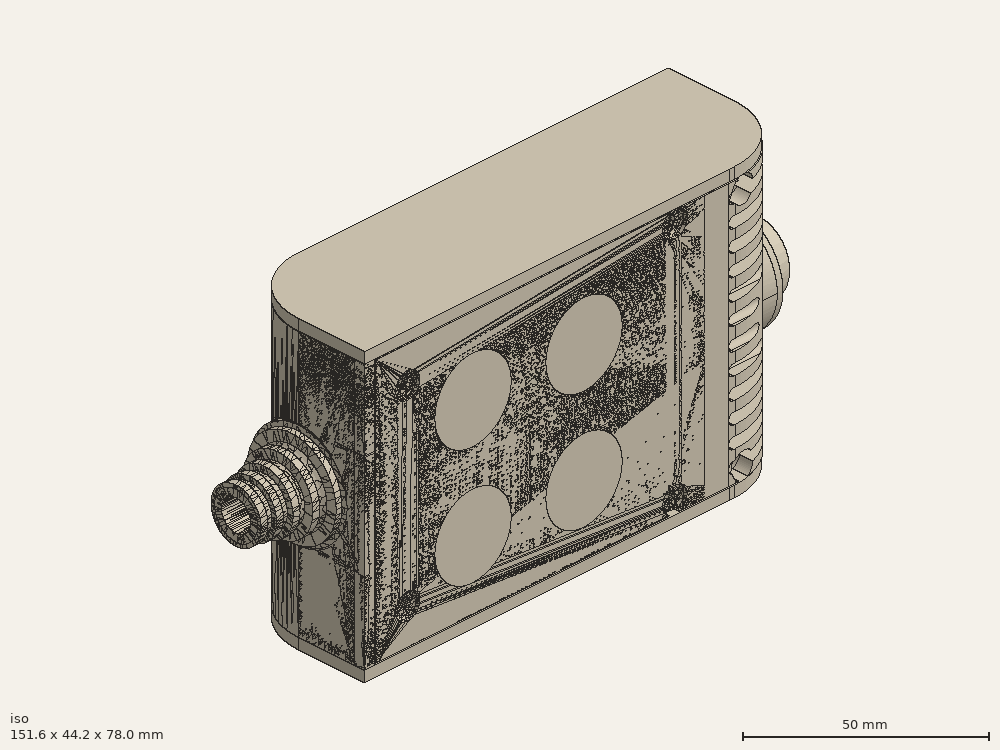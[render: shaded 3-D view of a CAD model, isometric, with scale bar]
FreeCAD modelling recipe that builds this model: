
FCSTD DOCUMENT  (FreeCAD 0.19R0.19.2)
Label: enclosure_200FCStd
License: All rights reserved
LicenseURL: http://en.wikipedia.org/wiki/All_rights_reserved
objects: Part::Revolution×152, Part::MultiFuse×146, Part::Feature×146, Sketcher::SketchObject×84, Part::Cut×70, Part::Cylinder×70, Part::Extrusion×67, Part::Fillet×58, Part::Box×36, App::MeasureDistance×4, PartDesign::Body×2, Image::ImagePlane×1
note: 831 computed .brp shape members not serialized (recipe doc carries the construction recipe); baked Part::Feature solids carry a one-line shape summary decoded from their .brp

FEATURE [Sketcher::SketchObject] Sketch  label="topSketch"
  FullyConstrained = true
  sketch-geometry (20):
    g0: LineSegment StartX=5.21097e-06 StartY=3 StartZ=0 EndX=5.21097e-06 EndY=19 EndZ=0
    g1: ArcOfCircle CenterX=19 CenterY=19 CenterZ=0 NormalX=0 NormalY=0 NormalZ=1 AngleXU=0 Radius=19 StartAngle=1.5708 EndAngle=3.14159
    g2: ArcOfCircle CenterX=19 CenterY=19 CenterZ=0 NormalX=0 NormalY=0 NormalZ=1 AngleXU=0 Radius=16 StartAngle=1.5708 EndAngle=3.14159
    g3: LineSegment StartX=114 StartY=35 StartZ=0 EndX=19 EndY=35 EndZ=0
    g4: LineSegment StartX=5.21097e-06 StartY=3 StartZ=0 EndX=5.21097e-06 EndY=0 EndZ=0
    g5: LineSegment StartX=3 StartY=0 StartZ=0 EndX=5.21097e-06 EndY=0 EndZ=0
    g6: LineSegment StartX=3 StartY=19 StartZ=0 EndX=3 EndY=0 EndZ=0
    g7: LineSegment StartX=19 StartY=38 StartZ=0 EndX=124 EndY=38 EndZ=0
    g8: Circle CenterX=119 CenterY=35 CenterZ=0 NormalX=0 NormalY=0 NormalZ=1 AngleXU=0 Radius=1
    g9: Circle CenterX=121 CenterY=35 CenterZ=0 NormalX=0 NormalY=0 NormalZ=1 AngleXU=0 Radius=1
    g10: Circle CenterX=121 CenterY=33 CenterZ=0 NormalX=0 NormalY=0 NormalZ=1 AngleXU=0 Radius=1
    g11: BSplineCurve PolesCount=3 KnotsCount=2 Degree=2 IsPeriodic=0
    g12: GeomPoint X=119 Y=35 Z=0
    g13: GeomPoint X=121 Y=33 Z=0
    g14: LineSegment StartX=119 StartY=35 StartZ=0 EndX=114 EndY=35 EndZ=0
    g15: ArcOfCircle CenterX=105 CenterY=19 CenterZ=0 NormalX=0 NormalY=0 NormalZ=1 AngleXU=0 Radius=19 StartAngle=5.7297 EndAngle=6.28319
    g16: ArcOfCircle CenterX=105 CenterY=19 CenterZ=0 NormalX=0 NormalY=0 NormalZ=1 AngleXU=0 Radius=16 StartAngle=5.60905 EndAngle=6.28319
    g17: LineSegment StartX=121 StartY=33 StartZ=0 EndX=121 EndY=19 EndZ=0
    g18: LineSegment StartX=124 StartY=38 StartZ=0 EndX=124 EndY=19 EndZ=0
    g19: LineSegment StartX=117.5 StartY=9.01251 StartZ=0 EndX=121.163 EndY=9.0125 EndZ=0
  constraints (46):
    c: Vertical(g0)
    c: Block(g0)
    c: Coincident(g1,g0)
    c: Block(g1)
    c: Coincident(g2,g1)
    c: Block(g2)
    c: Coincident(g3,g2)
    c: Horizontal(g3)
    c: Tangent(g3,g2)
    c: Coincident(g4,g0)
    c: Distance(g4) = 3
    c: Vertical(g4)
    c: Coincident(g5,g4)
    c: Horizontal(g5)
    c: Coincident(g6,g2)
    c: Coincident(g6,g5)
    c: Vertical(g6)
    c: Horizontal(g7)
    c: Distance(g7) = 105
    c: Coincident(g7,g1)
    c: Block(g3)
    c: Weight(g8) = 1
    c: Equal(g8,g9)
    c: Equal(g8,g10)
    c: InternalAlignment(g8,g11)
    c: InternalAlignment(g9,g11)
    c: InternalAlignment(g10,g11)
    c: InternalAlignment(g12,g11)
    c: InternalAlignment(g13,g11)
    c: Block(g11)
    c: Coincident(g14,g11)
    c: Coincident(g14,g3)
    c: Horizontal(g14)
    c: Block(g15)
    c: Coincident(g16,g15)
    c: Block(g16)
    c: Coincident(g17,g11)
    c: Coincident(g17,g16)
    c: Vertical(g17)
    c: Distance(g17) = 14
    c: Coincident(g18,g7)
    c: Coincident(g18,g15)
    c: Vertical(g18)
    c: Distance(g18) = 19
    c: Coincident(g19,g16)
    c: Coincident(g19,g15)
FEATURE [Sketcher::SketchObject] Sketch001  label="bottomSketch"
  FullyConstrained = true
  sketch-geometry (32):
    g0: LineSegment StartX=3.3 StartY=-6.03275e-07 StartZ=0 EndX=98 EndY=-6.03275e-07 EndZ=0
    g1: ArcOfCircle CenterX=98 CenterY=19 CenterZ=0 NormalX=0 NormalY=0 NormalZ=1 AngleXU=0 Radius=19 StartAngle=4.71239 EndAngle=5.71103
    g2: LineSegment StartX=6.3 StartY=8 StartZ=0 EndX=3.3 EndY=8 EndZ=0
    g3: LineSegment StartX=3.3 StartY=8 StartZ=0 EndX=3.3 EndY=-6.03275e-07 EndZ=0
    g4: ArcOfCircle CenterX=8.3 CenterY=5 CenterZ=0 NormalX=0 NormalY=0 NormalZ=1 AngleXU=0 Radius=2 StartAngle=3.14159 EndAngle=4.71239
    g5: LineSegment StartX=6.3 StartY=8 StartZ=0 EndX=6.3 EndY=5 EndZ=0
    g6: ArcOfCircle CenterX=98 CenterY=19 CenterZ=0 NormalX=0 NormalY=0 NormalZ=1 AngleXU=0 Radius=12.7 StartAngle=4.71239 EndAngle=6.28319
    g7: LineSegment StartX=94.7 StartY=3 StartZ=0 EndX=8.3 EndY=3 EndZ=0
    g8-g12: Circle x5 (B-spline internal-alignment scaffolding for g13; pole/knot coordinates omitted)
    g13: BSplineCurve PolesCount=5 KnotsCount=3 Degree=3 IsPeriodic=0
    g14: GeomPoint X=98 Y=6.3 Z=0
    g15: GeomPoint X=96.3938 Y=4.71946 Z=0
    g16: GeomPoint X=94.7 Y=3 Z=0
    g17-g23: Circle x7 (B-spline internal-alignment scaffolding for g24; pole/knot coordinates omitted)
    g24: BSplineCurve PolesCount=7 KnotsCount=5 Degree=3 IsPeriodic=0
    g25-g29: GeomPoint x5 (B-spline internal-alignment scaffolding for g24; pole/knot coordinates omitted)
    g30: ArcOfCircle CenterX=98 CenterY=19 CenterZ=0 NormalX=0 NormalY=0 NormalZ=1 AngleXU=0 Radius=15.7 StartAngle=5.81226 EndAngle=6.28319
    g31: LineSegment StartX=110.7 StartY=19 StartZ=0 EndX=113.7 EndY=19 EndZ=0
  constraints (41):
    c: Horizontal(g0)
    c: Coincident(g1,g0)
    c: Block(g1)
    c: Horizontal(g2)
    c: Distance(g2) = 3
    c: Coincident(g3,g2)
    c: Vertical(g3)
    c: Coincident(g3,g0)
    c: Block(g4)
    c: Block(g2)
    c: Coincident(g5,g2)
    c: Coincident(g5,g4)
    c: Vertical(g5)
    c: Coincident(g6,g1)
    c: Block(g6)
    c: Coincident(g7,g4)
    c: Horizontal(g7)
    c: Block(g0)
    c: Block(g7)
    c: Block(g3)
    c: Coincident(g13,g6)
    c: Weight(g8) = 1
    c: Equal(g8, g9-g12) x4
    c: Coincident(g13,g7)
    c: InternalAlignment(g8-g12 -> g13) x5
    c: InternalAlignment(g14,g13)
    c: InternalAlignment(g15,g13)
    c: InternalAlignment(g16,g13)
    c: Block(g13)
    c: Weight(g17) = 1
    c: Equal(g17, g18-g23) x6
    c: Coincident(g24,g1)
    c: InternalAlignment(g17-g23 -> g24) x7
    c: InternalAlignment(g25-g29 -> g24) x5
    c: Block(g24)
    c: Coincident(g30,g24)
    c: Coincident(g31,g6)
    c: Coincident(g31,g30)
    c: Horizontal(g31)
    c: Block(g31)
    c: Block(g30)
FEATURE [Part::Extrusion] Extrude  label="top"
  Base = -> Sketch
  Dir = (0,0,1)
  DirMode = 2
  FaceMakerClass = Part::FaceMakerBullseye
  LengthFwd = 72
  LengthRev = 0
  Solid = true
  Symmetric = false
FEATURE [Part::Extrusion] Extrude001  label="bottom"
  Base = -> Sketch001
  Dir = (0,0,1)
  DirMode = 2
  FaceMakerClass = Part::FaceMakerBullseye
  LengthFwd = 71.4
  LengthRev = 0
  Placement = pos=(0,0,0.3) rot=(0,0,1;0rad)
  Solid = true
  Symmetric = false
FEATURE [Sketcher::SketchObject] Sketch002  label="topSketch001"
  FullyConstrained = true
  sketch-geometry (8):
    g0: ArcOfCircle CenterX=19 CenterY=19.0975 CenterZ=0 NormalX=0 NormalY=0 NormalZ=1 AngleXU=0 Radius=18.9025 StartAngle=1.5708 EndAngle=3.14674
    g1: LineSegment StartX=0.0977805 StartY=19.0003 StartZ=0 EndX=0.0977805 EndY=0.000251602 EndZ=0
    g2: LineSegment StartX=19 StartY=38 StartZ=0 EndX=124 EndY=38 EndZ=0
    g3: LineSegment StartX=0.0977805 StartY=0.000251602 StartZ=0 EndX=105.098 EndY=0.000251602 EndZ=0
    g4: LineSegment StartX=124 StartY=38 StartZ=0 EndX=125.616 EndY=38 EndZ=0
    g5: LineSegment StartX=105.098 StartY=0.000251602 StartZ=0 EndX=106.713 EndY=0.000251602 EndZ=0
    g6: ArcOfCircle CenterX=106.616 CenterY=19 CenterZ=0 NormalX=0 NormalY=0 NormalZ=1 AngleXU=0 Radius=19 StartAngle=4.71754 EndAngle=6.28319
    g7: LineSegment StartX=125.616 StartY=38 StartZ=0 EndX=125.616 EndY=19 EndZ=0
  constraints (21):
    c: Block(g0)
    c: Coincident(g1,g0)
    c: Vertical(g1)
    c: Horizontal(g2)
    c: Distance(g2) = 105
    c: Coincident(g2,g0)
    c: Distance(g1) = 19
    c: Coincident(g3,g1)
    c: Horizontal(g3)
    c: Distance(g3) = 105
    c: Coincident(g4,g2)
    c: Horizontal(g4)
    c: Distance(g4) = 1.61553
    c: Horizontal(g5)
    c: Equal(g4,g5) = 1.61553
    c: Coincident(g5,g3)
    c: Block(g6)
    c: Coincident(g6,g5)
    c: Coincident(g7,g4)
    c: Coincident(g7,g6)
    c: Vertical(g7)
FEATURE [Part::Extrusion] Extrude002  label="sideA"
  Base = -> Sketch002
  Dir = (0,0,1)
  DirMode = 2
  FaceMakerClass = Part::FaceMakerBullseye
  LengthFwd = 3
  LengthRev = 0
  Placement = pos=(0,0,-3) rot=(0,0,1;0rad)
  Solid = true
  Symmetric = false
FEATURE [Sketcher::SketchObject] Sketch003  label="topSketch002"
  FullyConstrained = true
  sketch-geometry (6):
    g0: LineSegment StartX=19 StartY=38 StartZ=0 EndX=117 EndY=38 EndZ=0
    g1: ArcOfCircle CenterX=19 CenterY=19 CenterZ=0 NormalX=0 NormalY=0 NormalZ=1 AngleXU=0 Radius=19 StartAngle=1.5708 EndAngle=3.14159
    g2: LineSegment StartX=117 StartY=38 StartZ=0 EndX=117 EndY=19 EndZ=0
    g3: LineSegment StartX=98 StartY=1.0161e-12 StartZ=0 EndX=5.22862e-06 EndY=1.0161e-12 EndZ=0
    g4: LineSegment StartX=5.22862e-06 StartY=19 StartZ=0 EndX=5.22862e-06 EndY=1.0161e-12 EndZ=0
    g5: ArcOfCircle CenterX=98 CenterY=19 CenterZ=0 NormalX=0 NormalY=0 NormalZ=1 AngleXU=0 Radius=19 StartAngle=4.71239 EndAngle=6.28319
  constraints (16):
    c: Horizontal(g0)
    c: Distance(g0) = 98
    c: Coincident(g1,g0)
    c: Block(g1)
    c: Coincident(g2,g0)
    c: Vertical(g2)
    c: Distance(g2) = 19
    c: Horizontal(g3)
    c: Coincident(g4,g1)
    c: Vertical(g4)
    c: Coincident(g3,g4)
    c: Block(g3)
    c: Coincident(g5,g2)
    c: Coincident(g5,g3)
    c: Block(g0)
    c: Block(g5)
FEATURE [Sketcher::SketchObject] Sketch004
  FullyConstrained = true
  MapMode = 3
  Placement = pos=(0,0,0) rot=(1,0,0;1.5708rad)
  Support = -> [Extrude]
  sketch-geometry (8):
    g0: Circle CenterX=80.351 CenterY=-67.6202 CenterZ=0 NormalX=0 NormalY=0 NormalZ=1 AngleXU=0 Radius=2
    g1: Circle CenterX=80.351 CenterY=-67.6202 CenterZ=0 NormalX=0 NormalY=0 NormalZ=1 AngleXU=0 Radius=3
    g2: Circle CenterX=80.351 CenterY=-4.92017 CenterZ=0 NormalX=0 NormalY=0 NormalZ=1 AngleXU=0 Radius=2
    g3: Circle CenterX=80.351 CenterY=-4.92017 CenterZ=0 NormalX=0 NormalY=0 NormalZ=1 AngleXU=0 Radius=3
    g4: Circle CenterX=23.851 CenterY=-4.92017 CenterZ=0 NormalX=0 NormalY=0 NormalZ=1 AngleXU=0 Radius=2
    g5: Circle CenterX=23.851 CenterY=-4.92017 CenterZ=0 NormalX=0 NormalY=0 NormalZ=1 AngleXU=0 Radius=3
    g6: Circle CenterX=23.851 CenterY=-67.6202 CenterZ=0 NormalX=0 NormalY=0 NormalZ=1 AngleXU=0 Radius=2
    g7: Circle CenterX=23.851 CenterY=-67.6202 CenterZ=0 NormalX=0 NormalY=0 NormalZ=1 AngleXU=0 Radius=3
  constraints (8):
    c: Block(g3)
    c: Block(g2)
    c: Block(g1)
    c: Block(g0)
    c: Block(g6)
    c: Block(g7)
    c: Block(g4)
    c: Block(g5)
FEATURE [Part::Extrusion] Extrude004
  Base = -> Sketch004
  Dir = (0,-1,2e-16)
  DirMode = 2
  FaceMakerClass = Part::FaceMakerBullseye
  LengthFwd = 6
  LengthRev = 0
  Placement = pos=(0,9,0) rot=(0,0,1;0rad)
  Solid = true
  Symmetric = false
FEATURE [Sketcher::SketchObject] Sketch005
  FullyConstrained = true
  MapMode = 3
  Placement = pos=(0,0,0) rot=(1,0,0;1.5708rad)
  Support = -> [Extrude]
  sketch-geometry (8):
    g0: Circle CenterX=80.351 CenterY=-67.6202 CenterZ=0 NormalX=0 NormalY=0 NormalZ=1 AngleXU=0 Radius=3
    g1: Circle CenterX=80.351 CenterY=-4.92017 CenterZ=0 NormalX=0 NormalY=0 NormalZ=1 AngleXU=0 Radius=3
    g2: Circle CenterX=23.851 CenterY=-4.92017 CenterZ=0 NormalX=0 NormalY=0 NormalZ=1 AngleXU=0 Radius=3
    g3: Circle CenterX=23.851 CenterY=-67.6202 CenterZ=0 NormalX=0 NormalY=0 NormalZ=1 AngleXU=0 Radius=3
    g4: Circle CenterX=23.851 CenterY=-67.6202 CenterZ=0 NormalX=0 NormalY=0 NormalZ=1 AngleXU=0 Radius=5
    g5: Circle CenterX=80.351 CenterY=-67.6202 CenterZ=0 NormalX=0 NormalY=0 NormalZ=1 AngleXU=0 Radius=5
    g6: Circle CenterX=23.851 CenterY=-4.92017 CenterZ=0 NormalX=0 NormalY=0 NormalZ=1 AngleXU=0 Radius=5
    g7: Circle CenterX=80.351 CenterY=-4.92017 CenterZ=0 NormalX=0 NormalY=0 NormalZ=1 AngleXU=0 Radius=5
  constraints (8):
    c: Block(g1)
    c: Block(g0)
    c: Block(g3)
    c: Block(g2)
    c: Block(g5)
    c: Block(g4)
    c: Block(g6)
    c: Block(g7)
FEATURE [Part::Extrusion] Extrude005
  Base = -> Sketch005
  Dir = (0,-1,2e-16)
  DirMode = 2
  FaceMakerClass = Part::FaceMakerBullseye
  LengthFwd = 2
  LengthRev = 0
  Solid = true
  Symmetric = false
FEATURE [Sketcher::SketchObject] Sketch006
  FullyConstrained = true
  MapMode = 3
  Placement = pos=(0,0,0) rot=(1,0,0;1.5708rad)
  sketch-geometry (8):
    g0: Circle CenterX=80.351 CenterY=-67.6202 CenterZ=0 NormalX=0 NormalY=0 NormalZ=1 AngleXU=0 Radius=3
    g1: Circle CenterX=80.351 CenterY=-4.92017 CenterZ=0 NormalX=0 NormalY=0 NormalZ=1 AngleXU=0 Radius=3
    g2: Circle CenterX=23.851 CenterY=-4.92017 CenterZ=0 NormalX=0 NormalY=0 NormalZ=1 AngleXU=0 Radius=3
    g3: Circle CenterX=23.851 CenterY=-67.6202 CenterZ=0 NormalX=0 NormalY=0 NormalZ=1 AngleXU=0 Radius=3
    g4: Circle CenterX=23.851 CenterY=-67.6202 CenterZ=0 NormalX=0 NormalY=0 NormalZ=1 AngleXU=0 Radius=5
    g5: Circle CenterX=80.351 CenterY=-67.6202 CenterZ=0 NormalX=0 NormalY=0 NormalZ=1 AngleXU=0 Radius=5
    g6: Circle CenterX=23.851 CenterY=-4.92017 CenterZ=0 NormalX=0 NormalY=0 NormalZ=1 AngleXU=0 Radius=5
    g7: Circle CenterX=80.351 CenterY=-4.92017 CenterZ=0 NormalX=0 NormalY=0 NormalZ=1 AngleXU=0 Radius=5
  constraints (8):
    c: Block(g1)
    c: Block(g0)
    c: Block(g3)
    c: Block(g2)
    c: Block(g5)
    c: Block(g4)
    c: Block(g6)
    c: Block(g7)
FEATURE [Part::Extrusion] Extrude007
  Base = -> Sketch006
  Dir = (0,-1,2e-16)
  DirMode = 2
  FaceMakerClass = Part::FaceMakerBullseye
  LengthFwd = 2
  LengthRev = 0
  Solid = true
  Symmetric = false
FEATURE [Part::Fillet] Fillet
  Base = -> Extrude007
  Edges = 4 edges r=1.99: [Edge6,Edge12,Edge18,Edge24]
FEATURE [Part::Cut] Cut
  Base = -> Extrude005
  Placement = pos=(0,5,0) rot=(0,0,1;0rad)
  Tool = -> Fillet
FEATURE [Part::MultiFuse] Fusion  label="pCBScrews"
  Placement = pos=(-2.5,0,72.3) rot=(0,0,1;0rad)
  Shapes = -> [Extrude004,Cut]
FEATURE [App::MeasureDistance] Distance  label="Distance: 0.69 mm"
  Distance = 0.685967
  P1 = (24.0138,2.9647,0.3)
  P2 = (23.8901,3,-0.373787)
FEATURE [App::MeasureDistance] Distance001  label="Distance: 0.53 mm"
  Distance = 0.533607
  P1 = (80.2939,3,72.2334)
  P2 = (80.281,2.99661,71.7)
FEATURE [Part::Fillet] Fillet001
  Base = -> Extrude001
  Edges = 1 edges r=2.4: [Edge17]
FEATURE [Part::Fillet] Fillet002  label="bottom001"
  Base = -> Fillet001
  Edges = 1 edges r=2.4: [Edge36]
FEATURE [Part::Fillet] Fillet003  label="top001"
  Base = -> Extrude
  Edges = 1 edges r=2: [Edge1]
FEATURE [Sketcher::SketchObject] Sketch007
  FullyConstrained = true
  sketch-geometry (16):
    g0: LineSegment StartX=4 StartY=0 StartZ=0 EndX=4 EndY=2.4 EndZ=0
    g1: LineSegment StartX=4 StartY=2.4 StartZ=0 EndX=7 EndY=2.4 EndZ=0
    g2: LineSegment StartX=4 StartY=0 StartZ=0 EndX=5.7 EndY=0 EndZ=0
    g3: LineSegment StartX=5.7 StartY=0 StartZ=0 EndX=5.7 EndY=-5.6 EndZ=0
    g4-g8: Circle x5 (B-spline internal-alignment scaffolding for g9; pole/knot coordinates omitted)
    g9: BSplineCurve PolesCount=5 KnotsCount=3 Degree=3 IsPeriodic=0
    g10: GeomPoint X=7 Y=2.4 Z=0
    g11: GeomPoint X=10.4582 Y=-1.55472 Z=0
    g12: GeomPoint X=14 Y=-5.6 Z=0
    g13: LineSegment StartX=14 StartY=-5.6 StartZ=0 EndX=14 EndY=-14.1 EndZ=0
    g14: LineSegment StartX=14 StartY=-14.1 StartZ=0 EndX=6.5 EndY=-14.1 EndZ=0
    g15: LineSegment StartX=5.7 StartY=-5.6 StartZ=0 EndX=6.5 EndY=-14.1 EndZ=0
  constraints (28):
    c: Distance(g0) = 2.4
    c: Vertical(g0)
    c: Block(g0)
    c: Coincident(g1,g0)
    c: Horizontal(g1)
    c: Distance(g1) = 3
    c: Coincident(g2,g0)
    c: Horizontal(g2)
    c: Distance(g2) = 1.7
    c: Coincident(g3,g2)
    c: Vertical(g3)
    c: Distance(g3) = 5.6
    c: Coincident(g9,g1)
    c: Weight(g4) = 1
    c: Equal(g4, g5-g8) x4
    c: InternalAlignment(g4-g8 -> g9) x5
    c: InternalAlignment(g10,g9)
    c: InternalAlignment(g11,g9)
    c: InternalAlignment(g12,g9)
    c: Block(g9)
    c: Coincident(g13,g9)
    c: Vertical(g13)
    c: Distance(g13) = 8.5
    c: Coincident(g14,g13)
    c: Horizontal(g14)
    c: Distance(g14) = 7.5
    c: Coincident(g15,g3)
    c: Coincident(g15,g14)
FEATURE [Part::Feature] Face
  shape: bbox 10 x 16.5 x 2e-07 mm, 1 faces, 0 solids (baked)
FEATURE [Part::Revolution] Revolve  label="plugHousing"
  Angle = 360
  Axis = (0,1,0)
  Base = (0,0,0)
  FaceMakerClass = Part::FaceMakerBullseye
  Placement = pos=(0,0,36.15) rot=(0,0,1;0rad)
  Solid = false
  Source = -> Face
  Symmetric = false
FEATURE [Part::Feature] Face001
  shape: bbox 10 x 16.5 x 2e-07 mm, 1 faces, 0 solids (baked)
FEATURE [Part::Revolution] Revolve001  label="plugHousing001"
  Angle = 360
  Axis = (0,1,0)
  Base = (0,0,0)
  FaceMakerClass = Part::FaceMakerBullseye
  Placement = pos=(0,0,36.15) rot=(0,0,1;0rad)
  Solid = false
  Source = -> Face001
  Symmetric = false
FEATURE [Part::MultiFuse] Fusion001  label="plugHousing002"
  Placement = pos=(0,0,0) rot=(0,0,1;1.5708rad)
  Shapes = -> [Revolve001,Revolve]
FEATURE [Part::Feature] Face002
  shape: bbox 10 x 16.5 x 2e-07 mm, 1 faces, 0 solids (baked)
FEATURE [Part::Revolution] Revolve003  label="plugHousing005"
  Angle = 360
  Axis = (0,1,0)
  Base = (0,0,0)
  FaceMakerClass = Part::FaceMakerBullseye
  Placement = pos=(0,0,36.15) rot=(0,0,1;0rad)
  Solid = false
  Source = -> Face002
  Symmetric = false
FEATURE [Part::Feature] Face003
  shape: bbox 10 x 16.5 x 2e-07 mm, 1 faces, 0 solids (baked)
FEATURE [Part::Revolution] Revolve002  label="plugHousing003"
  Angle = 360
  Axis = (0,1,0)
  Base = (0,0,0)
  FaceMakerClass = Part::FaceMakerBullseye
  Placement = pos=(0,0,36.15) rot=(0,0,1;0rad)
  Solid = false
  Source = -> Face003
  Symmetric = false
FEATURE [Part::MultiFuse] Fusion002  label="plugHousing004"
  Placement = pos=(0,0,0) rot=(0,0,1;1.5708rad)
  Shapes = -> [Revolve002,Revolve003]
FEATURE [Part::MultiFuse] Fusion003  label="plugHousing006"
  Placement = pos=(0,19,0) rot=(0,0,1;3.14159rad)
  Shapes = -> [Fusion002,Fusion001]
FEATURE [Part::Feature] Face004
  shape: bbox 10 x 16.5 x 2e-07 mm, 1 faces, 0 solids (baked)
FEATURE [Part::Revolution] Revolve006  label="plugHousing010"
  Angle = 360
  Axis = (0,1,0)
  Base = (0,0,0)
  FaceMakerClass = Part::FaceMakerBullseye
  Placement = pos=(0,0,36.15) rot=(0,0,1;0rad)
  Solid = false
  Source = -> Face004
  Symmetric = false
FEATURE [Part::Feature] Face005
  shape: bbox 10 x 16.5 x 2e-07 mm, 1 faces, 0 solids (baked)
FEATURE [Part::Revolution] Revolve007  label="plugHousing011"
  Angle = 360
  Axis = (0,1,0)
  Base = (0,0,0)
  FaceMakerClass = Part::FaceMakerBullseye
  Placement = pos=(0,0,36.15) rot=(0,0,1;0rad)
  Solid = false
  Source = -> Face005
  Symmetric = false
FEATURE [Part::Feature] Face006
  shape: bbox 10 x 16.5 x 2e-07 mm, 1 faces, 0 solids (baked)
FEATURE [Part::Revolution] Revolve004  label="plugHousing007"
  Angle = 360
  Axis = (0,1,0)
  Base = (0,0,0)
  FaceMakerClass = Part::FaceMakerBullseye
  Placement = pos=(0,0,36.15) rot=(0,0,1;0rad)
  Solid = false
  Source = -> Face006
  Symmetric = false
FEATURE [Part::MultiFuse] Fusion004  label="plugHousing009"
  Placement = pos=(0,0,0) rot=(0,0,1;1.5708rad)
  Shapes = -> [Revolve004,Revolve007]
FEATURE [Part::Feature] Face007
  shape: bbox 10 x 16.5 x 2e-07 mm, 1 faces, 0 solids (baked)
FEATURE [Part::Revolution] Revolve005  label="plugHousing008"
  Angle = 360
  Axis = (0,1,0)
  Base = (0,0,0)
  FaceMakerClass = Part::FaceMakerBullseye
  Placement = pos=(0,0,36.15) rot=(0,0,1;0rad)
  Solid = false
  Source = -> Face007
  Symmetric = false
FEATURE [Part::MultiFuse] Fusion005  label="plugHousing012"
  Placement = pos=(0,0,0) rot=(0,0,1;1.5708rad)
  Shapes = -> [Revolve006,Revolve005]
FEATURE [Part::MultiFuse] Fusion006  label="plugHousing013"
  Placement = pos=(0,19,0) rot=(0,0,1;3.14159rad)
  Shapes = -> [Fusion005,Fusion004]
FEATURE [Part::MultiFuse] Fusion007  label="plugHousing014"
  Placement = pos=(122.621,0,-0.15) rot=(0,0,1;0rad)
  Shapes = -> [Fusion003,Fusion006]
FEATURE [Part::Cylinder] Cylinder002
  Angle = 360
  AttacherType = Attacher::AttachEngine3D
  Height = 20
  Placement = pos=(0,0,36.15) rot=(0,0,1;0rad)
  Radius = 4
FEATURE [Part::Cylinder] Cylinder003
  Angle = 360
  AttacherType = Attacher::AttachEngine3D
  Height = 10
  Placement = pos=(0,0,36.15) rot=(0,0,1;0rad)
  Radius = 4
FEATURE [Part::MultiFuse] Fusion009  label="removeToCreateHoleForPlugHousing"
  Placement = pos=(70,19,36.15) rot=(0,1,0;1.5708rad)
  Shapes = -> [Cylinder002,Cylinder003]
FEATURE [Part::Cylinder] Cylinder004
  Angle = 360
  AttacherType = Attacher::AttachEngine3D
  Height = 20
  Placement = pos=(0,0,36.15) rot=(0,0,1;0rad)
  Radius = 4
FEATURE [Part::Cylinder] Cylinder005
  Angle = 360
  AttacherType = Attacher::AttachEngine3D
  Height = 10
  Placement = pos=(0,0,36.15) rot=(0,0,1;0rad)
  Radius = 4
FEATURE [Part::MultiFuse] Fusion010  label="removeToCreateHoleForPlugHousing001"
  Placement = pos=(70,19,36.15) rot=(0,1,0;1.5708rad)
  Shapes = -> [Cylinder004,Cylinder005]
FEATURE [Part::Cut] Cut001
  Base = -> Fillet003
  Tool = -> Fusion010
FEATURE [Part::Cut] Cut002  label="Bottom"
  Base = -> Fillet002
  Tool = -> Fusion009
FEATURE [Part::Feature] Face008
  shape: bbox 10 x 16.5 x 2e-07 mm, 1 faces, 0 solids (baked)
FEATURE [Part::Revolution] Revolve011  label="plugHousing021"
  Angle = 360
  Axis = (0,1,0)
  Base = (0,0,0)
  FaceMakerClass = Part::FaceMakerBullseye
  Placement = pos=(0,0,36.15) rot=(0,0,1;0rad)
  Solid = false
  Source = -> Face008
  Symmetric = false
FEATURE [Part::Feature] Face009
  shape: bbox 10 x 16.5 x 2e-07 mm, 1 faces, 0 solids (baked)
FEATURE [Part::Revolution] Revolve012  label="plugHousing022"
  Angle = 360
  Axis = (0,1,0)
  Base = (0,0,0)
  FaceMakerClass = Part::FaceMakerBullseye
  Placement = pos=(0,0,36.15) rot=(0,0,1;0rad)
  Solid = false
  Source = -> Face009
  Symmetric = false
FEATURE [Part::Feature] Face010 .. Face013  x4 (patterned run collapsed; names and placements below)
  shape: bbox 10 x 16.5 x 2e-07 mm, 1 faces, 0 solids (baked)
FEATURE [Part::Revolution] Revolve015  label="plugHousing027"
  Angle = 360
  Axis = (0,1,0)
  Base = (0,0,0)
  FaceMakerClass = Part::FaceMakerBullseye
  Placement = pos=(0,0,36.15) rot=(0,0,1;0rad)
  Solid = false
  Source = -> Face013
  Symmetric = false
FEATURE [Part::Feature] Face014
  shape: bbox 10 x 16.5 x 2e-07 mm, 1 faces, 0 solids (baked)
FEATURE [Part::Feature] Face015
  shape: bbox 10 x 16.5 x 2e-07 mm, 1 faces, 0 solids (baked)
FEATURE [Part::Feature] Face016
  shape: bbox 10 x 16.5 x 2e-07 mm, 1 faces, 0 solids (baked)
FEATURE [Part::Revolution] Revolve019  label="plugHousing033"
  Angle = 360
  Axis = (0,1,0)
  Base = (0,0,0)
  FaceMakerClass = Part::FaceMakerBullseye
  Placement = pos=(0,0,36.15) rot=(0,0,1;0rad)
  Solid = false
  Source = -> Face016
  Symmetric = false
FEATURE [Part::Feature] Face017
  shape: bbox 10 x 16.5 x 2e-07 mm, 1 faces, 0 solids (baked)
FEATURE [Part::Revolution] Revolve020  label="plugHousing034"
  Angle = 360
  Axis = (0,1,0)
  Base = (0,0,0)
  FaceMakerClass = Part::FaceMakerBullseye
  Placement = pos=(0,0,36.15) rot=(0,0,1;0rad)
  Solid = false
  Source = -> Face017
  Symmetric = false
FEATURE [Part::Feature] Face018
  shape: bbox 10 x 16.5 x 2e-07 mm, 1 faces, 0 solids (baked)
FEATURE [Part::Revolution] Revolve016  label="plugHousing030"
  Angle = 360
  Axis = (0,1,0)
  Base = (0,0,0)
  FaceMakerClass = Part::FaceMakerBullseye
  Placement = pos=(0,0,36.15) rot=(0,0,1;0rad)
  Solid = false
  Source = -> Face018
  Symmetric = false
FEATURE [Part::MultiFuse] Fusion020  label="plugHousing038"
  Placement = pos=(0,0,0) rot=(0,0,1;1.5708rad)
  Shapes = -> [Revolve016,Revolve020]
FEATURE [Part::Feature] Face019
  shape: bbox 10 x 16.5 x 2e-07 mm, 1 faces, 0 solids (baked)
FEATURE [Part::Feature] Face020
  shape: bbox 10 x 16.5 x 2e-07 mm, 1 faces, 0 solids (baked)
FEATURE [Part::Revolution] Revolve017  label="plugHousing031"
  Angle = 360
  Axis = (0,1,0)
  Base = (0,0,0)
  FaceMakerClass = Part::FaceMakerBullseye
  Placement = pos=(0,0,36.15) rot=(0,0,1;0rad)
  Solid = false
  Source = -> Face020
  Symmetric = false
FEATURE [Part::MultiFuse] Fusion021  label="plugHousing039"
  Placement = pos=(0,0,0) rot=(0,0,1;1.5708rad)
  Shapes = -> [Revolve019,Revolve017]
FEATURE [Part::MultiFuse] Fusion023  label="plugHousing041"
  Placement = pos=(0,19,0) rot=(0,0,1;3.14159rad)
  Shapes = -> [Fusion021,Fusion020]
FEATURE [Part::Revolution] Revolve022  label="plugHousing043"
  Angle = 360
  Axis = (0,1,0)
  Base = (0,0,0)
  FaceMakerClass = Part::FaceMakerBullseye
  Placement = pos=(0,0,36.15) rot=(0,0,1;0rad)
  Solid = false
  Source = -> Face019
  Symmetric = false
FEATURE [Part::Feature] Face021
  shape: bbox 10 x 16.5 x 2e-07 mm, 1 faces, 0 solids (baked)
FEATURE [Part::Revolution] Revolve023  label="plugHousing044"
  Angle = 360
  Axis = (0,1,0)
  Base = (0,0,0)
  FaceMakerClass = Part::FaceMakerBullseye
  Placement = pos=(0,0,36.15) rot=(0,0,1;0rad)
  Solid = false
  Source = -> Face021
  Symmetric = false
FEATURE [Part::Feature] Face022
  shape: bbox 10 x 16.5 x 2e-07 mm, 1 faces, 0 solids (baked)
FEATURE [Part::Revolution] Revolve018  label="plugHousing032"
  Angle = 360
  Axis = (0,1,0)
  Base = (0,0,0)
  FaceMakerClass = Part::FaceMakerBullseye
  Placement = pos=(0,0,36.15) rot=(0,0,1;0rad)
  Solid = false
  Source = -> Face022
  Symmetric = false
FEATURE [Part::MultiFuse] Fusion022  label="plugHousing040"
  Placement = pos=(0,0,0) rot=(0,0,1;1.5708rad)
  Shapes = -> [Revolve018,Revolve023]
FEATURE [Part::Feature] Face023
  shape: bbox 10 x 16.5 x 2e-07 mm, 1 faces, 0 solids (baked)
FEATURE [Part::Revolution] Revolve021  label="plugHousing035"
  Angle = 360
  Axis = (0,1,0)
  Base = (0,0,0)
  FaceMakerClass = Part::FaceMakerBullseye
  Placement = pos=(0,0,36.15) rot=(0,0,1;0rad)
  Solid = false
  Source = -> Face023
  Symmetric = false
FEATURE [Part::MultiFuse] Fusion018  label="plugHousing036"
  Placement = pos=(0,0,0) rot=(0,0,1;1.5708rad)
  Shapes = -> [Revolve022,Revolve021]
FEATURE [Part::MultiFuse] Fusion019  label="plugHousing037"
  Placement = pos=(0,19,0) rot=(0,0,1;3.14159rad)
  Shapes = -> [Fusion018,Fusion022]
FEATURE [Part::MultiFuse] Fusion024  label="plugHousing042"
  Placement = pos=(122.621,0,-0.15) rot=(0,0,1;0rad)
  Shapes = -> [Fusion023,Fusion019]
FEATURE [Part::Cylinder] Cylinder006
  Angle = 360
  AttacherType = Attacher::AttachEngine3D
  Height = 20
  Placement = pos=(0,0,36.15) rot=(0,0,1;0rad)
  Radius = 14.3
FEATURE [Part::Cylinder] Cylinder007
  Angle = 360
  AttacherType = Attacher::AttachEngine3D
  Height = 10
  Placement = pos=(0,0,36.15) rot=(0,0,1;0rad)
  Radius = 4
FEATURE [Part::MultiFuse] Fusion026  label="removeToCreteHoleForPlugHousing"
  Placement = pos=(70,19,36) rot=(0,1,0;1.5708rad)
  Shapes = -> [Cylinder006,Cylinder007]
FEATURE [Part::Box] Box001  label="Cube001"
  AttacherType = Attacher::AttachEngine3D
  Height = 28
  Length = 3
  Placement = pos=(110.7,19,22) rot=(0,0,1;0rad)
  Width = 15.7
FEATURE [Part::Cut] Cut003  label="top002"
  Base = -> Cut001
  Tool = -> Fusion007
FEATURE [Part::Revolution] Revolve008  label="plugHousing015"
  Angle = 360
  Axis = (0,1,0)
  Base = (0,0,0)
  FaceMakerClass = Part::FaceMakerBullseye
  Placement = pos=(0,0,36.15) rot=(0,0,1;0rad)
  Solid = false
  Source = -> Face010
  Symmetric = false
FEATURE [Part::MultiFuse] Fusion013  label="plugHousing020"
  Placement = pos=(0,0,0) rot=(0,0,1;1.5708rad)
  Shapes = -> [Revolve008,Revolve012]
FEATURE [Part::Cut] Cut004  label="top003"
  Base = -> Cut003
  Placement = pos=(1,0,0) rot=(0,0,1;0rad)
  Tool = -> Fusion026
FEATURE [Part::Cylinder] Cylinder008
  Angle = 360
  AttacherType = Attacher::AttachEngine3D
  Height = 20
  Placement = pos=(0,0,36.15) rot=(0,0,1;0rad)
  Radius = 10.3
FEATURE [Part::Cylinder] Cylinder009
  Angle = 360
  AttacherType = Attacher::AttachEngine3D
  Height = 10
  Placement = pos=(0,0,36.15) rot=(0,0,1;0rad)
  Radius = 4
FEATURE [Part::MultiFuse] Fusion027  label="removeToCreteHoleForPlugHousing001"
  Placement = pos=(70,19,36) rot=(0,1,0;1.5708rad)
  Shapes = -> [Cylinder008,Cylinder009]
FEATURE [Part::Cut] Cut005  label="plugHousingTab"
  Base = -> Box001
  Tool = -> Fusion027
FEATURE [Part::MultiFuse] Fusion028  label="plugHousing045"
  Shapes = -> [Fusion024,Cut005]
FEATURE [Part::Box] Box002  label="Cube002"
  AttacherType = Attacher::AttachEngine3D
  Height = 28.8
  Length = 3
  Placement = pos=(107.3,28,21.6) rot=(0,0,1;0rad)
  Width = 7
FEATURE [Part::Box] Box003  label="Cube003"
  AttacherType = Attacher::AttachEngine3D
  Height = 3
  Length = 6.4
  Placement = pos=(107.3,28,18.6) rot=(0,0,1;0rad)
  Width = 7
FEATURE [Part::Box] Box004  label="Cube004"
  AttacherType = Attacher::AttachEngine3D
  Height = 3
  Length = 6.4
  Placement = pos=(107.3,28,50.4) rot=(0,0,1;0rad)
  Width = 7
FEATURE [Part::MultiFuse] Fusion029  label="plugHousingBracketHolder"
  Shapes = -> [Box004,Box002,Box003]
FEATURE [Part::Cylinder] Cylinder010
  Angle = 360
  AttacherType = Attacher::AttachEngine3D
  Height = 20
  Placement = pos=(0,0,36.15) rot=(0,0,1;0rad)
  Radius = 14.3
FEATURE [Part::Cylinder] Cylinder011
  Angle = 360
  AttacherType = Attacher::AttachEngine3D
  Height = 10
  Placement = pos=(0,0,36.15) rot=(0,0,1;0rad)
  Radius = 4
FEATURE [Part::MultiFuse] Fusion030  label="removeToCreteHoleForPlugHousing002"
  Placement = pos=(70,19,36) rot=(0,1,0;1.5708rad)
  Shapes = -> [Cylinder010,Cylinder011]
FEATURE [Part::Cut] Cut006  label="plugHousingBracketHolder001"
  Base = -> Fusion029
  Tool = -> Fusion030
FEATURE [Part::Cylinder] Cylinder012
  Angle = 360
  AttacherType = Attacher::AttachEngine3D
  Height = 20
  Placement = pos=(0,0,36.15) rot=(0,0,1;0rad)
  Radius = 7
FEATURE [Part::Cylinder] Cylinder013
  Angle = 360
  AttacherType = Attacher::AttachEngine3D
  Height = 10
  Placement = pos=(0,0,36.15) rot=(0,0,1;0rad)
  Radius = 4
FEATURE [Part::MultiFuse] Fusion032  label="removeToCreteHoleForPlugHousing003"
  Placement = pos=(70,19,36) rot=(0,1,0;1.5708rad)
  Shapes = -> [Cylinder012,Cylinder013]
FEATURE [Part::Cut] Cut007  label="bottom002"
  Base = -> Cut002
  Tool = -> Fusion032
FEATURE [Sketcher::SketchObject] Sketch008
  FullyConstrained = true
  sketch-geometry (54):
    g0: LineSegment StartX=-4.2 StartY=0 StartZ=0 EndX=-6.2 EndY=0 EndZ=0
    g1: LineSegment StartX=-14 StartY=-18 StartZ=0 EndX=-14 EndY=-26.5 EndZ=0
    g2: LineSegment StartX=-4.2 StartY=0 StartZ=0 EndX=-4.2 EndY=-13.4877 EndZ=0
    g3: Circle CenterX=-4.2 CenterY=-13.4877 CenterZ=0 NormalX=0 NormalY=0 NormalZ=1 AngleXU=0 Radius=1
    g4: Circle CenterX=-4.2 CenterY=-26.5 CenterZ=0 NormalX=0 NormalY=0 NormalZ=1 AngleXU=0 Radius=1
    g5: Circle CenterX=-8.2 CenterY=-26.5 CenterZ=0 NormalX=0 NormalY=0 NormalZ=1 AngleXU=0 Radius=1
    g6: BSplineCurve PolesCount=3 KnotsCount=2 Degree=2 IsPeriodic=0
    g7: GeomPoint X=-4.2 Y=-13.4877 Z=0
    g8: GeomPoint X=-8.2 Y=-26.5 Z=0
    g9: LineSegment StartX=-14 StartY=-26.5 StartZ=0 EndX=-8.2 EndY=-26.5 EndZ=0
    g10: LineSegment StartX=-10.15 StartY=-12 StartZ=0 EndX=-10.15 EndY=-14 EndZ=0
    g11: LineSegment StartX=-12.8401 StartY=-16 StartZ=0 EndX=-10.1571 EndY=-16 EndZ=0
    g12: LineSegment StartX=-10.15 StartY=-14 StartZ=0 EndX=-8.70761 EndY=-14 EndZ=0
    g13: LineSegment StartX=-12.8401 StartY=-16 StartZ=0 EndX=-12.8401 EndY=-17.6958 EndZ=0
    g14: LineSegment StartX=-10.15 StartY=-12 StartZ=0 EndX=-7.79258 EndY=-12 EndZ=0
    g15: Circle CenterX=-6.2215 CenterY=-2 CenterZ=0 NormalX=0 NormalY=0 NormalZ=1 AngleXU=0 Radius=1
    g16: Circle CenterX=-6.22762 CenterY=-2.58724 CenterZ=0 NormalX=0 NormalY=0 NormalZ=1 AngleXU=0 Radius=1
    g17: Circle CenterX=-6.32538 CenterY=-4 CenterZ=0 NormalX=0 NormalY=0 NormalZ=1 AngleXU=0 Radius=1
    g18: BSplineCurve PolesCount=3 KnotsCount=2 Degree=2 IsPeriodic=0
    g19: GeomPoint X=-6.2215 Y=-2 Z=0
    g20: GeomPoint X=-6.32538 Y=-4 Z=0
    g21: Circle CenterX=-6.48644 CenterY=-5.99526 CenterZ=0 NormalX=0 NormalY=0 NormalZ=1 AngleXU=0 Radius=1
    g22: Circle CenterX=-6.58486 CenterY=-6.99526 CenterZ=0 NormalX=0 NormalY=0 NormalZ=1 AngleXU=0 Radius=1
    g23: Circle CenterX=-6.77343 CenterY=-8 CenterZ=0 NormalX=0 NormalY=0 NormalZ=1 AngleXU=0 Radius=1
    g24: BSplineCurve PolesCount=3 KnotsCount=2 Degree=2 IsPeriodic=0
    g25: GeomPoint X=-6.48644 Y=-5.99526 Z=0
    g26: GeomPoint X=-6.77343 Y=-8 Z=0
    g27: Circle CenterX=-7.19003 CenterY=-10 CenterZ=0 NormalX=0 NormalY=0 NormalZ=1 AngleXU=0 Radius=1
    g28: Circle CenterX=-7.44407 CenterY=-11.0915 CenterZ=0 NormalX=0 NormalY=0 NormalZ=1 AngleXU=0 Radius=1
    g29: Circle CenterX=-7.79258 CenterY=-12 CenterZ=0 NormalX=0 NormalY=0 NormalZ=1 AngleXU=0 Radius=1
    g30: BSplineCurve PolesCount=3 KnotsCount=2 Degree=2 IsPeriodic=0
    g31: GeomPoint X=-7.19003 Y=-10 Z=0
    g32: GeomPoint X=-7.79258 Y=-12 Z=0
    g33: Circle CenterX=-8.70761 CenterY=-14 CenterZ=0 NormalX=0 NormalY=0 NormalZ=1 AngleXU=0 Radius=1
    g34: Circle CenterX=-9.33087 CenterY=-15.1837 CenterZ=0 NormalX=0 NormalY=0 NormalZ=1 AngleXU=0 Radius=1
    g35: Circle CenterX=-10.1571 CenterY=-16 CenterZ=0 NormalX=0 NormalY=0 NormalZ=1 AngleXU=0 Radius=1
    g36: BSplineCurve PolesCount=3 KnotsCount=2 Degree=2 IsPeriodic=0
    g37: GeomPoint X=-8.70761 Y=-14 Z=0
    g38: GeomPoint X=-10.1571 Y=-16 Z=0
    g39: Circle CenterX=-12.8401 CenterY=-17.6958 CenterZ=0 NormalX=0 NormalY=0 NormalZ=1 AngleXU=0 Radius=1
    g40: Circle CenterX=-13.3521 CenterY=-17.9027 CenterZ=0 NormalX=0 NormalY=0 NormalZ=1 AngleXU=0 Radius=1
    g41: Circle CenterX=-14 CenterY=-18 CenterZ=0 NormalX=0 NormalY=0 NormalZ=1 AngleXU=0 Radius=1
    g42: BSplineCurve PolesCount=3 KnotsCount=2 Degree=2 IsPeriodic=0
    g43: GeomPoint X=-12.8401 Y=-17.6958 Z=0
    g44: GeomPoint X=-14 Y=-18 Z=0
    g45: LineSegment StartX=-6.2 StartY=0 StartZ=0 EndX=-7.2 EndY=0 EndZ=0
    g46: LineSegment StartX=-7.2 StartY=0 StartZ=0 EndX=-7.2 EndY=-2 EndZ=0
    g47: LineSegment StartX=-7.2 StartY=-2 StartZ=0 EndX=-6.2215 EndY=-2 EndZ=0
    g48: LineSegment StartX=-6.32538 StartY=-4 StartZ=0 EndX=-7.65538 EndY=-4 EndZ=0
    g49: LineSegment StartX=-7.65538 StartY=-4 StartZ=0 EndX=-7.65538 EndY=-5.99526 EndZ=0
    g50: LineSegment StartX=-7.65538 StartY=-5.99526 StartZ=0 EndX=-6.48644 EndY=-5.99526 EndZ=0
    g51: LineSegment StartX=-6.77343 StartY=-8 StartZ=0 EndX=-8.43343 EndY=-8 EndZ=0
    g52: LineSegment StartX=-8.43343 StartY=-8 StartZ=0 EndX=-8.43343 EndY=-10 EndZ=0
    g53: LineSegment StartX=-8.43343 StartY=-10 StartZ=0 EndX=-7.19003 EndY=-10 EndZ=0
  constraints (112):
    c: Horizontal(g0)
    c: Distance(g0) = 2
    c: Block(g0)
    c: Vertical(g1)
    c: Coincident(g2,g0)
    c: Vertical(g2)
    c: Block(g2)
    c: Coincident(g6,g2)
    c: Weight(g3) = 1
    c: Equal(g3,g4)
    c: Equal(g3,g5)
    c: InternalAlignment(g3,g6)
    c: InternalAlignment(g4,g6)
    c: InternalAlignment(g5,g6)
    c: InternalAlignment(g7,g6)
    c: InternalAlignment(g8,g6)
    c: Block(g6)
    c: Coincident(g9,g1)
    c: Coincident(g9,g6)
    c: Horizontal(g9)
    c: Vertical(g10)
    c: Block(g10)
    c: Horizontal(g11)
    c: Block(g11)
    c: Coincident(g12,g10)
    c: Horizontal(g12)
    c: Block(g12)
    c: Coincident(g13,g11)
    c: Vertical(g13)
    c: Block(g13)
    c: Coincident(g14,g10)
    c: Horizontal(g14)
    c: Block(g14)
    c: Block(g9)
    c: Block(g1)
    c: Weight(g15) = 1
    c: Equal(g15,g16)
    c: Equal(g15,g17)
    c: InternalAlignment(g15,g18)
    c: InternalAlignment(g16,g18)
    c: InternalAlignment(g17,g18)
    c: InternalAlignment(g19,g18)
    c: InternalAlignment(g20,g18)
    c: Weight(g21) = 1
    c: Equal(g21,g22)
    c: Equal(g21,g23)
    c: InternalAlignment(g21,g24)
    c: InternalAlignment(g22,g24)
    c: InternalAlignment(g23,g24)
    c: InternalAlignment(g25,g24)
    c: InternalAlignment(g26,g24)
    c: Weight(g27) = 1
    c: Equal(g27,g28)
    c: Equal(g27,g29)
    c: Coincident(g30,g14)
    c: InternalAlignment(g27,g30)
    c: InternalAlignment(g28,g30)
    c: InternalAlignment(g29,g30)
    c: InternalAlignment(g31,g30)
    c: InternalAlignment(g32,g30)
    c: Coincident(g36,g12)
    c: Weight(g33) = 1
    c: Equal(g33,g34)
    c: Equal(g33,g35)
    c: Coincident(g36,g11)
    c: InternalAlignment(g33,g36)
    c: InternalAlignment(g34,g36)
    c: InternalAlignment(g35,g36)
    c: InternalAlignment(g37,g36)
    c: InternalAlignment(g38,g36)
    c: Coincident(g42,g13)
    c: Weight(g39) = 1
    c: Equal(g39,g40)
    c: Equal(g39,g41)
    c: Coincident(g42,g1)
    c: InternalAlignment(g39,g42)
    c: InternalAlignment(g40,g42)
    c: InternalAlignment(g41,g42)
    c: InternalAlignment(g43,g42)
    c: InternalAlignment(g44,g42)
    c: Block(g18)
    c: Block(g24)
    c: Block(g30)
    c: Block(g36)
    c: Block(g42)
    c: Horizontal(g45)
    c: Coincident(g45,g0)
    c: Vertical(g46)
    c: Coincident(g46,g45)
    c: Coincident(g47,g46)
    c: Coincident(g47,g18)
    c: Horizontal(g47)
    c: Block(g46)
    c: Coincident(g48,g18)
    c: Horizontal(g48)
    c: Distance(g48) = 1.33
    c: Vertical(g49)
    c: Coincident(g49,g48)
    c: Coincident(g50,g49)
    c: Coincident(g50,g24)
    c: Horizontal(g50)
    c: Tangent(g50,g22)
    c: Horizontal(g51)
    c: Coincident(g51,g24)
    c: Block(g51)
    c: Vertical(g52)
    c: Block(g52)
    c: Coincident(g52,g51)
    c: Coincident(g53,g52)
    c: Coincident(g53,g30)
    c: Horizontal(g53)
    c: Distance(g1) = 8.5
FEATURE [Part::Feature] Face024
  shape: bbox 9.8 x 26.5 x 2e-07 mm, 1 faces, 0 solids (baked)
FEATURE [Part::Revolution] Revolve024
  Angle = 360
  Axis = (0,1,0)
  Base = (0,0,0)
  FaceMakerClass = Part::FaceMakerBullseye
  Placement = pos=(0,0,0) rot=(0,0,1;1.5708rad)
  Solid = false
  Source = -> Face024
  Symmetric = false
FEATURE [Part::Feature] Face025
  shape: bbox 9.8 x 26.5 x 2e-07 mm, 1 faces, 0 solids (baked)
FEATURE [Part::Revolution] Revolve025
  Angle = 360
  Axis = (0,1,0)
  Base = (0,0,0)
  FaceMakerClass = Part::FaceMakerBullseye
  Placement = pos=(0,0,0) rot=(0,0,1;1.5708rad)
  Solid = false
  Source = -> Face025
  Symmetric = false
FEATURE [Part::MultiFuse] Fusion033
  Placement = pos=(-18,19,36) rot=(0,0,1;0rad)
  Shapes = -> [Revolve025,Revolve024]
FEATURE [Part::Cylinder] Cylinder014
  Angle = 360
  AttacherType = Attacher::AttachEngine3D
  Height = 20
  Placement = pos=(0,0,36.15) rot=(0,0,1;0rad)
  Radius = 14.3
FEATURE [Part::Cylinder] Cylinder015
  Angle = 360
  AttacherType = Attacher::AttachEngine3D
  Height = 10
  Placement = pos=(0,0,36.15) rot=(0,0,1;0rad)
  Radius = 4
FEATURE [Part::MultiFuse] Fusion034  label="removeToCreteHoleForPlugHousing004"
  Placement = pos=(-42,19,36) rot=(0,1,0;1.5708rad)
  Shapes = -> [Cylinder014,Cylinder015]
FEATURE [Part::Cut] Cut008  label="top004"
  Base = -> Cut004
  Placement = pos=(-1,0,0) rot=(0,0,1;0rad)
  Tool = -> Fusion034
FEATURE [Part::Box] Box005  label="Cube005"
  AttacherType = Attacher::AttachEngine3D
  Height = 28
  Length = 3
  Placement = pos=(110.7,19,22) rot=(0,0,1;0rad)
  Width = 15.7
FEATURE [Part::Cylinder] Cylinder016
  Angle = 360
  AttacherType = Attacher::AttachEngine3D
  Height = 10
  Placement = pos=(0,0,36.15) rot=(0,0,1;0rad)
  Radius = 4
FEATURE [Part::Cylinder] Cylinder017
  Angle = 360
  AttacherType = Attacher::AttachEngine3D
  Height = 20
  Placement = pos=(0,0,36.15) rot=(0,0,1;0rad)
  Radius = 10.3
FEATURE [Part::MultiFuse] Fusion035  label="removeToCreteHoleForPlugHousing005"
  Placement = pos=(70,19,36) rot=(0,1,0;1.5708rad)
  Shapes = -> [Cylinder017,Cylinder016]
FEATURE [Part::Cut] Cut009  label="plugHousingTab001"
  Base = -> Box005
  Placement = pos=(-107.4,-14,0) rot=(0,0,1;0rad)
  Tool = -> Fusion035
FEATURE [Part::Box] Box006  label="Cube006"
  AttacherType = Attacher::AttachEngine3D
  Height = 28
  Length = 3
  Placement = pos=(110.7,19,22) rot=(0,0,1;0rad)
  Width = 15.7
FEATURE [Part::Cylinder] Cylinder018
  Angle = 360
  AttacherType = Attacher::AttachEngine3D
  Height = 10
  Placement = pos=(0,0,36.15) rot=(0,0,1;0rad)
  Radius = 4
FEATURE [Part::Cylinder] Cylinder019
  Angle = 360
  AttacherType = Attacher::AttachEngine3D
  Height = 20
  Placement = pos=(0,0,36.15) rot=(0,0,1;0rad)
  Radius = 10.3
FEATURE [Part::MultiFuse] Fusion036  label="removeToCreteHoleForPlugHousing006"
  Placement = pos=(70,19,36) rot=(0,1,0;1.5708rad)
  Shapes = -> [Cylinder019,Cylinder018]
FEATURE [Part::Cut] Cut010  label="plugHousingTab002"
  Base = -> Box006
  Placement = pos=(-107.4,-14,0) rot=(0,0,1;0rad)
  Tool = -> Fusion036
FEATURE [Part::MultiFuse] Fusion037
  Placement = pos=(9.6,23,0) rot=(0,0,1;3.14159rad)
  Shapes = -> [Cut009,Cut010]
FEATURE [Part::Box] Box  label="Cube"
  AttacherType = Attacher::AttachEngine3D
  Height = 10
  Length = 3
  Placement = pos=(3.3,4,12) rot=(0,0,1;0rad)
  Width = 10
FEATURE [Part::Fillet] Fillet004
  Base = -> Fusion028
  Edges = 1 edges r=2: [Edge25]
FEATURE [Part::Fillet] Fillet005  label="plugHousing046"
  Base = -> Fillet004
  Edges = 1 edges r=2: [Edge8]
FEATURE [Part::Fillet] Fillet006
  Base = -> Box
  Edges = 1 edges r=2: [Edge11]
FEATURE [Part::Box] Box007  label="Cube007"
  AttacherType = Attacher::AttachEngine3D
  Height = 10
  Length = 3
  Placement = pos=(3.3,4,50) rot=(0,0,1;0rad)
  Width = 10
FEATURE [Part::Fillet] Fillet007
  Base = -> Box007
  Edges = 1 edges r=2: [Edge12]
FEATURE [Part::Box] Box008  label="Cube008"
  AttacherType = Attacher::AttachEngine3D
  Height = 28
  Length = 4
  Placement = pos=(5,0,22) rot=(0,0,1;0rad)
  Width = 10
FEATURE [Part::Fillet] Fillet008
  Base = -> Box008
  Edges = 1 edges r=1: [Edge7]
FEATURE [Part::Fillet] Fillet009
  Base = -> Fillet008
  Edges = 1 edges r=2: [Edge5]
FEATURE [Part::Fillet] Fillet010
  Base = -> Fillet009
  Edges = 1 edges r=2: [Edge2]
FEATURE [Sketcher::SketchObject] Sketch009  label="topSketch003"
  FullyConstrained = true
  sketch-geometry (4):
    g0: LineSegment StartX=16.8446 StartY=31.512 StartZ=0 EndX=16.3251 EndY=34.4666 EndZ=0
    g1: ArcOfCircle CenterX=19 CenterY=19.2524 CenterZ=0 NormalX=0 NormalY=0 NormalZ=1 AngleXU=0 Radius=15.4476 StartAngle=1.74483 EndAngle=2.72717
    g2: ArcOfCircle CenterX=19 CenterY=19.2524 CenterZ=0 NormalX=0 NormalY=0 NormalZ=1 AngleXU=0 Radius=12.4476 StartAngle=1.74483 EndAngle=2.73189
    g3: LineSegment StartX=4.86004 StartY=25.4725 StartZ=0 EndX=7.58253 EndY=24.2107 EndZ=0
  constraints (7):
    c: Block(g0)
    c: Coincident(g1,g0)
    c: Coincident(g2,g0)
    c: Coincident(g3,g1)
    c: Coincident(g3,g2)
    c: Block(g1)
    c: Block(g2)
FEATURE [Part::Extrusion] Extrude008
  Base = -> Sketch009
  Dir = (0,0,1)
  DirMode = 2
  FaceMakerClass = Part::FaceMakerBullseye
  LengthFwd = 10
  LengthRev = 0
  Placement = pos=(0,0,31) rot=(0,0,1;0rad)
  Solid = true
  Symmetric = false
FEATURE [Part::Cylinder] Cylinder020
  Angle = 360
  AttacherType = Attacher::AttachEngine3D
  Height = 20
  Placement = pos=(0,0,36.15) rot=(0,0,1;0rad)
  Radius = 8.2
FEATURE [Part::Cylinder] Cylinder021
  Angle = 360
  AttacherType = Attacher::AttachEngine3D
  Height = 10
  Placement = pos=(0,0,36.15) rot=(0,0,1;0rad)
  Radius = 4
FEATURE [Part::MultiFuse] Fusion038  label="removeToCreteHoleForPlugHousing007"
  Placement = pos=(-42,19,36) rot=(0,1,0;1.5708rad)
  Shapes = -> [Cylinder020,Cylinder021]
FEATURE [Part::Cut] Cut011
  Base = -> Extrude008
  Tool = -> Fusion038
FEATURE [Part::Fillet] Fillet011
  Base = -> Cut011
  Edges = 1 edges r=2: [Edge1]
FEATURE [Part::Fillet] Fillet012
  Base = -> Fillet011
  Edges = 1 edges r=2.5: [Edge1]
FEATURE [Part::Fillet] Fillet013
  Base = -> Fillet012
  Edges = 1 edges r=2.5: [Edge2]
FEATURE [Part::Box] Box010  label="Cube010"
  AttacherType = Attacher::AttachEngine3D
  Height = 16
  Length = 8
  Placement = pos=(12.7,31.52,28) rot=(0,0,1;0rad)
  Width = 4
FEATURE [Sketcher::SketchObject] Sketch010  label="topSketch004"
  FullyConstrained = true
  sketch-geometry (4):
    g0: LineSegment StartX=16.8446 StartY=31.512 StartZ=0 EndX=16.3251 EndY=34.4666 EndZ=0
    g1: ArcOfCircle CenterX=19 CenterY=19.2524 CenterZ=0 NormalX=0 NormalY=0 NormalZ=1 AngleXU=0 Radius=15.4476 StartAngle=1.74483 EndAngle=2.72717
    g2: ArcOfCircle CenterX=19 CenterY=19.2524 CenterZ=0 NormalX=0 NormalY=0 NormalZ=1 AngleXU=0 Radius=12.4476 StartAngle=1.74483 EndAngle=2.73189
    g3: LineSegment StartX=4.86004 StartY=25.4725 StartZ=0 EndX=7.58253 EndY=24.2107 EndZ=0
  constraints (7):
    c: Block(g0)
    c: Coincident(g1,g0)
    c: Coincident(g2,g0)
    c: Coincident(g3,g1)
    c: Coincident(g3,g2)
    c: Block(g1)
    c: Block(g2)
FEATURE [Part::Cylinder] Cylinder022
  Angle = 360
  AttacherType = Attacher::AttachEngine3D
  Height = 10
  Placement = pos=(0,0,36.15) rot=(0,0,1;0rad)
  Radius = 4
FEATURE [Sketcher::SketchObject] Sketch011  label="topSketch005"
  FullyConstrained = true
  sketch-geometry (4):
    g0: LineSegment StartX=16.8446 StartY=31.512 StartZ=0 EndX=16.3251 EndY=34.4666 EndZ=0
    g1: ArcOfCircle CenterX=19 CenterY=19.2524 CenterZ=0 NormalX=0 NormalY=0 NormalZ=1 AngleXU=0 Radius=15.4476 StartAngle=1.74483 EndAngle=2.72717
    g2: ArcOfCircle CenterX=19 CenterY=19.2524 CenterZ=0 NormalX=0 NormalY=0 NormalZ=1 AngleXU=0 Radius=12.4476 StartAngle=1.74483 EndAngle=2.73189
    g3: LineSegment StartX=4.86004 StartY=25.4725 StartZ=0 EndX=7.58253 EndY=24.2107 EndZ=0
  constraints (7):
    c: Block(g0)
    c: Coincident(g1,g0)
    c: Coincident(g2,g0)
    c: Coincident(g3,g1)
    c: Coincident(g3,g2)
    c: Block(g1)
    c: Block(g2)
FEATURE [Part::Extrusion] Extrude010
  Base = -> Sketch011
  Dir = (0,0,1)
  DirMode = 2
  FaceMakerClass = Part::FaceMakerBullseye
  LengthFwd = 10.6
  LengthRev = 0
  Placement = pos=(0,0,31) rot=(0,0,1;0rad)
  Solid = true
  Symmetric = false
FEATURE [Part::Cylinder] Cylinder023
  Angle = 360
  AttacherType = Attacher::AttachEngine3D
  Height = 20
  Placement = pos=(0,0,36.15) rot=(0,0,1;0rad)
  Radius = 8.2
FEATURE [Part::MultiFuse] Fusion039  label="removeToCreteHoleForPlugHousing008"
  Placement = pos=(-42,19,36) rot=(0,1,0;1.5708rad)
  Shapes = -> [Cylinder023,Cylinder022]
FEATURE [Part::Cut] Cut012
  Base = -> Extrude010
  Placement = pos=(0,0,-0.3) rot=(0,0,1;0rad)
  Tool = -> Fusion039
FEATURE [Part::Cut] Cut013
  Base = -> Box010
  Tool = -> Cut012
FEATURE [Part::Fillet] Fillet014
  Base = -> Cut013
  Edges = 1 edges r=0.7: [Edge13]
FEATURE [Part::Fillet] Fillet015
  Base = -> Fillet014
  Edges = 1 edges r=0.7: [Edge13]
FEATURE [Part::Fillet] Fillet016
  Base = -> Fillet015
  Edges = 1 edges r=0.7: [Edge16]
FEATURE [Part::Fillet] Fillet017
  Base = -> Fillet016
  Edges = 1 edges r=0.7: [Edge11]
FEATURE [Part::Fillet] Fillet018
  Base = -> Fillet017
  Edges = 1 edges r=0.7: [Edge10]
FEATURE [Part::Fillet] Fillet019
  Base = -> Fillet018
  Edges = 1 edges r=1.2: [Edge5]
FEATURE [Part::Fillet] Fillet020
  Base = -> Fillet019
  Edges = 1 edges r=1.2: [Edge12]
FEATURE [Part::Fillet] Fillet021
  Base = -> Fillet020
  Edges = 1 edges r=2: [Edge1]
  Placement = pos=(0.3,0,0) rot=(0,0,1;0rad)
FEATURE [Part::MultiFuse] Fusion040  label="top005"
  Shapes = -> [Cut008,Fillet021]
FEATURE [Part::MultiFuse] Fusion041  label="wireHolder"
  Shapes = -> [Fusion033,Fillet013]
FEATURE [Part::MultiFuse] Fusion042
  Shapes = -> [Fillet007,Fusion041]
FEATURE [Part::MultiFuse] Fusion043  label="wireHolder001"
  Shapes = -> [Fusion042,Fillet010]
FEATURE [Part::MultiFuse] Fusion044  label="wireHolder002"
  Shapes = -> [Fillet006,Fusion037,Fusion043]
FEATURE [Part::Feature] Face026
  shape: bbox 11 x 6 x 2e-07 mm, 1 faces, 0 solids (baked)
FEATURE [Part::Revolution] Revolve026
  Angle = 360
  Axis = (0,1,0)
  Base = (0,0,0)
  FaceMakerClass = Part::FaceMakerBullseye
  Placement = pos=(30.3,-1,19.7) rot=(0,0,1;0rad)
  Solid = false
  Source = -> Face026
  Symmetric = false
FEATURE [Sketcher::SketchObject] Sketch013  label="topSketch006"
  FullyConstrained = true
  sketch-geometry (13):
    g0: LineSegment StartX=117 StartY=19 StartZ=0 EndX=117 EndY=38 EndZ=0
    g1: ArcOfCircle CenterX=98 CenterY=19 CenterZ=0 NormalX=0 NormalY=0 NormalZ=1 AngleXU=0 Radius=19 StartAngle=5.7297 EndAngle=6.28319
    g2: LineSegment StartX=0 StartY=3 StartZ=0 EndX=0 EndY=19 EndZ=0
    g3: LineSegment StartX=19 StartY=38 StartZ=0 EndX=117 EndY=38 EndZ=0
    g4: ArcOfCircle CenterX=19 CenterY=19 CenterZ=0 NormalX=0 NormalY=0 NormalZ=1 AngleXU=0 Radius=19 StartAngle=1.5708 EndAngle=3.14159
    g5: ArcOfCircle CenterX=19 CenterY=19 CenterZ=0 NormalX=0 NormalY=0 NormalZ=1 AngleXU=0 Radius=16 StartAngle=1.5708 EndAngle=3.14159
    g6: ArcOfCircle CenterX=98 CenterY=19 CenterZ=0 NormalX=0 NormalY=0 NormalZ=1 AngleXU=0 Radius=16 StartAngle=5.60905 EndAngle=6.28319
    g7: LineSegment StartX=114 StartY=19 StartZ=0 EndX=114 EndY=35 EndZ=0
    g8: LineSegment StartX=110.5 StartY=9.01251 StartZ=0 EndX=114.163 EndY=9.01251 EndZ=0
    g9: LineSegment StartX=114 StartY=35 StartZ=0 EndX=19 EndY=35 EndZ=0
    g10: LineSegment StartX=0 StartY=3 StartZ=0 EndX=0 EndY=0 EndZ=0
    g11: LineSegment StartX=3 StartY=0 StartZ=0 EndX=0 EndY=0 EndZ=0
    g12: LineSegment StartX=3 StartY=19 StartZ=0 EndX=3 EndY=0 EndZ=0
  constraints (33):
    c: Vertical(g0)
    c: Distance(g0) = 19
    c: Block(g0)
    c: Coincident(g1,g0)
    c: Block(g1)
    c: Vertical(g2)
    c: Block(g2)
    c: Coincident(g3,g0)
    c: Horizontal(g3)
    c: Distance(g3) = 98
    c: Coincident(g4,g3)
    c: Coincident(g4,g2)
    c: Block(g4)
    c: Coincident(g5,g4)
    c: Coincident(g6,g1)
    c: Block(g6)
    c: Block(g5)
    c: Coincident(g7,g6)
    c: Vertical(g7)
    c: Coincident(g8,g6)
    c: Coincident(g8,g1)
    c: Coincident(g9,g7)
    c: Coincident(g9,g5)
    c: Horizontal(g9)
    c: Tangent(g9,g5)
    c: Coincident(g10,g2)
    c: Distance(g10) = 3
    c: Vertical(g10)
    c: Coincident(g11,g10)
    c: Horizontal(g11)
    c: Coincident(g12,g5)
    c: Coincident(g12,g11)
    c: Vertical(g12)
FEATURE [Part::Extrusion] Extrude011  label="top006"
  Base = -> Sketch013
  Dir = (0,0,1)
  DirMode = 2
  FaceMakerClass = Part::FaceMakerBullseye
  LengthFwd = 72
  LengthRev = 0
  Solid = true
  Symmetric = false
FEATURE [Sketcher::SketchObject] Sketch014
  FullyConstrained = true
  MapMode = 3
  Placement = pos=(0,0,0) rot=(1,0,0;1.5708rad)
  Support = -> [Extrude011]
  sketch-geometry (8):
    g0: Circle CenterX=80.351 CenterY=-67.6202 CenterZ=0 NormalX=0 NormalY=0 NormalZ=1 AngleXU=0 Radius=2
    g1: Circle CenterX=80.351 CenterY=-67.6202 CenterZ=0 NormalX=0 NormalY=0 NormalZ=1 AngleXU=0 Radius=3
    g2: Circle CenterX=80.351 CenterY=-4.92017 CenterZ=0 NormalX=0 NormalY=0 NormalZ=1 AngleXU=0 Radius=2
    g3: Circle CenterX=80.351 CenterY=-4.92017 CenterZ=0 NormalX=0 NormalY=0 NormalZ=1 AngleXU=0 Radius=3
    g4: Circle CenterX=23.851 CenterY=-4.92017 CenterZ=0 NormalX=0 NormalY=0 NormalZ=1 AngleXU=0 Radius=2
    g5: Circle CenterX=23.851 CenterY=-4.92017 CenterZ=0 NormalX=0 NormalY=0 NormalZ=1 AngleXU=0 Radius=3
    g6: Circle CenterX=23.851 CenterY=-67.6202 CenterZ=0 NormalX=0 NormalY=0 NormalZ=1 AngleXU=0 Radius=2
    g7: Circle CenterX=23.851 CenterY=-67.6202 CenterZ=0 NormalX=0 NormalY=0 NormalZ=1 AngleXU=0 Radius=3
  constraints (8):
    c: Block(g3)
    c: Block(g2)
    c: Block(g1)
    c: Block(g0)
    c: Block(g6)
    c: Block(g7)
    c: Block(g4)
    c: Block(g5)
FEATURE [Part::Feature] Face027
  shape: bbox 11 x 6 x 2e-07 mm, 1 faces, 0 solids (baked)
FEATURE [Part::Revolution] Revolve027
  Angle = 360
  Axis = (0,1,0)
  Base = (0,0,0)
  FaceMakerClass = Part::FaceMakerBullseye
  Placement = pos=(30.3,-1,51.7) rot=(0,0,1;0rad)
  Solid = false
  Source = -> Face027
  Symmetric = false
FEATURE [Part::Feature] Face028
  shape: bbox 11 x 6 x 2e-07 mm, 1 faces, 0 solids (baked)
FEATURE [Part::Revolution] Revolve028
  Angle = 360
  Axis = (0,1,0)
  Base = (0,0,0)
  FaceMakerClass = Part::FaceMakerBullseye
  Placement = pos=(62.3,-1,19.7) rot=(0,0,1;0rad)
  Solid = false
  Source = -> Face028
  Symmetric = false
FEATURE [Part::Feature] Face029
  shape: bbox 11 x 6 x 2e-07 mm, 1 faces, 0 solids (baked)
FEATURE [Part::Revolution] Revolve029
  Angle = 360
  Axis = (0,1,0)
  Base = (0,0,0)
  FaceMakerClass = Part::FaceMakerBullseye
  Placement = pos=(62.3,-1,51.7) rot=(0,0,1;0rad)
  Solid = false
  Source = -> Face029
  Symmetric = false
FEATURE [Part::Feature] Wire
  shape: bbox 11 x 5.2 x 2e-07 mm, 0 faces, 0 solids (baked)
FEATURE [Part::Revolution] Revolve030
  Angle = 360
  Axis = (0,1,0)
  Base = (0,0,0)
  FaceMakerClass = Part::FaceMakerBullseye
  Placement = pos=(30.3,38,19.7) rot=(0,0,1;0rad)
  Solid = true
  Source = -> Wire
  Symmetric = false
FEATURE [Part::Feature] Wire001
  shape: bbox 11 x 5.2 x 2e-07 mm, 0 faces, 0 solids (baked)
FEATURE [Part::Revolution] Revolve031
  Angle = 360
  Axis = (0,1,0)
  Base = (0,0,0)
  FaceMakerClass = Part::FaceMakerBullseye
  Placement = pos=(30.3,38,51.7) rot=(0,0,1;0rad)
  Solid = true
  Source = -> Wire001
  Symmetric = false
FEATURE [Part::Feature] Wire002
  shape: bbox 11 x 5.2 x 2e-07 mm, 0 faces, 0 solids (baked)
FEATURE [Part::Revolution] Revolve032
  Angle = 360
  Axis = (0,1,0)
  Base = (0,0,0)
  FaceMakerClass = Part::FaceMakerBullseye
  Placement = pos=(62.3,38,51.7) rot=(0,0,1;0rad)
  Solid = true
  Source = -> Wire002
  Symmetric = false
FEATURE [Part::Feature] Wire003
  shape: bbox 11 x 5.2 x 2e-07 mm, 0 faces, 0 solids (baked)
FEATURE [Part::Revolution] Revolve033
  Angle = 360
  Axis = (0,1,0)
  Base = (0,0,0)
  FaceMakerClass = Part::FaceMakerBullseye
  Placement = pos=(62.3,38,19.7) rot=(0,0,1;0rad)
  Solid = true
  Source = -> Wire003
  Symmetric = false
FEATURE [Part::MultiFuse] Fusion045  label="altRandScrewHousing"
  Shapes = -> [Revolve029,Revolve027,Revolve028,Revolve026]
FEATURE [Part::MultiFuse] Fusion046  label="fanScrewHousing"
  Shapes = -> [Revolve033,Revolve032,Revolve031,Revolve030]
FEATURE [Sketcher::SketchObject] Sketch015
  FullyConstrained = true
  sketch-geometry (17):
    g0: Circle CenterX=-3.5 CenterY=23.5 CenterZ=0 NormalX=0 NormalY=0 NormalZ=1 AngleXU=0 Radius=1
    g1: Circle CenterX=-1 CenterY=15.25 CenterZ=0 NormalX=0 NormalY=0 NormalZ=1 AngleXU=0 Radius=1
    g2: Circle CenterX=-3.5 CenterY=7 CenterZ=0 NormalX=0 NormalY=0 NormalZ=1 AngleXU=0 Radius=1
    g3: BSplineCurve PolesCount=3 KnotsCount=2 Degree=2 IsPeriodic=0
    g4: GeomPoint X=-3.5 Y=23.5 Z=0
    g5: GeomPoint X=-3.5 Y=7 Z=0
    g6: Circle CenterX=-4.8 CenterY=30.5 CenterZ=0 NormalX=0 NormalY=0 NormalZ=1 AngleXU=0 Radius=1
    g7: Circle CenterX=-3.5 CenterY=30.5 CenterZ=0 NormalX=0 NormalY=0 NormalZ=1 AngleXU=0 Radius=1
    g8: Circle CenterX=-3.5 CenterY=29.2 CenterZ=0 NormalX=0 NormalY=0 NormalZ=1 AngleXU=0 Radius=1
    g9: BSplineCurve PolesCount=3 KnotsCount=2 Degree=2 IsPeriodic=0
    g10: GeomPoint X=-4.8 Y=30.5 Z=0
    g11: GeomPoint X=-3.5 Y=29.2 Z=0
    g12: LineSegment StartX=-3.5 StartY=29.2 StartZ=0 EndX=-3.5 EndY=23.5 EndZ=0
    g13: LineSegment StartX=-4.8 StartY=30.5 StartZ=0 EndX=0 EndY=30.5 EndZ=0
    g14: LineSegment StartX=-3.5 StartY=0.3 StartZ=0 EndX=0 EndY=0.3 EndZ=0
    g15: LineSegment StartX=-3.5 StartY=0.3 StartZ=0 EndX=-3.5 EndY=7 EndZ=0
    g16: LineSegment StartX=0 StartY=0.3 StartZ=0 EndX=0 EndY=30.5 EndZ=0
  constraints (33):
    c: Weight(g0) = 1
    c: Equal(g0,g1)
    c: Equal(g0,g2)
    c: InternalAlignment(g0,g3)
    c: InternalAlignment(g1,g3)
    c: InternalAlignment(g2,g3)
    c: InternalAlignment(g4,g3)
    c: InternalAlignment(g5,g3)
    c: Block(g3)
    c: Weight(g6) = 1
    c: Equal(g6,g7)
    c: Equal(g6,g8)
    c: InternalAlignment(g6,g9)
    c: InternalAlignment(g7,g9)
    c: InternalAlignment(g8,g9)
    c: InternalAlignment(g10,g9)
    c: InternalAlignment(g11,g9)
    c: Block(g9)
    c: Coincident(g12,g9)
    c: Coincident(g12,g3)
    c: Vertical(g12)
    c: Coincident(g13,g9)
    c: Horizontal(g13)
    c: Distance(g13) = 4.8
    c: Horizontal(g14)
    c: Block(g14)
    c: Coincident(g15,g14)
    c: Coincident(g15,g3)
    c: Vertical(g15)
    c: Coincident(g16,g14)
    c: Coincident(g16,g13)
    c: Vertical(g16)
    c: Tangent(g16,g1)
FEATURE [Sketcher::SketchObject] Sketch016
  FullyConstrained = true
  sketch-geometry (16):
    g0: Circle CenterX=-3.5 CenterY=23.5 CenterZ=0 NormalX=0 NormalY=0 NormalZ=1 AngleXU=0 Radius=1
    g1: Circle CenterX=-1 CenterY=15.25 CenterZ=0 NormalX=0 NormalY=0 NormalZ=1 AngleXU=0 Radius=1
    g2: Circle CenterX=-3.5 CenterY=7 CenterZ=0 NormalX=0 NormalY=0 NormalZ=1 AngleXU=0 Radius=1
    g3: BSplineCurve PolesCount=3 KnotsCount=2 Degree=2 IsPeriodic=0
    g4: GeomPoint X=-3.5 Y=23.5 Z=0
    g5: GeomPoint X=-3.5 Y=7 Z=0
    g6: LineSegment StartX=-3.5 StartY=28.2 StartZ=0 EndX=-3.5 EndY=23.5 EndZ=0
    g7: LineSegment StartX=0 StartY=29.5 StartZ=0 EndX=0 EndY=30 EndZ=0
    g8: LineSegment StartX=-3.5 StartY=28.2 StartZ=0 EndX=-3.5 EndY=30 EndZ=0
    g9: LineSegment StartX=0 StartY=30 StartZ=0 EndX=0 EndY=30.5 EndZ=0
    g10: LineSegment StartX=0 StartY=30.5 StartZ=0 EndX=-3.5 EndY=30.5 EndZ=0
    g11: LineSegment StartX=-3.5 StartY=30.5 StartZ=0 EndX=-3.5 EndY=30 EndZ=0
    g12: LineSegment StartX=0 StartY=29.5 StartZ=0 EndX=0 EndY=5 EndZ=0
    g13: LineSegment StartX=-3.5 StartY=0.3 StartZ=0 EndX=-3.5 EndY=7 EndZ=0
    g14: LineSegment StartX=-3.5 StartY=0.3 StartZ=0 EndX=0 EndY=0.3 EndZ=0
    g15: LineSegment StartX=0 StartY=5 StartZ=0 EndX=0 EndY=0.3 EndZ=0
  constraints (39):
    c: Weight(g0) = 1
    c: Equal(g0,g1)
    c: Equal(g0,g2)
    c: InternalAlignment(g0,g3)
    c: InternalAlignment(g1,g3)
    c: InternalAlignment(g2,g3)
    c: InternalAlignment(g4,g3)
    c: InternalAlignment(g5,g3)
    c: Block(g3)
    c: Coincident(g6,g3)
    c: Vertical(g6)
    c: Vertical(g7)
    c: Distance(g7) = 0.5
    c: Coincident(g8,g6)
    c: Vertical(g8)
    c: Block(g6)
    c: Block(g7)
    c: Vertical(g9)
    c: Equal(g7,g9) = 0.5
    c: Block(g9)
    c: Coincident(g9,g7)
    c: Horizontal(g10)
    c: Coincident(g10,g9)
    c: Coincident(g11,g10)
    c: Coincident(g11,g8)
    c: Vertical(g11)
    c: Block(g11)
    c: Coincident(g12,g7)
    c: Vertical(g12)
    c: Coincident(g13,g3)
    c: Vertical(g13)
    c: Distance(g13) = 6.7
    c: Coincident(g14,g13)
    c: Horizontal(g14)
    c: Block(g14)
    c: Coincident(g15,g12)
    c: Coincident(g15,g14)
    c: Vertical(g15)
    c: Block(g15)
FEATURE [Sketcher::SketchObject] Sketch017
  FullyConstrained = true
  sketch-geometry (11):
    g0: LineSegment StartX=-3.5 StartY=1e-16 StartZ=0 EndX=-1.6 EndY=1e-16 EndZ=0
    g1: LineSegment StartX=-1.6 StartY=1e-16 StartZ=0 EndX=-1.6 EndY=1.5 EndZ=0
    g2: LineSegment StartX=-3.5 StartY=1.5 StartZ=0 EndX=-1.6 EndY=1.5 EndZ=0
    g3: LineSegment StartX=-3.5 StartY=1e-16 StartZ=0 EndX=-4.8 EndY=1e-16 EndZ=0
    g4: Circle CenterX=-3.5 CenterY=1.3 CenterZ=0 NormalX=0 NormalY=0 NormalZ=1 AngleXU=0 Radius=1
    g5: Circle CenterX=-3.5 CenterY=1e-16 CenterZ=0 NormalX=0 NormalY=0 NormalZ=1 AngleXU=0 Radius=1
    g6: Circle CenterX=-4.8 CenterY=1e-16 CenterZ=0 NormalX=0 NormalY=0 NormalZ=1 AngleXU=0 Radius=1
    g7: BSplineCurve PolesCount=3 KnotsCount=2 Degree=2 IsPeriodic=0
    g8: GeomPoint X=-3.5 Y=1.3 Z=0
    g9: GeomPoint X=-4.8 Y=1e-16 Z=0
    g10: LineSegment StartX=-3.5 StartY=1.3 StartZ=0 EndX=-3.5 EndY=1.5 EndZ=0
  constraints (24):
    c: Horizontal(g0)
    c: Distance(g0) = 1.9
    c: Block(g0)
    c: Coincident(g1,g0)
    c: Vertical(g1)
    c: Coincident(g2,g1)
    c: Horizontal(g2)
    c: Coincident(g3,g0)
    c: Horizontal(g3)
    c: Distance(g3) = 1.3
    c: Weight(g4) = 1
    c: Equal(g4,g5)
    c: Coincident(g5,g0)
    c: Equal(g4,g6)
    c: Coincident(g7,g3)
    c: InternalAlignment(g4,g7)
    c: InternalAlignment(g5,g7)
    c: InternalAlignment(g6,g7)
    c: InternalAlignment(g8,g7)
    c: InternalAlignment(g9,g7)
    c: Coincident(g10,g7)
    c: Coincident(g10,g2)
    c: Vertical(g10)
    c: Block(g10)
FEATURE [Part::Feature] Face035
  shape: bbox 3.2 x 1.5 x 2e-07 mm, 1 faces, 0 solids (baked)
FEATURE [Part::Revolution] Revolve039  label="backCaseScrewRetainer"
  Angle = 360
  Axis = (0,1,0)
  Base = (0,0,0)
  FaceMakerClass = Part::FaceMakerBullseye
  Placement = pos=(12.5,3,62) rot=(0,0,1;0rad)
  Solid = false
  Source = -> Face035
  Symmetric = false
FEATURE [Part::Feature] Face036
  shape: bbox 3.2 x 1.5 x 2e-07 mm, 1 faces, 0 solids (baked)
FEATURE [Part::Feature] Face039
  shape: bbox 4.8 x 30.2 x 2e-07 mm, 1 faces, 0 solids (baked)
FEATURE [Part::Revolution] Revolve043  label="frontCaseScrewPost002"
  Angle = 360
  Axis = (0,1,0)
  Base = (0,0,0)
  FaceMakerClass = Part::FaceMakerBullseye
  Placement = pos=(89.5,4.5,3.5) rot=(0,0,1;0rad)
  Solid = false
  Source = -> Face039
  Symmetric = false
FEATURE [Part::Feature] Face042
  shape: bbox 4.8 x 30.2 x 2e-07 mm, 1 faces, 0 solids (baked)
FEATURE [Part::Revolution] Revolve046  label="frontCaseScrewPost003"
  Angle = 360
  Axis = (0,1,0)
  Base = (0,0,0)
  FaceMakerClass = Part::FaceMakerBullseye
  Placement = pos=(89.5,4.5,68.5) rot=(0,0,1;0rad)
  Solid = false
  Source = -> Face042
  Symmetric = false
FEATURE [Part::Feature] Face043
  shape: bbox 3.2 x 1.5 x 2e-07 mm, 1 faces, 0 solids (baked)
FEATURE [Part::Revolution] Revolve047  label="frontCaseScrewRetainer002"
  Angle = 360
  Axis = (0,1,0)
  Base = (0,0,0)
  FaceMakerClass = Part::FaceMakerBullseye
  Placement = pos=(89.5,3,68.5) rot=(0,0,1;0rad)
  Solid = false
  Source = -> Face043
  Symmetric = false
FEATURE [Part::Feature] Face044
  shape: bbox 3.2 x 1.5 x 2e-07 mm, 1 faces, 0 solids (baked)
FEATURE [Part::Revolution] Revolve048  label="frontCaseScrewRetainer003"
  Angle = 360
  Axis = (0,1,0)
  Base = (0,0,0)
  FaceMakerClass = Part::FaceMakerBullseye
  Placement = pos=(89.5,3,3.5) rot=(0,0,1;0rad)
  Solid = false
  Source = -> Face044
  Symmetric = false
FEATURE [App::MeasureDistance] Distance002  label="Distance: 1.67 mm"
  Distance = 1.66921
  P1 = (99.2361,4.7524,71.7)
  P2 = (99.2347,6.42161,71.7)
FEATURE [Sketcher::SketchObject] Sketch018
  FullyConstrained = true
  sketch-geometry (7):
    g0: LineSegment StartX=0 StartY=0 StartZ=0 EndX=0 EndY=6 EndZ=0
    g1: Circle CenterX=0 CenterY=0 CenterZ=0 NormalX=0 NormalY=0 NormalZ=1 AngleXU=0 Radius=1
    g2: Circle CenterX=8 CenterY=6 CenterZ=0 NormalX=0 NormalY=0 NormalZ=1 AngleXU=0 Radius=1
    g3: BSplineCurve PolesCount=3 KnotsCount=2 Degree=2 IsPeriodic=0
    g4: GeomPoint X=0 Y=0 Z=0
    g5: GeomPoint X=8 Y=6 Z=0
    g6: LineSegment StartX=0 StartY=6 StartZ=0 EndX=8 EndY=6 EndZ=0
  constraints (14):
    c: Coincident(g0,g-1)
    c: Distance(g0) = 6
    c: Vertical(g0)
    c: Coincident(g3,g0)
    c: Weight(g1) = 1
    c: Equal(g1,g2)
    c: InternalAlignment(g1,g3)
    c: InternalAlignment(g2,g3)
    c: InternalAlignment(g4,g3)
    c: InternalAlignment(g5,g3)
    c: Block(g3)
    c: Coincident(g6,g0)
    c: Coincident(g6,g3)
    c: Horizontal(g6)
FEATURE [Part::Extrusion] Extrude012  label="caseScrewPillarBracket"
  Base = -> Sketch018
  Dir = (0,0,1)
  DirMode = 2
  FaceMakerClass = Part::FaceMakerBullseye
  LengthFwd = 2.4
  LengthRev = 0
  Placement = pos=(15.76,29,8.8) rot=(0,1,0;0rad)
  Solid = true
  Symmetric = false
FEATURE [Sketcher::SketchObject] Sketch019
  FullyConstrained = true
  sketch-geometry (7):
    g0: LineSegment StartX=0 StartY=0 StartZ=0 EndX=0 EndY=6 EndZ=0
    g1: Circle CenterX=0 CenterY=0 CenterZ=0 NormalX=0 NormalY=0 NormalZ=1 AngleXU=0 Radius=1
    g2: Circle CenterX=8 CenterY=6 CenterZ=0 NormalX=0 NormalY=0 NormalZ=1 AngleXU=0 Radius=1
    g3: BSplineCurve PolesCount=3 KnotsCount=2 Degree=2 IsPeriodic=0
    g4: GeomPoint X=0 Y=0 Z=0
    g5: GeomPoint X=8 Y=6 Z=0
    g6: LineSegment StartX=0 StartY=6 StartZ=0 EndX=8 EndY=6 EndZ=0
  constraints (14):
    c: Coincident(g0,g-1)
    c: Distance(g0) = 6
    c: Vertical(g0)
    c: Coincident(g3,g0)
    c: Weight(g1) = 1
    c: Equal(g1,g2)
    c: InternalAlignment(g1,g3)
    c: InternalAlignment(g2,g3)
    c: InternalAlignment(g4,g3)
    c: InternalAlignment(g5,g3)
    c: Block(g3)
    c: Coincident(g6,g0)
    c: Coincident(g6,g3)
    c: Horizontal(g6)
FEATURE [Part::Extrusion] Extrude013  label="caseScrewPillarBracket001"
  Base = -> Sketch019
  Dir = (0,0,1)
  DirMode = 2
  FaceMakerClass = Part::FaceMakerBullseye
  LengthFwd = 2.4
  LengthRev = 0
  Placement = pos=(15.76,29,60.8) rot=(0,0,1;0rad)
  Solid = true
  Symmetric = false
FEATURE [Sketcher::SketchObject] Sketch020
  FullyConstrained = true
  sketch-geometry (7):
    g0: LineSegment StartX=0 StartY=0 StartZ=0 EndX=0 EndY=6 EndZ=0
    g1: Circle CenterX=0 CenterY=0 CenterZ=0 NormalX=0 NormalY=0 NormalZ=1 AngleXU=0 Radius=1
    g2: Circle CenterX=8 CenterY=6 CenterZ=0 NormalX=0 NormalY=0 NormalZ=1 AngleXU=0 Radius=1
    g3: BSplineCurve PolesCount=3 KnotsCount=2 Degree=2 IsPeriodic=0
    g4: GeomPoint X=0 Y=0 Z=0
    g5: GeomPoint X=8 Y=6 Z=0
    g6: LineSegment StartX=0 StartY=6 StartZ=0 EndX=8 EndY=6 EndZ=0
  constraints (14):
    c: Coincident(g0,g-1)
    c: Distance(g0) = 6
    c: Vertical(g0)
    c: Coincident(g3,g0)
    c: Weight(g1) = 1
    c: Equal(g1,g2)
    c: InternalAlignment(g1,g3)
    c: InternalAlignment(g2,g3)
    c: InternalAlignment(g4,g3)
    c: InternalAlignment(g5,g3)
    c: Block(g3)
    c: Coincident(g6,g0)
    c: Coincident(g6,g3)
    c: Horizontal(g6)
FEATURE [Part::Extrusion] Extrude014  label="caseScrewPillarBracket002"
  Base = -> Sketch020
  Dir = (0,0,1)
  DirMode = 2
  FaceMakerClass = Part::FaceMakerBullseye
  LengthFwd = 2.4
  LengthRev = 0
  Placement = pos=(13.7,29,13.26) rot=(0,-1,0;1.5708rad)
  Solid = true
  Symmetric = false
FEATURE [Sketcher::SketchObject] Sketch021
  FullyConstrained = true
  sketch-geometry (7):
    g0: LineSegment StartX=0 StartY=0 StartZ=0 EndX=0 EndY=6 EndZ=0
    g1: Circle CenterX=0 CenterY=0 CenterZ=0 NormalX=0 NormalY=0 NormalZ=1 AngleXU=0 Radius=1
    g2: Circle CenterX=8 CenterY=6 CenterZ=0 NormalX=0 NormalY=0 NormalZ=1 AngleXU=0 Radius=1
    g3: BSplineCurve PolesCount=3 KnotsCount=2 Degree=2 IsPeriodic=0
    g4: GeomPoint X=0 Y=0 Z=0
    g5: GeomPoint X=8 Y=6 Z=0
    g6: LineSegment StartX=0 StartY=6 StartZ=0 EndX=8 EndY=6 EndZ=0
  constraints (14):
    c: Coincident(g0,g-1)
    c: Distance(g0) = 6
    c: Vertical(g0)
    c: Coincident(g3,g0)
    c: Weight(g1) = 1
    c: Equal(g1,g2)
    c: InternalAlignment(g1,g3)
    c: InternalAlignment(g2,g3)
    c: InternalAlignment(g4,g3)
    c: InternalAlignment(g5,g3)
    c: Block(g3)
    c: Coincident(g6,g0)
    c: Coincident(g6,g3)
    c: Horizontal(g6)
FEATURE [Part::Extrusion] Extrude015  label="caseScrewPillarBracket003"
  Base = -> Sketch021
  Dir = (0,0,1)
  DirMode = 2
  FaceMakerClass = Part::FaceMakerBullseye
  LengthFwd = 2.4
  LengthRev = 0
  Placement = pos=(11.3,29,58.74) rot=(0,1,0;1.5708rad)
  Solid = true
  Symmetric = false
FEATURE [Sketcher::SketchObject] Sketch022
  FullyConstrained = true
  sketch-geometry (7):
    g0: LineSegment StartX=0 StartY=0 StartZ=0 EndX=0 EndY=6 EndZ=0
    g1: Circle CenterX=0 CenterY=0 CenterZ=0 NormalX=0 NormalY=0 NormalZ=1 AngleXU=0 Radius=1
    g2: Circle CenterX=8 CenterY=6 CenterZ=0 NormalX=0 NormalY=0 NormalZ=1 AngleXU=0 Radius=1
    g3: BSplineCurve PolesCount=3 KnotsCount=2 Degree=2 IsPeriodic=0
    g4: GeomPoint X=0 Y=0 Z=0
    g5: GeomPoint X=8 Y=6 Z=0
    g6: LineSegment StartX=0 StartY=6 StartZ=0 EndX=8 EndY=6 EndZ=0
  constraints (14):
    c: Coincident(g0,g-1)
    c: Distance(g0) = 6
    c: Vertical(g0)
    c: Coincident(g3,g0)
    c: Weight(g1) = 1
    c: Equal(g1,g2)
    c: InternalAlignment(g1,g3)
    c: InternalAlignment(g2,g3)
    c: InternalAlignment(g4,g3)
    c: InternalAlignment(g5,g3)
    c: Block(g3)
    c: Coincident(g6,g0)
    c: Coincident(g6,g3)
    c: Horizontal(g6)
FEATURE [Part::Extrusion] Extrude016  label="caseScrewPillarBracket004"
  Base = -> Sketch022
  Dir = (0,0,1)
  DirMode = 2
  FaceMakerClass = Part::FaceMakerBullseye
  LengthFwd = 2.4
  LengthRev = 0
  Placement = pos=(88.3,29,65.23) rot=(0,1,0;1.5708rad)
  Solid = true
  Symmetric = false
FEATURE [Sketcher::SketchObject] Sketch023
  FullyConstrained = true
  sketch-geometry (7):
    g0: LineSegment StartX=0 StartY=0 StartZ=0 EndX=0 EndY=6 EndZ=0
    g1: Circle CenterX=0 CenterY=0 CenterZ=0 NormalX=0 NormalY=0 NormalZ=1 AngleXU=0 Radius=1
    g2: Circle CenterX=8 CenterY=6 CenterZ=0 NormalX=0 NormalY=0 NormalZ=1 AngleXU=0 Radius=1
    g3: BSplineCurve PolesCount=3 KnotsCount=2 Degree=2 IsPeriodic=0
    g4: GeomPoint X=0 Y=0 Z=0
    g5: GeomPoint X=8 Y=6 Z=0
    g6: LineSegment StartX=0 StartY=6 StartZ=0 EndX=8 EndY=6 EndZ=0
  constraints (14):
    c: Coincident(g0,g-1)
    c: Distance(g0) = 6
    c: Vertical(g0)
    c: Coincident(g3,g0)
    c: Weight(g1) = 1
    c: Equal(g1,g2)
    c: InternalAlignment(g1,g3)
    c: InternalAlignment(g2,g3)
    c: InternalAlignment(g4,g3)
    c: InternalAlignment(g5,g3)
    c: Block(g3)
    c: Coincident(g6,g0)
    c: Coincident(g6,g3)
    c: Horizontal(g6)
FEATURE [Part::Extrusion] Extrude017  label="caseScrewPillarBracket005"
  Base = -> Sketch023
  Dir = (0,0,1)
  DirMode = 2
  FaceMakerClass = Part::FaceMakerBullseye
  LengthFwd = 2.4
  LengthRev = 0
  Placement = pos=(90.7,29,6.77) rot=(0,-1,0;1.5708rad)
  Solid = true
  Symmetric = false
FEATURE [Sketcher::SketchObject] Sketch024
  FullyConstrained = true
  sketch-geometry (7):
    g0: LineSegment StartX=0 StartY=0 StartZ=0 EndX=0 EndY=6 EndZ=0
    g1: Circle CenterX=0 CenterY=0 CenterZ=0 NormalX=0 NormalY=0 NormalZ=1 AngleXU=0 Radius=1
    g2: Circle CenterX=8 CenterY=6 CenterZ=0 NormalX=0 NormalY=0 NormalZ=1 AngleXU=0 Radius=1
    g3: BSplineCurve PolesCount=3 KnotsCount=2 Degree=2 IsPeriodic=0
    g4: GeomPoint X=0 Y=0 Z=0
    g5: GeomPoint X=8 Y=6 Z=0
    g6: LineSegment StartX=0 StartY=6 StartZ=0 EndX=8 EndY=6 EndZ=0
  constraints (14):
    c: Coincident(g0,g-1)
    c: Distance(g0) = 6
    c: Vertical(g0)
    c: Coincident(g3,g0)
    c: Weight(g1) = 1
    c: Equal(g1,g2)
    c: InternalAlignment(g1,g3)
    c: InternalAlignment(g2,g3)
    c: InternalAlignment(g4,g3)
    c: InternalAlignment(g5,g3)
    c: Block(g3)
    c: Coincident(g6,g0)
    c: Coincident(g6,g3)
    c: Horizontal(g6)
FEATURE [Part::Extrusion] Extrude018  label="caseScrewPillarBracket006"
  Base = -> Sketch024
  Dir = (0,0,1)
  DirMode = 2
  FaceMakerClass = Part::FaceMakerBullseye
  LengthFwd = 2.4
  LengthRev = 0
  Placement = pos=(103.7,29,6.77) rot=(0,-1,0;1.5708rad)
  Solid = true
  Symmetric = false
FEATURE [Sketcher::SketchObject] Sketch025
  FullyConstrained = true
  sketch-geometry (7):
    g0: LineSegment StartX=0 StartY=0 StartZ=0 EndX=0 EndY=6 EndZ=0
    g1: Circle CenterX=0 CenterY=0 CenterZ=0 NormalX=0 NormalY=0 NormalZ=1 AngleXU=0 Radius=1
    g2: Circle CenterX=8 CenterY=6 CenterZ=0 NormalX=0 NormalY=0 NormalZ=1 AngleXU=0 Radius=1
    g3: BSplineCurve PolesCount=3 KnotsCount=2 Degree=2 IsPeriodic=0
    g4: GeomPoint X=0 Y=0 Z=0
    g5: GeomPoint X=8 Y=6 Z=0
    g6: LineSegment StartX=0 StartY=6 StartZ=0 EndX=8 EndY=6 EndZ=0
  constraints (14):
    c: Coincident(g0,g-1)
    c: Distance(g0) = 6
    c: Vertical(g0)
    c: Coincident(g3,g0)
    c: Weight(g1) = 1
    c: Equal(g1,g2)
    c: InternalAlignment(g1,g3)
    c: InternalAlignment(g2,g3)
    c: InternalAlignment(g4,g3)
    c: InternalAlignment(g5,g3)
    c: Block(g3)
    c: Coincident(g6,g0)
    c: Coincident(g6,g3)
    c: Horizontal(g6)
FEATURE [Part::Extrusion] Extrude019  label="caseScrewPillarBracket007"
  Base = -> Sketch025
  Dir = (0,0,1)
  DirMode = 2
  FaceMakerClass = Part::FaceMakerBullseye
  LengthFwd = 2.4
  LengthRev = 0
  Placement = pos=(101.3,29,65.23) rot=(0,1,0;1.5708rad)
  Solid = true
  Symmetric = false
FEATURE [Part::Box] Box011  label="frontCaseScrewPillarBracket"
  AttacherType = Attacher::AttachEngine3D
  Height = 2.4
  Length = 16
  Placement = pos=(87,28,2.3) rot=(0,0,1;0rad)
  Width = 7
FEATURE [Part::Box] Box012  label="frontCaseScrewPillarBracket001"
  AttacherType = Attacher::AttachEngine3D
  Height = 2.4
  Length = 16
  Placement = pos=(87,28,67.3) rot=(0,0,1;0rad)
  Width = 7
FEATURE [Sketcher::SketchObject] Sketch026
  FullyConstrained = true
  sketch-geometry (17):
    g0: Circle CenterX=-3.5 CenterY=23.5 CenterZ=0 NormalX=0 NormalY=0 NormalZ=1 AngleXU=0 Radius=1
    g1: Circle CenterX=-1 CenterY=15.25 CenterZ=0 NormalX=0 NormalY=0 NormalZ=1 AngleXU=0 Radius=1
    g2: Circle CenterX=-3.5 CenterY=7 CenterZ=0 NormalX=0 NormalY=0 NormalZ=1 AngleXU=0 Radius=1
    g3: BSplineCurve PolesCount=3 KnotsCount=2 Degree=2 IsPeriodic=0
    g4: GeomPoint X=-3.5 Y=23.5 Z=0
    g5: GeomPoint X=-3.5 Y=7 Z=0
    g6: Circle CenterX=-4.8 CenterY=30.5 CenterZ=0 NormalX=0 NormalY=0 NormalZ=1 AngleXU=0 Radius=1
    g7: Circle CenterX=-3.5 CenterY=30.5 CenterZ=0 NormalX=0 NormalY=0 NormalZ=1 AngleXU=0 Radius=1
    g8: Circle CenterX=-3.5 CenterY=29.2 CenterZ=0 NormalX=0 NormalY=0 NormalZ=1 AngleXU=0 Radius=1
    g9: BSplineCurve PolesCount=3 KnotsCount=2 Degree=2 IsPeriodic=0
    g10: GeomPoint X=-4.8 Y=30.5 Z=0
    g11: GeomPoint X=-3.5 Y=29.2 Z=0
    g12: LineSegment StartX=-3.5 StartY=29.2 StartZ=0 EndX=-3.5 EndY=23.5 EndZ=0
    g13: LineSegment StartX=-4.8 StartY=30.5 StartZ=0 EndX=0 EndY=30.5 EndZ=0
    g14: LineSegment StartX=-3.5 StartY=5 StartZ=0 EndX=-3.5 EndY=7 EndZ=0
    g15: LineSegment StartX=0 StartY=5 StartZ=0 EndX=0 EndY=30.5 EndZ=0
    g16: LineSegment StartX=-3.5 StartY=5 StartZ=0 EndX=0 EndY=5 EndZ=0
  constraints (33):
    c: Weight(g0) = 1
    c: Equal(g0,g1)
    c: Equal(g0,g2)
    c: InternalAlignment(g0,g3)
    c: InternalAlignment(g1,g3)
    c: InternalAlignment(g2,g3)
    c: InternalAlignment(g4,g3)
    c: InternalAlignment(g5,g3)
    c: Block(g3)
    c: Weight(g6) = 1
    c: Equal(g6,g7)
    c: Equal(g6,g8)
    c: InternalAlignment(g6,g9)
    c: InternalAlignment(g7,g9)
    c: InternalAlignment(g8,g9)
    c: InternalAlignment(g10,g9)
    c: InternalAlignment(g11,g9)
    c: Block(g9)
    c: Coincident(g12,g9)
    c: Coincident(g12,g3)
    c: Vertical(g12)
    c: Coincident(g13,g9)
    c: Horizontal(g13)
    c: Distance(g13) = 4.8
    c: Coincident(g14,g3)
    c: Vertical(g14)
    c: Coincident(g15,g13)
    c: Vertical(g15)
    c: Tangent(g15,g1)
    c: Distance(g14) = 2
    c: Coincident(g16,g14)
    c: Horizontal(g16)
    c: Coincident(g15,g16)
FEATURE [Part::Feature] Face050
  shape: bbox 4.8 x 25.5 x 2e-07 mm, 1 faces, 0 solids (baked)
FEATURE [Part::Revolution] Revolve054  label="moreFrontCaseScrewPost001"
  Angle = 360
  Axis = (0,1,0)
  Base = (0,0,0)
  FaceMakerClass = Part::FaceMakerBullseye
  Placement = pos=(102.5,4.5,3.5) rot=(0,0,1;0rad)
  Solid = false
  Source = -> Face050
  Symmetric = false
FEATURE [Part::Feature] Face051
  shape: bbox 4.8 x 25.5 x 2e-07 mm, 1 faces, 0 solids (baked)
FEATURE [Part::Revolution] Revolve055  label="moreFrontCaseScrewPost002"
  Angle = 360
  Axis = (0,1,0)
  Base = (0,0,0)
  FaceMakerClass = Part::FaceMakerBullseye
  Placement = pos=(102.5,4.5,68.5) rot=(0,0,1;0rad)
  Solid = false
  Source = -> Face051
  Symmetric = false
FEATURE [Sketcher::SketchObject] Sketch027
  FullyConstrained = true
  sketch-geometry (10):
    g0: LineSegment StartX=-1.6 StartY=4.7 StartZ=0 EndX=-1.6 EndY=1.7 EndZ=0
    g1: LineSegment StartX=-3.5 StartY=4.7 StartZ=0 EndX=-1.6 EndY=4.7 EndZ=0
    g2: LineSegment StartX=-1.6 StartY=1.7 StartZ=0 EndX=-1.6 EndY=1.5 EndZ=0
    g3: LineSegment StartX=-1.6 StartY=1.5 StartZ=0 EndX=-5.2 EndY=1.5 EndZ=0
    g4: Circle CenterX=-3.5 CenterY=4.7 CenterZ=0 NormalX=0 NormalY=0 NormalZ=1 AngleXU=0 Radius=1
    g5: Circle CenterX=-3.59627 CenterY=2.99743 CenterZ=0 NormalX=0 NormalY=0 NormalZ=1 AngleXU=0 Radius=1
    g6: Circle CenterX=-5.2 CenterY=1.5 CenterZ=0 NormalX=0 NormalY=0 NormalZ=1 AngleXU=0 Radius=1
    g7: BSplineCurve PolesCount=3 KnotsCount=2 Degree=2 IsPeriodic=0
    g8: GeomPoint X=-3.5 Y=4.7 Z=0
    g9: GeomPoint X=-5.2 Y=1.5 Z=0
  constraints (23):
    c: Vertical(g0)
    c: Distance(g0) = 3
    c: Coincident(g1,g0)
    c: Horizontal(g1)
    c: Block(g0)
    c: Block(g1)
    c: Coincident(g2,g0)
    c: Vertical(g2)
    c: Distance(g2) = 0.2
    c: Coincident(g3,g2)
    c: Horizontal(g3)
    c: Block(g3)
    c: Coincident(g7,g1)
    c: Weight(g4) = 1
    c: Equal(g4,g5)
    c: Equal(g4,g6)
    c: Coincident(g7,g3)
    c: InternalAlignment(g4,g7)
    c: InternalAlignment(g5,g7)
    c: InternalAlignment(g6,g7)
    c: InternalAlignment(g8,g7)
    c: InternalAlignment(g9,g7)
    c: Block(g7)
FEATURE [Sketcher::SketchObject] Sketch028
  FullyConstrained = true
  sketch-geometry (18):
    g0: LineSegment StartX=0 StartY=3e-16 StartZ=0 EndX=0 EndY=1.7 EndZ=0
    g1: LineSegment StartX=-3.5 StartY=0 StartZ=0 EndX=-3.5 EndY=0.9 EndZ=0
    g2: Circle CenterX=-2.7 CenterY=1.7 CenterZ=0 NormalX=0 NormalY=0 NormalZ=1 AngleXU=0 Radius=1
    g3: Circle CenterX=-3.5 CenterY=1.7 CenterZ=0 NormalX=0 NormalY=0 NormalZ=1 AngleXU=0 Radius=1
    g4: Circle CenterX=-3.5 CenterY=0.9 CenterZ=0 NormalX=0 NormalY=0 NormalZ=1 AngleXU=0 Radius=1
    g5: BSplineCurve PolesCount=3 KnotsCount=2 Degree=2 IsPeriodic=0
    g6: GeomPoint X=-2.7 Y=1.7 Z=0
    g7: GeomPoint X=-3.5 Y=0.9 Z=0
    g8: LineSegment StartX=-3.5 StartY=0 StartZ=0 EndX=-3.5 EndY=-7 EndZ=0
    g9: LineSegment StartX=0 StartY=3e-16 StartZ=0 EndX=0 EndY=-7 EndZ=0
    g10: LineSegment StartX=-3.5 StartY=-7 StartZ=0 EndX=0 EndY=-7 EndZ=0
    g11: LineSegment StartX=-2.7 StartY=1.7 StartZ=0 EndX=-1.6 EndY=1.7 EndZ=0
    g12: LineSegment StartX=0 StartY=1.7 StartZ=0 EndX=0 EndY=4.5 EndZ=0
    g13: LineSegment StartX=0 StartY=4.5 StartZ=0 EndX=0 EndY=10.8 EndZ=0
    g14: LineSegment StartX=0 StartY=10.8 StartZ=0 EndX=-2 EndY=10.8 EndZ=0
    g15: LineSegment StartX=-1.6 StartY=4.7 StartZ=0 EndX=-1.6 EndY=1.7 EndZ=0
    g16: LineSegment StartX=-1.6 StartY=4.7 StartZ=0 EndX=-2 EndY=4.7 EndZ=0
    g17: LineSegment StartX=-2 StartY=4.7 StartZ=0 EndX=-2 EndY=10.8 EndZ=0
  constraints (44):
    c: Vertical(g0)
    c: Vertical(g1)
    c: Distance(g1) = 0.9
    c: Block(g0)
    c: Distance(g0) = 1.7
    c: Weight(g2) = 1
    c: Equal(g2,g3)
    c: Equal(g2,g4)
    c: Coincident(g5,g1)
    c: InternalAlignment(g2,g5)
    c: InternalAlignment(g3,g5)
    c: InternalAlignment(g4,g5)
    c: InternalAlignment(g6,g5)
    c: InternalAlignment(g7,g5)
    c: Block(g5)
    c: Coincident(g8,g1)
    c: Vertical(g8)
    c: Distance(g8) = 7
    c: Vertical(g9)
    c: Equal(g8,g9) = 7
    c: Coincident(g9,g0)
    c: Coincident(g10,g8)
    c: Coincident(g10,g9)
    c: Horizontal(g10)
    c: Coincident(g11,g5)
    c: Horizontal(g11)
    c: Coincident(g12,g0)
    c: Vertical(g12)
    c: Distance(g12) = 2.8
    c: Coincident(g13,g12)
    c: Vertical(g13)
    c: Distance(g13) = 6.3
    c: Coincident(g14,g13)
    c: Horizontal(g14)
    c: Distance(g14) = 2
    c: Vertical(g15)
    c: Distance(g15) = 3
    c: Block(g11)
    c: Coincident(g15,g11)
    c: Coincident(g16,g15)
    c: Horizontal(g16)
    c: Coincident(g17,g16)
    c: Coincident(g17,g14)
    c: Vertical(g17)
FEATURE [Part::Revolution] Revolve040  label="backCaseScrewRetainer001"
  Angle = 360
  Axis = (0,1,0)
  Base = (0,0,0)
  FaceMakerClass = Part::FaceMakerBullseye
  Placement = pos=(12.5,3,10) rot=(0,0,1;0rad)
  Solid = false
  Source = -> Face036
  Symmetric = false
FEATURE [Part::Feature] Face055
  shape: bbox 3.5 x 30.2 x 2e-07 mm, 1 faces, 0 solids (baked)
FEATURE [Part::Revolution] Revolve059  label="backCaseScrewPost"
  Angle = 360
  Axis = (0,1,0)
  Base = (0,0,0)
  FaceMakerClass = Part::FaceMakerBullseye
  Placement = pos=(12.5,4.5,10) rot=(0,0,1;0rad)
  Solid = false
  Source = -> Face055
  Symmetric = false
FEATURE [Part::Feature] Face056
  shape: bbox 3.5 x 30.2 x 2e-07 mm, 1 faces, 0 solids (baked)
FEATURE [Part::Revolution] Revolve060  label="backCaseScrewPost001"
  Angle = 360
  Axis = (0,1,0)
  Base = (0,0,0)
  FaceMakerClass = Part::FaceMakerBullseye
  Placement = pos=(12.5,4.5,62) rot=(0,0,1;0rad)
  Solid = false
  Source = -> Face056
  Symmetric = false
FEATURE [Part::Feature] Face057
  shape: bbox 3.5 x 17.8 x 2e-07 mm, 1 faces, 0 solids (baked)
FEATURE [Part::Revolution] Revolve061  label="removeToCreateScrewAndThreadedInsertHole"
  Angle = 360
  Axis = (0,1,0)
  Base = (0,0,0)
  FaceMakerClass = Part::FaceMakerBullseye
  Placement = pos=(12.5,0,10) rot=(0,0,1;0rad)
  Solid = false
  Source = -> Face057
  Symmetric = false
FEATURE [Part::Feature] Face058
  shape: bbox 3.5 x 17.8 x 2e-07 mm, 1 faces, 0 solids (baked)
FEATURE [Part::Revolution] Revolve062  label="removeToCreateScrewAndThreadedInsertHole001"
  Angle = 360
  Axis = (0,1,0)
  Base = (0,0,0)
  FaceMakerClass = Part::FaceMakerBullseye
  Placement = pos=(12.5,0,62) rot=(0,0,1;0rad)
  Solid = false
  Source = -> Face058
  Symmetric = false
FEATURE [Part::Feature] Face059
  shape: bbox 3.5 x 17.8 x 2e-07 mm, 1 faces, 0 solids (baked)
FEATURE [Part::Revolution] Revolve063  label="removeToCreateScrewAndThreadedInsertHole002"
  Angle = 360
  Axis = (0,1,0)
  Base = (0,0,0)
  FaceMakerClass = Part::FaceMakerBullseye
  Placement = pos=(89.5,0,68.5) rot=(0,0,1;0rad)
  Solid = false
  Source = -> Face059
  Symmetric = false
FEATURE [Part::Feature] Face060
  shape: bbox 3.5 x 17.8 x 2e-07 mm, 1 faces, 0 solids (baked)
FEATURE [Part::Revolution] Revolve064  label="removeToCreateScrewAndThreadedInsertHole003"
  Angle = 360
  Axis = (0,1,0)
  Base = (0,0,0)
  FaceMakerClass = Part::FaceMakerBullseye
  Placement = pos=(89.5,0,3.5) rot=(0,0,1;0rad)
  Solid = false
  Source = -> Face060
  Symmetric = false
FEATURE [Part::Feature] Face061
  shape: bbox 3.5 x 17.8 x 2e-07 mm, 1 faces, 0 solids (baked)
FEATURE [Part::Revolution] Revolve065  label="removeToCreateScrewAndThreadedInsertHole004"
  Angle = 360
  Axis = (0,1,0)
  Base = (0,0,0)
  FaceMakerClass = Part::FaceMakerBullseye
  Placement = pos=(102.5,4.7,3.5) rot=(0,0,1;0rad)
  Solid = false
  Source = -> Face061
  Symmetric = false
FEATURE [Part::Feature] Face062
  shape: bbox 3.5 x 17.8 x 2e-07 mm, 1 faces, 0 solids (baked)
FEATURE [Part::Revolution] Revolve066  label="removeToCreateScrewAndThreadedInsertHole005"
  Angle = 360
  Axis = (0,1,0)
  Base = (0,0,0)
  FaceMakerClass = Part::FaceMakerBullseye
  Placement = pos=(102.5,4.7,68.5) rot=(0,0,1;0rad)
  Solid = false
  Source = -> Face062
  Symmetric = false
FEATURE [Part::MultiFuse] Fusion047  label="makeHoles"
  Shapes = -> [Revolve066,Revolve065,Revolve064,Revolve063,Revolve062,Revolve061]
FEATURE [Part::Feature] Face063
  shape: bbox 3.6 x 3.2 x 2e-07 mm, 1 faces, 0 solids (baked)
FEATURE [Part::Revolution] Revolve067  label="moreFrontCaseScrewRetainer002"
  Angle = 360
  Axis = (0,1,0)
  Base = (0,0,0)
  FaceMakerClass = Part::FaceMakerBullseye
  Placement = pos=(102.5,4.5,68.5) rot=(0,0,1;0rad)
  Solid = false
  Source = -> Face063
  Symmetric = false
FEATURE [Part::Feature] Face064
  shape: bbox 3.6 x 3.2 x 2e-07 mm, 1 faces, 0 solids (baked)
FEATURE [Part::Revolution] Revolve068  label="moreFrontCaseScrewRetainer003"
  Angle = 360
  Axis = (0,1,0)
  Base = (0,0,0)
  FaceMakerClass = Part::FaceMakerBullseye
  Placement = pos=(102.5,4.5,3.5) rot=(0,0,1;0rad)
  Solid = false
  Source = -> Face064
  Symmetric = false
FEATURE [Part::Feature] Face065
  shape: bbox 3.5 x 17.8 x 2e-07 mm, 1 faces, 0 solids (baked)
FEATURE [Part::Revolution] Revolve069  label="removeToCreateScrewAndThreadedInsertHole006"
  Angle = 360
  Axis = (0,1,0)
  Base = (0,0,0)
  FaceMakerClass = Part::FaceMakerBullseye
  Placement = pos=(12.5,0,10) rot=(0,0,1;0rad)
  Solid = false
  Source = -> Face065
  Symmetric = false
FEATURE [Part::Feature] Face066
  shape: bbox 3.5 x 17.8 x 2e-07 mm, 1 faces, 0 solids (baked)
FEATURE [Part::Revolution] Revolve070  label="removeToCreateScrewAndThreadedInsertHole007"
  Angle = 360
  Axis = (0,1,0)
  Base = (0,0,0)
  FaceMakerClass = Part::FaceMakerBullseye
  Placement = pos=(12.5,0,62) rot=(0,0,1;0rad)
  Solid = false
  Source = -> Face066
  Symmetric = false
FEATURE [Part::Feature] Face067
  shape: bbox 3.5 x 17.8 x 2e-07 mm, 1 faces, 0 solids (baked)
FEATURE [Part::Revolution] Revolve071  label="removeToCreateScrewAndThreadedInsertHole008"
  Angle = 360
  Axis = (0,1,0)
  Base = (0,0,0)
  FaceMakerClass = Part::FaceMakerBullseye
  Placement = pos=(89.5,0,68.5) rot=(0,0,1;0rad)
  Solid = false
  Source = -> Face067
  Symmetric = false
FEATURE [Part::Feature] Face068
  shape: bbox 3.5 x 17.8 x 2e-07 mm, 1 faces, 0 solids (baked)
FEATURE [Part::Revolution] Revolve072  label="removeToCreateScrewAndThreadedInsertHole009"
  Angle = 360
  Axis = (0,1,0)
  Base = (0,0,0)
  FaceMakerClass = Part::FaceMakerBullseye
  Placement = pos=(89.5,0,3.5) rot=(0,0,1;0rad)
  Solid = false
  Source = -> Face068
  Symmetric = false
FEATURE [Part::Feature] Face069
  shape: bbox 3.5 x 17.8 x 2e-07 mm, 1 faces, 0 solids (baked)
FEATURE [Part::Feature] Face070
  shape: bbox 3.5 x 17.8 x 2e-07 mm, 1 faces, 0 solids (baked)
FEATURE [Part::Revolution] Revolve073  label="removeToCreateScrewAndThreadedInsertHole010"
  Angle = 360
  Axis = (0,1,0)
  Base = (0,0,0)
  FaceMakerClass = Part::FaceMakerBullseye
  Placement = pos=(102.5,4.7,3.5) rot=(0,0,1;0rad)
  Solid = false
  Source = -> Face069
  Symmetric = false
FEATURE [Part::Revolution] Revolve074  label="removeToCreateScrewAndThreadedInsertHole011"
  Angle = 360
  Axis = (0,1,0)
  Base = (0,0,0)
  FaceMakerClass = Part::FaceMakerBullseye
  Placement = pos=(102.5,4.7,68.5) rot=(0,0,1;0rad)
  Solid = false
  Source = -> Face070
  Symmetric = false
FEATURE [Part::MultiFuse] Fusion048  label="makeHoles001"
  Shapes = -> [Revolve074,Revolve073,Revolve072,Revolve071,Revolve070,Revolve069]
FEATURE [Part::MultiFuse] Fusion049  label="caseScrewRetainers"
  Shapes = -> [Revolve067,Revolve068,Revolve048,Revolve047,Revolve039,Revolve040]
FEATURE [Part::Cut] Cut015  label="caseScrewRetainers001"
  Base = -> Fusion049
  Tool = -> Fusion048
FEATURE [Part::MultiFuse] Fusion050  label="casePillars"
  Shapes = -> [Revolve055,Revolve054,Revolve043,Revolve046,Revolve059,Revolve060]
FEATURE [Part::Feature] Face071 .. Face076  x6 (patterned run collapsed; names and placements below)
  shape: bbox 3.5 x 17.8 x 2e-07 mm, 1 faces, 0 solids (baked)
FEATURE [Part::Revolution] Revolve075  label="removeToCreateScrewAndThreadedInsertHole012"
  Angle = 360
  Axis = (0,1,0)
  Base = (0,0,0)
  FaceMakerClass = Part::FaceMakerBullseye
  Placement = pos=(12.5,0,10) rot=(0,0,1;0rad)
  Solid = false
  Source = -> Face071
  Symmetric = false
FEATURE [Part::Revolution] Revolve076  label="removeToCreateScrewAndThreadedInsertHole013"
  Angle = 360
  Axis = (0,1,0)
  Base = (0,0,0)
  FaceMakerClass = Part::FaceMakerBullseye
  Placement = pos=(12.5,0,62) rot=(0,0,1;0rad)
  Solid = false
  Source = -> Face072
  Symmetric = false
FEATURE [Part::Revolution] Revolve077  label="removeToCreateScrewAndThreadedInsertHole014"
  Angle = 360
  Axis = (0,1,0)
  Base = (0,0,0)
  FaceMakerClass = Part::FaceMakerBullseye
  Placement = pos=(89.5,0,68.5) rot=(0,0,1;0rad)
  Solid = false
  Source = -> Face073
  Symmetric = false
FEATURE [Part::Revolution] Revolve078  label="removeToCreateScrewAndThreadedInsertHole015"
  Angle = 360
  Axis = (0,1,0)
  Base = (0,0,0)
  FaceMakerClass = Part::FaceMakerBullseye
  Placement = pos=(89.5,0,3.5) rot=(0,0,1;0rad)
  Solid = false
  Source = -> Face074
  Symmetric = false
FEATURE [Part::Revolution] Revolve079  label="removeToCreateScrewAndThreadedInsertHole016"
  Angle = 360
  Axis = (0,1,0)
  Base = (0,0,0)
  FaceMakerClass = Part::FaceMakerBullseye
  Placement = pos=(102.5,4.7,3.5) rot=(0,0,1;0rad)
  Solid = false
  Source = -> Face075
  Symmetric = false
FEATURE [Part::Revolution] Revolve080  label="removeToCreateScrewAndThreadedInsertHole017"
  Angle = 360
  Axis = (0,1,0)
  Base = (0,0,0)
  FaceMakerClass = Part::FaceMakerBullseye
  Placement = pos=(102.5,4.7,68.5) rot=(0,0,1;0rad)
  Solid = false
  Source = -> Face076
  Symmetric = false
FEATURE [Part::MultiFuse] Fusion051  label="makeHoles002"
  Shapes = -> [Revolve080,Revolve079,Revolve078,Revolve077,Revolve076,Revolve075]
FEATURE [Part::Cut] Cut016  label="caesPillars"
  Base = -> Fusion050
  Tool = -> Fusion051
FEATURE [Part::Revolution] Revolve009  label="plugHousing016"
  Angle = 360
  Axis = (0,1,0)
  Base = (0,0,0)
  FaceMakerClass = Part::FaceMakerBullseye
  Placement = pos=(0,0,36.15) rot=(0,0,1;0rad)
  Solid = false
  Source = -> Face012
  Symmetric = false
FEATURE [Part::MultiFuse] Fusion014  label="plugHousing023"
  Placement = pos=(0,0,0) rot=(0,0,1;1.5708rad)
  Shapes = -> [Revolve011,Revolve009]
FEATURE [Part::Revolution] Revolve010  label="plugHousing017"
  Angle = 360
  Axis = (0,1,0)
  Base = (0,0,0)
  FaceMakerClass = Part::FaceMakerBullseye
  Placement = pos=(0,0,36.15) rot=(0,0,1;0rad)
  Solid = false
  Source = -> Face014
  Symmetric = false
FEATURE [Part::MultiFuse] Fusion015  label="plugHousing024"
  Placement = pos=(0,0,0) rot=(0,0,1;1.5708rad)
  Shapes = -> [Revolve010,Revolve015]
FEATURE [Part::Revolution] Revolve014  label="plugHousing026"
  Angle = 360
  Axis = (0,1,0)
  Base = (0,0,0)
  FaceMakerClass = Part::FaceMakerBullseye
  Placement = pos=(0,0,36.15) rot=(0,0,1;0rad)
  Solid = false
  Source = -> Face011
  Symmetric = false
FEATURE [Part::Revolution] Revolve013  label="plugHousing025"
  Angle = 360
  Axis = (0,1,0)
  Base = (0,0,0)
  FaceMakerClass = Part::FaceMakerBullseye
  Placement = pos=(0,0,36.15) rot=(0,0,1;0rad)
  Solid = false
  Source = -> Face015
  Symmetric = false
FEATURE [Part::MultiFuse] Fusion016  label="plugHousing028"
  Placement = pos=(0,19,0) rot=(0,0,1;3.14159rad)
  Shapes = -> [Fusion014,Fusion013]
FEATURE [Part::MultiFuse] Fusion011  label="plugHousing018"
  Placement = pos=(0,0,0) rot=(0,0,1;1.5708rad)
  Shapes = -> [Revolve014,Revolve013]
FEATURE [Part::MultiFuse] Fusion012  label="plugHousing019"
  Placement = pos=(0,19,0) rot=(0,0,1;3.14159rad)
  Shapes = -> [Fusion011,Fusion015]
FEATURE [Part::MultiFuse] Fusion017  label="plugHousing029"
  Placement = pos=(122.621,0,-0.15) rot=(0,0,1;0rad)
  Shapes = -> [Fusion016,Fusion012]
FEATURE [Part::MultiFuse] Fusion052  label="casePillarRetainers"
  Shapes = -> [Extrude012,Extrude013,Extrude014,Extrude015,Extrude016,Extrude017,Extrude018,Extrude019,Box011,Box012]
FEATURE [Part::Feature] Face077
  shape: bbox 3.5 x 17.8 x 2e-07 mm, 1 faces, 0 solids (baked)
FEATURE [Part::Revolution] Revolve081  label="removeToCreateScrewAndThreadedInsertHole018"
  Angle = 360
  Axis = (0,1,0)
  Base = (0,0,0)
  FaceMakerClass = Part::FaceMakerBullseye
  Placement = pos=(62.3,30.3,19.7) rot=(0,0,1;0rad)
  Solid = false
  Source = -> Face077
  Symmetric = false
FEATURE [Part::Feature] Face078
  shape: bbox 3.5 x 17.8 x 2e-07 mm, 1 faces, 0 solids (baked)
FEATURE [Part::Revolution] Revolve082  label="removeToCreateScrewAndThreadedInsertHole019"
  Angle = 360
  Axis = (0,1,0)
  Base = (0,0,0)
  FaceMakerClass = Part::FaceMakerBullseye
  Placement = pos=(62.3,30.3,51.7) rot=(0,0,1;0rad)
  Solid = false
  Source = -> Face078
  Symmetric = false
FEATURE [Part::Feature] Face079
  shape: bbox 3.5 x 17.8 x 2e-07 mm, 1 faces, 0 solids (baked)
FEATURE [Part::Revolution] Revolve083  label="removeToCreateScrewAndThreadedInsertHole020"
  Angle = 360
  Axis = (0,1,0)
  Base = (0,0,0)
  FaceMakerClass = Part::FaceMakerBullseye
  Placement = pos=(30.3,30.3,19.7) rot=(0,0,1;0rad)
  Solid = false
  Source = -> Face079
  Symmetric = false
FEATURE [Part::Feature] Face080
  shape: bbox 3.5 x 17.8 x 2e-07 mm, 1 faces, 0 solids (baked)
FEATURE [Part::Revolution] Revolve084  label="removeToCreateScrewAndThreadedInsertHole021"
  Angle = 360
  Axis = (0,1,0)
  Base = (0,0,0)
  FaceMakerClass = Part::FaceMakerBullseye
  Placement = pos=(30.3,30.3,51.7) rot=(0,0,1;0rad)
  Solid = false
  Source = -> Face080
  Symmetric = false
FEATURE [Part::MultiFuse] Fusion053  label="createThreadedInsertHolesForFan"
  Shapes = -> [Revolve081,Revolve082,Revolve083,Revolve084]
FEATURE [Part::Cut] Cut017  label="fanScrewHousing001"
  Base = -> Fusion046
  Tool = -> Fusion053
FEATURE [Part::Feature] Face081
  shape: bbox 3.5 x 17.8 x 2e-07 mm, 1 faces, 0 solids (baked)
FEATURE [Part::Revolution] Revolve085  label="removeToCreateScrewAndThreadedInsertHole022"
  Angle = 360
  Axis = (0,1,0)
  Base = (0,0,0)
  FaceMakerClass = Part::FaceMakerBullseye
  Placement = pos=(62.3,30.3,19.7) rot=(0,0,1;0rad)
  Solid = false
  Source = -> Face081
  Symmetric = false
FEATURE [Part::Feature] Face082
  shape: bbox 3.5 x 17.8 x 2e-07 mm, 1 faces, 0 solids (baked)
FEATURE [Part::Revolution] Revolve086  label="removeToCreateScrewAndThreadedInsertHole023"
  Angle = 360
  Axis = (0,1,0)
  Base = (0,0,0)
  FaceMakerClass = Part::FaceMakerBullseye
  Placement = pos=(62.3,30.3,51.7) rot=(0,0,1;0rad)
  Solid = false
  Source = -> Face082
  Symmetric = false
FEATURE [Part::Feature] Face083
  shape: bbox 3.5 x 17.8 x 2e-07 mm, 1 faces, 0 solids (baked)
FEATURE [Part::Revolution] Revolve087  label="removeToCreateScrewAndThreadedInsertHole024"
  Angle = 360
  Axis = (0,1,0)
  Base = (0,0,0)
  FaceMakerClass = Part::FaceMakerBullseye
  Placement = pos=(30.3,30.3,19.7) rot=(0,0,1;0rad)
  Solid = false
  Source = -> Face083
  Symmetric = false
FEATURE [Part::Feature] Face084
  shape: bbox 3.5 x 17.8 x 2e-07 mm, 1 faces, 0 solids (baked)
FEATURE [Part::Revolution] Revolve088  label="removeToCreateScrewAndThreadedInsertHole025"
  Angle = 360
  Axis = (0,1,0)
  Base = (0,0,0)
  FaceMakerClass = Part::FaceMakerBullseye
  Placement = pos=(30.3,30.3,51.7) rot=(0,0,1;0rad)
  Solid = false
  Source = -> Face084
  Symmetric = false
FEATURE [Part::MultiFuse] Fusion054  label="createThreadedInsertHolesForFan001"
  Shapes = -> [Revolve085,Revolve086,Revolve087,Revolve088]
FEATURE [Part::Cut] Cut018  label="top007"
  Base = -> Fusion040
  Tool = -> Fusion054
FEATURE [Sketcher::SketchObject] Sketch029
  FullyConstrained = false
  Placement = pos=(0,0,0) rot=(1,0,0;1.5708rad)
  sketch-geometry (24):
    g0: ArcOfCircle CenterX=-4 CenterY=-10.5 CenterZ=0 NormalX=0 NormalY=0 NormalZ=1 AngleXU=0 Radius=1.5 StartAngle=6e-16 EndAngle=3.14159
    g1: ArcOfCircle CenterX=-34.2 CenterY=-10.5 CenterZ=0 NormalX=0 NormalY=0 NormalZ=1 AngleXU=0 Radius=1.5 StartAngle=0 EndAngle=3.14159
    g2: ArcOfCircle CenterX=-34.2 CenterY=-27.7 CenterZ=0 NormalX=0 NormalY=0 NormalZ=1 AngleXU=0 Radius=1.5 StartAngle=3.14159 EndAngle=6.28319
    g3: ArcOfCircle CenterX=-4 CenterY=-27.7 CenterZ=0 NormalX=0 NormalY=0 NormalZ=1 AngleXU=0 Radius=1.5 StartAngle=3.1416 EndAngle=6.28319
    g4: ArcOfCircle CenterX=-10 CenterY=-4.3 CenterZ=0 NormalX=0 NormalY=0 NormalZ=1 AngleXU=0 Radius=1.5 StartAngle=2e-16 EndAngle=3.14159
    g5: ArcOfCircle CenterX=-16.1 CenterY=-1.8 CenterZ=0 NormalX=0 NormalY=0 NormalZ=1 AngleXU=0 Radius=1.5 StartAngle=5e-16 EndAngle=3.14159
    g6: ArcOfCircle CenterX=-22.1 CenterY=-1.8 CenterZ=0 NormalX=0 NormalY=0 NormalZ=1 AngleXU=0 Radius=1.5 StartAngle=5e-16 EndAngle=3.14159
    g7: ArcOfCircle CenterX=-28.2 CenterY=-4.3 CenterZ=0 NormalX=0 NormalY=0 NormalZ=1 AngleXU=0 Radius=1.5 StartAngle=2e-16 EndAngle=3.14159
    g8: ArcOfCircle CenterX=-10 CenterY=-33.9 CenterZ=0 NormalX=0 NormalY=0 NormalZ=1 AngleXU=0 Radius=1.5 StartAngle=3.14159 EndAngle=6.28319
    g9: ArcOfCircle CenterX=-16.1 CenterY=-36.4 CenterZ=0 NormalX=0 NormalY=0 NormalZ=1 AngleXU=0 Radius=1.5 StartAngle=3.14159 EndAngle=6.28319
    g10: ArcOfCircle CenterX=-22.1 CenterY=-36.4 CenterZ=0 NormalX=0 NormalY=0 NormalZ=1 AngleXU=0 Radius=1.5 StartAngle=3.14159 EndAngle=6.28319
    g11: ArcOfCircle CenterX=-28.2 CenterY=-33.9 CenterZ=0 NormalX=0 NormalY=0 NormalZ=1 AngleXU=0 Radius=1.5 StartAngle=3.14159 EndAngle=6.28319
    g12: LineSegment StartX=-35.7 StartY=-10.5 StartZ=0 EndX=-35.7 EndY=-27.7 EndZ=0
    g13: LineSegment StartX=-32.7 StartY=-10.5 StartZ=0 EndX=-32.7 EndY=-27.7 EndZ=0
    g14: LineSegment StartX=-29.7 StartY=-33.9 StartZ=0 EndX=-29.7 EndY=-4.3 EndZ=0
    g15: LineSegment StartX=-26.7 StartY=-33.9 StartZ=0 EndX=-26.7 EndY=-4.3 EndZ=0
    g16: LineSegment StartX=-2.5 StartY=-10.5 StartZ=0 EndX=-2.5 EndY=-27.7 EndZ=0
    g17: LineSegment StartX=-8.5 StartY=-4.3 StartZ=0 EndX=-8.5 EndY=-33.9 EndZ=0
    g18: LineSegment StartX=-5.5 StartY=-10.5 StartZ=0 EndX=-5.5 EndY=-27.7 EndZ=0
    g19: LineSegment StartX=-11.5 StartY=-4.3 StartZ=0 EndX=-11.5 EndY=-33.9 EndZ=0
    g20: LineSegment StartX=-14.6 StartY=-1.8 StartZ=0 EndX=-14.6 EndY=-36.4 EndZ=0
    g21: LineSegment StartX=-17.6 StartY=-1.8 StartZ=0 EndX=-17.6 EndY=-36.4 EndZ=0
    g22: LineSegment StartX=-20.6 StartY=-36.4 StartZ=0 EndX=-20.6 EndY=-1.8 EndZ=0
    g23: LineSegment StartX=-23.6 StartY=-1.8 StartZ=0 EndX=-23.6 EndY=-36.4 EndZ=0
  constraints (48):
    c: Block(g0)
    c: Block(g1)
    c: Block(g2)
    c: Block(g3)
    c: Block(g4)
    c: Block(g5)
    c: Block(g6)
    c: Block(g7)
    c: Block(g8)
    c: Block(g9)
    c: Block(g10)
    c: Block(g11)
    c: Coincident(g12,g1)
    c: Coincident(g12,g2)
    c: Vertical(g12)
    c: Coincident(g13,g1)
    c: Coincident(g13,g2)
    c: Vertical(g13)
    c: Coincident(g14,g11)
    c: Coincident(g14,g7)
    c: Vertical(g14)
    c: Coincident(g15,g11)
    c: Coincident(g15,g7)
    c: Vertical(g15)
    c: Coincident(g16,g0)
    c: Coincident(g16,g3)
    c: Vertical(g16)
    c: Coincident(g17,g4)
    c: Coincident(g17,g8)
    c: Vertical(g17)
    c: Coincident(g18,g0)
    c: Coincident(g18,g3)
    c: Vertical(g18)
    c: Coincident(g19,g4)
    c: Coincident(g19,g8)
    c: Vertical(g19)
    c: Coincident(g20,g5)
    c: Coincident(g20,g9)
    c: Vertical(g20)
    c: Coincident(g21,g5)
    c: Coincident(g21,g9)
    c: Vertical(g21)
    c: Coincident(g22,g10)
    c: Coincident(g22,g6)
    c: Vertical(g22)
    c: Coincident(g23,g6)
    c: Coincident(g23,g10)
    c: Vertical(g23)
FEATURE [Part::Extrusion] Extrude020  label="removeToCreateFanGrillHoles"
  Base = -> Sketch029
  Dir = (0,-1,6e-16)
  DirMode = 2
  FaceMakerClass = Part::FaceMakerBullseye
  LengthFwd = 10
  LengthRev = 0
  Placement = pos=(65.4,44,54.82) rot=(0,0,1;0rad)
  Solid = true
  Symmetric = false
FEATURE [Part::MultiFuse] Fusion055  label="top008"
  Shapes = -> [Cut017,Cut018]
FEATURE [Part::Cut] Cut019  label="top009"
  Base = -> Fusion055
  Tool = -> Extrude020
FEATURE [App::MeasureDistance] Distance003  label="Distance: 71.95 mm"
  Distance = 71.9513
  P1 = (117,38,72)
  P2 = (117,38,0.0487319)
FEATURE [Sketcher::SketchObject] Sketch030
  FullyConstrained = true
  Placement = pos=(117,19,0) rot=(0.57735,0.57735,0.57735;2.0944rad)
  sketch-geometry (48):
    g0: LineSegment StartX=-49.19 StartY=69.25 StartZ=0 EndX=-49.19 EndY=66.25 EndZ=0
    g1: LineSegment StartX=-49.19 StartY=63.5 StartZ=0 EndX=-49.19 EndY=60.5 EndZ=0
    g2: LineSegment StartX=-49.19 StartY=57.75 StartZ=0 EndX=-49.19 EndY=54.75 EndZ=0
    g3: LineSegment StartX=-49.19 StartY=52 StartZ=0 EndX=-49.19 EndY=49 EndZ=0
    g4: LineSegment StartX=-49.19 StartY=46.25 StartZ=0 EndX=-49.19 EndY=43.25 EndZ=0
    g5: LineSegment StartX=-49.19 StartY=40.5 StartZ=0 EndX=-49.19 EndY=37.5 EndZ=0
    g6: LineSegment StartX=-49.19 StartY=34.5 StartZ=0 EndX=-49.19 EndY=31.5 EndZ=0
    g7: LineSegment StartX=-49.19 StartY=28.75 StartZ=0 EndX=-49.19 EndY=25.75 EndZ=0
    g8: LineSegment StartX=-49.19 StartY=23 StartZ=0 EndX=-49.19 EndY=20 EndZ=0
    g9: LineSegment StartX=-49.19 StartY=17.25 StartZ=0 EndX=-49.19 EndY=14.25 EndZ=0
    g10: LineSegment StartX=-49.19 StartY=11.5 StartZ=0 EndX=-49.19 EndY=8.5 EndZ=0
    g11: LineSegment StartX=-49.19 StartY=5.75 StartZ=0 EndX=-49.19 EndY=2.75 EndZ=0
    g12: ArcOfCircle CenterX=-1.5 CenterY=67.75 CenterZ=0 NormalX=0 NormalY=0 NormalZ=1 AngleXU=0 Radius=1.5 StartAngle=4.71239 EndAngle=7.85398
    g13: ArcOfCircle CenterX=-1.5 CenterY=62 CenterZ=0 NormalX=0 NormalY=0 NormalZ=1 AngleXU=0 Radius=1.5 StartAngle=4.71239 EndAngle=7.85398
    g14: ArcOfCircle CenterX=-1.5 CenterY=56.25 CenterZ=0 NormalX=0 NormalY=0 NormalZ=1 AngleXU=0 Radius=1.5 StartAngle=4.71239 EndAngle=7.85398
    g15: ArcOfCircle CenterX=-11.49 CenterY=50.5 CenterZ=0 NormalX=0 NormalY=0 NormalZ=1 AngleXU=0 Radius=1.5 StartAngle=4.71239 EndAngle=7.85398
    g16: ArcOfCircle CenterX=-16.28 CenterY=44.75 CenterZ=0 NormalX=0 NormalY=0 NormalZ=1 AngleXU=0 Radius=1.5 StartAngle=4.71239 EndAngle=7.85398
    g17: ArcOfCircle CenterX=-18.2337 CenterY=39 CenterZ=0 NormalX=0 NormalY=0 NormalZ=1 AngleXU=0 Radius=1.5 StartAngle=4.71485 EndAngle=7.85398
    g18: ArcOfCircle CenterX=-16.2837 CenterY=27.25 CenterZ=0 NormalX=0 NormalY=0 NormalZ=1 AngleXU=0 Radius=1.5 StartAngle=4.71485 EndAngle=7.85398
    g19: ArcOfCircle CenterX=-18.2337 CenterY=33 CenterZ=0 NormalX=0 NormalY=0 NormalZ=1 AngleXU=0 Radius=1.5 StartAngle=4.71485 EndAngle=7.85398
    g20: ArcOfCircle CenterX=-11.49 CenterY=21.5 CenterZ=0 NormalX=0 NormalY=0 NormalZ=1 AngleXU=0 Radius=1.5 StartAngle=4.71239 EndAngle=7.85398
    g21: ArcOfCircle CenterX=-1.5 CenterY=4.25 CenterZ=0 NormalX=0 NormalY=0 NormalZ=1 AngleXU=0 Radius=1.5 StartAngle=4.71239 EndAngle=7.85398
    g22: ArcOfCircle CenterX=-1.5 CenterY=10 CenterZ=0 NormalX=0 NormalY=0 NormalZ=1 AngleXU=0 Radius=1.5 StartAngle=4.71239 EndAngle=7.85398
    g23: ArcOfCircle CenterX=-1.5 CenterY=15.75 CenterZ=0 NormalX=0 NormalY=0 NormalZ=1 AngleXU=0 Radius=1.5 StartAngle=4.71239 EndAngle=7.85398
    g24: LineSegment StartX=-49.19 StartY=69.25 StartZ=0 EndX=-1.5 EndY=69.25 EndZ=0
    g25: LineSegment StartX=-49.19 StartY=66.25 StartZ=0 EndX=-1.5 EndY=66.25 EndZ=0
    g26: LineSegment StartX=-49.19 StartY=63.5 StartZ=0 EndX=-1.5 EndY=63.5 EndZ=0
    g27: LineSegment StartX=-49.19 StartY=60.5 StartZ=0 EndX=-1.5 EndY=60.5 EndZ=0
    g28: LineSegment StartX=-49.19 StartY=57.75 StartZ=0 EndX=-1.5 EndY=57.75 EndZ=0
    g29: LineSegment StartX=-49.19 StartY=54.75 StartZ=0 EndX=-1.5 EndY=54.75 EndZ=0
    g30: LineSegment StartX=-49.19 StartY=52 StartZ=0 EndX=-11.49 EndY=52 EndZ=0
    g31: LineSegment StartX=-49.19 StartY=49 StartZ=0 EndX=-11.49 EndY=49 EndZ=0
    g32: LineSegment StartX=-49.19 StartY=46.25 StartZ=0 EndX=-16.28 EndY=46.25 EndZ=0
    g33: LineSegment StartX=-49.19 StartY=43.25 StartZ=0 EndX=-16.28 EndY=43.25 EndZ=0
    g34: LineSegment StartX=-49.19 StartY=40.5 StartZ=0 EndX=-18.2337 EndY=40.5 EndZ=0
    g35: LineSegment StartX=-49.19 StartY=37.5 StartZ=0 EndX=-18.23 EndY=37.5 EndZ=0
    g36: LineSegment StartX=-49.19 StartY=34.5 StartZ=0 EndX=-18.2337 EndY=34.5 EndZ=0
    g37: LineSegment StartX=-49.19 StartY=31.5 StartZ=0 EndX=-18.23 EndY=31.5 EndZ=0
    g38: LineSegment StartX=-49.19 StartY=28.75 StartZ=0 EndX=-16.2837 EndY=28.75 EndZ=0
    g39: LineSegment StartX=-49.19 StartY=25.75 StartZ=0 EndX=-16.28 EndY=25.75 EndZ=0
    g40: LineSegment StartX=-49.19 StartY=23 StartZ=0 EndX=-11.49 EndY=23 EndZ=0
    g41: LineSegment StartX=-49.19 StartY=20 StartZ=0 EndX=-11.49 EndY=20 EndZ=0
    g42: LineSegment StartX=-49.19 StartY=17.25 StartZ=0 EndX=-1.5 EndY=17.25 EndZ=0
    g43: LineSegment StartX=-49.19 StartY=14.25 StartZ=0 EndX=-1.5 EndY=14.25 EndZ=0
    g44: LineSegment StartX=-49.19 StartY=11.5 StartZ=0 EndX=-1.5 EndY=11.5 EndZ=0
    g45: LineSegment StartX=-49.19 StartY=8.5 StartZ=0 EndX=-1.5 EndY=8.5 EndZ=0
    g46: LineSegment StartX=-49.19 StartY=5.75 StartZ=0 EndX=-1.5 EndY=5.75 EndZ=0
    g47: LineSegment StartX=-49.19 StartY=2.75 StartZ=0 EndX=-1.5 EndY=2.75 EndZ=0
  constraints (120):
    c: Vertical(g0)
    c: Distance(g0) = 3
    c: Block(g0)
    c: Vertical(g1)
    c: Distance(g1) = 3
    c: Vertical(g2)
    c: Equal(g0,g2) = 3
    c: Block(g2)
    c: Vertical(g3)
    c: Equal(g1,g3) = 3
    c: Vertical(g4)
    c: Equal(g0,g4) = 3
    c: Block(g4)
    c: Vertical(g5)
    c: Equal(g1,g5) = 3
    c: Vertical(g6)
    c: Equal(g0,g6) = 3
    c: Block(g6)
    c: Vertical(g7)
    c: Equal(g1,g7) = 3
    c: Vertical(g8)
    c: Equal(g0,g8) = 3
    c: Block(g8)
    c: Vertical(g9)
    c: Equal(g1,g9) = 3
    c: Vertical(g10)
    c: Equal(g0,g10) = 3
    c: Block(g10)
    c: Vertical(g11)
    c: Equal(g1,g11) = 3
    c: Block(g12)
    c: Block(g13)
    c: Block(g14)
    c: Block(g15)
    c: Block(g16)
    c: Block(g17)
    c: Block(g18)
    c: Block(g19)
    c: Block(g20)
    c: Block(g21)
    c: Block(g22)
    c: Block(g23)
    c: Block(g11)
    c: Block(g9)
    c: Block(g7)
    c: Block(g5)
    c: Block(g3)
    c: Block(g1)
    c: Coincident(g24,g0)
    c: Coincident(g24,g12)
    c: Horizontal(g24)
    c: Coincident(g25,g0)
    c: Coincident(g25,g12)
    c: Horizontal(g25)
    c: Coincident(g26,g1)
    c: Coincident(g26,g13)
    c: Horizontal(g26)
    c: Coincident(g27,g1)
    c: Coincident(g27,g13)
    c: Horizontal(g27)
    c: Coincident(g28,g2)
    c: Coincident(g28,g14)
    c: Horizontal(g28)
    c: Coincident(g29,g2)
    c: Coincident(g29,g14)
    c: Horizontal(g29)
    c: Coincident(g30,g3)
    c: Coincident(g30,g15)
    c: Horizontal(g30)
    c: Coincident(g31,g3)
    c: Coincident(g31,g15)
    c: Horizontal(g31)
    c: Coincident(g32,g4)
    c: Coincident(g32,g16)
    c: Horizontal(g32)
    c: Coincident(g33,g4)
    c: Coincident(g33,g16)
    c: Horizontal(g33)
    c: Coincident(g34,g5)
    c: Coincident(g34,g17)
    c: Horizontal(g34)
    c: Coincident(g35,g5)
    c: Coincident(g35,g17)
    c: Horizontal(g35)
    c: Coincident(g36,g6)
    c: Coincident(g36,g19)
    c: Horizontal(g36)
    c: Coincident(g37,g6)
    c: Coincident(g37,g19)
    c: Horizontal(g37)
    c: Coincident(g38,g7)
    c: Coincident(g38,g18)
    c: Horizontal(g38)
    c: Coincident(g39,g7)
    c: Coincident(g39,g18)
    c: Horizontal(g39)
    c: Coincident(g40,g8)
    c: Coincident(g40,g20)
    c: Horizontal(g40)
    c: Coincident(g41,g8)
    c: Coincident(g41,g20)
    c: Horizontal(g41)
    c: Coincident(g42,g9)
    c: Coincident(g42,g23)
    c: Horizontal(g42)
    c: Coincident(g43,g9)
    c: Coincident(g43,g23)
    c: Horizontal(g43)
    c: Coincident(g44,g10)
    c: Coincident(g44,g22)
    c: Horizontal(g44)
    c: Coincident(g45,g10)
    c: Coincident(g45,g22)
    c: Horizontal(g45)
    c: Coincident(g46,g11)
    c: Coincident(g46,g21)
    c: Horizontal(g46)
    c: Coincident(g47,g11)
    c: Coincident(g47,g21)
    c: Horizontal(g47)
FEATURE [Sketcher::SketchObject] Sketch031
  FullyConstrained = true
  Placement = pos=(117,19,0) rot=(0.57735,0.57735,0.57735;2.0944rad)
  sketch-geometry (24):
    g0: ArcOfCircle CenterX=-49.19 CenterY=67.75 CenterZ=0 NormalX=0 NormalY=0 NormalZ=1 AngleXU=0 Radius=1.5 StartAngle=1.5708 EndAngle=4.71239
    g1: ArcOfCircle CenterX=-49.19 CenterY=62 CenterZ=0 NormalX=0 NormalY=0 NormalZ=1 AngleXU=0 Radius=1.5 StartAngle=1.5708 EndAngle=4.71239
    g2: ArcOfCircle CenterX=-49.19 CenterY=56.25 CenterZ=0 NormalX=0 NormalY=0 NormalZ=1 AngleXU=0 Radius=1.5 StartAngle=1.5708 EndAngle=4.71239
    g3: ArcOfCircle CenterX=-49.19 CenterY=50.5 CenterZ=0 NormalX=0 NormalY=0 NormalZ=1 AngleXU=0 Radius=1.5 StartAngle=1.5708 EndAngle=4.71239
    g4: ArcOfCircle CenterX=-49.19 CenterY=44.75 CenterZ=0 NormalX=0 NormalY=0 NormalZ=1 AngleXU=0 Radius=1.5 StartAngle=1.5708 EndAngle=4.71239
    g5: ArcOfCircle CenterX=-49.19 CenterY=39 CenterZ=0 NormalX=0 NormalY=0 NormalZ=1 AngleXU=0 Radius=1.5 StartAngle=1.5708 EndAngle=4.71239
    g6: ArcOfCircle CenterX=-49.19 CenterY=33 CenterZ=0 NormalX=0 NormalY=0 NormalZ=1 AngleXU=0 Radius=1.5 StartAngle=1.5708 EndAngle=4.71239
    g7: ArcOfCircle CenterX=-49.19 CenterY=27.25 CenterZ=0 NormalX=0 NormalY=0 NormalZ=1 AngleXU=0 Radius=1.5 StartAngle=1.5708 EndAngle=4.71239
    g8: ArcOfCircle CenterX=-49.19 CenterY=21.5 CenterZ=0 NormalX=0 NormalY=0 NormalZ=1 AngleXU=0 Radius=1.5 StartAngle=1.5708 EndAngle=4.71239
    g9: ArcOfCircle CenterX=-49.19 CenterY=15.75 CenterZ=0 NormalX=0 NormalY=0 NormalZ=1 AngleXU=0 Radius=1.5 StartAngle=1.5708 EndAngle=4.71239
    g10: ArcOfCircle CenterX=-49.19 CenterY=10 CenterZ=0 NormalX=0 NormalY=0 NormalZ=1 AngleXU=0 Radius=1.5 StartAngle=1.5708 EndAngle=4.71239
    g11: ArcOfCircle CenterX=-49.19 CenterY=4.25 CenterZ=0 NormalX=0 NormalY=0 NormalZ=1 AngleXU=0 Radius=1.5 StartAngle=1.5708 EndAngle=4.71239
    g12: LineSegment StartX=-49.19 StartY=69.25 StartZ=0 EndX=-49.19 EndY=66.25 EndZ=0
    g13: LineSegment StartX=-49.19 StartY=63.5 StartZ=0 EndX=-49.19 EndY=60.5 EndZ=0
    g14: LineSegment StartX=-49.19 StartY=57.75 StartZ=0 EndX=-49.19 EndY=54.75 EndZ=0
    g15: LineSegment StartX=-49.19 StartY=52 StartZ=0 EndX=-49.19 EndY=49 EndZ=0
    g16: LineSegment StartX=-49.19 StartY=46.25 StartZ=0 EndX=-49.19 EndY=43.25 EndZ=0
    g17: LineSegment StartX=-49.19 StartY=40.5 StartZ=0 EndX=-49.19 EndY=37.5 EndZ=0
    g18: LineSegment StartX=-49.19 StartY=34.5 StartZ=0 EndX=-49.19 EndY=31.5 EndZ=0
    g19: LineSegment StartX=-49.19 StartY=28.75 StartZ=0 EndX=-49.19 EndY=25.75 EndZ=0
    g20: LineSegment StartX=-49.19 StartY=23 StartZ=0 EndX=-49.19 EndY=20 EndZ=0
    g21: LineSegment StartX=-49.19 StartY=17.25 StartZ=0 EndX=-49.19 EndY=14.25 EndZ=0
    g22: LineSegment StartX=-49.19 StartY=11.5 StartZ=0 EndX=-49.19 EndY=8.5 EndZ=0
    g23: LineSegment StartX=-49.19 StartY=5.75 StartZ=0 EndX=-49.19 EndY=2.75 EndZ=0
  constraints (48):
    c: Block(g0)
    c: Block(g1)
    c: Block(g2)
    c: Block(g3)
    c: Block(g4)
    c: Block(g5)
    c: Block(g6)
    c: Block(g7)
    c: Block(g8)
    c: Block(g9)
    c: Block(g10)
    c: Block(g11)
    c: Coincident(g12,g0)
    c: Coincident(g12,g0)
    c: Vertical(g12)
    c: Vertical(g13)
    c: Coincident(g13,g1)
    c: Vertical(g14)
    c: Coincident(g14,g2)
    c: Vertical(g15)
    c: Coincident(g15,g3)
    c: Vertical(g16)
    c: Coincident(g16,g4)
    c: Vertical(g17)
    c: Coincident(g17,g5)
    c: Vertical(g18)
    c: Coincident(g18,g6)
    c: Vertical(g19)
    c: Coincident(g19,g7)
    c: Vertical(g20)
    c: Coincident(g20,g8)
    c: Vertical(g21)
    c: Coincident(g21,g9)
    c: Vertical(g22)
    c: Coincident(g22,g10)
    c: Vertical(g23)
    c: Coincident(g23,g11)
    c: Block(g23)
    c: Block(g22)
    c: Block(g21)
    c: Block(g20)
    c: Block(g13)
    c: Block(g14)
    c: Block(g15)
    c: Block(g16)
    c: Block(g17)
    c: Block(g18)
    c: Block(g19)
FEATURE [Part::Extrusion] Extrude022
  Base = -> Sketch030
  Dir = (1,-2e-16,2e-16)
  DirMode = 2
  FaceMakerClass = Part::FaceMakerBullseye
  LengthFwd = 19
  LengthRev = 0
  Placement = pos=(-19,0,0) rot=(0,0,1;0rad)
  Solid = true
  Symmetric = false
FEATURE [Part::Fillet] Fillet022
  Base = -> Extrude022
  Edges = 24 edges r=1.49: [Edge6,Edge11,Edge18,Edge23,Edge30,Edge35,Edge42,Edge47,Edge54,Edge59,Edge66,Edge71,Edge78,Edge83,Edge90,Edge95,Edge102,Edge107,Edge114,Edge119,Edge126,Edge131,Edge138,Edge143]
FEATURE [Part::Cut] Cut020  label="top010"
  Base = -> Cut019
  Tool = -> Fillet022
FEATURE [Sketcher::SketchObject] Sketch032
  FullyConstrained = true
  Placement = pos=(117,19,0) rot=(0.57735,0.57735,0.57735;2.0944rad)
  sketch-geometry (48):
    g0: LineSegment StartX=-49.19 StartY=69.25 StartZ=0 EndX=-49.19 EndY=66.25 EndZ=0
    g1: LineSegment StartX=-49.19 StartY=63.5 StartZ=0 EndX=-49.19 EndY=60.5 EndZ=0
    g2: LineSegment StartX=-49.19 StartY=57.75 StartZ=0 EndX=-49.19 EndY=54.75 EndZ=0
    g3: LineSegment StartX=-49.19 StartY=52 StartZ=0 EndX=-49.19 EndY=49 EndZ=0
    g4: LineSegment StartX=-49.19 StartY=46.25 StartZ=0 EndX=-49.19 EndY=43.25 EndZ=0
    g5: LineSegment StartX=-49.19 StartY=40.5 StartZ=0 EndX=-49.19 EndY=37.5 EndZ=0
    g6: LineSegment StartX=-49.19 StartY=34.5 StartZ=0 EndX=-49.19 EndY=31.5 EndZ=0
    g7: LineSegment StartX=-49.19 StartY=28.75 StartZ=0 EndX=-49.19 EndY=25.75 EndZ=0
    g8: LineSegment StartX=-49.19 StartY=23 StartZ=0 EndX=-49.19 EndY=20 EndZ=0
    g9: LineSegment StartX=-49.19 StartY=17.25 StartZ=0 EndX=-49.19 EndY=14.25 EndZ=0
    g10: LineSegment StartX=-49.19 StartY=11.5 StartZ=0 EndX=-49.19 EndY=8.5 EndZ=0
    g11: LineSegment StartX=-49.19 StartY=5.75 StartZ=0 EndX=-49.19 EndY=2.75 EndZ=0
    g12: ArcOfCircle CenterX=-1.5 CenterY=67.75 CenterZ=0 NormalX=0 NormalY=0 NormalZ=1 AngleXU=0 Radius=1.5 StartAngle=4.71239 EndAngle=7.85398
    g13: ArcOfCircle CenterX=-1.5 CenterY=62 CenterZ=0 NormalX=0 NormalY=0 NormalZ=1 AngleXU=0 Radius=1.5 StartAngle=4.71239 EndAngle=7.85398
    g14: ArcOfCircle CenterX=-1.5 CenterY=56.25 CenterZ=0 NormalX=0 NormalY=0 NormalZ=1 AngleXU=0 Radius=1.5 StartAngle=4.71239 EndAngle=7.85398
    g15: ArcOfCircle CenterX=-11.49 CenterY=50.5 CenterZ=0 NormalX=0 NormalY=0 NormalZ=1 AngleXU=0 Radius=1.5 StartAngle=4.71239 EndAngle=7.85398
    g16: ArcOfCircle CenterX=-16.28 CenterY=44.75 CenterZ=0 NormalX=0 NormalY=0 NormalZ=1 AngleXU=0 Radius=1.5 StartAngle=4.71239 EndAngle=7.85398
    g17: ArcOfCircle CenterX=-18.2337 CenterY=39 CenterZ=0 NormalX=0 NormalY=0 NormalZ=1 AngleXU=0 Radius=1.5 StartAngle=4.71485 EndAngle=7.85398
    g18: ArcOfCircle CenterX=-16.2837 CenterY=27.25 CenterZ=0 NormalX=0 NormalY=0 NormalZ=1 AngleXU=0 Radius=1.5 StartAngle=4.71485 EndAngle=7.85398
    g19: ArcOfCircle CenterX=-18.2337 CenterY=33 CenterZ=0 NormalX=0 NormalY=0 NormalZ=1 AngleXU=0 Radius=1.5 StartAngle=4.71485 EndAngle=7.85398
    g20: ArcOfCircle CenterX=-11.49 CenterY=21.5 CenterZ=0 NormalX=0 NormalY=0 NormalZ=1 AngleXU=0 Radius=1.5 StartAngle=4.71239 EndAngle=7.85398
    g21: ArcOfCircle CenterX=-1.5 CenterY=4.25 CenterZ=0 NormalX=0 NormalY=0 NormalZ=1 AngleXU=0 Radius=1.5 StartAngle=4.71239 EndAngle=7.85398
    g22: ArcOfCircle CenterX=-1.5 CenterY=10 CenterZ=0 NormalX=0 NormalY=0 NormalZ=1 AngleXU=0 Radius=1.5 StartAngle=4.71239 EndAngle=7.85398
    g23: ArcOfCircle CenterX=-1.5 CenterY=15.75 CenterZ=0 NormalX=0 NormalY=0 NormalZ=1 AngleXU=0 Radius=1.5 StartAngle=4.71239 EndAngle=7.85398
    g24: LineSegment StartX=-49.19 StartY=69.25 StartZ=0 EndX=-1.5 EndY=69.25 EndZ=0
    g25: LineSegment StartX=-49.19 StartY=66.25 StartZ=0 EndX=-1.5 EndY=66.25 EndZ=0
    g26: LineSegment StartX=-49.19 StartY=63.5 StartZ=0 EndX=-1.5 EndY=63.5 EndZ=0
    g27: LineSegment StartX=-49.19 StartY=60.5 StartZ=0 EndX=-1.5 EndY=60.5 EndZ=0
    g28: LineSegment StartX=-49.19 StartY=57.75 StartZ=0 EndX=-1.5 EndY=57.75 EndZ=0
    g29: LineSegment StartX=-49.19 StartY=54.75 StartZ=0 EndX=-1.5 EndY=54.75 EndZ=0
    g30: LineSegment StartX=-49.19 StartY=52 StartZ=0 EndX=-11.49 EndY=52 EndZ=0
    g31: LineSegment StartX=-49.19 StartY=49 StartZ=0 EndX=-11.49 EndY=49 EndZ=0
    g32: LineSegment StartX=-49.19 StartY=46.25 StartZ=0 EndX=-16.28 EndY=46.25 EndZ=0
    g33: LineSegment StartX=-49.19 StartY=43.25 StartZ=0 EndX=-16.28 EndY=43.25 EndZ=0
    g34: LineSegment StartX=-49.19 StartY=40.5 StartZ=0 EndX=-18.2337 EndY=40.5 EndZ=0
    g35: LineSegment StartX=-49.19 StartY=37.5 StartZ=0 EndX=-18.23 EndY=37.5 EndZ=0
    g36: LineSegment StartX=-49.19 StartY=34.5 StartZ=0 EndX=-18.2337 EndY=34.5 EndZ=0
    g37: LineSegment StartX=-49.19 StartY=31.5 StartZ=0 EndX=-18.23 EndY=31.5 EndZ=0
    g38: LineSegment StartX=-49.19 StartY=28.75 StartZ=0 EndX=-16.2837 EndY=28.75 EndZ=0
    g39: LineSegment StartX=-49.19 StartY=25.75 StartZ=0 EndX=-16.28 EndY=25.75 EndZ=0
    g40: LineSegment StartX=-49.19 StartY=23 StartZ=0 EndX=-11.49 EndY=23 EndZ=0
    g41: LineSegment StartX=-49.19 StartY=20 StartZ=0 EndX=-11.49 EndY=20 EndZ=0
    g42: LineSegment StartX=-49.19 StartY=17.25 StartZ=0 EndX=-1.5 EndY=17.25 EndZ=0
    g43: LineSegment StartX=-49.19 StartY=14.25 StartZ=0 EndX=-1.5 EndY=14.25 EndZ=0
    g44: LineSegment StartX=-49.19 StartY=11.5 StartZ=0 EndX=-1.5 EndY=11.5 EndZ=0
    g45: LineSegment StartX=-49.19 StartY=8.5 StartZ=0 EndX=-1.5 EndY=8.5 EndZ=0
    g46: LineSegment StartX=-49.19 StartY=5.75 StartZ=0 EndX=-1.5 EndY=5.75 EndZ=0
    g47: LineSegment StartX=-49.19 StartY=2.75 StartZ=0 EndX=-1.5 EndY=2.75 EndZ=0
  constraints (120):
    c: Vertical(g0)
    c: Distance(g0) = 3
    c: Block(g0)
    c: Vertical(g1)
    c: Distance(g1) = 3
    c: Vertical(g2)
    c: Equal(g0,g2) = 3
    c: Block(g2)
    c: Vertical(g3)
    c: Equal(g1,g3) = 3
    c: Vertical(g4)
    c: Equal(g0,g4) = 3
    c: Block(g4)
    c: Vertical(g5)
    c: Equal(g1,g5) = 3
    c: Vertical(g6)
    c: Equal(g0,g6) = 3
    c: Block(g6)
    c: Vertical(g7)
    c: Equal(g1,g7) = 3
    c: Vertical(g8)
    c: Equal(g0,g8) = 3
    c: Block(g8)
    c: Vertical(g9)
    c: Equal(g1,g9) = 3
    c: Vertical(g10)
    c: Equal(g0,g10) = 3
    c: Block(g10)
    c: Vertical(g11)
    c: Equal(g1,g11) = 3
    c: Block(g12)
    c: Block(g13)
    c: Block(g14)
    c: Block(g15)
    c: Block(g16)
    c: Block(g17)
    c: Block(g18)
    c: Block(g19)
    c: Block(g20)
    c: Block(g21)
    c: Block(g22)
    c: Block(g23)
    c: Block(g11)
    c: Block(g9)
    c: Block(g7)
    c: Block(g5)
    c: Block(g3)
    c: Block(g1)
    c: Coincident(g24,g0)
    c: Coincident(g24,g12)
    c: Horizontal(g24)
    c: Coincident(g25,g0)
    c: Coincident(g25,g12)
    c: Horizontal(g25)
    c: Coincident(g26,g1)
    c: Coincident(g26,g13)
    c: Horizontal(g26)
    c: Coincident(g27,g1)
    c: Coincident(g27,g13)
    c: Horizontal(g27)
    c: Coincident(g28,g2)
    c: Coincident(g28,g14)
    c: Horizontal(g28)
    c: Coincident(g29,g2)
    c: Coincident(g29,g14)
    c: Horizontal(g29)
    c: Coincident(g30,g3)
    c: Coincident(g30,g15)
    c: Horizontal(g30)
    c: Coincident(g31,g3)
    c: Coincident(g31,g15)
    c: Horizontal(g31)
    c: Coincident(g32,g4)
    c: Coincident(g32,g16)
    c: Horizontal(g32)
    c: Coincident(g33,g4)
    c: Coincident(g33,g16)
    c: Horizontal(g33)
    c: Coincident(g34,g5)
    c: Coincident(g34,g17)
    c: Horizontal(g34)
    c: Coincident(g35,g5)
    c: Coincident(g35,g17)
    c: Horizontal(g35)
    c: Coincident(g36,g6)
    c: Coincident(g36,g19)
    c: Horizontal(g36)
    c: Coincident(g37,g6)
    c: Coincident(g37,g19)
    c: Horizontal(g37)
    c: Coincident(g38,g7)
    c: Coincident(g38,g18)
    c: Horizontal(g38)
    c: Coincident(g39,g7)
    c: Coincident(g39,g18)
    c: Horizontal(g39)
    c: Coincident(g40,g8)
    c: Coincident(g40,g20)
    c: Horizontal(g40)
    c: Coincident(g41,g8)
    c: Coincident(g41,g20)
    c: Horizontal(g41)
    c: Coincident(g42,g9)
    c: Coincident(g42,g23)
    c: Horizontal(g42)
    c: Coincident(g43,g9)
    c: Coincident(g43,g23)
    c: Horizontal(g43)
    c: Coincident(g44,g10)
    c: Coincident(g44,g22)
    c: Horizontal(g44)
    c: Coincident(g45,g10)
    c: Coincident(g45,g22)
    c: Horizontal(g45)
    c: Coincident(g46,g11)
    c: Coincident(g46,g21)
    c: Horizontal(g46)
    c: Coincident(g47,g11)
    c: Coincident(g47,g21)
    c: Horizontal(g47)
FEATURE [Part::Extrusion] Extrude023
  Base = -> Sketch032
  Dir = (1,-2e-16,2e-16)
  DirMode = 2
  FaceMakerClass = Part::FaceMakerBullseye
  LengthFwd = 19
  LengthRev = 0
  Placement = pos=(-19,0,0) rot=(0,0,1;0rad)
  Solid = true
  Symmetric = false
FEATURE [Part::Fillet] Fillet023
  Base = -> Extrude023
  Edges = <same value as first occurrence — deduplicated (x6 in doc)>
  Placement = pos=(0,0.05,0) rot=(0,0,1;0rad)
FEATURE [Part::Cut] Cut014  label="bottom003"
  Base = -> Cut007
  Tool = -> Fusion047
FEATURE [Part::Cut] Cut021  label="bottom004"
  Base = -> Cut014
  Tool = -> Fillet023
FEATURE [Sketcher::SketchObject] Sketch033
  FullyConstrained = true
  Placement = pos=(117,19,0) rot=(0.57735,0.57735,0.57735;2.0944rad)
  sketch-geometry (8):
    g0: LineSegment StartX=-49.19 StartY=69.25 StartZ=0 EndX=-49.19 EndY=66.25 EndZ=0
    g1: LineSegment StartX=-49.19 StartY=5.75 StartZ=0 EndX=-49.19 EndY=2.75 EndZ=0
    g2: ArcOfCircle CenterX=-1.5 CenterY=67.75 CenterZ=0 NormalX=0 NormalY=0 NormalZ=1 AngleXU=0 Radius=1.5 StartAngle=4.71239 EndAngle=7.85398
    g3: ArcOfCircle CenterX=-1.5 CenterY=4.25 CenterZ=0 NormalX=0 NormalY=0 NormalZ=1 AngleXU=0 Radius=1.5 StartAngle=4.71239 EndAngle=7.85398
    g4: LineSegment StartX=-49.19 StartY=69.25 StartZ=0 EndX=-1.5 EndY=69.25 EndZ=0
    g5: LineSegment StartX=-49.19 StartY=66.25 StartZ=0 EndX=-1.5 EndY=66.25 EndZ=0
    g6: LineSegment StartX=-49.19 StartY=5.75 StartZ=0 EndX=-1.5 EndY=5.75 EndZ=0
    g7: LineSegment StartX=-49.19 StartY=2.75 StartZ=0 EndX=-1.5 EndY=2.75 EndZ=0
  constraints (19):
    c: Vertical(g0)
    c: Distance(g0) = 3
    c: Block(g0)
    c: Vertical(g1)
    c: Block(g2)
    c: Block(g3)
    c: Block(g1)
    c: Coincident(g4,g0)
    c: Coincident(g4,g2)
    c: Horizontal(g4)
    c: Coincident(g5,g0)
    c: Coincident(g5,g2)
    c: Horizontal(g5)
    c: Coincident(g6,g1)
    c: Coincident(g6,g3)
    c: Horizontal(g6)
    c: Coincident(g7,g1)
    c: Coincident(g7,g3)
    c: Horizontal(g7)
FEATURE [Sketcher::SketchObject] Sketch034
  FullyConstrained = true
  Placement = pos=(117,19,0) rot=(0.57735,0.57735,0.57735;2.0944rad)
  sketch-geometry (8):
    g0: LineSegment StartX=-49.19 StartY=63.5 StartZ=0 EndX=-49.19 EndY=60.5 EndZ=0
    g1: LineSegment StartX=-49.19 StartY=11.5 StartZ=0 EndX=-49.19 EndY=8.5 EndZ=0
    g2: ArcOfCircle CenterX=-1.5 CenterY=62 CenterZ=0 NormalX=0 NormalY=0 NormalZ=1 AngleXU=0 Radius=1.5 StartAngle=4.71239 EndAngle=7.85398
    g3: ArcOfCircle CenterX=-1.5 CenterY=10 CenterZ=0 NormalX=0 NormalY=0 NormalZ=1 AngleXU=0 Radius=1.5 StartAngle=4.71239 EndAngle=7.85398
    g4: LineSegment StartX=-49.19 StartY=63.5 StartZ=0 EndX=-1.5 EndY=63.5 EndZ=0
    g5: LineSegment StartX=-49.19 StartY=60.5 StartZ=0 EndX=-1.5 EndY=60.5 EndZ=0
    g6: LineSegment StartX=-49.19 StartY=11.5 StartZ=0 EndX=-1.5 EndY=11.5 EndZ=0
    g7: LineSegment StartX=-49.19 StartY=8.5 StartZ=0 EndX=-1.5 EndY=8.5 EndZ=0
  constraints (19):
    c: Vertical(g0)
    c: Distance(g0) = 3
    c: Vertical(g1)
    c: Block(g1)
    c: Block(g2)
    c: Block(g3)
    c: Block(g0)
    c: Coincident(g4,g0)
    c: Coincident(g4,g2)
    c: Horizontal(g4)
    c: Coincident(g5,g0)
    c: Coincident(g5,g2)
    c: Horizontal(g5)
    c: Coincident(g6,g1)
    c: Coincident(g6,g3)
    c: Horizontal(g6)
    c: Coincident(g7,g1)
    c: Coincident(g7,g3)
    c: Horizontal(g7)
FEATURE [Part::Extrusion] Extrude024
  Base = -> Sketch033
  Dir = (1,0,0)
  DirMode = 2
  FaceMakerClass = Part::FaceMakerBullseye
  LengthFwd = 10
  LengthRev = 0
  Solid = true
  Symmetric = false
FEATURE [Part::Extrusion] Extrude025
  Base = -> Sketch034
  Dir = (1,0,0)
  DirMode = 2
  FaceMakerClass = Part::FaceMakerBullseye
  LengthFwd = 10
  LengthRev = 0
  Solid = true
  Symmetric = false
FEATURE [Part::Fillet] Fillet024  label="removeFromtMoreFrontCaseScrewRetainers"
  Base = -> Extrude024
  Edges = 4 edges r=1.49: [Edge6,Edge11,Edge18,Edge23]
  Placement = pos=(-11,0,0) rot=(0,0,1;0rad)
FEATURE [Part::Fillet] Fillet025  label="removeFromtMoreFrontCaseScrewRetainers001"
  Base = -> Extrude025
  Edges = 4 edges r=1.49: [Edge6,Edge11,Edge18,Edge23]
  Placement = pos=(-19,0,0) rot=(0,0,1;0rad)
FEATURE [Part::Cut] Cut022
  Base = -> Cut015
  Tool = -> Fillet025
FEATURE [Part::Cut] Cut023  label="screwRetainers"
  Base = -> Cut022
  Tool = -> Fillet024
FEATURE [Part::MultiFuse] Fusion056  label="bottom005"
  Shapes = -> [Fusion044,Cut021]
FEATURE [Part::MultiFuse] Fusion057  label="casePillars001"
  Shapes = -> [Cut016,Fusion052]
FEATURE [Part::MultiFuse] Fusion058  label="bottom006"
  Shapes = -> [Fusion056,Cut023]
FEATURE [Part::MultiFuse] Fusion059  label="bottom007"
  Shapes = -> [Fusion058,Fillet005]
FEATURE [Part::MultiFuse] Fusion060  label="bottom008"
  Shapes = -> [Fusion059,Fusion]
FEATURE [Part::MultiFuse] Fusion061  label="top011"
  Shapes = -> [Cut006,Cut020]
FEATURE [Part::MultiFuse] Fusion062  label="top012"
  Shapes = -> [Fusion057,Fusion061]
FEATURE [Sketcher::SketchObject] Sketch035  label="topSketch007"
  FullyConstrained = true
  sketch-geometry (6):
    g0: LineSegment StartX=19 StartY=38 StartZ=0 EndX=117 EndY=38 EndZ=0
    g1: ArcOfCircle CenterX=19 CenterY=19 CenterZ=0 NormalX=0 NormalY=0 NormalZ=1 AngleXU=0 Radius=19 StartAngle=1.5708 EndAngle=3.14159
    g2: LineSegment StartX=117 StartY=38 StartZ=0 EndX=117 EndY=19 EndZ=0
    g3: LineSegment StartX=98 StartY=1.0161e-12 StartZ=0 EndX=5.22862e-06 EndY=1.0161e-12 EndZ=0
    g4: LineSegment StartX=5.22862e-06 StartY=19 StartZ=0 EndX=5.22862e-06 EndY=1.0161e-12 EndZ=0
    g5: ArcOfCircle CenterX=98 CenterY=19 CenterZ=0 NormalX=0 NormalY=0 NormalZ=1 AngleXU=0 Radius=19 StartAngle=4.71239 EndAngle=6.28319
  constraints (16):
    c: Horizontal(g0)
    c: Distance(g0) = 98
    c: Coincident(g1,g0)
    c: Block(g1)
    c: Coincident(g2,g0)
    c: Vertical(g2)
    c: Distance(g2) = 19
    c: Horizontal(g3)
    c: Coincident(g4,g1)
    c: Vertical(g4)
    c: Coincident(g3,g4)
    c: Block(g3)
    c: Coincident(g5,g2)
    c: Coincident(g5,g3)
    c: Block(g0)
    c: Block(g5)
FEATURE [Part::Extrusion] Extrude026  label="sideA001"
  Base = -> Sketch035
  Dir = (0,0,1)
  DirMode = 2
  FaceMakerClass = Part::FaceMakerBullseye
  LengthFwd = 3
  LengthRev = 0
  Placement = pos=(0,0,-2.7) rot=(0,0,1;0rad)
  Solid = true
  Symmetric = false
FEATURE [Sketcher::SketchObject] Sketch036  label="topSketch008"
  FullyConstrained = true
  sketch-geometry (6):
    g0: LineSegment StartX=19 StartY=38 StartZ=0 EndX=117 EndY=38 EndZ=0
    g1: ArcOfCircle CenterX=19 CenterY=19 CenterZ=0 NormalX=0 NormalY=0 NormalZ=1 AngleXU=0 Radius=19 StartAngle=1.5708 EndAngle=3.14159
    g2: LineSegment StartX=117 StartY=38 StartZ=0 EndX=117 EndY=19 EndZ=0
    g3: LineSegment StartX=98 StartY=1.0161e-12 StartZ=0 EndX=5.22862e-06 EndY=1.0161e-12 EndZ=0
    g4: LineSegment StartX=5.22862e-06 StartY=19 StartZ=0 EndX=5.22862e-06 EndY=1.0161e-12 EndZ=0
    g5: ArcOfCircle CenterX=98 CenterY=19 CenterZ=0 NormalX=0 NormalY=0 NormalZ=1 AngleXU=0 Radius=19 StartAngle=4.71239 EndAngle=6.28319
  constraints (16):
    c: Horizontal(g0)
    c: Distance(g0) = 98
    c: Coincident(g1,g0)
    c: Block(g1)
    c: Coincident(g2,g0)
    c: Vertical(g2)
    c: Distance(g2) = 19
    c: Horizontal(g3)
    c: Coincident(g4,g1)
    c: Vertical(g4)
    c: Coincident(g3,g4)
    c: Block(g3)
    c: Coincident(g5,g2)
    c: Coincident(g5,g3)
    c: Block(g0)
    c: Block(g5)
FEATURE [Part::Extrusion] Extrude027  label="sideB001"
  Base = -> Sketch036
  Dir = (0,0,1)
  DirMode = 2
  FaceMakerClass = Part::FaceMakerBullseye
  LengthFwd = 3
  LengthRev = 0
  Placement = pos=(0,0,71.7) rot=(0,0,1;0rad)
  Solid = true
  Symmetric = false
FEATURE [Part::MultiFuse] Fusion064  label="removeFromBottom"
  Shapes = -> [Extrude026,Extrude027]
FEATURE [Part::Cut] Cut024  label="bottom009"
  Base = -> Fusion060
  Tool = -> Fusion064
FEATURE [Sketcher::SketchObject] Sketch037  label="topSketch009"
  FullyConstrained = true
  sketch-geometry (8):
    g0: ArcOfCircle CenterX=19 CenterY=19.1201 CenterZ=0 NormalX=0 NormalY=0 NormalZ=1 AngleXU=0 Radius=18.8799 StartAngle=1.5708 EndAngle=3.14793
    g1: LineSegment StartX=0.120501 StartY=19.0004 StartZ=0 EndX=0.120501 EndY=0.000382114 EndZ=0
    g2: LineSegment StartX=19 StartY=38 StartZ=0 EndX=124 EndY=38 EndZ=0
    g3: LineSegment StartX=0.120501 StartY=0.000382114 StartZ=0 EndX=105.121 EndY=0.000382114 EndZ=0
    g4: LineSegment StartX=124 StartY=38 StartZ=0 EndX=125.616 EndY=38 EndZ=0
    g5: LineSegment StartX=105.121 StartY=0.000382114 StartZ=0 EndX=106.736 EndY=0.000382114 EndZ=0
    g6: ArcOfCircle CenterX=106.616 CenterY=19 CenterZ=0 NormalX=0 NormalY=0 NormalZ=1 AngleXU=0 Radius=19 StartAngle=4.71873 EndAngle=6.28319
    g7: LineSegment StartX=125.616 StartY=38 StartZ=0 EndX=125.616 EndY=19 EndZ=0
  constraints (21):
    c: Block(g0)
    c: Coincident(g1,g0)
    c: Vertical(g1)
    c: Horizontal(g2)
    c: Distance(g2) = 105
    c: Coincident(g2,g0)
    c: Distance(g1) = 19
    c: Coincident(g3,g1)
    c: Horizontal(g3)
    c: Distance(g3) = 105
    c: Coincident(g4,g2)
    c: Horizontal(g4)
    c: Distance(g4) = 1.61553
    c: Horizontal(g5)
    c: Equal(g4,g5) = 1.61553
    c: Coincident(g5,g3)
    c: Block(g6)
    c: Coincident(g6,g5)
    c: Coincident(g7,g4)
    c: Coincident(g7,g6)
    c: Vertical(g7)
FEATURE [Part::Extrusion] Extrude028  label="sideB"
  Base = -> Sketch037
  Dir = (0,0,1)
  DirMode = 2
  FaceMakerClass = Part::FaceMakerBullseye
  LengthFwd = 3
  LengthRev = 0
  Placement = pos=(0,0,72) rot=(0,0,1;0rad)
  Solid = true
  Symmetric = false
FEATURE [Sketcher::SketchObject] Sketch038  label="topSketch010"
  FullyConstrained = true
  sketch-geometry (22):
    g0: LineSegment StartX=5.21097e-06 StartY=3 StartZ=0 EndX=5.21097e-06 EndY=19 EndZ=0
    g1: ArcOfCircle CenterX=19 CenterY=19 CenterZ=0 NormalX=0 NormalY=0 NormalZ=1 AngleXU=0 Radius=19 StartAngle=1.5708 EndAngle=3.14159
    g2: ArcOfCircle CenterX=19 CenterY=19 CenterZ=0 NormalX=0 NormalY=0 NormalZ=1 AngleXU=0 Radius=16 StartAngle=1.5708 EndAngle=3.14159
    g3: LineSegment StartX=114 StartY=35 StartZ=0 EndX=19 EndY=35 EndZ=0
    g4: LineSegment StartX=5.21097e-06 StartY=3 StartZ=0 EndX=5.21097e-06 EndY=0 EndZ=0
    g5: LineSegment StartX=3 StartY=0 StartZ=0 EndX=5.21097e-06 EndY=0 EndZ=0
    g6: LineSegment StartX=3 StartY=19 StartZ=0 EndX=3 EndY=0 EndZ=0
    g7: LineSegment StartX=19 StartY=38 StartZ=0 EndX=124 EndY=38 EndZ=0
    g8: Circle CenterX=119 CenterY=35 CenterZ=0 NormalX=0 NormalY=0 NormalZ=1 AngleXU=0 Radius=1
    g9: Circle CenterX=121 CenterY=35 CenterZ=0 NormalX=0 NormalY=0 NormalZ=1 AngleXU=0 Radius=1
    g10: Circle CenterX=121 CenterY=33 CenterZ=0 NormalX=0 NormalY=0 NormalZ=1 AngleXU=0 Radius=1
    g11: BSplineCurve PolesCount=3 KnotsCount=2 Degree=2 IsPeriodic=0
    g12: GeomPoint X=119 Y=35 Z=0
    g13: GeomPoint X=121 Y=33 Z=0
    g14: LineSegment StartX=119 StartY=35 StartZ=0 EndX=114 EndY=35 EndZ=0
    g15: ArcOfCircle CenterX=105 CenterY=19 CenterZ=0 NormalX=0 NormalY=0 NormalZ=1 AngleXU=0 Radius=16 StartAngle=5.60905 EndAngle=6.28319
    g16: LineSegment StartX=121 StartY=33 StartZ=0 EndX=121 EndY=19 EndZ=0
    g17: LineSegment StartX=117.5 StartY=9.01251 StartZ=0 EndX=121.163 EndY=9.0125 EndZ=0
    g18: ArcOfCircle CenterX=105 CenterY=19 CenterZ=0 NormalX=0 NormalY=0 NormalZ=1 AngleXU=0 Radius=20.6155 StartAngle=5.7297 EndAngle=6.28319
    g19: LineSegment StartX=121.163 StartY=9.0125 StartZ=0 EndX=122.538 EndY=8.16329 EndZ=0
    g20: LineSegment StartX=124 StartY=38 StartZ=0 EndX=125.616 EndY=38 EndZ=0
    g21: LineSegment StartX=125.616 StartY=19 StartZ=0 EndX=125.616 EndY=38 EndZ=0
  constraints (49):
    c: Vertical(g0)
    c: Block(g0)
    c: Coincident(g1,g0)
    c: Block(g1)
    c: Coincident(g2,g1)
    c: Block(g2)
    c: Coincident(g3,g2)
    c: Horizontal(g3)
    c: Tangent(g3,g2)
    c: Coincident(g4,g0)
    c: Distance(g4) = 3
    c: Vertical(g4)
    c: Coincident(g5,g4)
    c: Horizontal(g5)
    c: Coincident(g6,g2)
    c: Coincident(g6,g5)
    c: Vertical(g6)
    c: Horizontal(g7)
    c: Distance(g7) = 105
    c: Coincident(g7,g1)
    c: Block(g3)
    c: Weight(g8) = 1
    c: Equal(g8,g9)
    c: Equal(g8,g10)
    c: InternalAlignment(g8,g11)
    c: InternalAlignment(g9,g11)
    c: InternalAlignment(g10,g11)
    c: InternalAlignment(g12,g11)
    c: InternalAlignment(g13,g11)
    c: Block(g11)
    c: Coincident(g14,g11)
    c: Coincident(g14,g3)
    c: Horizontal(g14)
    c: Block(g15)
    c: Coincident(g16,g11)
    c: Coincident(g16,g15)
    c: Vertical(g16)
    c: Distance(g16) = 14
    c: Coincident(g17,g15)
    c: Block(g18)
    c: Coincident(g19,g18)
    c: Coincident(g20,g7)
    c: Horizontal(g20)
    c: Vertical(g21)
    c: Coincident(g20,g21)
    c: Block(g20)
    c: Block(g21)
    c: Block(g19)
    c: Block(g17)
FEATURE [Part::Extrusion] Extrude029
  Base = -> Sketch038
  Dir = (0,0,1)
  DirMode = 2
  FaceMakerClass = Part::FaceMakerBullseye
  LengthFwd = 72
  LengthRev = 0
  Solid = true
  Symmetric = false
FEATURE [Part::Feature] Face085
  shape: bbox 4.8 x 25.5 x 2e-07 mm, 1 faces, 0 solids (baked)
FEATURE [Part::Revolution] Revolve089  label="moreFrontCaseScrewPost003"
  Angle = 360
  Axis = (0,1,0)
  Base = (0,0,0)
  FaceMakerClass = Part::FaceMakerBullseye
  Placement = pos=(109.5,4.5,3.5) rot=(0,0,1;0rad)
  Solid = false
  Source = -> Face085
  Symmetric = false
FEATURE [Part::Feature] Face086
  shape: bbox 4.8 x 25.5 x 2e-07 mm, 1 faces, 0 solids (baked)
FEATURE [Part::Revolution] Revolve090  label="moreFrontCaseScrewPost004"
  Angle = 360
  Axis = (0,1,0)
  Base = (0,0,0)
  FaceMakerClass = Part::FaceMakerBullseye
  Placement = pos=(109.5,4.5,68.5) rot=(0,0,1;0rad)
  Solid = false
  Source = -> Face086
  Symmetric = false
FEATURE [Part::Fillet] Fillet026  label="top013"
  Base = -> Extrude029
  Edges = 1 edges r=2: [Edge35]
FEATURE [Sketcher::SketchObject] Sketch039
  FullyConstrained = true
  sketch-geometry (7):
    g0: LineSegment StartX=0 StartY=0 StartZ=0 EndX=0 EndY=6 EndZ=0
    g1: Circle CenterX=0 CenterY=0 CenterZ=0 NormalX=0 NormalY=0 NormalZ=1 AngleXU=0 Radius=1
    g2: Circle CenterX=8 CenterY=6 CenterZ=0 NormalX=0 NormalY=0 NormalZ=1 AngleXU=0 Radius=1
    g3: BSplineCurve PolesCount=3 KnotsCount=2 Degree=2 IsPeriodic=0
    g4: GeomPoint X=0 Y=0 Z=0
    g5: GeomPoint X=8 Y=6 Z=0
    g6: LineSegment StartX=0 StartY=6 StartZ=0 EndX=8 EndY=6 EndZ=0
  constraints (14):
    c: Coincident(g0,g-1)
    c: Distance(g0) = 6
    c: Vertical(g0)
    c: Coincident(g3,g0)
    c: Weight(g1) = 1
    c: Equal(g1,g2)
    c: InternalAlignment(g1,g3)
    c: InternalAlignment(g2,g3)
    c: InternalAlignment(g4,g3)
    c: InternalAlignment(g5,g3)
    c: Block(g3)
    c: Coincident(g6,g0)
    c: Coincident(g6,g3)
    c: Horizontal(g6)
FEATURE [Sketcher::SketchObject] Sketch040
  FullyConstrained = true
  sketch-geometry (7):
    g0: LineSegment StartX=0 StartY=0 StartZ=0 EndX=0 EndY=6 EndZ=0
    g1: Circle CenterX=0 CenterY=0 CenterZ=0 NormalX=0 NormalY=0 NormalZ=1 AngleXU=0 Radius=1
    g2: Circle CenterX=8 CenterY=6 CenterZ=0 NormalX=0 NormalY=0 NormalZ=1 AngleXU=0 Radius=1
    g3: BSplineCurve PolesCount=3 KnotsCount=2 Degree=2 IsPeriodic=0
    g4: GeomPoint X=0 Y=0 Z=0
    g5: GeomPoint X=8 Y=6 Z=0
    g6: LineSegment StartX=0 StartY=6 StartZ=0 EndX=8 EndY=6 EndZ=0
  constraints (14):
    c: Coincident(g0,g-1)
    c: Distance(g0) = 6
    c: Vertical(g0)
    c: Coincident(g3,g0)
    c: Weight(g1) = 1
    c: Equal(g1,g2)
    c: InternalAlignment(g1,g3)
    c: InternalAlignment(g2,g3)
    c: InternalAlignment(g4,g3)
    c: InternalAlignment(g5,g3)
    c: Block(g3)
    c: Coincident(g6,g0)
    c: Coincident(g6,g3)
    c: Horizontal(g6)
FEATURE [Sketcher::SketchObject] Sketch041
  FullyConstrained = true
  sketch-geometry (7):
    g0: LineSegment StartX=0 StartY=0 StartZ=0 EndX=0 EndY=6 EndZ=0
    g1: Circle CenterX=0 CenterY=0 CenterZ=0 NormalX=0 NormalY=0 NormalZ=1 AngleXU=0 Radius=1
    g2: Circle CenterX=8 CenterY=6 CenterZ=0 NormalX=0 NormalY=0 NormalZ=1 AngleXU=0 Radius=1
    g3: BSplineCurve PolesCount=3 KnotsCount=2 Degree=2 IsPeriodic=0
    g4: GeomPoint X=0 Y=0 Z=0
    g5: GeomPoint X=8 Y=6 Z=0
    g6: LineSegment StartX=0 StartY=6 StartZ=0 EndX=8 EndY=6 EndZ=0
  constraints (14):
    c: Coincident(g0,g-1)
    c: Distance(g0) = 6
    c: Vertical(g0)
    c: Coincident(g3,g0)
    c: Weight(g1) = 1
    c: Equal(g1,g2)
    c: InternalAlignment(g1,g3)
    c: InternalAlignment(g2,g3)
    c: InternalAlignment(g4,g3)
    c: InternalAlignment(g5,g3)
    c: Block(g3)
    c: Coincident(g6,g0)
    c: Coincident(g6,g3)
    c: Horizontal(g6)
FEATURE [Sketcher::SketchObject] Sketch042
  FullyConstrained = true
  sketch-geometry (7):
    g0: LineSegment StartX=0 StartY=0 StartZ=0 EndX=0 EndY=6 EndZ=0
    g1: Circle CenterX=0 CenterY=0 CenterZ=0 NormalX=0 NormalY=0 NormalZ=1 AngleXU=0 Radius=1
    g2: Circle CenterX=8 CenterY=6 CenterZ=0 NormalX=0 NormalY=0 NormalZ=1 AngleXU=0 Radius=1
    g3: BSplineCurve PolesCount=3 KnotsCount=2 Degree=2 IsPeriodic=0
    g4: GeomPoint X=0 Y=0 Z=0
    g5: GeomPoint X=8 Y=6 Z=0
    g6: LineSegment StartX=0 StartY=6 StartZ=0 EndX=8 EndY=6 EndZ=0
  constraints (14):
    c: Coincident(g0,g-1)
    c: Distance(g0) = 6
    c: Vertical(g0)
    c: Coincident(g3,g0)
    c: Weight(g1) = 1
    c: Equal(g1,g2)
    c: InternalAlignment(g1,g3)
    c: InternalAlignment(g2,g3)
    c: InternalAlignment(g4,g3)
    c: InternalAlignment(g5,g3)
    c: Block(g3)
    c: Coincident(g6,g0)
    c: Coincident(g6,g3)
    c: Horizontal(g6)
FEATURE [Part::Extrusion] Extrude030  label="caseScrewPillarBracket008"
  Base = -> Sketch039
  Dir = (0,0,1)
  DirMode = 2
  FaceMakerClass = Part::FaceMakerBullseye
  LengthFwd = 2.4
  LengthRev = 0
  Placement = pos=(15.76,29,8.8) rot=(0,1,0;0rad)
  Solid = true
  Symmetric = false
FEATURE [Part::Extrusion] Extrude031  label="caseScrewPillarBracket009"
  Base = -> Sketch040
  Dir = (0,0,1)
  DirMode = 2
  FaceMakerClass = Part::FaceMakerBullseye
  LengthFwd = 2.4
  LengthRev = 0
  Placement = pos=(15.76,29,60.8) rot=(0,0,1;0rad)
  Solid = true
  Symmetric = false
FEATURE [Part::Extrusion] Extrude032  label="caseScrewPillarBracket010"
  Base = -> Sketch041
  Dir = (0,0,1)
  DirMode = 2
  FaceMakerClass = Part::FaceMakerBullseye
  LengthFwd = 2.4
  LengthRev = 0
  Placement = pos=(13.7,29,13.26) rot=(0,-1,0;1.5708rad)
  Solid = true
  Symmetric = false
FEATURE [Part::Extrusion] Extrude033  label="caseScrewPillarBracket011"
  Base = -> Sketch042
  Dir = (0,0,1)
  DirMode = 2
  FaceMakerClass = Part::FaceMakerBullseye
  LengthFwd = 2.4
  LengthRev = 0
  Placement = pos=(11.3,29,58.74) rot=(0,1,0;1.5708rad)
  Solid = true
  Symmetric = false
FEATURE [Sketcher::SketchObject] Sketch043
  FullyConstrained = true
  sketch-geometry (7):
    g0: LineSegment StartX=0 StartY=0 StartZ=0 EndX=0 EndY=6 EndZ=0
    g1: Circle CenterX=0 CenterY=0 CenterZ=0 NormalX=0 NormalY=0 NormalZ=1 AngleXU=0 Radius=1
    g2: Circle CenterX=8 CenterY=6 CenterZ=0 NormalX=0 NormalY=0 NormalZ=1 AngleXU=0 Radius=1
    g3: BSplineCurve PolesCount=3 KnotsCount=2 Degree=2 IsPeriodic=0
    g4: GeomPoint X=0 Y=0 Z=0
    g5: GeomPoint X=8 Y=6 Z=0
    g6: LineSegment StartX=0 StartY=6 StartZ=0 EndX=8 EndY=6 EndZ=0
  constraints (14):
    c: Coincident(g0,g-1)
    c: Distance(g0) = 6
    c: Vertical(g0)
    c: Coincident(g3,g0)
    c: Weight(g1) = 1
    c: Equal(g1,g2)
    c: InternalAlignment(g1,g3)
    c: InternalAlignment(g2,g3)
    c: InternalAlignment(g4,g3)
    c: InternalAlignment(g5,g3)
    c: Block(g3)
    c: Coincident(g6,g0)
    c: Coincident(g6,g3)
    c: Horizontal(g6)
FEATURE [Part::Extrusion] Extrude034  label="caseScrewPillarBracket012"
  Base = -> Sketch043
  Dir = (0,0,1)
  DirMode = 2
  FaceMakerClass = Part::FaceMakerBullseye
  LengthFwd = 2.4
  LengthRev = 0
  Placement = pos=(88.3,29,65.23) rot=(0,1,0;1.5708rad)
  Solid = true
  Symmetric = false
FEATURE [Sketcher::SketchObject] Sketch044
  FullyConstrained = true
  sketch-geometry (7):
    g0: LineSegment StartX=0 StartY=0 StartZ=0 EndX=0 EndY=6 EndZ=0
    g1: Circle CenterX=0 CenterY=0 CenterZ=0 NormalX=0 NormalY=0 NormalZ=1 AngleXU=0 Radius=1
    g2: Circle CenterX=8 CenterY=6 CenterZ=0 NormalX=0 NormalY=0 NormalZ=1 AngleXU=0 Radius=1
    g3: BSplineCurve PolesCount=3 KnotsCount=2 Degree=2 IsPeriodic=0
    g4: GeomPoint X=0 Y=0 Z=0
    g5: GeomPoint X=8 Y=6 Z=0
    g6: LineSegment StartX=0 StartY=6 StartZ=0 EndX=8 EndY=6 EndZ=0
  constraints (14):
    c: Coincident(g0,g-1)
    c: Distance(g0) = 6
    c: Vertical(g0)
    c: Coincident(g3,g0)
    c: Weight(g1) = 1
    c: Equal(g1,g2)
    c: InternalAlignment(g1,g3)
    c: InternalAlignment(g2,g3)
    c: InternalAlignment(g4,g3)
    c: InternalAlignment(g5,g3)
    c: Block(g3)
    c: Coincident(g6,g0)
    c: Coincident(g6,g3)
    c: Horizontal(g6)
FEATURE [Part::Extrusion] Extrude035  label="caseScrewPillarBracket013"
  Base = -> Sketch044
  Dir = (0,0,1)
  DirMode = 2
  FaceMakerClass = Part::FaceMakerBullseye
  LengthFwd = 2.4
  LengthRev = 0
  Placement = pos=(90.7,29,6.77) rot=(0,-1,0;1.5708rad)
  Solid = true
  Symmetric = false
FEATURE [Sketcher::SketchObject] Sketch045
  FullyConstrained = true
  sketch-geometry (7):
    g0: LineSegment StartX=0 StartY=0 StartZ=0 EndX=0 EndY=6 EndZ=0
    g1: Circle CenterX=0 CenterY=0 CenterZ=0 NormalX=0 NormalY=0 NormalZ=1 AngleXU=0 Radius=1
    g2: Circle CenterX=8 CenterY=6 CenterZ=0 NormalX=0 NormalY=0 NormalZ=1 AngleXU=0 Radius=1
    g3: BSplineCurve PolesCount=3 KnotsCount=2 Degree=2 IsPeriodic=0
    g4: GeomPoint X=0 Y=0 Z=0
    g5: GeomPoint X=8 Y=6 Z=0
    g6: LineSegment StartX=0 StartY=6 StartZ=0 EndX=8 EndY=6 EndZ=0
  constraints (14):
    c: Coincident(g0,g-1)
    c: Distance(g0) = 6
    c: Vertical(g0)
    c: Coincident(g3,g0)
    c: Weight(g1) = 1
    c: Equal(g1,g2)
    c: InternalAlignment(g1,g3)
    c: InternalAlignment(g2,g3)
    c: InternalAlignment(g4,g3)
    c: InternalAlignment(g5,g3)
    c: Block(g3)
    c: Coincident(g6,g0)
    c: Coincident(g6,g3)
    c: Horizontal(g6)
FEATURE [Sketcher::SketchObject] Sketch046
  FullyConstrained = true
  sketch-geometry (7):
    g0: LineSegment StartX=0 StartY=0 StartZ=0 EndX=0 EndY=6 EndZ=0
    g1: Circle CenterX=0 CenterY=0 CenterZ=0 NormalX=0 NormalY=0 NormalZ=1 AngleXU=0 Radius=1
    g2: Circle CenterX=8 CenterY=6 CenterZ=0 NormalX=0 NormalY=0 NormalZ=1 AngleXU=0 Radius=1
    g3: BSplineCurve PolesCount=3 KnotsCount=2 Degree=2 IsPeriodic=0
    g4: GeomPoint X=0 Y=0 Z=0
    g5: GeomPoint X=8 Y=6 Z=0
    g6: LineSegment StartX=0 StartY=6 StartZ=0 EndX=8 EndY=6 EndZ=0
  constraints (14):
    c: Coincident(g0,g-1)
    c: Distance(g0) = 6
    c: Vertical(g0)
    c: Coincident(g3,g0)
    c: Weight(g1) = 1
    c: Equal(g1,g2)
    c: InternalAlignment(g1,g3)
    c: InternalAlignment(g2,g3)
    c: InternalAlignment(g4,g3)
    c: InternalAlignment(g5,g3)
    c: Block(g3)
    c: Coincident(g6,g0)
    c: Coincident(g6,g3)
    c: Horizontal(g6)
FEATURE [Part::Extrusion] Extrude036  label="caseScrewPillarBracket014"
  Base = -> Sketch045
  Dir = (0,0,1)
  DirMode = 2
  FaceMakerClass = Part::FaceMakerBullseye
  LengthFwd = 2.4
  LengthRev = 0
  Placement = pos=(110.7,29,6.77) rot=(0,-1,0;1.5708rad)
  Solid = true
  Symmetric = false
FEATURE [Part::Extrusion] Extrude037  label="caseScrewPillarBracket015"
  Base = -> Sketch046
  Dir = (0,0,1)
  DirMode = 2
  FaceMakerClass = Part::FaceMakerBullseye
  LengthFwd = 2.4
  LengthRev = 0
  Placement = pos=(108.3,29,65.23) rot=(0,1,0;1.5708rad)
  Solid = true
  Symmetric = false
FEATURE [Part::Box] Box013  label="frontCaseScrewPillarBracket002"
  AttacherType = Attacher::AttachEngine3D
  Height = 2.4
  Length = 22
  Placement = pos=(87,28,2.3) rot=(0,0,1;0rad)
  Width = 7
FEATURE [Part::Box] Box014  label="frontCaseScrewPillarBracket003"
  AttacherType = Attacher::AttachEngine3D
  Height = 2.4
  Length = 22
  Placement = pos=(87,28,67.3) rot=(0,0,1;0rad)
  Width = 7
FEATURE [Part::Feature] Face087
  shape: bbox 4.8 x 30.2 x 2e-07 mm, 1 faces, 0 solids (baked)
FEATURE [Part::Revolution] Revolve091  label="frontCaseScrewPost004"
  Angle = 360
  Axis = (0,1,0)
  Base = (0,0,0)
  FaceMakerClass = Part::FaceMakerBullseye
  Placement = pos=(89.5,4.5,3.5) rot=(0,0,1;0rad)
  Solid = false
  Source = -> Face087
  Symmetric = false
FEATURE [Part::Feature] Face088
  shape: bbox 4.8 x 30.2 x 2e-07 mm, 1 faces, 0 solids (baked)
FEATURE [Part::Revolution] Revolve092  label="frontCaseScrewPost005"
  Angle = 360
  Axis = (0,1,0)
  Base = (0,0,0)
  FaceMakerClass = Part::FaceMakerBullseye
  Placement = pos=(89.5,4.5,68.5) rot=(0,0,1;0rad)
  Solid = false
  Source = -> Face088
  Symmetric = false
FEATURE [Part::Feature] Face089
  shape: bbox 3.5 x 30.2 x 2e-07 mm, 1 faces, 0 solids (baked)
FEATURE [Part::Revolution] Revolve093  label="backCaseScrewPost002"
  Angle = 360
  Axis = (0,1,0)
  Base = (0,0,0)
  FaceMakerClass = Part::FaceMakerBullseye
  Placement = pos=(12.5,4.5,10) rot=(0,0,1;0rad)
  Solid = false
  Source = -> Face089
  Symmetric = false
FEATURE [Part::Feature] Face090
  shape: bbox 3.5 x 30.2 x 2e-07 mm, 1 faces, 0 solids (baked)
FEATURE [Part::Revolution] Revolve094  label="backCaseScrewPost003"
  Angle = 360
  Axis = (0,1,0)
  Base = (0,0,0)
  FaceMakerClass = Part::FaceMakerBullseye
  Placement = pos=(12.5,4.5,62) rot=(0,0,1;0rad)
  Solid = false
  Source = -> Face090
  Symmetric = false
FEATURE [Part::Box] Box015  label="Cube011"
  AttacherType = Attacher::AttachEngine3D
  Height = 28.8
  Length = 3
  Placement = pos=(107.3,28,21.6) rot=(0,0,1;0rad)
  Width = 7
FEATURE [Part::Box] Box016  label="Cube012"
  AttacherType = Attacher::AttachEngine3D
  Height = 3
  Length = 7.4
  Placement = pos=(107.3,28,18.6) rot=(0,0,1;0rad)
  Width = 7
FEATURE [Part::Box] Box017  label="Cube013"
  AttacherType = Attacher::AttachEngine3D
  Height = 3
  Length = 7.4
  Placement = pos=(107.3,28,50.4) rot=(0,0,1;0rad)
  Width = 7
FEATURE [Part::Cylinder] Cylinder024
  Angle = 360
  AttacherType = Attacher::AttachEngine3D
  Height = 20
  Placement = pos=(0,0,36.15) rot=(0,0,1;0rad)
  Radius = 14.3
FEATURE [Part::Cylinder] Cylinder025
  Angle = 360
  AttacherType = Attacher::AttachEngine3D
  Height = 10
  Placement = pos=(0,0,36.15) rot=(0,0,1;0rad)
  Radius = 4
FEATURE [Part::MultiFuse] Fusion066  label="removeToCreteHoleForPlugHousing009"
  Placement = pos=(70,19,36) rot=(0,1,0;1.5708rad)
  Shapes = -> [Cylinder024,Cylinder025]
FEATURE [Part::MultiFuse] Fusion065  label="plugHousingBracketHolder002"
  Shapes = -> [Box017,Box015,Box016]
FEATURE [Part::Cut] Cut025  label="plugHousingBracketHolder003"
  Base = -> Fusion065
  Placement = pos=(7,0,0) rot=(0,0,1;0rad)
  Tool = -> Fusion066
FEATURE [Sketcher::SketchObject] Sketch047
  FullyConstrained = false
  Placement = pos=(0,0,0) rot=(1,0,0;1.5708rad)
  sketch-geometry (24):
    g0: ArcOfCircle CenterX=-4 CenterY=-10.5 CenterZ=0 NormalX=0 NormalY=0 NormalZ=1 AngleXU=0 Radius=1.5 StartAngle=6e-16 EndAngle=3.14159
    g1: ArcOfCircle CenterX=-34.2 CenterY=-10.5 CenterZ=0 NormalX=0 NormalY=0 NormalZ=1 AngleXU=0 Radius=1.5 StartAngle=0 EndAngle=3.14159
    g2: ArcOfCircle CenterX=-34.2 CenterY=-27.7 CenterZ=0 NormalX=0 NormalY=0 NormalZ=1 AngleXU=0 Radius=1.5 StartAngle=3.14159 EndAngle=6.28319
    g3: ArcOfCircle CenterX=-4 CenterY=-27.7 CenterZ=0 NormalX=0 NormalY=0 NormalZ=1 AngleXU=0 Radius=1.5 StartAngle=3.1416 EndAngle=6.28319
    g4: ArcOfCircle CenterX=-10 CenterY=-4.3 CenterZ=0 NormalX=0 NormalY=0 NormalZ=1 AngleXU=0 Radius=1.5 StartAngle=2e-16 EndAngle=3.14159
    g5: ArcOfCircle CenterX=-16.1 CenterY=-1.8 CenterZ=0 NormalX=0 NormalY=0 NormalZ=1 AngleXU=0 Radius=1.5 StartAngle=5e-16 EndAngle=3.14159
    g6: ArcOfCircle CenterX=-22.1 CenterY=-1.8 CenterZ=0 NormalX=0 NormalY=0 NormalZ=1 AngleXU=0 Radius=1.5 StartAngle=5e-16 EndAngle=3.14159
    g7: ArcOfCircle CenterX=-28.2 CenterY=-4.3 CenterZ=0 NormalX=0 NormalY=0 NormalZ=1 AngleXU=0 Radius=1.5 StartAngle=2e-16 EndAngle=3.14159
    g8: ArcOfCircle CenterX=-10 CenterY=-33.9 CenterZ=0 NormalX=0 NormalY=0 NormalZ=1 AngleXU=0 Radius=1.5 StartAngle=3.14159 EndAngle=6.28319
    g9: ArcOfCircle CenterX=-16.1 CenterY=-36.4 CenterZ=0 NormalX=0 NormalY=0 NormalZ=1 AngleXU=0 Radius=1.5 StartAngle=3.14159 EndAngle=6.28319
    g10: ArcOfCircle CenterX=-22.1 CenterY=-36.4 CenterZ=0 NormalX=0 NormalY=0 NormalZ=1 AngleXU=0 Radius=1.5 StartAngle=3.14159 EndAngle=6.28319
    g11: ArcOfCircle CenterX=-28.2 CenterY=-33.9 CenterZ=0 NormalX=0 NormalY=0 NormalZ=1 AngleXU=0 Radius=1.5 StartAngle=3.14159 EndAngle=6.28319
    g12: LineSegment StartX=-35.7 StartY=-10.5 StartZ=0 EndX=-35.7 EndY=-27.7 EndZ=0
    g13: LineSegment StartX=-32.7 StartY=-10.5 StartZ=0 EndX=-32.7 EndY=-27.7 EndZ=0
    g14: LineSegment StartX=-29.7 StartY=-33.9 StartZ=0 EndX=-29.7 EndY=-4.3 EndZ=0
    g15: LineSegment StartX=-26.7 StartY=-33.9 StartZ=0 EndX=-26.7 EndY=-4.3 EndZ=0
    g16: LineSegment StartX=-2.5 StartY=-10.5 StartZ=0 EndX=-2.5 EndY=-27.7 EndZ=0
    g17: LineSegment StartX=-8.5 StartY=-4.3 StartZ=0 EndX=-8.5 EndY=-33.9 EndZ=0
    g18: LineSegment StartX=-5.5 StartY=-10.5 StartZ=0 EndX=-5.5 EndY=-27.7 EndZ=0
    g19: LineSegment StartX=-11.5 StartY=-4.3 StartZ=0 EndX=-11.5 EndY=-33.9 EndZ=0
    g20: LineSegment StartX=-14.6 StartY=-1.8 StartZ=0 EndX=-14.6 EndY=-36.4 EndZ=0
    g21: LineSegment StartX=-17.6 StartY=-1.8 StartZ=0 EndX=-17.6 EndY=-36.4 EndZ=0
    g22: LineSegment StartX=-20.6 StartY=-36.4 StartZ=0 EndX=-20.6 EndY=-1.8 EndZ=0
    g23: LineSegment StartX=-23.6 StartY=-1.8 StartZ=0 EndX=-23.6 EndY=-36.4 EndZ=0
  constraints (48):
    c: Block(g0)
    c: Block(g1)
    c: Block(g2)
    c: Block(g3)
    c: Block(g4)
    c: Block(g5)
    c: Block(g6)
    c: Block(g7)
    c: Block(g8)
    c: Block(g9)
    c: Block(g10)
    c: Block(g11)
    c: Coincident(g12,g1)
    c: Coincident(g12,g2)
    c: Vertical(g12)
    c: Coincident(g13,g1)
    c: Coincident(g13,g2)
    c: Vertical(g13)
    c: Coincident(g14,g11)
    c: Coincident(g14,g7)
    c: Vertical(g14)
    c: Coincident(g15,g11)
    c: Coincident(g15,g7)
    c: Vertical(g15)
    c: Coincident(g16,g0)
    c: Coincident(g16,g3)
    c: Vertical(g16)
    c: Coincident(g17,g4)
    c: Coincident(g17,g8)
    c: Vertical(g17)
    c: Coincident(g18,g0)
    c: Coincident(g18,g3)
    c: Vertical(g18)
    c: Coincident(g19,g4)
    c: Coincident(g19,g8)
    c: Vertical(g19)
    c: Coincident(g20,g5)
    c: Coincident(g20,g9)
    c: Vertical(g20)
    c: Coincident(g21,g5)
    c: Coincident(g21,g9)
    c: Vertical(g21)
    c: Coincident(g22,g10)
    c: Coincident(g22,g6)
    c: Vertical(g22)
    c: Coincident(g23,g6)
    c: Coincident(g23,g10)
    c: Vertical(g23)
FEATURE [Part::Extrusion] Extrude038  label="removeToCreateFanGrillHoles001"
  Base = -> Sketch047
  Dir = (0,-1,6e-16)
  DirMode = 2
  FaceMakerClass = Part::FaceMakerBullseye
  LengthFwd = 10
  LengthRev = 0
  Placement = pos=(65.4,44,54.82) rot=(0,0,1;0rad)
  Solid = true
  Symmetric = false
FEATURE [Part::Feature] Wire004
  shape: bbox 11 x 5.2 x 2e-07 mm, 0 faces, 0 solids (baked)
FEATURE [Part::Revolution] Revolve095
  Angle = 360
  Axis = (0,1,0)
  Base = (0,0,0)
  FaceMakerClass = Part::FaceMakerBullseye
  Placement = pos=(30.3,38,19.7) rot=(0,0,1;0rad)
  Solid = true
  Source = -> Wire004
  Symmetric = false
FEATURE [Part::Feature] Wire005
  shape: bbox 11 x 5.2 x 2e-07 mm, 0 faces, 0 solids (baked)
FEATURE [Part::Revolution] Revolve096
  Angle = 360
  Axis = (0,1,0)
  Base = (0,0,0)
  FaceMakerClass = Part::FaceMakerBullseye
  Placement = pos=(30.3,38,51.7) rot=(0,0,1;0rad)
  Solid = true
  Source = -> Wire005
  Symmetric = false
FEATURE [Part::Feature] Wire006
  shape: bbox 11 x 5.2 x 2e-07 mm, 0 faces, 0 solids (baked)
FEATURE [Part::Revolution] Revolve097
  Angle = 360
  Axis = (0,1,0)
  Base = (0,0,0)
  FaceMakerClass = Part::FaceMakerBullseye
  Placement = pos=(62.3,38,51.7) rot=(0,0,1;0rad)
  Solid = true
  Source = -> Wire006
  Symmetric = false
FEATURE [Part::Feature] Wire007
  shape: bbox 11 x 5.2 x 2e-07 mm, 0 faces, 0 solids (baked)
FEATURE [Part::Revolution] Revolve098
  Angle = 360
  Axis = (0,1,0)
  Base = (0,0,0)
  FaceMakerClass = Part::FaceMakerBullseye
  Placement = pos=(62.3,38,19.7) rot=(0,0,1;0rad)
  Solid = true
  Source = -> Wire007
  Symmetric = false
FEATURE [Part::MultiFuse] Fusion067  label="fanScrewHousing002"
  Shapes = -> [Revolve098,Revolve097,Revolve096,Revolve095]
FEATURE [Part::Feature] Face091 .. Face094  x4 (patterned run collapsed; names and placements below)
  shape: bbox 3.5 x 17.8 x 2e-07 mm, 1 faces, 0 solids (baked)
FEATURE [Part::Revolution] Revolve099  label="removeToCreateScrewAndThreadedInsertHole026"
  Angle = 360
  Axis = (0,1,0)
  Base = (0,0,0)
  FaceMakerClass = Part::FaceMakerBullseye
  Placement = pos=(62.3,30.3,19.7) rot=(0,0,1;0rad)
  Solid = false
  Source = -> Face091
  Symmetric = false
FEATURE [Part::Revolution] Revolve100  label="removeToCreateScrewAndThreadedInsertHole027"
  Angle = 360
  Axis = (0,1,0)
  Base = (0,0,0)
  FaceMakerClass = Part::FaceMakerBullseye
  Placement = pos=(62.3,30.3,51.7) rot=(0,0,1;0rad)
  Solid = false
  Source = -> Face092
  Symmetric = false
FEATURE [Part::Revolution] Revolve101  label="removeToCreateScrewAndThreadedInsertHole028"
  Angle = 360
  Axis = (0,1,0)
  Base = (0,0,0)
  FaceMakerClass = Part::FaceMakerBullseye
  Placement = pos=(30.3,30.3,19.7) rot=(0,0,1;0rad)
  Solid = false
  Source = -> Face093
  Symmetric = false
FEATURE [Part::Revolution] Revolve102  label="removeToCreateScrewAndThreadedInsertHole029"
  Angle = 360
  Axis = (0,1,0)
  Base = (0,0,0)
  FaceMakerClass = Part::FaceMakerBullseye
  Placement = pos=(30.3,30.3,51.7) rot=(0,0,1;0rad)
  Solid = false
  Source = -> Face094
  Symmetric = false
FEATURE [Part::MultiFuse] Fusion068  label="createThreadedInsertHolesForFan002"
  Shapes = -> [Revolve099,Revolve100,Revolve101,Revolve102]
FEATURE [Part::Cut] Cut026  label="fanScrewHousing003"
  Base = -> Fusion067
  Tool = -> Fusion068
FEATURE [Sketcher::SketchObject] Sketch048
  FullyConstrained = false
  Placement = pos=(0,0,0) rot=(1,0,0;1.5708rad)
  sketch-geometry (24):
    g0: ArcOfCircle CenterX=-4 CenterY=-10.5 CenterZ=0 NormalX=0 NormalY=0 NormalZ=1 AngleXU=0 Radius=1.5 StartAngle=6e-16 EndAngle=3.14159
    g1: ArcOfCircle CenterX=-34.2 CenterY=-10.5 CenterZ=0 NormalX=0 NormalY=0 NormalZ=1 AngleXU=0 Radius=1.5 StartAngle=0 EndAngle=3.14159
    g2: ArcOfCircle CenterX=-34.2 CenterY=-27.7 CenterZ=0 NormalX=0 NormalY=0 NormalZ=1 AngleXU=0 Radius=1.5 StartAngle=3.14159 EndAngle=6.28319
    g3: ArcOfCircle CenterX=-4 CenterY=-27.7 CenterZ=0 NormalX=0 NormalY=0 NormalZ=1 AngleXU=0 Radius=1.5 StartAngle=3.1416 EndAngle=6.28319
    g4: ArcOfCircle CenterX=-10 CenterY=-4.3 CenterZ=0 NormalX=0 NormalY=0 NormalZ=1 AngleXU=0 Radius=1.5 StartAngle=2e-16 EndAngle=3.14159
    g5: ArcOfCircle CenterX=-16.1 CenterY=-1.8 CenterZ=0 NormalX=0 NormalY=0 NormalZ=1 AngleXU=0 Radius=1.5 StartAngle=5e-16 EndAngle=3.14159
    g6: ArcOfCircle CenterX=-22.1 CenterY=-1.8 CenterZ=0 NormalX=0 NormalY=0 NormalZ=1 AngleXU=0 Radius=1.5 StartAngle=5e-16 EndAngle=3.14159
    g7: ArcOfCircle CenterX=-28.2 CenterY=-4.3 CenterZ=0 NormalX=0 NormalY=0 NormalZ=1 AngleXU=0 Radius=1.5 StartAngle=2e-16 EndAngle=3.14159
    g8: ArcOfCircle CenterX=-10 CenterY=-33.9 CenterZ=0 NormalX=0 NormalY=0 NormalZ=1 AngleXU=0 Radius=1.5 StartAngle=3.14159 EndAngle=6.28319
    g9: ArcOfCircle CenterX=-16.1 CenterY=-36.4 CenterZ=0 NormalX=0 NormalY=0 NormalZ=1 AngleXU=0 Radius=1.5 StartAngle=3.14159 EndAngle=6.28319
    g10: ArcOfCircle CenterX=-22.1 CenterY=-36.4 CenterZ=0 NormalX=0 NormalY=0 NormalZ=1 AngleXU=0 Radius=1.5 StartAngle=3.14159 EndAngle=6.28319
    g11: ArcOfCircle CenterX=-28.2 CenterY=-33.9 CenterZ=0 NormalX=0 NormalY=0 NormalZ=1 AngleXU=0 Radius=1.5 StartAngle=3.14159 EndAngle=6.28319
    g12: LineSegment StartX=-35.7 StartY=-10.5 StartZ=0 EndX=-35.7 EndY=-27.7 EndZ=0
    g13: LineSegment StartX=-32.7 StartY=-10.5 StartZ=0 EndX=-32.7 EndY=-27.7 EndZ=0
    g14: LineSegment StartX=-29.7 StartY=-33.9 StartZ=0 EndX=-29.7 EndY=-4.3 EndZ=0
    g15: LineSegment StartX=-26.7 StartY=-33.9 StartZ=0 EndX=-26.7 EndY=-4.3 EndZ=0
    g16: LineSegment StartX=-2.5 StartY=-10.5 StartZ=0 EndX=-2.5 EndY=-27.7 EndZ=0
    g17: LineSegment StartX=-8.5 StartY=-4.3 StartZ=0 EndX=-8.5 EndY=-33.9 EndZ=0
    g18: LineSegment StartX=-5.5 StartY=-10.5 StartZ=0 EndX=-5.5 EndY=-27.7 EndZ=0
    g19: LineSegment StartX=-11.5 StartY=-4.3 StartZ=0 EndX=-11.5 EndY=-33.9 EndZ=0
    g20: LineSegment StartX=-14.6 StartY=-1.8 StartZ=0 EndX=-14.6 EndY=-36.4 EndZ=0
    g21: LineSegment StartX=-17.6 StartY=-1.8 StartZ=0 EndX=-17.6 EndY=-36.4 EndZ=0
    g22: LineSegment StartX=-20.6 StartY=-36.4 StartZ=0 EndX=-20.6 EndY=-1.8 EndZ=0
    g23: LineSegment StartX=-23.6 StartY=-1.8 StartZ=0 EndX=-23.6 EndY=-36.4 EndZ=0
  constraints (48):
    c: Block(g0)
    c: Block(g1)
    c: Block(g2)
    c: Block(g3)
    c: Block(g4)
    c: Block(g5)
    c: Block(g6)
    c: Block(g7)
    c: Block(g8)
    c: Block(g9)
    c: Block(g10)
    c: Block(g11)
    c: Coincident(g12,g1)
    c: Coincident(g12,g2)
    c: Vertical(g12)
    c: Coincident(g13,g1)
    c: Coincident(g13,g2)
    c: Vertical(g13)
    c: Coincident(g14,g11)
    c: Coincident(g14,g7)
    c: Vertical(g14)
    c: Coincident(g15,g11)
    c: Coincident(g15,g7)
    c: Vertical(g15)
    c: Coincident(g16,g0)
    c: Coincident(g16,g3)
    c: Vertical(g16)
    c: Coincident(g17,g4)
    c: Coincident(g17,g8)
    c: Vertical(g17)
    c: Coincident(g18,g0)
    c: Coincident(g18,g3)
    c: Vertical(g18)
    c: Coincident(g19,g4)
    c: Coincident(g19,g8)
    c: Vertical(g19)
    c: Coincident(g20,g5)
    c: Coincident(g20,g9)
    c: Vertical(g20)
    c: Coincident(g21,g5)
    c: Coincident(g21,g9)
    c: Vertical(g21)
    c: Coincident(g22,g10)
    c: Coincident(g22,g6)
    c: Vertical(g22)
    c: Coincident(g23,g6)
    c: Coincident(g23,g10)
    c: Vertical(g23)
FEATURE [Part::Extrusion] Extrude039  label="removeToCreateFanGrillHoles002"
  Base = -> Sketch048
  Dir = (0,-1,6e-16)
  DirMode = 2
  FaceMakerClass = Part::FaceMakerBullseye
  LengthFwd = 10
  LengthRev = 0
  Placement = pos=(65.4,44,54.82) rot=(0,0,1;0rad)
  Solid = true
  Symmetric = false
FEATURE [Part::Cut] Cut027  label="fanScrewHousing004"
  Base = -> Cut026
  Tool = -> Extrude038
FEATURE [Part::Cut] Cut028  label="top014"
  Base = -> Fillet026
  Tool = -> Extrude039
FEATURE [Part::Feature] Face095 .. Face098  x4 (patterned run collapsed; names and placements below)
  shape: bbox 3.5 x 17.8 x 2e-07 mm, 1 faces, 0 solids (baked)
FEATURE [Part::Revolution] Revolve103  label="removeToCreateScrewAndThreadedInsertHole030"
  Angle = 360
  Axis = (0,1,0)
  Base = (0,0,0)
  FaceMakerClass = Part::FaceMakerBullseye
  Placement = pos=(62.3,30.3,19.7) rot=(0,0,1;0rad)
  Solid = false
  Source = -> Face095
  Symmetric = false
FEATURE [Part::Revolution] Revolve104  label="removeToCreateScrewAndThreadedInsertHole031"
  Angle = 360
  Axis = (0,1,0)
  Base = (0,0,0)
  FaceMakerClass = Part::FaceMakerBullseye
  Placement = pos=(62.3,30.3,51.7) rot=(0,0,1;0rad)
  Solid = false
  Source = -> Face096
  Symmetric = false
FEATURE [Part::Revolution] Revolve105  label="removeToCreateScrewAndThreadedInsertHole032"
  Angle = 360
  Axis = (0,1,0)
  Base = (0,0,0)
  FaceMakerClass = Part::FaceMakerBullseye
  Placement = pos=(30.3,30.3,19.7) rot=(0,0,1;0rad)
  Solid = false
  Source = -> Face097
  Symmetric = false
FEATURE [Part::Revolution] Revolve106  label="removeToCreateScrewAndThreadedInsertHole033"
  Angle = 360
  Axis = (0,1,0)
  Base = (0,0,0)
  FaceMakerClass = Part::FaceMakerBullseye
  Placement = pos=(30.3,30.3,51.7) rot=(0,0,1;0rad)
  Solid = false
  Source = -> Face098
  Symmetric = false
FEATURE [Part::MultiFuse] Fusion069  label="createThreadedInsertHolesForFan003"
  Shapes = -> [Revolve103,Revolve104,Revolve105,Revolve106]
FEATURE [Part::Cut] Cut029  label="top015"
  Base = -> Cut028
  Tool = -> Fusion054
FEATURE [Part::Cut] Cut030  label="fanScrewHousing005"
  Base = -> Cut027
  Tool = -> Fusion069
FEATURE [Part::Cylinder] Cylinder026  label="removeToCreteHoleForPlugHousing010"
  Angle = 360
  AttacherType = Attacher::AttachEngine3D
  Height = 20
  Placement = pos=(-2,19,36) rot=(0,1,0;1.5708rad)
  Radius = 14.3
FEATURE [Part::Box] Box018  label="removeToCreteHoleForPlugHousing011"
  AttacherType = Attacher::AttachEngine3D
  Height = 28.6
  Length = 10
  Placement = pos=(-2,0,21.7) rot=(0,0,1;0rad)
  Width = 19
FEATURE [Part::Box] Box019  label="wireHolderBottomCaseBit"
  AttacherType = Attacher::AttachEngine3D
  Height = 28
  Length = 3
  Placement = pos=(0,0,22) rot=(0,0,1;0rad)
  Width = 21
FEATURE [Part::Cylinder] Cylinder027  label="removeToCreteHoleForPlugHousing012"
  Angle = 360
  AttacherType = Attacher::AttachEngine3D
  Height = 20
  Placement = pos=(-2,19,36) rot=(0,1,0;1.5708rad)
  Radius = 14.3
FEATURE [Part::Cut] Cut031  label="wireHolderBottomCaseBit001"
  Base = -> Box019
  Tool = -> Cylinder027
FEATURE [Part::MultiFuse] Fusion070  label="removeToCreteHoleForPlugHousing013"
  Shapes = -> [Box018,Cylinder026]
FEATURE [Part::Cut] Cut032  label="top016"
  Base = -> Cut029
  Tool = -> Fusion070
FEATURE [Part::Cylinder] Cylinder028
  Angle = 360
  AttacherType = Attacher::AttachEngine3D
  Height = 20
  Placement = pos=(0,0,36.15) rot=(0,0,1;0rad)
  Radius = 14.3
FEATURE [Part::Cylinder] Cylinder029
  Angle = 360
  AttacherType = Attacher::AttachEngine3D
  Height = 10
  Placement = pos=(0,0,36.15) rot=(0,0,1;0rad)
  Radius = 4
FEATURE [Part::MultiFuse] Fusion071  label="removeToCreteHoleForPlugHousing014"
  Placement = pos=(70,19,36) rot=(0,1,0;1.5708rad)
  Shapes = -> [Cylinder028,Cylinder029]
FEATURE [Sketcher::SketchObject] Sketch049  label="topSketch011"
  FullyConstrained = true
  sketch-geometry (4):
    g0: ArcOfCircle CenterX=105 CenterY=19 CenterZ=0 NormalX=0 NormalY=0 NormalZ=1 AngleXU=0 Radius=20.6155 StartAngle=5.54125 EndAngle=6.28319
    g1: ArcOfCircle CenterX=105 CenterY=19 CenterZ=0 NormalX=0 NormalY=0 NormalZ=1 AngleXU=0 Radius=13 StartAngle=5.54125 EndAngle=6.28319
    g2: LineSegment StartX=118 StartY=19 StartZ=0 EndX=125.616 EndY=19 EndZ=0
    g3: LineSegment StartX=114.583 StartY=10.2157 StartZ=0 EndX=120.197 EndY=5.06982 EndZ=0
  constraints (7):
    c: Block(g0)
    c: Block(g1)
    c: Coincident(g2,g1)
    c: Coincident(g2,g0)
    c: Horizontal(g2)
    c: Coincident(g3,g1)
    c: Coincident(g3,g0)
FEATURE [Part::Box] Box020  label="removeToCreteHoleForPlugHousing015"
  AttacherType = Attacher::AttachEngine3D
  Height = 28.6
  Length = 20
  Placement = pos=(106.15,0,21.7) rot=(0,0,1;0rad)
  Width = 19
FEATURE [Part::MultiFuse] Fusion072  label="removeToCreteHoleForPlugHousing016"
  Shapes = -> [Box020,Fusion071]
FEATURE [Part::Cut] Cut033  label="removeToCreteHoleForPlugHousing017"
  Base = -> Cut032
  Tool = -> Fusion072
FEATURE [Part::Cylinder] Cylinder030
  Angle = 360
  AttacherType = Attacher::AttachEngine3D
  Height = 20
  Placement = pos=(0,0,36.15) rot=(0,0,1;0rad)
  Radius = 14.3
FEATURE [Part::Cylinder] Cylinder031
  Angle = 360
  AttacherType = Attacher::AttachEngine3D
  Height = 10
  Placement = pos=(0,0,36.15) rot=(0,0,1;0rad)
  Radius = 4
FEATURE [Part::Box] Box021  label="removeToCreteHoleForPlugHousing019"
  AttacherType = Attacher::AttachEngine3D
  Height = 28.6
  Length = 20
  Placement = pos=(106.15,0,21.7) rot=(0,0,1;0rad)
  Width = 19
FEATURE [Part::MultiFuse] Fusion074  label="removeToCreteHoleForPlugHousing020"
  Placement = pos=(70,19,36) rot=(0,1,0;1.5708rad)
  Shapes = -> [Cylinder030,Cylinder031]
FEATURE [Part::MultiFuse] Fusion073  label="removeToCreteHoleForPlugHousing018"
  Placement = pos=(0,0,28.3) rot=(0,0,1;0rad)
  Shapes = -> [Box021,Fusion074]
FEATURE [Part::Cylinder] Cylinder032
  Angle = 360
  AttacherType = Attacher::AttachEngine3D
  Height = 20
  Placement = pos=(0,0,36.15) rot=(0,0,1;0rad)
  Radius = 14.3
FEATURE [Part::Cylinder] Cylinder033
  Angle = 360
  AttacherType = Attacher::AttachEngine3D
  Height = 10
  Placement = pos=(0,0,36.15) rot=(0,0,1;0rad)
  Radius = 4
FEATURE [Part::Box] Box022  label="removeToCreteHoleForPlugHousing021"
  AttacherType = Attacher::AttachEngine3D
  Height = 28.6
  Length = 20
  Placement = pos=(106.15,0,21.7) rot=(0,0,1;0rad)
  Width = 19
FEATURE [Part::MultiFuse] Fusion076  label="removeToCreteHoleForPlugHousing023"
  Placement = pos=(70,19,36) rot=(0,1,0;1.5708rad)
  Shapes = -> [Cylinder032,Cylinder033]
FEATURE [Part::MultiFuse] Fusion075  label="removeToCreteHoleForPlugHousing022"
  Placement = pos=(0,0,-28.3) rot=(0,0,1;0rad)
  Shapes = -> [Box022,Fusion076]
FEATURE [Part::MultiFuse] Fusion077  label="removeToCreatePlugHousingBottomBit"
  Shapes = -> [Fusion075,Fusion073]
FEATURE [Part::Cylinder] Cylinder034
  Angle = 360
  AttacherType = Attacher::AttachEngine3D
  Height = 20
  Placement = pos=(0,0,36.15) rot=(0,0,1;0rad)
  Radius = 14
FEATURE [Part::Cylinder] Cylinder035
  Angle = 360
  AttacherType = Attacher::AttachEngine3D
  Height = 10
  Placement = pos=(0,0,36.15) rot=(0,0,1;0rad)
  Radius = 4
FEATURE [Part::MultiFuse] Fusion078  label="removeToCreteHoleForPlugHousing024"
  Placement = pos=(70,19,36) rot=(0,1,0;1.5708rad)
  Shapes = -> [Cylinder034,Cylinder035]
FEATURE [Part::MultiFuse] Fusion079  label="removeToCreatePlugHousingBottomBit001"
  Shapes = -> [Fusion078,Fusion077]
FEATURE [Part::Extrusion] Extrude040  label="bottomPlugHousingBit"
  Base = -> Sketch049
  Dir = (0,0,1)
  DirMode = 2
  FaceMakerClass = Part::FaceMakerBullseye
  LengthFwd = 72
  LengthRev = 0
  Solid = true
  Symmetric = false
FEATURE [Part::Cut] Cut034  label="bottomPlugHousingBit001"
  Base = -> Extrude040
  Placement = pos=(-0.09,0,0) rot=(0,0,1;0rad)
  Tool = -> Fusion079
FEATURE [Part::Box] Box023  label="Cube014"
  AttacherType = Attacher::AttachEngine3D
  Height = 16
  Length = 8
  Placement = pos=(12.7,31.52,28) rot=(0,0,1;0rad)
  Width = 4
FEATURE [Part::Cylinder] Cylinder036
  Angle = 360
  AttacherType = Attacher::AttachEngine3D
  Height = 10
  Placement = pos=(0,0,36.15) rot=(0,0,1;0rad)
  Radius = 4
FEATURE [Part::Cylinder] Cylinder037
  Angle = 360
  AttacherType = Attacher::AttachEngine3D
  Height = 20
  Placement = pos=(0,0,36.15) rot=(0,0,1;0rad)
  Radius = 8.2
FEATURE [Part::MultiFuse] Fusion080  label="removeToCreteHoleForPlugHousing025"
  Placement = pos=(-42,19,36) rot=(0,1,0;1.5708rad)
  Shapes = -> [Cylinder037,Cylinder036]
FEATURE [Sketcher::SketchObject] Sketch050  label="topSketch012"
  FullyConstrained = true
  sketch-geometry (4):
    g0: LineSegment StartX=16.8446 StartY=31.512 StartZ=0 EndX=16.3251 EndY=34.4666 EndZ=0
    g1: ArcOfCircle CenterX=19 CenterY=19.2524 CenterZ=0 NormalX=0 NormalY=0 NormalZ=1 AngleXU=0 Radius=15.4476 StartAngle=1.74483 EndAngle=2.72717
    g2: ArcOfCircle CenterX=19 CenterY=19.2524 CenterZ=0 NormalX=0 NormalY=0 NormalZ=1 AngleXU=0 Radius=12.4476 StartAngle=1.74483 EndAngle=2.73189
    g3: LineSegment StartX=4.86004 StartY=25.4725 StartZ=0 EndX=7.58253 EndY=24.2107 EndZ=0
  constraints (7):
    c: Block(g0)
    c: Coincident(g1,g0)
    c: Coincident(g2,g0)
    c: Coincident(g3,g1)
    c: Coincident(g3,g2)
    c: Block(g1)
    c: Block(g2)
FEATURE [Part::Extrusion] Extrude041
  Base = -> Sketch050
  Dir = (0,0,1)
  DirMode = 2
  FaceMakerClass = Part::FaceMakerBullseye
  LengthFwd = 10.6
  LengthRev = 0
  Placement = pos=(0,0,31) rot=(0,0,1;0rad)
  Solid = true
  Symmetric = false
FEATURE [Part::Cut] Cut035
  Base = -> Extrude041
  Placement = pos=(0,0,-0.3) rot=(0,0,1;0rad)
  Tool = -> Fusion080
FEATURE [Part::Cut] Cut036
  Base = -> Box023
  Tool = -> Cut035
FEATURE [Part::Fillet] Fillet027
  Base = -> Cut036
  Edges = 1 edges r=0.7: [Edge13]
FEATURE [Part::Fillet] Fillet028
  Base = -> Fillet027
  Edges = 1 edges r=0.7: [Edge13]
FEATURE [Part::Fillet] Fillet029
  Base = -> Fillet028
  Edges = 1 edges r=0.7: [Edge16]
FEATURE [Part::Fillet] Fillet030
  Base = -> Fillet029
  Edges = 1 edges r=0.7: [Edge11]
FEATURE [Part::Fillet] Fillet031
  Base = -> Fillet030
  Edges = 1 edges r=0.7: [Edge10]
FEATURE [Part::Fillet] Fillet032
  Base = -> Fillet031
  Edges = 1 edges r=1.2: [Edge5]
FEATURE [Part::Fillet] Fillet033
  Base = -> Fillet032
  Edges = 1 edges r=1.2: [Edge12]
FEATURE [Part::Fillet] Fillet034  label="wireHousingRetainer"
  Base = -> Fillet033
  Edges = 1 edges r=2: [Edge1]
  Placement = pos=(0.3,0,0) rot=(0,0,1;0rad)
FEATURE [Part::Feature] Face099
  shape: bbox 3.5 x 17.8 x 2e-07 mm, 1 faces, 0 solids (baked)
FEATURE [Part::Revolution] Revolve107  label="removeToCreateScrewAndThreadedInsertHole034"
  Angle = 360
  Axis = (0,1,0)
  Base = (0,0,0)
  FaceMakerClass = Part::FaceMakerBullseye
  Placement = pos=(12.5,0,10) rot=(0,0,1;0rad)
  Solid = false
  Source = -> Face099
  Symmetric = false
FEATURE [Part::Feature] Face100
  shape: bbox 3.5 x 17.8 x 2e-07 mm, 1 faces, 0 solids (baked)
FEATURE [Part::Revolution] Revolve108  label="removeToCreateScrewAndThreadedInsertHole035"
  Angle = 360
  Axis = (0,1,0)
  Base = (0,0,0)
  FaceMakerClass = Part::FaceMakerBullseye
  Placement = pos=(12.5,0,62) rot=(0,0,1;0rad)
  Solid = false
  Source = -> Face100
  Symmetric = false
FEATURE [Part::Feature] Face101
  shape: bbox 3.5 x 17.8 x 2e-07 mm, 1 faces, 0 solids (baked)
FEATURE [Part::Revolution] Revolve109  label="removeToCreateScrewAndThreadedInsertHole036"
  Angle = 360
  Axis = (0,1,0)
  Base = (0,0,0)
  FaceMakerClass = Part::FaceMakerBullseye
  Placement = pos=(89.5,0,68.5) rot=(0,0,1;0rad)
  Solid = false
  Source = -> Face101
  Symmetric = false
FEATURE [Part::Feature] Face102
  shape: bbox 3.5 x 17.8 x 2e-07 mm, 1 faces, 0 solids (baked)
FEATURE [Part::Revolution] Revolve110  label="removeToCreateScrewAndThreadedInsertHole037"
  Angle = 360
  Axis = (0,1,0)
  Base = (0,0,0)
  FaceMakerClass = Part::FaceMakerBullseye
  Placement = pos=(89.5,0,3.5) rot=(0,0,1;0rad)
  Solid = false
  Source = -> Face102
  Symmetric = false
FEATURE [Part::Feature] Face103
  shape: bbox 3.5 x 17.8 x 2e-07 mm, 1 faces, 0 solids (baked)
FEATURE [Part::Revolution] Revolve111  label="removeToCreateScrewAndThreadedInsertHole038"
  Angle = 360
  Axis = (0,1,0)
  Base = (0,0,0)
  FaceMakerClass = Part::FaceMakerBullseye
  Placement = pos=(109.5,4.7,3.5) rot=(0,0,1;0rad)
  Solid = false
  Source = -> Face103
  Symmetric = false
FEATURE [Part::Feature] Face104
  shape: bbox 3.5 x 17.8 x 2e-07 mm, 1 faces, 0 solids (baked)
FEATURE [Part::Revolution] Revolve112  label="removeToCreateScrewAndThreadedInsertHole039"
  Angle = 360
  Axis = (0,1,0)
  Base = (0,0,0)
  FaceMakerClass = Part::FaceMakerBullseye
  Placement = pos=(109.5,4.7,68.5) rot=(0,0,1;0rad)
  Solid = false
  Source = -> Face104
  Symmetric = false
FEATURE [Part::MultiFuse] Fusion081  label="removeToCreateScrewAndThreadedInsertHole040"
  Shapes = -> [Revolve107,Revolve108,Revolve109,Revolve110,Revolve111,Revolve112]
FEATURE [Part::MultiFuse] Fusion082  label="casePillars002"
  Shapes = -> [Revolve094,Revolve092,Revolve090,Revolve089,Revolve091,Revolve093]
FEATURE [Part::Cut] Cut037  label="casePillars003"
  Base = -> Fusion082
  Tool = -> Fusion081
FEATURE [Sketcher::SketchObject] Sketch051
  FullyConstrained = true
  Placement = pos=(117,19,0) rot=(0.57735,0.57735,0.57735;2.0944rad)
  sketch-geometry (48):
    g0: LineSegment StartX=-49.19 StartY=69.25 StartZ=0 EndX=-49.19 EndY=66.25 EndZ=0
    g1: LineSegment StartX=-49.19 StartY=63.5 StartZ=0 EndX=-49.19 EndY=60.5 EndZ=0
    g2: LineSegment StartX=-49.19 StartY=57.75 StartZ=0 EndX=-49.19 EndY=54.75 EndZ=0
    g3: LineSegment StartX=-49.19 StartY=52 StartZ=0 EndX=-49.19 EndY=49 EndZ=0
    g4: LineSegment StartX=-49.19 StartY=46.25 StartZ=0 EndX=-49.19 EndY=43.25 EndZ=0
    g5: LineSegment StartX=-49.19 StartY=40.5 StartZ=0 EndX=-49.19 EndY=37.5 EndZ=0
    g6: LineSegment StartX=-49.19 StartY=34.5 StartZ=0 EndX=-49.19 EndY=31.5 EndZ=0
    g7: LineSegment StartX=-49.19 StartY=28.75 StartZ=0 EndX=-49.19 EndY=25.75 EndZ=0
    g8: LineSegment StartX=-49.19 StartY=23 StartZ=0 EndX=-49.19 EndY=20 EndZ=0
    g9: LineSegment StartX=-49.19 StartY=17.25 StartZ=0 EndX=-49.19 EndY=14.25 EndZ=0
    g10: LineSegment StartX=-49.19 StartY=11.5 StartZ=0 EndX=-49.19 EndY=8.5 EndZ=0
    g11: LineSegment StartX=-49.19 StartY=5.75 StartZ=0 EndX=-49.19 EndY=2.75 EndZ=0
    g12: ArcOfCircle CenterX=-1.5 CenterY=67.75 CenterZ=0 NormalX=0 NormalY=0 NormalZ=1 AngleXU=0 Radius=1.5 StartAngle=4.71239 EndAngle=7.85398
    g13: ArcOfCircle CenterX=-1.5 CenterY=62 CenterZ=0 NormalX=0 NormalY=0 NormalZ=1 AngleXU=0 Radius=1.5 StartAngle=4.71239 EndAngle=7.85398
    g14: ArcOfCircle CenterX=-1.5 CenterY=56.25 CenterZ=0 NormalX=0 NormalY=0 NormalZ=1 AngleXU=0 Radius=1.5 StartAngle=4.71239 EndAngle=7.85398
    g15: ArcOfCircle CenterX=-11.49 CenterY=50.5 CenterZ=0 NormalX=0 NormalY=0 NormalZ=1 AngleXU=0 Radius=1.5 StartAngle=4.71239 EndAngle=7.85398
    g16: ArcOfCircle CenterX=-16.28 CenterY=44.75 CenterZ=0 NormalX=0 NormalY=0 NormalZ=1 AngleXU=0 Radius=1.5 StartAngle=4.71239 EndAngle=7.85398
    g17: ArcOfCircle CenterX=-18.2337 CenterY=39 CenterZ=0 NormalX=0 NormalY=0 NormalZ=1 AngleXU=0 Radius=1.5 StartAngle=4.71485 EndAngle=7.85398
    g18: ArcOfCircle CenterX=-16.2837 CenterY=27.25 CenterZ=0 NormalX=0 NormalY=0 NormalZ=1 AngleXU=0 Radius=1.5 StartAngle=4.71485 EndAngle=7.85398
    g19: ArcOfCircle CenterX=-18.2337 CenterY=33 CenterZ=0 NormalX=0 NormalY=0 NormalZ=1 AngleXU=0 Radius=1.5 StartAngle=4.71485 EndAngle=7.85398
    g20: ArcOfCircle CenterX=-11.49 CenterY=21.5 CenterZ=0 NormalX=0 NormalY=0 NormalZ=1 AngleXU=0 Radius=1.5 StartAngle=4.71239 EndAngle=7.85398
    g21: ArcOfCircle CenterX=-1.5 CenterY=4.25 CenterZ=0 NormalX=0 NormalY=0 NormalZ=1 AngleXU=0 Radius=1.5 StartAngle=4.71239 EndAngle=7.85398
    g22: ArcOfCircle CenterX=-1.5 CenterY=10 CenterZ=0 NormalX=0 NormalY=0 NormalZ=1 AngleXU=0 Radius=1.5 StartAngle=4.71239 EndAngle=7.85398
    g23: ArcOfCircle CenterX=-1.5 CenterY=15.75 CenterZ=0 NormalX=0 NormalY=0 NormalZ=1 AngleXU=0 Radius=1.5 StartAngle=4.71239 EndAngle=7.85398
    g24: LineSegment StartX=-49.19 StartY=69.25 StartZ=0 EndX=-1.5 EndY=69.25 EndZ=0
    g25: LineSegment StartX=-49.19 StartY=66.25 StartZ=0 EndX=-1.5 EndY=66.25 EndZ=0
    g26: LineSegment StartX=-49.19 StartY=63.5 StartZ=0 EndX=-1.5 EndY=63.5 EndZ=0
    g27: LineSegment StartX=-49.19 StartY=60.5 StartZ=0 EndX=-1.5 EndY=60.5 EndZ=0
    g28: LineSegment StartX=-49.19 StartY=57.75 StartZ=0 EndX=-1.5 EndY=57.75 EndZ=0
    g29: LineSegment StartX=-49.19 StartY=54.75 StartZ=0 EndX=-1.5 EndY=54.75 EndZ=0
    g30: LineSegment StartX=-49.19 StartY=52 StartZ=0 EndX=-11.49 EndY=52 EndZ=0
    g31: LineSegment StartX=-49.19 StartY=49 StartZ=0 EndX=-11.49 EndY=49 EndZ=0
    g32: LineSegment StartX=-49.19 StartY=46.25 StartZ=0 EndX=-16.28 EndY=46.25 EndZ=0
    g33: LineSegment StartX=-49.19 StartY=43.25 StartZ=0 EndX=-16.28 EndY=43.25 EndZ=0
    g34: LineSegment StartX=-49.19 StartY=40.5 StartZ=0 EndX=-18.2337 EndY=40.5 EndZ=0
    g35: LineSegment StartX=-49.19 StartY=37.5 StartZ=0 EndX=-18.23 EndY=37.5 EndZ=0
    g36: LineSegment StartX=-49.19 StartY=34.5 StartZ=0 EndX=-18.2337 EndY=34.5 EndZ=0
    g37: LineSegment StartX=-49.19 StartY=31.5 StartZ=0 EndX=-18.23 EndY=31.5 EndZ=0
    g38: LineSegment StartX=-49.19 StartY=28.75 StartZ=0 EndX=-16.2837 EndY=28.75 EndZ=0
    g39: LineSegment StartX=-49.19 StartY=25.75 StartZ=0 EndX=-16.28 EndY=25.75 EndZ=0
    g40: LineSegment StartX=-49.19 StartY=23 StartZ=0 EndX=-11.49 EndY=23 EndZ=0
    g41: LineSegment StartX=-49.19 StartY=20 StartZ=0 EndX=-11.49 EndY=20 EndZ=0
    g42: LineSegment StartX=-49.19 StartY=17.25 StartZ=0 EndX=-1.5 EndY=17.25 EndZ=0
    g43: LineSegment StartX=-49.19 StartY=14.25 StartZ=0 EndX=-1.5 EndY=14.25 EndZ=0
    g44: LineSegment StartX=-49.19 StartY=11.5 StartZ=0 EndX=-1.5 EndY=11.5 EndZ=0
    g45: LineSegment StartX=-49.19 StartY=8.5 StartZ=0 EndX=-1.5 EndY=8.5 EndZ=0
    g46: LineSegment StartX=-49.19 StartY=5.75 StartZ=0 EndX=-1.5 EndY=5.75 EndZ=0
    g47: LineSegment StartX=-49.19 StartY=2.75 StartZ=0 EndX=-1.5 EndY=2.75 EndZ=0
  constraints (120):
    c: Vertical(g0)
    c: Distance(g0) = 3
    c: Block(g0)
    c: Vertical(g1)
    c: Distance(g1) = 3
    c: Vertical(g2)
    c: Equal(g0,g2) = 3
    c: Block(g2)
    c: Vertical(g3)
    c: Equal(g1,g3) = 3
    c: Vertical(g4)
    c: Equal(g0,g4) = 3
    c: Block(g4)
    c: Vertical(g5)
    c: Equal(g1,g5) = 3
    c: Vertical(g6)
    c: Equal(g0,g6) = 3
    c: Block(g6)
    c: Vertical(g7)
    c: Equal(g1,g7) = 3
    c: Vertical(g8)
    c: Equal(g0,g8) = 3
    c: Block(g8)
    c: Vertical(g9)
    c: Equal(g1,g9) = 3
    c: Vertical(g10)
    c: Equal(g0,g10) = 3
    c: Block(g10)
    c: Vertical(g11)
    c: Equal(g1,g11) = 3
    c: Block(g12)
    c: Block(g13)
    c: Block(g14)
    c: Block(g15)
    c: Block(g16)
    c: Block(g17)
    c: Block(g18)
    c: Block(g19)
    c: Block(g20)
    c: Block(g21)
    c: Block(g22)
    c: Block(g23)
    c: Block(g11)
    c: Block(g9)
    c: Block(g7)
    c: Block(g5)
    c: Block(g3)
    c: Block(g1)
    c: Coincident(g24,g0)
    c: Coincident(g24,g12)
    c: Horizontal(g24)
    c: Coincident(g25,g0)
    c: Coincident(g25,g12)
    c: Horizontal(g25)
    c: Coincident(g26,g1)
    c: Coincident(g26,g13)
    c: Horizontal(g26)
    c: Coincident(g27,g1)
    c: Coincident(g27,g13)
    c: Horizontal(g27)
    c: Coincident(g28,g2)
    c: Coincident(g28,g14)
    c: Horizontal(g28)
    c: Coincident(g29,g2)
    c: Coincident(g29,g14)
    c: Horizontal(g29)
    c: Coincident(g30,g3)
    c: Coincident(g30,g15)
    c: Horizontal(g30)
    c: Coincident(g31,g3)
    c: Coincident(g31,g15)
    c: Horizontal(g31)
    c: Coincident(g32,g4)
    c: Coincident(g32,g16)
    c: Horizontal(g32)
    c: Coincident(g33,g4)
    c: Coincident(g33,g16)
    c: Horizontal(g33)
    c: Coincident(g34,g5)
    c: Coincident(g34,g17)
    c: Horizontal(g34)
    c: Coincident(g35,g5)
    c: Coincident(g35,g17)
    c: Horizontal(g35)
    c: Coincident(g36,g6)
    c: Coincident(g36,g19)
    c: Horizontal(g36)
    c: Coincident(g37,g6)
    c: Coincident(g37,g19)
    c: Horizontal(g37)
    c: Coincident(g38,g7)
    c: Coincident(g38,g18)
    c: Horizontal(g38)
    c: Coincident(g39,g7)
    c: Coincident(g39,g18)
    c: Horizontal(g39)
    c: Coincident(g40,g8)
    c: Coincident(g40,g20)
    c: Horizontal(g40)
    c: Coincident(g41,g8)
    c: Coincident(g41,g20)
    c: Horizontal(g41)
    c: Coincident(g42,g9)
    c: Coincident(g42,g23)
    c: Horizontal(g42)
    c: Coincident(g43,g9)
    c: Coincident(g43,g23)
    c: Horizontal(g43)
    c: Coincident(g44,g10)
    c: Coincident(g44,g22)
    c: Horizontal(g44)
    c: Coincident(g45,g10)
    c: Coincident(g45,g22)
    c: Horizontal(g45)
    c: Coincident(g46,g11)
    c: Coincident(g46,g21)
    c: Horizontal(g46)
    c: Coincident(g47,g11)
    c: Coincident(g47,g21)
    c: Horizontal(g47)
FEATURE [Part::Extrusion] Extrude042
  Base = -> Sketch051
  Dir = (1,-2e-16,2e-16)
  DirMode = 2
  FaceMakerClass = Part::FaceMakerBullseye
  LengthFwd = 19
  LengthRev = 0
  Placement = pos=(-19,0,0) rot=(0,0,1;0rad)
  Solid = true
  Symmetric = false
FEATURE [Part::Fillet] Fillet035  label="removeToCreateVentalationHoles"
  Base = -> Extrude042
  Edges = <same value as first occurrence — deduplicated (x6 in doc)>
  Placement = pos=(7,0,0) rot=(0,0,1;0rad)
FEATURE [Part::Cut] Cut038  label="top017"
  Base = -> Cut033
  Tool = -> Fillet035
FEATURE [Sketcher::SketchObject] Sketch052  label="bottomSketch001"
  FullyConstrained = true
  sketch-geometry (45):
    g0: LineSegment StartX=6.29999 StartY=8 StartZ=0 EndX=3.29999 EndY=8 EndZ=0
    g1: LineSegment StartX=3.29999 StartY=8 StartZ=0 EndX=3.29999 EndY=-6.03275e-07 EndZ=0
    g2: ArcOfCircle CenterX=8.29999 CenterY=5 CenterZ=0 NormalX=0 NormalY=0 NormalZ=1 AngleXU=0 Radius=2 StartAngle=3.14159 EndAngle=4.71239
    g3: LineSegment StartX=6.29999 StartY=8 StartZ=0 EndX=6.29999 EndY=5 EndZ=0
    g4: ArcOfCircle CenterX=105 CenterY=19 CenterZ=0 NormalX=0 NormalY=0 NormalZ=1 AngleXU=0 Radius=12.7 StartAngle=4.71239 EndAngle=5.94289
    g5-g11: Circle x7 (B-spline internal-alignment scaffolding for g12; pole/knot coordinates omitted)
    g12: BSplineCurve PolesCount=7 KnotsCount=5 Degree=3 IsPeriodic=0
    g13-g17: GeomPoint x5 (B-spline internal-alignment scaffolding for g12; pole/knot coordinates omitted)
    g18: ArcOfCircle CenterX=105 CenterY=19 CenterZ=0 NormalX=0 NormalY=0 NormalZ=1 AngleXU=0 Radius=15.7 StartAngle=5.81226 EndAngle=6.28319
    g19: BSplineCurve PolesCount=5 KnotsCount=3 Degree=3 IsPeriodic=0
    g20: LineSegment StartX=8.29999 StartY=3 StartZ=0 EndX=101.7 EndY=3 EndZ=0
    g21: LineSegment StartX=3.29999 StartY=-6.03275e-07 StartZ=0 EndX=105 EndY=-6.03275e-07 EndZ=0
    g22: LineSegment StartX=120.974 StartY=8.71251 StartZ=0 EndX=122.332 EndY=7.83778 EndZ=0
    g23: LineSegment StartX=105 StartY=-6.03274e-07 StartZ=0 EndX=113 EndY=-6.03274e-07 EndZ=0
    g24: ArcOfCircle CenterX=105 CenterY=19 CenterZ=0 NormalX=0 NormalY=0 NormalZ=1 AngleXU=0 Radius=20.6155 StartAngle=5.11091 EndAngle=5.71103
    g25: ArcOfCircle CenterX=117.7 CenterY=19 CenterZ=0 NormalX=0 NormalY=0 NormalZ=1 AngleXU=0 Radius=3 StartAngle=1.2e-15 EndAngle=2.10468
    g26: Circle CenterX=116.345 CenterY=16.3232 CenterZ=0 NormalX=0 NormalY=0 NormalZ=1 AngleXU=0 Radius=1
    g27: Circle CenterX=117.24 CenterY=15.7584 CenterZ=0 NormalX=0 NormalY=0 NormalZ=1 AngleXU=0 Radius=1
    g28: Circle CenterX=116.972 CenterY=14.7612 CenterZ=0 NormalX=0 NormalY=0 NormalZ=1 AngleXU=0 Radius=1
    g29: BSplineCurve PolesCount=3 KnotsCount=2 Degree=2 IsPeriodic=0
    g30: GeomPoint X=116.345 Y=16.3232 Z=0
    g31: GeomPoint X=116.972 Y=14.7612 Z=0
    g32: Circle CenterX=115.828 CenterY=17.157 CenterZ=0 NormalX=0 NormalY=0 NormalZ=1 AngleXU=0 Radius=1
    g33: Circle CenterX=115.841 CenterY=16.639 CenterZ=0 NormalX=0 NormalY=0 NormalZ=1 AngleXU=0 Radius=1
    g34: Circle CenterX=116.345 CenterY=16.3232 CenterZ=0 NormalX=0 NormalY=0 NormalZ=1 AngleXU=0 Radius=1
    g35: BSplineCurve PolesCount=3 KnotsCount=2 Degree=2 IsPeriodic=0
    g36: GeomPoint X=115.828 Y=17.157 Z=0
    g37: GeomPoint X=116.345 Y=16.3232 Z=0
    g38: LineSegment StartX=115.828 StartY=17.157 StartZ=0 EndX=115.828 EndY=20.8307 EndZ=0
    g39: Circle CenterX=115.828 CenterY=20.8307 CenterZ=0 NormalX=0 NormalY=0 NormalZ=1 AngleXU=0 Radius=1
    g40: Circle CenterX=115.831 CenterY=21.3396 CenterZ=0 NormalX=0 NormalY=0 NormalZ=1 AngleXU=0 Radius=1
    g41: Circle CenterX=116.173 CenterY=21.5825 CenterZ=0 NormalX=0 NormalY=0 NormalZ=1 AngleXU=0 Radius=1
    g42: BSplineCurve PolesCount=3 KnotsCount=2 Degree=2 IsPeriodic=0
    g43: GeomPoint X=115.828 Y=20.8307 Z=0
    g44: GeomPoint X=116.173 Y=21.5825 Z=0
  constraints (70):
    c: Horizontal(g0)
    c: Distance(g0) = 3
    c: Coincident(g1,g0)
    c: Vertical(g1)
    c: Block(g2)
    c: Block(g0)
    c: Coincident(g3,g0)
    c: Coincident(g3,g2)
    c: Vertical(g3)
    c: Block(g1)
    c: Block(g4)
    c: Coincident(g19,g4)
    c: Block(g19)
    c: Equal(g5, g6-g11) x6
    c: InternalAlignment(g5-g11 -> g12) x7
    c: InternalAlignment(g13-g17 -> g12) x5
    c: Block(g12)
    c: Coincident(g18,g12)
    c: Block(g18)
    c: Coincident(g20,g2)
    c: Coincident(g20,g19)
    c: Horizontal(g20)
    c: Distance(g20) = 93.4
    c: Coincident(g21,g1)
    c: Horizontal(g21)
    c: Distance(g21) = 101.7
    c: Horizontal(g23)
    c: Distance(g23) = 8
    c: Coincident(g24,g23)
    c: Block(g23)
    c: Coincident(g22,g24)
    c: Block(g24)
    c: Block(g22)
    c: Distance(g22) = 1.61553
    c: Coincident(g25,g18)
    c: Block(g25)
    c: Weight(g26) = 1
    c: Equal(g26,g27)
    c: Equal(g26,g28)
    c: Coincident(g29,g4)
    c: InternalAlignment(g26,g29)
    c: InternalAlignment(g27,g29)
    c: InternalAlignment(g28,g29)
    c: InternalAlignment(g30,g29)
    c: InternalAlignment(g31,g29)
    c: Block(g29)
    c: Weight(g32) = 1
    c: Equal(g32,g33)
    c: Equal(g32,g34)
    c: Coincident(g35,g29)
    c: InternalAlignment(g32,g35)
    c: InternalAlignment(g33,g35)
    c: InternalAlignment(g34,g35)
    c: InternalAlignment(g36,g35)
    c: InternalAlignment(g37,g35)
    c: Block(g35)
    c: Coincident(g38,g35)
    c: Vertical(g38)
    c: Block(g38)
    c: Coincident(g42,g38)
    c: Weight(g39) = 1
    c: Equal(g39,g40)
    c: Equal(g39,g41)
    c: Coincident(g42,g25)
    c: InternalAlignment(g39,g42)
    c: InternalAlignment(g40,g42)
    c: InternalAlignment(g41,g42)
    c: InternalAlignment(g43,g42)
    c: InternalAlignment(g44,g42)
    c: Block(g42)
FEATURE [Part::Extrusion] Extrude043  label="bottom010"
  Base = -> Sketch052
  Dir = (0,0,1)
  DirMode = 2
  FaceMakerClass = Part::FaceMakerBullseye
  LengthFwd = 71.4
  LengthRev = 0
  Placement = pos=(0,0,0.3) rot=(0,0,1;0rad)
  Solid = true
  Symmetric = false
FEATURE [Sketcher::SketchObject] Sketch053  label="topSketch013"
  FullyConstrained = true
  sketch-geometry (22):
    g0: LineSegment StartX=5.21097e-06 StartY=3 StartZ=0 EndX=5.21097e-06 EndY=19 EndZ=0
    g1: ArcOfCircle CenterX=19 CenterY=19 CenterZ=0 NormalX=0 NormalY=0 NormalZ=1 AngleXU=0 Radius=19 StartAngle=1.5708 EndAngle=3.14159
    g2: ArcOfCircle CenterX=19 CenterY=19 CenterZ=0 NormalX=0 NormalY=0 NormalZ=1 AngleXU=0 Radius=16 StartAngle=1.5708 EndAngle=3.14159
    g3: LineSegment StartX=114 StartY=35 StartZ=0 EndX=19 EndY=35 EndZ=0
    g4: LineSegment StartX=5.21097e-06 StartY=3 StartZ=0 EndX=5.21097e-06 EndY=0 EndZ=0
    g5: LineSegment StartX=3 StartY=0 StartZ=0 EndX=5.21097e-06 EndY=0 EndZ=0
    g6: LineSegment StartX=3 StartY=19 StartZ=0 EndX=3 EndY=0 EndZ=0
    g7: LineSegment StartX=19 StartY=38 StartZ=0 EndX=124 EndY=38 EndZ=0
    g8: Circle CenterX=119 CenterY=35 CenterZ=0 NormalX=0 NormalY=0 NormalZ=1 AngleXU=0 Radius=1
    g9: Circle CenterX=121 CenterY=35 CenterZ=0 NormalX=0 NormalY=0 NormalZ=1 AngleXU=0 Radius=1
    g10: Circle CenterX=121 CenterY=33 CenterZ=0 NormalX=0 NormalY=0 NormalZ=1 AngleXU=0 Radius=1
    g11: BSplineCurve PolesCount=3 KnotsCount=2 Degree=2 IsPeriodic=0
    g12: GeomPoint X=119 Y=35 Z=0
    g13: GeomPoint X=121 Y=33 Z=0
    g14: LineSegment StartX=119 StartY=35 StartZ=0 EndX=114 EndY=35 EndZ=0
    g15: ArcOfCircle CenterX=105 CenterY=19 CenterZ=0 NormalX=0 NormalY=0 NormalZ=1 AngleXU=0 Radius=16 StartAngle=5.60905 EndAngle=6.28319
    g16: LineSegment StartX=121 StartY=33 StartZ=0 EndX=121 EndY=19 EndZ=0
    g17: LineSegment StartX=117.5 StartY=9.01251 StartZ=0 EndX=121.163 EndY=9.0125 EndZ=0
    g18: ArcOfCircle CenterX=105 CenterY=19 CenterZ=0 NormalX=0 NormalY=0 NormalZ=1 AngleXU=0 Radius=20.6155 StartAngle=5.7297 EndAngle=6.28319
    g19: LineSegment StartX=121.163 StartY=9.0125 StartZ=0 EndX=122.538 EndY=8.16329 EndZ=0
    g20: LineSegment StartX=124 StartY=38 StartZ=0 EndX=125.616 EndY=38 EndZ=0
    g21: LineSegment StartX=125.616 StartY=19 StartZ=0 EndX=125.616 EndY=38 EndZ=0
  constraints (50):
    c: Vertical(g0)
    c: Block(g0)
    c: Coincident(g1,g0)
    c: Block(g1)
    c: Coincident(g2,g1)
    c: Block(g2)
    c: Coincident(g3,g2)
    c: Horizontal(g3)
    c: Tangent(g3,g2)
    c: Coincident(g4,g0)
    c: Distance(g4) = 3
    c: Vertical(g4)
    c: Coincident(g5,g4)
    c: Horizontal(g5)
    c: Coincident(g6,g2)
    c: Coincident(g6,g5)
    c: Vertical(g6)
    c: Horizontal(g7)
    c: Distance(g7) = 105
    c: Coincident(g7,g1)
    c: Block(g3)
    c: Weight(g8) = 1
    c: Equal(g8,g9)
    c: Equal(g8,g10)
    c: InternalAlignment(g8,g11)
    c: InternalAlignment(g9,g11)
    c: InternalAlignment(g10,g11)
    c: InternalAlignment(g12,g11)
    c: InternalAlignment(g13,g11)
    c: Block(g11)
    c: Coincident(g14,g11)
    c: Coincident(g14,g3)
    c: Horizontal(g14)
    c: Block(g15)
    c: Coincident(g16,g11)
    c: Coincident(g16,g15)
    c: Vertical(g16)
    c: Distance(g16) = 14
    c: Coincident(g17,g15)
    c: Block(g18)
    c: Coincident(g19,g18)
    c: Coincident(g20,g7)
    c: Horizontal(g20)
    c: Vertical(g21)
    c: Coincident(g20,g21)
    c: Block(g20)
    c: Block(g21)
    c: Block(g19)
    c: Block(g17)
    c: Distance(g20) = 1.61553
FEATURE [Part::Extrusion] Extrude044
  Base = -> Sketch053
  Dir = (0,0,1)
  DirMode = 2
  FaceMakerClass = Part::FaceMakerBullseye
  LengthFwd = 72
  LengthRev = 0
  Solid = true
  Symmetric = false
FEATURE [Part::Fillet] Fillet036  label="top018"
  Base = -> Extrude044
  Edges = 1 edges r=2: [Edge41]
FEATURE [Sketcher::SketchObject] Sketch054
  FullyConstrained = false
  Placement = pos=(0,0,0) rot=(1,0,0;1.5708rad)
  sketch-geometry (24):
    g0: ArcOfCircle CenterX=-4 CenterY=-10.5 CenterZ=0 NormalX=0 NormalY=0 NormalZ=1 AngleXU=0 Radius=1.5 StartAngle=6e-16 EndAngle=3.14159
    g1: ArcOfCircle CenterX=-34.2 CenterY=-10.5 CenterZ=0 NormalX=0 NormalY=0 NormalZ=1 AngleXU=0 Radius=1.5 StartAngle=0 EndAngle=3.14159
    g2: ArcOfCircle CenterX=-34.2 CenterY=-27.7 CenterZ=0 NormalX=0 NormalY=0 NormalZ=1 AngleXU=0 Radius=1.5 StartAngle=3.14159 EndAngle=6.28319
    g3: ArcOfCircle CenterX=-4 CenterY=-27.7 CenterZ=0 NormalX=0 NormalY=0 NormalZ=1 AngleXU=0 Radius=1.5 StartAngle=3.1416 EndAngle=6.28319
    g4: ArcOfCircle CenterX=-10 CenterY=-4.3 CenterZ=0 NormalX=0 NormalY=0 NormalZ=1 AngleXU=0 Radius=1.5 StartAngle=2e-16 EndAngle=3.14159
    g5: ArcOfCircle CenterX=-16.1 CenterY=-1.8 CenterZ=0 NormalX=0 NormalY=0 NormalZ=1 AngleXU=0 Radius=1.5 StartAngle=5e-16 EndAngle=3.14159
    g6: ArcOfCircle CenterX=-22.1 CenterY=-1.8 CenterZ=0 NormalX=0 NormalY=0 NormalZ=1 AngleXU=0 Radius=1.5 StartAngle=5e-16 EndAngle=3.14159
    g7: ArcOfCircle CenterX=-28.2 CenterY=-4.3 CenterZ=0 NormalX=0 NormalY=0 NormalZ=1 AngleXU=0 Radius=1.5 StartAngle=2e-16 EndAngle=3.14159
    g8: ArcOfCircle CenterX=-10 CenterY=-33.9 CenterZ=0 NormalX=0 NormalY=0 NormalZ=1 AngleXU=0 Radius=1.5 StartAngle=3.14159 EndAngle=6.28319
    g9: ArcOfCircle CenterX=-16.1 CenterY=-36.4 CenterZ=0 NormalX=0 NormalY=0 NormalZ=1 AngleXU=0 Radius=1.5 StartAngle=3.14159 EndAngle=6.28319
    g10: ArcOfCircle CenterX=-22.1 CenterY=-36.4 CenterZ=0 NormalX=0 NormalY=0 NormalZ=1 AngleXU=0 Radius=1.5 StartAngle=3.14159 EndAngle=6.28319
    g11: ArcOfCircle CenterX=-28.2 CenterY=-33.9 CenterZ=0 NormalX=0 NormalY=0 NormalZ=1 AngleXU=0 Radius=1.5 StartAngle=3.14159 EndAngle=6.28319
    g12: LineSegment StartX=-35.7 StartY=-10.5 StartZ=0 EndX=-35.7 EndY=-27.7 EndZ=0
    g13: LineSegment StartX=-32.7 StartY=-10.5 StartZ=0 EndX=-32.7 EndY=-27.7 EndZ=0
    g14: LineSegment StartX=-29.7 StartY=-33.9 StartZ=0 EndX=-29.7 EndY=-4.3 EndZ=0
    g15: LineSegment StartX=-26.7 StartY=-33.9 StartZ=0 EndX=-26.7 EndY=-4.3 EndZ=0
    g16: LineSegment StartX=-2.5 StartY=-10.5 StartZ=0 EndX=-2.5 EndY=-27.7 EndZ=0
    g17: LineSegment StartX=-8.5 StartY=-4.3 StartZ=0 EndX=-8.5 EndY=-33.9 EndZ=0
    g18: LineSegment StartX=-5.5 StartY=-10.5 StartZ=0 EndX=-5.5 EndY=-27.7 EndZ=0
    g19: LineSegment StartX=-11.5 StartY=-4.3 StartZ=0 EndX=-11.5 EndY=-33.9 EndZ=0
    g20: LineSegment StartX=-14.6 StartY=-1.8 StartZ=0 EndX=-14.6 EndY=-36.4 EndZ=0
    g21: LineSegment StartX=-17.6 StartY=-1.8 StartZ=0 EndX=-17.6 EndY=-36.4 EndZ=0
    g22: LineSegment StartX=-20.6 StartY=-36.4 StartZ=0 EndX=-20.6 EndY=-1.8 EndZ=0
    g23: LineSegment StartX=-23.6 StartY=-1.8 StartZ=0 EndX=-23.6 EndY=-36.4 EndZ=0
  constraints (48):
    c: Block(g0)
    c: Block(g1)
    c: Block(g2)
    c: Block(g3)
    c: Block(g4)
    c: Block(g5)
    c: Block(g6)
    c: Block(g7)
    c: Block(g8)
    c: Block(g9)
    c: Block(g10)
    c: Block(g11)
    c: Coincident(g12,g1)
    c: Coincident(g12,g2)
    c: Vertical(g12)
    c: Coincident(g13,g1)
    c: Coincident(g13,g2)
    c: Vertical(g13)
    c: Coincident(g14,g11)
    c: Coincident(g14,g7)
    c: Vertical(g14)
    c: Coincident(g15,g11)
    c: Coincident(g15,g7)
    c: Vertical(g15)
    c: Coincident(g16,g0)
    c: Coincident(g16,g3)
    c: Vertical(g16)
    c: Coincident(g17,g4)
    c: Coincident(g17,g8)
    c: Vertical(g17)
    c: Coincident(g18,g0)
    c: Coincident(g18,g3)
    c: Vertical(g18)
    c: Coincident(g19,g4)
    c: Coincident(g19,g8)
    c: Vertical(g19)
    c: Coincident(g20,g5)
    c: Coincident(g20,g9)
    c: Vertical(g20)
    c: Coincident(g21,g5)
    c: Coincident(g21,g9)
    c: Vertical(g21)
    c: Coincident(g22,g10)
    c: Coincident(g22,g6)
    c: Vertical(g22)
    c: Coincident(g23,g6)
    c: Coincident(g23,g10)
    c: Vertical(g23)
FEATURE [Part::Extrusion] Extrude045  label="removeToCreateFanGrillHoles003"
  Base = -> Sketch054
  Dir = (0,-1,6e-16)
  DirMode = 2
  FaceMakerClass = Part::FaceMakerBullseye
  LengthFwd = 10
  LengthRev = 0
  Placement = pos=(65.4,44,54.82) rot=(0,0,1;0rad)
  Solid = true
  Symmetric = false
FEATURE [Part::Feature] Face105 .. Face108  x4 (patterned run collapsed; names and placements below)
  shape: bbox 3.5 x 17.8 x 2e-07 mm, 1 faces, 0 solids (baked)
FEATURE [Part::Revolution] Revolve113  label="removeToCreateScrewAndThreadedInsertHole041"
  Angle = 360
  Axis = (0,1,0)
  Base = (0,0,0)
  FaceMakerClass = Part::FaceMakerBullseye
  Placement = pos=(62.3,30.3,19.7) rot=(0,0,1;0rad)
  Solid = false
  Source = -> Face105
  Symmetric = false
FEATURE [Part::Revolution] Revolve114  label="removeToCreateScrewAndThreadedInsertHole042"
  Angle = 360
  Axis = (0,1,0)
  Base = (0,0,0)
  FaceMakerClass = Part::FaceMakerBullseye
  Placement = pos=(62.3,30.3,51.7) rot=(0,0,1;0rad)
  Solid = false
  Source = -> Face106
  Symmetric = false
FEATURE [Part::Revolution] Revolve115  label="removeToCreateScrewAndThreadedInsertHole043"
  Angle = 360
  Axis = (0,1,0)
  Base = (0,0,0)
  FaceMakerClass = Part::FaceMakerBullseye
  Placement = pos=(30.3,30.3,19.7) rot=(0,0,1;0rad)
  Solid = false
  Source = -> Face107
  Symmetric = false
FEATURE [Part::Revolution] Revolve116  label="removeToCreateScrewAndThreadedInsertHole044"
  Angle = 360
  Axis = (0,1,0)
  Base = (0,0,0)
  FaceMakerClass = Part::FaceMakerBullseye
  Placement = pos=(30.3,30.3,51.7) rot=(0,0,1;0rad)
  Solid = false
  Source = -> Face108
  Symmetric = false
FEATURE [Part::MultiFuse] Fusion083  label="createThreadedInsertHolesForFan004"
  Shapes = -> [Revolve113,Revolve114,Revolve115,Revolve116]
FEATURE [Part::Box] Box024  label="removeToCreteHoleForPlugHousing026"
  AttacherType = Attacher::AttachEngine3D
  Height = 28.6
  Length = 10
  Placement = pos=(-2,0,21.7) rot=(0,0,1;0rad)
  Width = 19
FEATURE [Part::Cylinder] Cylinder038  label="removeToCreteHoleForPlugHousing027"
  Angle = 360
  AttacherType = Attacher::AttachEngine3D
  Height = 20
  Placement = pos=(-2,19,36) rot=(0,1,0;1.5708rad)
  Radius = 14.3
FEATURE [Part::MultiFuse] Fusion084  label="removeToCreteHoleForPlugHousing028"
  Shapes = -> [Box024,Cylinder038]
FEATURE [Part::Cylinder] Cylinder039
  Angle = 360
  AttacherType = Attacher::AttachEngine3D
  Height = 20
  Placement = pos=(0,0,36.15) rot=(0,0,1;0rad)
  Radius = 14.3
FEATURE [Part::Cylinder] Cylinder040
  Angle = 360
  AttacherType = Attacher::AttachEngine3D
  Height = 10
  Placement = pos=(0,0,36.15) rot=(0,0,1;0rad)
  Radius = 4
FEATURE [Part::Box] Box025  label="removeToCreteHoleForPlugHousing030"
  AttacherType = Attacher::AttachEngine3D
  Height = 28.6
  Length = 20
  Placement = pos=(106.15,0,21.7) rot=(0,0,1;0rad)
  Width = 19
FEATURE [Part::MultiFuse] Fusion086  label="removeToCreteHoleForPlugHousing031"
  Placement = pos=(70,19,36) rot=(0,1,0;1.5708rad)
  Shapes = -> [Cylinder039,Cylinder040]
FEATURE [Part::MultiFuse] Fusion085  label="removeToCreteHoleForPlugHousing029"
  Shapes = -> [Box025,Fusion086]
FEATURE [Sketcher::SketchObject] Sketch055
  FullyConstrained = true
  Placement = pos=(117,19,0) rot=(0.57735,0.57735,0.57735;2.0944rad)
  sketch-geometry (48):
    g0: LineSegment StartX=-49.19 StartY=69.25 StartZ=0 EndX=-49.19 EndY=66.25 EndZ=0
    g1: LineSegment StartX=-49.19 StartY=63.5 StartZ=0 EndX=-49.19 EndY=60.5 EndZ=0
    g2: LineSegment StartX=-49.19 StartY=57.75 StartZ=0 EndX=-49.19 EndY=54.75 EndZ=0
    g3: LineSegment StartX=-49.19 StartY=52 StartZ=0 EndX=-49.19 EndY=49 EndZ=0
    g4: LineSegment StartX=-49.19 StartY=46.25 StartZ=0 EndX=-49.19 EndY=43.25 EndZ=0
    g5: LineSegment StartX=-49.19 StartY=40.5 StartZ=0 EndX=-49.19 EndY=37.5 EndZ=0
    g6: LineSegment StartX=-49.19 StartY=34.5 StartZ=0 EndX=-49.19 EndY=31.5 EndZ=0
    g7: LineSegment StartX=-49.19 StartY=28.75 StartZ=0 EndX=-49.19 EndY=25.75 EndZ=0
    g8: LineSegment StartX=-49.19 StartY=23 StartZ=0 EndX=-49.19 EndY=20 EndZ=0
    g9: LineSegment StartX=-49.19 StartY=17.25 StartZ=0 EndX=-49.19 EndY=14.25 EndZ=0
    g10: LineSegment StartX=-49.19 StartY=11.5 StartZ=0 EndX=-49.19 EndY=8.5 EndZ=0
    g11: LineSegment StartX=-49.19 StartY=5.75 StartZ=0 EndX=-49.19 EndY=2.75 EndZ=0
    g12: ArcOfCircle CenterX=-1.5 CenterY=67.75 CenterZ=0 NormalX=0 NormalY=0 NormalZ=1 AngleXU=0 Radius=1.5 StartAngle=4.71239 EndAngle=7.85398
    g13: ArcOfCircle CenterX=-1.5 CenterY=62 CenterZ=0 NormalX=0 NormalY=0 NormalZ=1 AngleXU=0 Radius=1.5 StartAngle=4.71239 EndAngle=7.85398
    g14: ArcOfCircle CenterX=-1.5 CenterY=56.25 CenterZ=0 NormalX=0 NormalY=0 NormalZ=1 AngleXU=0 Radius=1.5 StartAngle=4.71239 EndAngle=7.85398
    g15: ArcOfCircle CenterX=-11.49 CenterY=50.5 CenterZ=0 NormalX=0 NormalY=0 NormalZ=1 AngleXU=0 Radius=1.5 StartAngle=4.71239 EndAngle=7.85398
    g16: ArcOfCircle CenterX=-16.28 CenterY=44.75 CenterZ=0 NormalX=0 NormalY=0 NormalZ=1 AngleXU=0 Radius=1.5 StartAngle=4.71239 EndAngle=7.85398
    g17: ArcOfCircle CenterX=-18.2337 CenterY=39 CenterZ=0 NormalX=0 NormalY=0 NormalZ=1 AngleXU=0 Radius=1.5 StartAngle=4.71485 EndAngle=7.85398
    g18: ArcOfCircle CenterX=-16.2837 CenterY=27.25 CenterZ=0 NormalX=0 NormalY=0 NormalZ=1 AngleXU=0 Radius=1.5 StartAngle=4.71485 EndAngle=7.85398
    g19: ArcOfCircle CenterX=-18.2337 CenterY=33 CenterZ=0 NormalX=0 NormalY=0 NormalZ=1 AngleXU=0 Radius=1.5 StartAngle=4.71485 EndAngle=7.85398
    g20: ArcOfCircle CenterX=-11.49 CenterY=21.5 CenterZ=0 NormalX=0 NormalY=0 NormalZ=1 AngleXU=0 Radius=1.5 StartAngle=4.71239 EndAngle=7.85398
    g21: ArcOfCircle CenterX=-1.5 CenterY=4.25 CenterZ=0 NormalX=0 NormalY=0 NormalZ=1 AngleXU=0 Radius=1.5 StartAngle=4.71239 EndAngle=7.85398
    g22: ArcOfCircle CenterX=-1.5 CenterY=10 CenterZ=0 NormalX=0 NormalY=0 NormalZ=1 AngleXU=0 Radius=1.5 StartAngle=4.71239 EndAngle=7.85398
    g23: ArcOfCircle CenterX=-1.5 CenterY=15.75 CenterZ=0 NormalX=0 NormalY=0 NormalZ=1 AngleXU=0 Radius=1.5 StartAngle=4.71239 EndAngle=7.85398
    g24: LineSegment StartX=-49.19 StartY=69.25 StartZ=0 EndX=-1.5 EndY=69.25 EndZ=0
    g25: LineSegment StartX=-49.19 StartY=66.25 StartZ=0 EndX=-1.5 EndY=66.25 EndZ=0
    g26: LineSegment StartX=-49.19 StartY=63.5 StartZ=0 EndX=-1.5 EndY=63.5 EndZ=0
    g27: LineSegment StartX=-49.19 StartY=60.5 StartZ=0 EndX=-1.5 EndY=60.5 EndZ=0
    g28: LineSegment StartX=-49.19 StartY=57.75 StartZ=0 EndX=-1.5 EndY=57.75 EndZ=0
    g29: LineSegment StartX=-49.19 StartY=54.75 StartZ=0 EndX=-1.5 EndY=54.75 EndZ=0
    g30: LineSegment StartX=-49.19 StartY=52 StartZ=0 EndX=-11.49 EndY=52 EndZ=0
    g31: LineSegment StartX=-49.19 StartY=49 StartZ=0 EndX=-11.49 EndY=49 EndZ=0
    g32: LineSegment StartX=-49.19 StartY=46.25 StartZ=0 EndX=-16.28 EndY=46.25 EndZ=0
    g33: LineSegment StartX=-49.19 StartY=43.25 StartZ=0 EndX=-16.28 EndY=43.25 EndZ=0
    g34: LineSegment StartX=-49.19 StartY=40.5 StartZ=0 EndX=-18.2337 EndY=40.5 EndZ=0
    g35: LineSegment StartX=-49.19 StartY=37.5 StartZ=0 EndX=-18.23 EndY=37.5 EndZ=0
    g36: LineSegment StartX=-49.19 StartY=34.5 StartZ=0 EndX=-18.2337 EndY=34.5 EndZ=0
    g37: LineSegment StartX=-49.19 StartY=31.5 StartZ=0 EndX=-18.23 EndY=31.5 EndZ=0
    g38: LineSegment StartX=-49.19 StartY=28.75 StartZ=0 EndX=-16.2837 EndY=28.75 EndZ=0
    g39: LineSegment StartX=-49.19 StartY=25.75 StartZ=0 EndX=-16.28 EndY=25.75 EndZ=0
    g40: LineSegment StartX=-49.19 StartY=23 StartZ=0 EndX=-11.49 EndY=23 EndZ=0
    g41: LineSegment StartX=-49.19 StartY=20 StartZ=0 EndX=-11.49 EndY=20 EndZ=0
    g42: LineSegment StartX=-49.19 StartY=17.25 StartZ=0 EndX=-1.5 EndY=17.25 EndZ=0
    g43: LineSegment StartX=-49.19 StartY=14.25 StartZ=0 EndX=-1.5 EndY=14.25 EndZ=0
    g44: LineSegment StartX=-49.19 StartY=11.5 StartZ=0 EndX=-1.5 EndY=11.5 EndZ=0
    g45: LineSegment StartX=-49.19 StartY=8.5 StartZ=0 EndX=-1.5 EndY=8.5 EndZ=0
    g46: LineSegment StartX=-49.19 StartY=5.75 StartZ=0 EndX=-1.5 EndY=5.75 EndZ=0
    g47: LineSegment StartX=-49.19 StartY=2.75 StartZ=0 EndX=-1.5 EndY=2.75 EndZ=0
  constraints (120):
    c: Vertical(g0)
    c: Distance(g0) = 3
    c: Block(g0)
    c: Vertical(g1)
    c: Distance(g1) = 3
    c: Vertical(g2)
    c: Equal(g0,g2) = 3
    c: Block(g2)
    c: Vertical(g3)
    c: Equal(g1,g3) = 3
    c: Vertical(g4)
    c: Equal(g0,g4) = 3
    c: Block(g4)
    c: Vertical(g5)
    c: Equal(g1,g5) = 3
    c: Vertical(g6)
    c: Equal(g0,g6) = 3
    c: Block(g6)
    c: Vertical(g7)
    c: Equal(g1,g7) = 3
    c: Vertical(g8)
    c: Equal(g0,g8) = 3
    c: Block(g8)
    c: Vertical(g9)
    c: Equal(g1,g9) = 3
    c: Vertical(g10)
    c: Equal(g0,g10) = 3
    c: Block(g10)
    c: Vertical(g11)
    c: Equal(g1,g11) = 3
    c: Block(g12)
    c: Block(g13)
    c: Block(g14)
    c: Block(g15)
    c: Block(g16)
    c: Block(g17)
    c: Block(g18)
    c: Block(g19)
    c: Block(g20)
    c: Block(g21)
    c: Block(g22)
    c: Block(g23)
    c: Block(g11)
    c: Block(g9)
    c: Block(g7)
    c: Block(g5)
    c: Block(g3)
    c: Block(g1)
    c: Coincident(g24,g0)
    c: Coincident(g24,g12)
    c: Horizontal(g24)
    c: Coincident(g25,g0)
    c: Coincident(g25,g12)
    c: Horizontal(g25)
    c: Coincident(g26,g1)
    c: Coincident(g26,g13)
    c: Horizontal(g26)
    c: Coincident(g27,g1)
    c: Coincident(g27,g13)
    c: Horizontal(g27)
    c: Coincident(g28,g2)
    c: Coincident(g28,g14)
    c: Horizontal(g28)
    c: Coincident(g29,g2)
    c: Coincident(g29,g14)
    c: Horizontal(g29)
    c: Coincident(g30,g3)
    c: Coincident(g30,g15)
    c: Horizontal(g30)
    c: Coincident(g31,g3)
    c: Coincident(g31,g15)
    c: Horizontal(g31)
    c: Coincident(g32,g4)
    c: Coincident(g32,g16)
    c: Horizontal(g32)
    c: Coincident(g33,g4)
    c: Coincident(g33,g16)
    c: Horizontal(g33)
    c: Coincident(g34,g5)
    c: Coincident(g34,g17)
    c: Horizontal(g34)
    c: Coincident(g35,g5)
    c: Coincident(g35,g17)
    c: Horizontal(g35)
    c: Coincident(g36,g6)
    c: Coincident(g36,g19)
    c: Horizontal(g36)
    c: Coincident(g37,g6)
    c: Coincident(g37,g19)
    c: Horizontal(g37)
    c: Coincident(g38,g7)
    c: Coincident(g38,g18)
    c: Horizontal(g38)
    c: Coincident(g39,g7)
    c: Coincident(g39,g18)
    c: Horizontal(g39)
    c: Coincident(g40,g8)
    c: Coincident(g40,g20)
    c: Horizontal(g40)
    c: Coincident(g41,g8)
    c: Coincident(g41,g20)
    c: Horizontal(g41)
    c: Coincident(g42,g9)
    c: Coincident(g42,g23)
    c: Horizontal(g42)
    c: Coincident(g43,g9)
    c: Coincident(g43,g23)
    c: Horizontal(g43)
    c: Coincident(g44,g10)
    c: Coincident(g44,g22)
    c: Horizontal(g44)
    c: Coincident(g45,g10)
    c: Coincident(g45,g22)
    c: Horizontal(g45)
    c: Coincident(g46,g11)
    c: Coincident(g46,g21)
    c: Horizontal(g46)
    c: Coincident(g47,g11)
    c: Coincident(g47,g21)
    c: Horizontal(g47)
FEATURE [Part::Extrusion] Extrude046
  Base = -> Sketch055
  Dir = (1,0,0)
  DirMode = 2
  FaceMakerClass = Part::FaceMakerBullseye
  LengthFwd = 23
  LengthRev = 0
  Placement = pos=(-19,0,0) rot=(0,0,1;0rad)
  Solid = true
  Symmetric = false
FEATURE [Part::Fillet] Fillet038  label="removeToCreateVentalationHoles001"
  Base = -> Extrude046
  Edges = <same value as first occurrence — deduplicated (x6 in doc)>
  Placement = pos=(7,0,0) rot=(0,0,1;0rad)
FEATURE [Sketcher::SketchObject] Sketch056  label="topSketch014"
  FullyConstrained = true
  sketch-geometry (22):
    g0: LineSegment StartX=5.21097e-06 StartY=3 StartZ=0 EndX=5.21097e-06 EndY=19 EndZ=0
    g1: ArcOfCircle CenterX=19 CenterY=19 CenterZ=0 NormalX=0 NormalY=0 NormalZ=1 AngleXU=0 Radius=19 StartAngle=1.5708 EndAngle=3.14159
    g2: ArcOfCircle CenterX=19 CenterY=19 CenterZ=0 NormalX=0 NormalY=0 NormalZ=1 AngleXU=0 Radius=16 StartAngle=1.5708 EndAngle=3.14159
    g3: LineSegment StartX=114 StartY=35 StartZ=0 EndX=19 EndY=35 EndZ=0
    g4: LineSegment StartX=5.21097e-06 StartY=3 StartZ=0 EndX=5.21097e-06 EndY=0 EndZ=0
    g5: LineSegment StartX=3 StartY=0 StartZ=0 EndX=5.21097e-06 EndY=0 EndZ=0
    g6: LineSegment StartX=3 StartY=19 StartZ=0 EndX=3 EndY=0 EndZ=0
    g7: LineSegment StartX=19 StartY=38 StartZ=0 EndX=124 EndY=38 EndZ=0
    g8: Circle CenterX=119 CenterY=35 CenterZ=0 NormalX=0 NormalY=0 NormalZ=1 AngleXU=0 Radius=1
    g9: Circle CenterX=121 CenterY=35 CenterZ=0 NormalX=0 NormalY=0 NormalZ=1 AngleXU=0 Radius=1
    g10: Circle CenterX=121 CenterY=33 CenterZ=0 NormalX=0 NormalY=0 NormalZ=1 AngleXU=0 Radius=1
    g11: BSplineCurve PolesCount=3 KnotsCount=2 Degree=2 IsPeriodic=0
    g12: GeomPoint X=119 Y=35 Z=0
    g13: GeomPoint X=121 Y=33 Z=0
    g14: LineSegment StartX=119 StartY=35 StartZ=0 EndX=114 EndY=35 EndZ=0
    g15: ArcOfCircle CenterX=105 CenterY=19 CenterZ=0 NormalX=0 NormalY=0 NormalZ=1 AngleXU=0 Radius=16 StartAngle=5.60905 EndAngle=6.28319
    g16: LineSegment StartX=121 StartY=33 StartZ=0 EndX=121 EndY=19 EndZ=0
    g17: LineSegment StartX=117.5 StartY=9.01251 StartZ=0 EndX=121.163 EndY=9.0125 EndZ=0
    g18: ArcOfCircle CenterX=105 CenterY=19 CenterZ=0 NormalX=0 NormalY=0 NormalZ=1 AngleXU=0 Radius=20.6155 StartAngle=5.7297 EndAngle=6.28319
    g19: LineSegment StartX=121.163 StartY=9.0125 StartZ=0 EndX=122.538 EndY=8.16329 EndZ=0
    g20: LineSegment StartX=124 StartY=38 StartZ=0 EndX=125.616 EndY=38 EndZ=0
    g21: LineSegment StartX=125.616 StartY=19 StartZ=0 EndX=125.616 EndY=38 EndZ=0
  constraints (49):
    c: Vertical(g0)
    c: Block(g0)
    c: Coincident(g1,g0)
    c: Block(g1)
    c: Coincident(g2,g1)
    c: Block(g2)
    c: Coincident(g3,g2)
    c: Horizontal(g3)
    c: Tangent(g3,g2)
    c: Coincident(g4,g0)
    c: Distance(g4) = 3
    c: Vertical(g4)
    c: Coincident(g5,g4)
    c: Horizontal(g5)
    c: Coincident(g6,g2)
    c: Coincident(g6,g5)
    c: Vertical(g6)
    c: Horizontal(g7)
    c: Distance(g7) = 105
    c: Coincident(g7,g1)
    c: Block(g3)
    c: Weight(g8) = 1
    c: Equal(g8,g9)
    c: Equal(g8,g10)
    c: InternalAlignment(g8,g11)
    c: InternalAlignment(g9,g11)
    c: InternalAlignment(g10,g11)
    c: InternalAlignment(g12,g11)
    c: InternalAlignment(g13,g11)
    c: Block(g11)
    c: Coincident(g14,g11)
    c: Coincident(g14,g3)
    c: Horizontal(g14)
    c: Block(g15)
    c: Coincident(g16,g11)
    c: Coincident(g16,g15)
    c: Vertical(g16)
    c: Distance(g16) = 14
    c: Coincident(g17,g15)
    c: Block(g18)
    c: Coincident(g19,g18)
    c: Coincident(g20,g7)
    c: Horizontal(g20)
    c: Vertical(g21)
    c: Coincident(g20,g21)
    c: Block(g20)
    c: Block(g21)
    c: Block(g19)
    c: Block(g17)
FEATURE [Part::Box] Box026  label="removeToCreteHoleForPlugHousing032"
  AttacherType = Attacher::AttachEngine3D
  Height = 28.6
  Length = 10
  Placement = pos=(-2,0,21.7) rot=(0,0,1;0rad)
  Width = 19
FEATURE [Part::Feature] Face109 .. Face112  x4 (patterned run collapsed; names and placements below)
  shape: bbox 3.5 x 17.8 x 2e-07 mm, 1 faces, 0 solids (baked)
FEATURE [Part::Revolution] Revolve117  label="removeToCreateScrewAndThreadedInsertHole045"
  Angle = 360
  Axis = (0,1,0)
  Base = (0,0,0)
  FaceMakerClass = Part::FaceMakerBullseye
  Placement = pos=(62.3,30.3,19.7) rot=(0,0,1;0rad)
  Solid = false
  Source = -> Face109
  Symmetric = false
FEATURE [Part::Revolution] Revolve118  label="removeToCreateScrewAndThreadedInsertHole046"
  Angle = 360
  Axis = (0,1,0)
  Base = (0,0,0)
  FaceMakerClass = Part::FaceMakerBullseye
  Placement = pos=(62.3,30.3,51.7) rot=(0,0,1;0rad)
  Solid = false
  Source = -> Face110
  Symmetric = false
FEATURE [Part::Revolution] Revolve119  label="removeToCreateScrewAndThreadedInsertHole047"
  Angle = 360
  Axis = (0,1,0)
  Base = (0,0,0)
  FaceMakerClass = Part::FaceMakerBullseye
  Placement = pos=(30.3,30.3,19.7) rot=(0,0,1;0rad)
  Solid = false
  Source = -> Face111
  Symmetric = false
FEATURE [Part::Revolution] Revolve120  label="removeToCreateScrewAndThreadedInsertHole048"
  Angle = 360
  Axis = (0,1,0)
  Base = (0,0,0)
  FaceMakerClass = Part::FaceMakerBullseye
  Placement = pos=(30.3,30.3,51.7) rot=(0,0,1;0rad)
  Solid = false
  Source = -> Face112
  Symmetric = false
FEATURE [Part::MultiFuse] Fusion087  label="createThreadedInsertHolesForFan005"
  Shapes = -> [Revolve117,Revolve118,Revolve119,Revolve120]
FEATURE [Part::Extrusion] Extrude047
  Base = -> Sketch056
  Dir = (0,0,1)
  DirMode = 2
  FaceMakerClass = Part::FaceMakerBullseye
  LengthFwd = 72
  LengthRev = 0
  Solid = true
  Symmetric = false
FEATURE [Part::Fillet] Fillet039  label="top019"
  Base = -> Extrude047
  Edges = 1 edges r=2: [Edge35]
FEATURE [Sketcher::SketchObject] Sketch057
  FullyConstrained = false
  Placement = pos=(0,0,0) rot=(1,0,0;1.5708rad)
  sketch-geometry (24):
    g0: ArcOfCircle CenterX=-4 CenterY=-10.5 CenterZ=0 NormalX=0 NormalY=0 NormalZ=1 AngleXU=0 Radius=1.5 StartAngle=6e-16 EndAngle=3.14159
    g1: ArcOfCircle CenterX=-34.2 CenterY=-10.5 CenterZ=0 NormalX=0 NormalY=0 NormalZ=1 AngleXU=0 Radius=1.5 StartAngle=0 EndAngle=3.14159
    g2: ArcOfCircle CenterX=-34.2 CenterY=-27.7 CenterZ=0 NormalX=0 NormalY=0 NormalZ=1 AngleXU=0 Radius=1.5 StartAngle=3.14159 EndAngle=6.28319
    g3: ArcOfCircle CenterX=-4 CenterY=-27.7 CenterZ=0 NormalX=0 NormalY=0 NormalZ=1 AngleXU=0 Radius=1.5 StartAngle=3.1416 EndAngle=6.28319
    g4: ArcOfCircle CenterX=-10 CenterY=-4.3 CenterZ=0 NormalX=0 NormalY=0 NormalZ=1 AngleXU=0 Radius=1.5 StartAngle=2e-16 EndAngle=3.14159
    g5: ArcOfCircle CenterX=-16.1 CenterY=-1.8 CenterZ=0 NormalX=0 NormalY=0 NormalZ=1 AngleXU=0 Radius=1.5 StartAngle=5e-16 EndAngle=3.14159
    g6: ArcOfCircle CenterX=-22.1 CenterY=-1.8 CenterZ=0 NormalX=0 NormalY=0 NormalZ=1 AngleXU=0 Radius=1.5 StartAngle=5e-16 EndAngle=3.14159
    g7: ArcOfCircle CenterX=-28.2 CenterY=-4.3 CenterZ=0 NormalX=0 NormalY=0 NormalZ=1 AngleXU=0 Radius=1.5 StartAngle=2e-16 EndAngle=3.14159
    g8: ArcOfCircle CenterX=-10 CenterY=-33.9 CenterZ=0 NormalX=0 NormalY=0 NormalZ=1 AngleXU=0 Radius=1.5 StartAngle=3.14159 EndAngle=6.28319
    g9: ArcOfCircle CenterX=-16.1 CenterY=-36.4 CenterZ=0 NormalX=0 NormalY=0 NormalZ=1 AngleXU=0 Radius=1.5 StartAngle=3.14159 EndAngle=6.28319
    g10: ArcOfCircle CenterX=-22.1 CenterY=-36.4 CenterZ=0 NormalX=0 NormalY=0 NormalZ=1 AngleXU=0 Radius=1.5 StartAngle=3.14159 EndAngle=6.28319
    g11: ArcOfCircle CenterX=-28.2 CenterY=-33.9 CenterZ=0 NormalX=0 NormalY=0 NormalZ=1 AngleXU=0 Radius=1.5 StartAngle=3.14159 EndAngle=6.28319
    g12: LineSegment StartX=-35.7 StartY=-10.5 StartZ=0 EndX=-35.7 EndY=-27.7 EndZ=0
    g13: LineSegment StartX=-32.7 StartY=-10.5 StartZ=0 EndX=-32.7 EndY=-27.7 EndZ=0
    g14: LineSegment StartX=-29.7 StartY=-33.9 StartZ=0 EndX=-29.7 EndY=-4.3 EndZ=0
    g15: LineSegment StartX=-26.7 StartY=-33.9 StartZ=0 EndX=-26.7 EndY=-4.3 EndZ=0
    g16: LineSegment StartX=-2.5 StartY=-10.5 StartZ=0 EndX=-2.5 EndY=-27.7 EndZ=0
    g17: LineSegment StartX=-8.5 StartY=-4.3 StartZ=0 EndX=-8.5 EndY=-33.9 EndZ=0
    g18: LineSegment StartX=-5.5 StartY=-10.5 StartZ=0 EndX=-5.5 EndY=-27.7 EndZ=0
    g19: LineSegment StartX=-11.5 StartY=-4.3 StartZ=0 EndX=-11.5 EndY=-33.9 EndZ=0
    g20: LineSegment StartX=-14.6 StartY=-1.8 StartZ=0 EndX=-14.6 EndY=-36.4 EndZ=0
    g21: LineSegment StartX=-17.6 StartY=-1.8 StartZ=0 EndX=-17.6 EndY=-36.4 EndZ=0
    g22: LineSegment StartX=-20.6 StartY=-36.4 StartZ=0 EndX=-20.6 EndY=-1.8 EndZ=0
    g23: LineSegment StartX=-23.6 StartY=-1.8 StartZ=0 EndX=-23.6 EndY=-36.4 EndZ=0
  constraints (48):
    c: Block(g0)
    c: Block(g1)
    c: Block(g2)
    c: Block(g3)
    c: Block(g4)
    c: Block(g5)
    c: Block(g6)
    c: Block(g7)
    c: Block(g8)
    c: Block(g9)
    c: Block(g10)
    c: Block(g11)
    c: Coincident(g12,g1)
    c: Coincident(g12,g2)
    c: Vertical(g12)
    c: Coincident(g13,g1)
    c: Coincident(g13,g2)
    c: Vertical(g13)
    c: Coincident(g14,g11)
    c: Coincident(g14,g7)
    c: Vertical(g14)
    c: Coincident(g15,g11)
    c: Coincident(g15,g7)
    c: Vertical(g15)
    c: Coincident(g16,g0)
    c: Coincident(g16,g3)
    c: Vertical(g16)
    c: Coincident(g17,g4)
    c: Coincident(g17,g8)
    c: Vertical(g17)
    c: Coincident(g18,g0)
    c: Coincident(g18,g3)
    c: Vertical(g18)
    c: Coincident(g19,g4)
    c: Coincident(g19,g8)
    c: Vertical(g19)
    c: Coincident(g20,g5)
    c: Coincident(g20,g9)
    c: Vertical(g20)
    c: Coincident(g21,g5)
    c: Coincident(g21,g9)
    c: Vertical(g21)
    c: Coincident(g22,g10)
    c: Coincident(g22,g6)
    c: Vertical(g22)
    c: Coincident(g23,g6)
    c: Coincident(g23,g10)
    c: Vertical(g23)
FEATURE [Part::Extrusion] Extrude048  label="removeToCreateFanGrillHoles004"
  Base = -> Sketch057
  Dir = (0,-1,6e-16)
  DirMode = 2
  FaceMakerClass = Part::FaceMakerBullseye
  LengthFwd = 10
  LengthRev = 0
  Placement = pos=(65.4,44,54.82) rot=(0,0,1;0rad)
  Solid = true
  Symmetric = false
FEATURE [Part::Cut] Cut040  label="top021"
  Base = -> Fillet039
  Tool = -> Extrude048
FEATURE [Part::Cylinder] Cylinder041  label="removeToCreteHoleForPlugHousing034"
  Angle = 360
  AttacherType = Attacher::AttachEngine3D
  Height = 20
  Placement = pos=(-2,19,36) rot=(0,1,0;1.5708rad)
  Radius = 14.3
FEATURE [Part::MultiFuse] Fusion089  label="removeToCreteHoleForPlugHousing035"
  Shapes = -> [Box026,Cylinder041]
FEATURE [Part::Cylinder] Cylinder042
  Angle = 360
  AttacherType = Attacher::AttachEngine3D
  Height = 20
  Placement = pos=(0,0,36.15) rot=(0,0,1;0rad)
  Radius = 14.3
FEATURE [Part::Cylinder] Cylinder043
  Angle = 360
  AttacherType = Attacher::AttachEngine3D
  Height = 10
  Placement = pos=(0,0,36.15) rot=(0,0,1;0rad)
  Radius = 4
FEATURE [Part::Box] Box027  label="removeToCreteHoleForPlugHousing036"
  AttacherType = Attacher::AttachEngine3D
  Height = 28.6
  Length = 20
  Placement = pos=(106.15,0,21.7) rot=(0,0,1;0rad)
  Width = 19
FEATURE [Part::Cut] Cut041  label="top022"
  Base = -> Cut040
  Tool = -> Fusion087
FEATURE [Part::Cut] Cut039  label="top020"
  Base = -> Cut041
  Tool = -> Fusion089
FEATURE [Part::MultiFuse] Fusion090  label="removeToCreteHoleForPlugHousing037"
  Placement = pos=(70,19,36) rot=(0,1,0;1.5708rad)
  Shapes = -> [Cylinder042,Cylinder043]
FEATURE [Part::MultiFuse] Fusion088  label="removeToCreteHoleForPlugHousing033"
  Shapes = -> [Box027,Fusion090]
FEATURE [Part::Cut] Cut042  label="removeToCreteHoleForPlugHousing038"
  Base = -> Cut039
  Tool = -> Fusion088
FEATURE [Part::MultiFuse] Fusion091  label="removeFromTop"
  Shapes = -> [Fillet038,Fusion085,Fusion084,Fusion083,Extrude045]
FEATURE [Part::Cut] Cut043  label="REAL TOP ====="
  Base = -> Fillet036
  Tool = -> Fusion091
FEATURE [Part::MultiFuse] Fusion092  label="caseScrewPillarBracket016"
  Shapes = -> [Extrude030,Extrude031,Extrude032,Extrude033,Extrude034,Extrude035,Extrude036,Extrude037,Box013,Box014]
FEATURE [Sketcher::SketchObject] Sketch058  label="topSketch015"
  FullyConstrained = true
  sketch-geometry (20):
    g0: LineSegment StartX=5.21097e-06 StartY=3 StartZ=0 EndX=5.21097e-06 EndY=19 EndZ=0
    g1: ArcOfCircle CenterX=19 CenterY=19 CenterZ=0 NormalX=0 NormalY=0 NormalZ=1 AngleXU=0 Radius=19 StartAngle=1.5708 EndAngle=3.14159
    g2: ArcOfCircle CenterX=19 CenterY=19 CenterZ=0 NormalX=0 NormalY=0 NormalZ=1 AngleXU=0 Radius=16 StartAngle=1.5708 EndAngle=3.14159
    g3: LineSegment StartX=114 StartY=35 StartZ=0 EndX=19 EndY=35 EndZ=0
    g4: LineSegment StartX=5.21097e-06 StartY=3 StartZ=0 EndX=5.21097e-06 EndY=0 EndZ=0
    g5: LineSegment StartX=3 StartY=0 StartZ=0 EndX=5.21097e-06 EndY=0 EndZ=0
    g6: LineSegment StartX=3 StartY=19 StartZ=0 EndX=3 EndY=0 EndZ=0
    g7: LineSegment StartX=19 StartY=38 StartZ=0 EndX=124 EndY=38 EndZ=0
    g8: Circle CenterX=119 CenterY=35 CenterZ=0 NormalX=0 NormalY=0 NormalZ=1 AngleXU=0 Radius=1
    g9: Circle CenterX=121 CenterY=35 CenterZ=0 NormalX=0 NormalY=0 NormalZ=1 AngleXU=0 Radius=1
    g10: Circle CenterX=121 CenterY=33 CenterZ=0 NormalX=0 NormalY=0 NormalZ=1 AngleXU=0 Radius=1
    g11: BSplineCurve PolesCount=3 KnotsCount=2 Degree=2 IsPeriodic=0
    g12: GeomPoint X=119 Y=35 Z=0
    g13: GeomPoint X=121 Y=33 Z=0
    g14: LineSegment StartX=119 StartY=35 StartZ=0 EndX=114 EndY=35 EndZ=0
    g15: ArcOfCircle CenterX=105 CenterY=19 CenterZ=0 NormalX=0 NormalY=0 NormalZ=1 AngleXU=0 Radius=19 StartAngle=5.7297 EndAngle=6.28319
    g16: ArcOfCircle CenterX=105 CenterY=19 CenterZ=0 NormalX=0 NormalY=0 NormalZ=1 AngleXU=0 Radius=16 StartAngle=5.60905 EndAngle=6.28319
    g17: LineSegment StartX=121 StartY=33 StartZ=0 EndX=121 EndY=19 EndZ=0
    g18: LineSegment StartX=124 StartY=38 StartZ=0 EndX=124 EndY=19 EndZ=0
    g19: LineSegment StartX=117.5 StartY=9.01251 StartZ=0 EndX=121.163 EndY=9.0125 EndZ=0
  constraints (46):
    c: Vertical(g0)
    c: Block(g0)
    c: Coincident(g1,g0)
    c: Block(g1)
    c: Coincident(g2,g1)
    c: Block(g2)
    c: Coincident(g3,g2)
    c: Horizontal(g3)
    c: Tangent(g3,g2)
    c: Coincident(g4,g0)
    c: Distance(g4) = 3
    c: Vertical(g4)
    c: Coincident(g5,g4)
    c: Horizontal(g5)
    c: Coincident(g6,g2)
    c: Coincident(g6,g5)
    c: Vertical(g6)
    c: Horizontal(g7)
    c: Distance(g7) = 105
    c: Coincident(g7,g1)
    c: Block(g3)
    c: Weight(g8) = 1
    c: Equal(g8,g9)
    c: Equal(g8,g10)
    c: InternalAlignment(g8,g11)
    c: InternalAlignment(g9,g11)
    c: InternalAlignment(g10,g11)
    c: InternalAlignment(g12,g11)
    c: InternalAlignment(g13,g11)
    c: Block(g11)
    c: Coincident(g14,g11)
    c: Coincident(g14,g3)
    c: Horizontal(g14)
    c: Block(g15)
    c: Coincident(g16,g15)
    c: Block(g16)
    c: Coincident(g17,g11)
    c: Coincident(g17,g16)
    c: Vertical(g17)
    c: Distance(g17) = 14
    c: Coincident(g18,g7)
    c: Coincident(g18,g15)
    c: Vertical(g18)
    c: Distance(g18) = 19
    c: Coincident(g19,g16)
    c: Coincident(g19,g15)
FEATURE [Part::Extrusion] Extrude049  label="top023"
  Base = -> Sketch058
  Dir = (0,0,1)
  DirMode = 2
  FaceMakerClass = Part::FaceMakerBullseye
  LengthFwd = 72
  LengthRev = 0
  Solid = true
  Symmetric = false
FEATURE [Sketcher::SketchObject] Sketch059
  FullyConstrained = true
  MapMode = 3
  Placement = pos=(0,0,0) rot=(1,0,0;1.5708rad)
  Support = -> [Extrude049]
  sketch-geometry (8):
    g0: Circle CenterX=80.351 CenterY=-67.6202 CenterZ=0 NormalX=0 NormalY=0 NormalZ=1 AngleXU=0 Radius=2
    g1: Circle CenterX=80.351 CenterY=-67.6202 CenterZ=0 NormalX=0 NormalY=0 NormalZ=1 AngleXU=0 Radius=3
    g2: Circle CenterX=80.351 CenterY=-4.92017 CenterZ=0 NormalX=0 NormalY=0 NormalZ=1 AngleXU=0 Radius=2
    g3: Circle CenterX=80.351 CenterY=-4.92017 CenterZ=0 NormalX=0 NormalY=0 NormalZ=1 AngleXU=0 Radius=3
    g4: Circle CenterX=23.851 CenterY=-4.92017 CenterZ=0 NormalX=0 NormalY=0 NormalZ=1 AngleXU=0 Radius=2
    g5: Circle CenterX=23.851 CenterY=-4.92017 CenterZ=0 NormalX=0 NormalY=0 NormalZ=1 AngleXU=0 Radius=3
    g6: Circle CenterX=23.851 CenterY=-67.6202 CenterZ=0 NormalX=0 NormalY=0 NormalZ=1 AngleXU=0 Radius=2
    g7: Circle CenterX=23.851 CenterY=-67.6202 CenterZ=0 NormalX=0 NormalY=0 NormalZ=1 AngleXU=0 Radius=3
  constraints (8):
    c: Block(g3)
    c: Block(g2)
    c: Block(g1)
    c: Block(g0)
    c: Block(g6)
    c: Block(g7)
    c: Block(g4)
    c: Block(g5)
FEATURE [Sketcher::SketchObject] Sketch060
  FullyConstrained = true
  MapMode = 3
  Placement = pos=(0,0,0) rot=(1,0,0;1.5708rad)
  Support = -> [Extrude049]
  sketch-geometry (8):
    g0: Circle CenterX=80.351 CenterY=-67.6202 CenterZ=0 NormalX=0 NormalY=0 NormalZ=1 AngleXU=0 Radius=3
    g1: Circle CenterX=80.351 CenterY=-4.92017 CenterZ=0 NormalX=0 NormalY=0 NormalZ=1 AngleXU=0 Radius=3
    g2: Circle CenterX=23.851 CenterY=-4.92017 CenterZ=0 NormalX=0 NormalY=0 NormalZ=1 AngleXU=0 Radius=3
    g3: Circle CenterX=23.851 CenterY=-67.6202 CenterZ=0 NormalX=0 NormalY=0 NormalZ=1 AngleXU=0 Radius=3
    g4: Circle CenterX=23.851 CenterY=-67.6202 CenterZ=0 NormalX=0 NormalY=0 NormalZ=1 AngleXU=0 Radius=5
    g5: Circle CenterX=80.351 CenterY=-67.6202 CenterZ=0 NormalX=0 NormalY=0 NormalZ=1 AngleXU=0 Radius=5
    g6: Circle CenterX=23.851 CenterY=-4.92017 CenterZ=0 NormalX=0 NormalY=0 NormalZ=1 AngleXU=0 Radius=5
    g7: Circle CenterX=80.351 CenterY=-4.92017 CenterZ=0 NormalX=0 NormalY=0 NormalZ=1 AngleXU=0 Radius=5
  constraints (8):
    c: Block(g1)
    c: Block(g0)
    c: Block(g3)
    c: Block(g2)
    c: Block(g5)
    c: Block(g4)
    c: Block(g6)
    c: Block(g7)
FEATURE [Sketcher::SketchObject] Sketch061
  FullyConstrained = true
  MapMode = 3
  Placement = pos=(0,0,0) rot=(1,0,0;1.5708rad)
  sketch-geometry (8):
    g0: Circle CenterX=80.351 CenterY=-67.6202 CenterZ=0 NormalX=0 NormalY=0 NormalZ=1 AngleXU=0 Radius=3
    g1: Circle CenterX=80.351 CenterY=-4.92017 CenterZ=0 NormalX=0 NormalY=0 NormalZ=1 AngleXU=0 Radius=3
    g2: Circle CenterX=23.851 CenterY=-4.92017 CenterZ=0 NormalX=0 NormalY=0 NormalZ=1 AngleXU=0 Radius=3
    g3: Circle CenterX=23.851 CenterY=-67.6202 CenterZ=0 NormalX=0 NormalY=0 NormalZ=1 AngleXU=0 Radius=3
    g4: Circle CenterX=23.851 CenterY=-67.6202 CenterZ=0 NormalX=0 NormalY=0 NormalZ=1 AngleXU=0 Radius=5
    g5: Circle CenterX=80.351 CenterY=-67.6202 CenterZ=0 NormalX=0 NormalY=0 NormalZ=1 AngleXU=0 Radius=5
    g6: Circle CenterX=23.851 CenterY=-4.92017 CenterZ=0 NormalX=0 NormalY=0 NormalZ=1 AngleXU=0 Radius=5
    g7: Circle CenterX=80.351 CenterY=-4.92017 CenterZ=0 NormalX=0 NormalY=0 NormalZ=1 AngleXU=0 Radius=5
  constraints (8):
    c: Block(g1)
    c: Block(g0)
    c: Block(g3)
    c: Block(g2)
    c: Block(g5)
    c: Block(g4)
    c: Block(g6)
    c: Block(g7)
FEATURE [Sketcher::SketchObject] Sketch062  label="topSketch016"
  FullyConstrained = true
  sketch-geometry (20):
    g0: LineSegment StartX=5.21097e-06 StartY=3 StartZ=0 EndX=5.21097e-06 EndY=19 EndZ=0
    g1: ArcOfCircle CenterX=19 CenterY=19 CenterZ=0 NormalX=0 NormalY=0 NormalZ=1 AngleXU=0 Radius=19 StartAngle=1.5708 EndAngle=3.14159
    g2: ArcOfCircle CenterX=19 CenterY=19 CenterZ=0 NormalX=0 NormalY=0 NormalZ=1 AngleXU=0 Radius=16 StartAngle=1.5708 EndAngle=3.14159
    g3: LineSegment StartX=114 StartY=35 StartZ=0 EndX=19 EndY=35 EndZ=0
    g4: LineSegment StartX=5.21097e-06 StartY=3 StartZ=0 EndX=5.21097e-06 EndY=0 EndZ=0
    g5: LineSegment StartX=3 StartY=0 StartZ=0 EndX=5.21097e-06 EndY=0 EndZ=0
    g6: LineSegment StartX=3 StartY=19 StartZ=0 EndX=3 EndY=0 EndZ=0
    g7: LineSegment StartX=19 StartY=38 StartZ=0 EndX=124 EndY=38 EndZ=0
    g8: Circle CenterX=119 CenterY=35 CenterZ=0 NormalX=0 NormalY=0 NormalZ=1 AngleXU=0 Radius=1
    g9: Circle CenterX=121 CenterY=35 CenterZ=0 NormalX=0 NormalY=0 NormalZ=1 AngleXU=0 Radius=1
    g10: Circle CenterX=121 CenterY=33 CenterZ=0 NormalX=0 NormalY=0 NormalZ=1 AngleXU=0 Radius=1
    g11: BSplineCurve PolesCount=3 KnotsCount=2 Degree=2 IsPeriodic=0
    g12: GeomPoint X=119 Y=35 Z=0
    g13: GeomPoint X=121 Y=33 Z=0
    g14: LineSegment StartX=119 StartY=35 StartZ=0 EndX=114 EndY=35 EndZ=0
    g15: ArcOfCircle CenterX=105 CenterY=19 CenterZ=0 NormalX=0 NormalY=0 NormalZ=1 AngleXU=0 Radius=19 StartAngle=5.7297 EndAngle=6.28319
    g16: ArcOfCircle CenterX=105 CenterY=19 CenterZ=0 NormalX=0 NormalY=0 NormalZ=1 AngleXU=0 Radius=16 StartAngle=5.60905 EndAngle=6.28319
    g17: LineSegment StartX=121 StartY=33 StartZ=0 EndX=121 EndY=19 EndZ=0
    g18: LineSegment StartX=124 StartY=38 StartZ=0 EndX=124 EndY=19 EndZ=0
    g19: LineSegment StartX=117.5 StartY=9.01251 StartZ=0 EndX=121.163 EndY=9.0125 EndZ=0
  constraints (46):
    c: Vertical(g0)
    c: Block(g0)
    c: Coincident(g1,g0)
    c: Block(g1)
    c: Coincident(g2,g1)
    c: Block(g2)
    c: Coincident(g3,g2)
    c: Horizontal(g3)
    c: Tangent(g3,g2)
    c: Coincident(g4,g0)
    c: Distance(g4) = 3
    c: Vertical(g4)
    c: Coincident(g5,g4)
    c: Horizontal(g5)
    c: Coincident(g6,g2)
    c: Coincident(g6,g5)
    c: Vertical(g6)
    c: Horizontal(g7)
    c: Distance(g7) = 105
    c: Coincident(g7,g1)
    c: Block(g3)
    c: Weight(g8) = 1
    c: Equal(g8,g9)
    c: Equal(g8,g10)
    c: InternalAlignment(g8,g11)
    c: InternalAlignment(g9,g11)
    c: InternalAlignment(g10,g11)
    c: InternalAlignment(g12,g11)
    c: InternalAlignment(g13,g11)
    c: Block(g11)
    c: Coincident(g14,g11)
    c: Coincident(g14,g3)
    c: Horizontal(g14)
    c: Block(g15)
    c: Coincident(g16,g15)
    c: Block(g16)
    c: Coincident(g17,g11)
    c: Coincident(g17,g16)
    c: Vertical(g17)
    c: Distance(g17) = 14
    c: Coincident(g18,g7)
    c: Coincident(g18,g15)
    c: Vertical(g18)
    c: Distance(g18) = 19
    c: Coincident(g19,g16)
    c: Coincident(g19,g15)
FEATURE [Part::Extrusion] Extrude053  label="top024"
  Base = -> Sketch062
  Dir = (0,0,1)
  DirMode = 2
  FaceMakerClass = Part::FaceMakerBullseye
  LengthFwd = 72
  LengthRev = 0
  Solid = true
  Symmetric = false
FEATURE [Sketcher::SketchObject] Sketch063
  FullyConstrained = true
  MapMode = 3
  Placement = pos=(0,0,0) rot=(1,0,0;1.5708rad)
  Support = -> [Extrude053]
  sketch-geometry (8):
    g0: Circle CenterX=80.351 CenterY=-67.6202 CenterZ=0 NormalX=0 NormalY=0 NormalZ=1 AngleXU=0 Radius=2
    g1: Circle CenterX=80.351 CenterY=-67.6202 CenterZ=0 NormalX=0 NormalY=0 NormalZ=1 AngleXU=0 Radius=3
    g2: Circle CenterX=80.351 CenterY=-4.92017 CenterZ=0 NormalX=0 NormalY=0 NormalZ=1 AngleXU=0 Radius=2
    g3: Circle CenterX=80.351 CenterY=-4.92017 CenterZ=0 NormalX=0 NormalY=0 NormalZ=1 AngleXU=0 Radius=3
    g4: Circle CenterX=23.851 CenterY=-4.92017 CenterZ=0 NormalX=0 NormalY=0 NormalZ=1 AngleXU=0 Radius=2
    g5: Circle CenterX=23.851 CenterY=-4.92017 CenterZ=0 NormalX=0 NormalY=0 NormalZ=1 AngleXU=0 Radius=3
    g6: Circle CenterX=23.851 CenterY=-67.6202 CenterZ=0 NormalX=0 NormalY=0 NormalZ=1 AngleXU=0 Radius=2
    g7: Circle CenterX=23.851 CenterY=-67.6202 CenterZ=0 NormalX=0 NormalY=0 NormalZ=1 AngleXU=0 Radius=3
  constraints (8):
    c: Block(g3)
    c: Block(g2)
    c: Block(g1)
    c: Block(g0)
    c: Block(g6)
    c: Block(g7)
    c: Block(g4)
    c: Block(g5)
FEATURE [Part::Extrusion] Extrude054
  Base = -> Sketch063
  Dir = (0,-1,2e-16)
  DirMode = 2
  FaceMakerClass = Part::FaceMakerBullseye
  LengthFwd = 6
  LengthRev = 0
  Placement = pos=(0,9,0) rot=(0,0,1;0rad)
  Solid = true
  Symmetric = false
FEATURE [Sketcher::SketchObject] Sketch064  label="topSketch017"
  FullyConstrained = true
  sketch-geometry (20):
    g0: LineSegment StartX=5.21097e-06 StartY=3 StartZ=0 EndX=5.21097e-06 EndY=19 EndZ=0
    g1: ArcOfCircle CenterX=19 CenterY=19 CenterZ=0 NormalX=0 NormalY=0 NormalZ=1 AngleXU=0 Radius=19 StartAngle=1.5708 EndAngle=3.14159
    g2: ArcOfCircle CenterX=19 CenterY=19 CenterZ=0 NormalX=0 NormalY=0 NormalZ=1 AngleXU=0 Radius=16 StartAngle=1.5708 EndAngle=3.14159
    g3: LineSegment StartX=114 StartY=35 StartZ=0 EndX=19 EndY=35 EndZ=0
    g4: LineSegment StartX=5.21097e-06 StartY=3 StartZ=0 EndX=5.21097e-06 EndY=0 EndZ=0
    g5: LineSegment StartX=3 StartY=0 StartZ=0 EndX=5.21097e-06 EndY=0 EndZ=0
    g6: LineSegment StartX=3 StartY=19 StartZ=0 EndX=3 EndY=0 EndZ=0
    g7: LineSegment StartX=19 StartY=38 StartZ=0 EndX=124 EndY=38 EndZ=0
    g8: Circle CenterX=119 CenterY=35 CenterZ=0 NormalX=0 NormalY=0 NormalZ=1 AngleXU=0 Radius=1
    g9: Circle CenterX=121 CenterY=35 CenterZ=0 NormalX=0 NormalY=0 NormalZ=1 AngleXU=0 Radius=1
    g10: Circle CenterX=121 CenterY=33 CenterZ=0 NormalX=0 NormalY=0 NormalZ=1 AngleXU=0 Radius=1
    g11: BSplineCurve PolesCount=3 KnotsCount=2 Degree=2 IsPeriodic=0
    g12: GeomPoint X=119 Y=35 Z=0
    g13: GeomPoint X=121 Y=33 Z=0
    g14: LineSegment StartX=119 StartY=35 StartZ=0 EndX=114 EndY=35 EndZ=0
    g15: ArcOfCircle CenterX=105 CenterY=19 CenterZ=0 NormalX=0 NormalY=0 NormalZ=1 AngleXU=0 Radius=19 StartAngle=5.7297 EndAngle=6.28319
    g16: ArcOfCircle CenterX=105 CenterY=19 CenterZ=0 NormalX=0 NormalY=0 NormalZ=1 AngleXU=0 Radius=16 StartAngle=5.60905 EndAngle=6.28319
    g17: LineSegment StartX=121 StartY=33 StartZ=0 EndX=121 EndY=19 EndZ=0
    g18: LineSegment StartX=124 StartY=38 StartZ=0 EndX=124 EndY=19 EndZ=0
    g19: LineSegment StartX=117.5 StartY=9.01251 StartZ=0 EndX=121.163 EndY=9.0125 EndZ=0
  constraints (46):
    c: Vertical(g0)
    c: Block(g0)
    c: Coincident(g1,g0)
    c: Block(g1)
    c: Coincident(g2,g1)
    c: Block(g2)
    c: Coincident(g3,g2)
    c: Horizontal(g3)
    c: Tangent(g3,g2)
    c: Coincident(g4,g0)
    c: Distance(g4) = 3
    c: Vertical(g4)
    c: Coincident(g5,g4)
    c: Horizontal(g5)
    c: Coincident(g6,g2)
    c: Coincident(g6,g5)
    c: Vertical(g6)
    c: Horizontal(g7)
    c: Distance(g7) = 105
    c: Coincident(g7,g1)
    c: Block(g3)
    c: Weight(g8) = 1
    c: Equal(g8,g9)
    c: Equal(g8,g10)
    c: InternalAlignment(g8,g11)
    c: InternalAlignment(g9,g11)
    c: InternalAlignment(g10,g11)
    c: InternalAlignment(g12,g11)
    c: InternalAlignment(g13,g11)
    c: Block(g11)
    c: Coincident(g14,g11)
    c: Coincident(g14,g3)
    c: Horizontal(g14)
    c: Block(g15)
    c: Coincident(g16,g15)
    c: Block(g16)
    c: Coincident(g17,g11)
    c: Coincident(g17,g16)
    c: Vertical(g17)
    c: Distance(g17) = 14
    c: Coincident(g18,g7)
    c: Coincident(g18,g15)
    c: Vertical(g18)
    c: Distance(g18) = 19
    c: Coincident(g19,g16)
    c: Coincident(g19,g15)
FEATURE [Sketcher::SketchObject] Sketch065
  FullyConstrained = true
  MapMode = 3
  Placement = pos=(0,0,0) rot=(1,0,0;1.5708rad)
  sketch-geometry (8):
    g0: Circle CenterX=80.351 CenterY=-67.6202 CenterZ=0 NormalX=0 NormalY=0 NormalZ=1 AngleXU=0 Radius=3
    g1: Circle CenterX=80.351 CenterY=-4.92017 CenterZ=0 NormalX=0 NormalY=0 NormalZ=1 AngleXU=0 Radius=3
    g2: Circle CenterX=23.851 CenterY=-4.92017 CenterZ=0 NormalX=0 NormalY=0 NormalZ=1 AngleXU=0 Radius=3
    g3: Circle CenterX=23.851 CenterY=-67.6202 CenterZ=0 NormalX=0 NormalY=0 NormalZ=1 AngleXU=0 Radius=3
    g4: Circle CenterX=23.851 CenterY=-67.6202 CenterZ=0 NormalX=0 NormalY=0 NormalZ=1 AngleXU=0 Radius=5
    g5: Circle CenterX=80.351 CenterY=-67.6202 CenterZ=0 NormalX=0 NormalY=0 NormalZ=1 AngleXU=0 Radius=5
    g6: Circle CenterX=23.851 CenterY=-4.92017 CenterZ=0 NormalX=0 NormalY=0 NormalZ=1 AngleXU=0 Radius=5
    g7: Circle CenterX=80.351 CenterY=-4.92017 CenterZ=0 NormalX=0 NormalY=0 NormalZ=1 AngleXU=0 Radius=5
  constraints (8):
    c: Block(g1)
    c: Block(g0)
    c: Block(g3)
    c: Block(g2)
    c: Block(g5)
    c: Block(g4)
    c: Block(g6)
    c: Block(g7)
FEATURE [Part::Extrusion] Extrude056
  Base = -> Sketch065
  Dir = (0,-1,2e-16)
  DirMode = 2
  FaceMakerClass = Part::FaceMakerBullseye
  LengthFwd = 2
  LengthRev = 0
  Solid = true
  Symmetric = false
FEATURE [Part::Extrusion] Extrude057  label="top025"
  Base = -> Sketch064
  Dir = (0,0,1)
  DirMode = 2
  FaceMakerClass = Part::FaceMakerBullseye
  LengthFwd = 72
  LengthRev = 0
  Solid = true
  Symmetric = false
FEATURE [Sketcher::SketchObject] Sketch066
  FullyConstrained = true
  MapMode = 3
  Placement = pos=(0,0,0) rot=(1,0,0;1.5708rad)
  Support = -> [Extrude057]
  sketch-geometry (8):
    g0: Circle CenterX=80.351 CenterY=-67.6202 CenterZ=0 NormalX=0 NormalY=0 NormalZ=1 AngleXU=0 Radius=3
    g1: Circle CenterX=80.351 CenterY=-4.92017 CenterZ=0 NormalX=0 NormalY=0 NormalZ=1 AngleXU=0 Radius=3
    g2: Circle CenterX=23.851 CenterY=-4.92017 CenterZ=0 NormalX=0 NormalY=0 NormalZ=1 AngleXU=0 Radius=3
    g3: Circle CenterX=23.851 CenterY=-67.6202 CenterZ=0 NormalX=0 NormalY=0 NormalZ=1 AngleXU=0 Radius=3
    g4: Circle CenterX=23.851 CenterY=-67.6202 CenterZ=0 NormalX=0 NormalY=0 NormalZ=1 AngleXU=0 Radius=5
    g5: Circle CenterX=80.351 CenterY=-67.6202 CenterZ=0 NormalX=0 NormalY=0 NormalZ=1 AngleXU=0 Radius=5
    g6: Circle CenterX=23.851 CenterY=-4.92017 CenterZ=0 NormalX=0 NormalY=0 NormalZ=1 AngleXU=0 Radius=5
    g7: Circle CenterX=80.351 CenterY=-4.92017 CenterZ=0 NormalX=0 NormalY=0 NormalZ=1 AngleXU=0 Radius=5
  constraints (8):
    c: Block(g1)
    c: Block(g0)
    c: Block(g3)
    c: Block(g2)
    c: Block(g5)
    c: Block(g4)
    c: Block(g6)
    c: Block(g7)
FEATURE [Part::Extrusion] Extrude055
  Base = -> Sketch066
  Dir = (0,-1,2e-16)
  DirMode = 2
  FaceMakerClass = Part::FaceMakerBullseye
  LengthFwd = 2
  LengthRev = 0
  Solid = true
  Symmetric = false
FEATURE [Part::Fillet] Fillet041
  Base = -> Extrude056
  Edges = 4 edges r=1.99: [Edge6,Edge12,Edge18,Edge24]
FEATURE [Part::Cut] Cut045
  Base = -> Extrude055
  Placement = pos=(0,6,0) rot=(0,0,1;0rad)
  Tool = -> Fillet041
FEATURE [Part::MultiFuse] Fusion095  label="pcbScrewPillars"
  Placement = pos=(-3.2,-1,72.3) rot=(0,0,1;0rad)
  Shapes = -> [Cut045,Extrude054]
FEATURE [Part::Feature] Face113
  shape: bbox 3.2 x 1.5 x 2e-07 mm, 1 faces, 0 solids (baked)
FEATURE [Part::Revolution] Revolve121  label="backCaseScrewRetainer002"
  Angle = 360
  Axis = (0,1,0)
  Base = (0,0,0)
  FaceMakerClass = Part::FaceMakerBullseye
  Placement = pos=(12.5,3,62) rot=(0,0,1;0rad)
  Solid = false
  Source = -> Face113
  Symmetric = false
FEATURE [Part::Feature] Face114
  shape: bbox 3.2 x 1.5 x 2e-07 mm, 1 faces, 0 solids (baked)
FEATURE [Part::Feature] Face115
  shape: bbox 3.2 x 1.5 x 2e-07 mm, 1 faces, 0 solids (baked)
FEATURE [Part::Feature] Face116
  shape: bbox 3.2 x 1.5 x 2e-07 mm, 1 faces, 0 solids (baked)
FEATURE [Part::Revolution] Revolve122  label="frontCaseScrewRetainer004"
  Angle = 360
  Axis = (0,1,0)
  Base = (0,0,0)
  FaceMakerClass = Part::FaceMakerBullseye
  Placement = pos=(89.5,3,68.5) rot=(0,0,1;0rad)
  Solid = false
  Source = -> Face115
  Symmetric = false
FEATURE [Part::Revolution] Revolve123  label="frontCaseScrewRetainer005"
  Angle = 360
  Axis = (0,1,0)
  Base = (0,0,0)
  FaceMakerClass = Part::FaceMakerBullseye
  Placement = pos=(89.5,3,3.5) rot=(0,0,1;0rad)
  Solid = false
  Source = -> Face116
  Symmetric = false
FEATURE [Part::Revolution] Revolve124  label="backCaseScrewRetainer003"
  Angle = 360
  Axis = (0,1,0)
  Base = (0,0,0)
  FaceMakerClass = Part::FaceMakerBullseye
  Placement = pos=(12.5,3,10) rot=(0,0,1;0rad)
  Solid = false
  Source = -> Face114
  Symmetric = false
FEATURE [Part::Feature] Face117
  shape: bbox 3.6 x 3.2 x 2e-07 mm, 1 faces, 0 solids (baked)
FEATURE [Part::Revolution] Revolve125  label="moreFrontCaseScrewRetainer004"
  Angle = 360
  Axis = (0,1,0)
  Base = (0,0,0)
  FaceMakerClass = Part::FaceMakerBullseye
  Placement = pos=(109.5,4.5,68.5) rot=(0,0,1;0rad)
  Solid = false
  Source = -> Face117
  Symmetric = false
FEATURE [Part::Feature] Face118
  shape: bbox 3.6 x 3.2 x 2e-07 mm, 1 faces, 0 solids (baked)
FEATURE [Part::Revolution] Revolve126  label="moreFrontCaseScrewRetainer005"
  Angle = 360
  Axis = (0,1,0)
  Base = (0,0,0)
  FaceMakerClass = Part::FaceMakerBullseye
  Placement = pos=(109.5,4.5,3.5) rot=(0,0,1;0rad)
  Solid = false
  Source = -> Face118
  Symmetric = false
FEATURE [Part::MultiFuse] Fusion096  label="screwRetainers001"
  Shapes = -> [Revolve126,Revolve125,Revolve124,Revolve123,Revolve122,Revolve121]
FEATURE [Part::Feature] Face119
  shape: bbox 10 x 16.5 x 2e-07 mm, 1 faces, 0 solids (baked)
FEATURE [Part::Revolution] Revolve130  label="plugHousing050"
  Angle = 360
  Axis = (0,1,0)
  Base = (0,0,0)
  FaceMakerClass = Part::FaceMakerBullseye
  Placement = pos=(0,0,36.15) rot=(0,0,1;0rad)
  Solid = false
  Source = -> Face119
  Symmetric = false
FEATURE [Part::Feature] Face120
  shape: bbox 10 x 16.5 x 2e-07 mm, 1 faces, 0 solids (baked)
FEATURE [Part::Feature] Face121
  shape: bbox 10 x 16.5 x 2e-07 mm, 1 faces, 0 solids (baked)
FEATURE [Part::Revolution] Revolve127  label="plugHousing047"
  Angle = 360
  Axis = (0,1,0)
  Base = (0,0,0)
  FaceMakerClass = Part::FaceMakerBullseye
  Placement = pos=(0,0,36.15) rot=(0,0,1;0rad)
  Solid = false
  Source = -> Face121
  Symmetric = false
FEATURE [Part::Feature] Face122
  shape: bbox 10 x 16.5 x 2e-07 mm, 1 faces, 0 solids (baked)
FEATURE [Part::Feature] Face123
  shape: bbox 10 x 16.5 x 2e-07 mm, 1 faces, 0 solids (baked)
FEATURE [Part::Revolution] Revolve128  label="plugHousing048"
  Angle = 360
  Axis = (0,1,0)
  Base = (0,0,0)
  FaceMakerClass = Part::FaceMakerBullseye
  Placement = pos=(0,0,36.15) rot=(0,0,1;0rad)
  Solid = false
  Source = -> Face123
  Symmetric = false
FEATURE [Part::MultiFuse] Fusion100  label="plugHousing054"
  Placement = pos=(0,0,0) rot=(0,0,1;1.5708rad)
  Shapes = -> [Revolve130,Revolve128]
FEATURE [Part::Feature] Face124
  shape: bbox 10 x 16.5 x 2e-07 mm, 1 faces, 0 solids (baked)
FEATURE [Part::Feature] Face125
  shape: bbox 10 x 16.5 x 2e-07 mm, 1 faces, 0 solids (baked)
FEATURE [Part::Revolution] Revolve129  label="plugHousing049"
  Angle = 360
  Axis = (0,1,0)
  Base = (0,0,0)
  FaceMakerClass = Part::FaceMakerBullseye
  Placement = pos=(0,0,36.15) rot=(0,0,1;0rad)
  Solid = false
  Source = -> Face125
  Symmetric = false
FEATURE [Part::Feature] Face126
  shape: bbox 10 x 16.5 x 2e-07 mm, 1 faces, 0 solids (baked)
FEATURE [Part::Revolution] Revolve131  label="plugHousing058"
  Angle = 360
  Axis = (0,1,0)
  Base = (0,0,0)
  FaceMakerClass = Part::FaceMakerBullseye
  Placement = pos=(0,0,36.15) rot=(0,0,1;0rad)
  Solid = false
  Source = -> Face120
  Symmetric = false
FEATURE [Part::MultiFuse] Fusion099  label="plugHousing053"
  Placement = pos=(0,0,0) rot=(0,0,1;1.5708rad)
  Shapes = -> [Revolve127,Revolve131]
FEATURE [Part::MultiFuse] Fusion102  label="plugHousing056"
  Placement = pos=(0,19,0) rot=(0,0,1;3.14159rad)
  Shapes = -> [Fusion100,Fusion099]
FEATURE [Part::Revolution] Revolve132  label="plugHousing059"
  Angle = 360
  Axis = (0,1,0)
  Base = (0,0,0)
  FaceMakerClass = Part::FaceMakerBullseye
  Placement = pos=(0,0,36.15) rot=(0,0,1;0rad)
  Solid = false
  Source = -> Face126
  Symmetric = false
FEATURE [Part::Revolution] Revolve133  label="plugHousing060"
  Angle = 360
  Axis = (0,1,0)
  Base = (0,0,0)
  FaceMakerClass = Part::FaceMakerBullseye
  Placement = pos=(0,0,36.15) rot=(0,0,1;0rad)
  Solid = false
  Source = -> Face122
  Symmetric = false
FEATURE [Part::MultiFuse] Fusion097  label="plugHousing051"
  Placement = pos=(0,0,0) rot=(0,0,1;1.5708rad)
  Shapes = -> [Revolve133,Revolve132]
FEATURE [Part::Revolution] Revolve134  label="plugHousing061"
  Angle = 360
  Axis = (0,1,0)
  Base = (0,0,0)
  FaceMakerClass = Part::FaceMakerBullseye
  Placement = pos=(0,0,36.15) rot=(0,0,1;0rad)
  Solid = false
  Source = -> Face124
  Symmetric = false
FEATURE [Part::MultiFuse] Fusion101  label="plugHousing055"
  Placement = pos=(0,0,0) rot=(0,0,1;1.5708rad)
  Shapes = -> [Revolve129,Revolve134]
FEATURE [Part::MultiFuse] Fusion098  label="plugHousing052"
  Placement = pos=(0,19,0) rot=(0,0,1;3.14159rad)
  Shapes = -> [Fusion097,Fusion101]
FEATURE [Part::MultiFuse] Fusion103  label="plugHousing057"
  Placement = pos=(122.621,0,-0.15) rot=(0,0,1;0rad)
  Shapes = -> [Fusion102,Fusion098]
FEATURE [Part::Box] Box028  label="Cube015"
  AttacherType = Attacher::AttachEngine3D
  Height = 28
  Length = 3
  Placement = pos=(110.7,19,22) rot=(0,0,1;0rad)
  Width = 15.7
FEATURE [Part::Cylinder] Cylinder044
  Angle = 360
  AttacherType = Attacher::AttachEngine3D
  Height = 20
  Placement = pos=(0,0,36.15) rot=(0,0,1;0rad)
  Radius = 10.3
FEATURE [Part::Cylinder] Cylinder045
  Angle = 360
  AttacherType = Attacher::AttachEngine3D
  Height = 10
  Placement = pos=(0,0,36.15) rot=(0,0,1;0rad)
  Radius = 4
FEATURE [Part::MultiFuse] Fusion104  label="removeToCreteHoleForPlugHousing040"
  Placement = pos=(70,19,36) rot=(0,1,0;1.5708rad)
  Shapes = -> [Cylinder044,Cylinder045]
FEATURE [Part::Cut] Cut046  label="plugHousingTab003"
  Base = -> Box028
  Tool = -> Fusion104
FEATURE [Part::MultiFuse] Fusion105  label="plugHousing062"
  Shapes = -> [Fusion103,Cut046]
FEATURE [Part::Fillet] Fillet042
  Base = -> Fusion105
  Edges = 1 edges r=2: [Edge25]
FEATURE [Part::Fillet] Fillet043  label="plugHousing063"
  Base = -> Fillet042
  Edges = 1 edges r=2: [Edge8]
  Placement = pos=(7,0,0) rot=(0,0,1;0rad)
FEATURE [Part::Feature] Face127
  shape: bbox 10 x 16.5 x 2e-07 mm, 1 faces, 0 solids (baked)
FEATURE [Part::Feature] Face128
  shape: bbox 10 x 16.5 x 2e-07 mm, 1 faces, 0 solids (baked)
FEATURE [Part::Revolution] Revolve137  label="plugHousing070"
  Angle = 360
  Axis = (0,1,0)
  Base = (0,0,0)
  FaceMakerClass = Part::FaceMakerBullseye
  Placement = pos=(0,0,36.15) rot=(0,0,1;0rad)
  Solid = false
  Source = -> Face127
  Symmetric = false
FEATURE [Part::Revolution] Revolve140  label="plugHousing073"
  Angle = 360
  Axis = (0,1,0)
  Base = (0,0,0)
  FaceMakerClass = Part::FaceMakerBullseye
  Placement = pos=(0,0,36.15) rot=(0,0,1;0rad)
  Solid = false
  Source = -> Face128
  Symmetric = false
FEATURE [Part::Feature] Face129
  shape: bbox 10 x 16.5 x 2e-07 mm, 1 faces, 0 solids (baked)
FEATURE [Part::Revolution] Revolve138  label="plugHousing071"
  Angle = 360
  Axis = (0,1,0)
  Base = (0,0,0)
  FaceMakerClass = Part::FaceMakerBullseye
  Placement = pos=(0,0,36.15) rot=(0,0,1;0rad)
  Solid = false
  Source = -> Face129
  Symmetric = false
FEATURE [Part::Feature] Face130
  shape: bbox 10 x 16.5 x 2e-07 mm, 1 faces, 0 solids (baked)
FEATURE [Part::Revolution] Revolve139  label="plugHousing072"
  Angle = 360
  Axis = (0,1,0)
  Base = (0,0,0)
  FaceMakerClass = Part::FaceMakerBullseye
  Placement = pos=(0,0,36.15) rot=(0,0,1;0rad)
  Solid = false
  Source = -> Face130
  Symmetric = false
FEATURE [Part::Feature] Face131
  shape: bbox 10 x 16.5 x 2e-07 mm, 1 faces, 0 solids (baked)
FEATURE [Part::Revolution] Revolve135  label="plugHousing068"
  Angle = 360
  Axis = (0,1,0)
  Base = (0,0,0)
  FaceMakerClass = Part::FaceMakerBullseye
  Placement = pos=(0,0,36.15) rot=(0,0,1;0rad)
  Solid = false
  Source = -> Face131
  Symmetric = false
FEATURE [Part::MultiFuse] Fusion112  label="plugHousing078"
  Placement = pos=(0,0,0) rot=(0,0,1;1.5708rad)
  Shapes = -> [Revolve135,Revolve139]
FEATURE [Part::Feature] Face132
  shape: bbox 10 x 16.5 x 2e-07 mm, 1 faces, 0 solids (baked)
FEATURE [Part::Revolution] Revolve141  label="plugHousing074"
  Angle = 360
  Axis = (0,1,0)
  Base = (0,0,0)
  FaceMakerClass = Part::FaceMakerBullseye
  Placement = pos=(0,0,36.15) rot=(0,0,1;0rad)
  Solid = false
  Source = -> Face132
  Symmetric = false
FEATURE [Part::MultiFuse] Fusion110  label="plugHousing076"
  Placement = pos=(0,0,0) rot=(0,0,1;1.5708rad)
  Shapes = -> [Revolve141,Revolve140]
FEATURE [Part::Feature] Face133
  shape: bbox 10 x 16.5 x 2e-07 mm, 1 faces, 0 solids (baked)
FEATURE [Part::Revolution] Revolve136  label="plugHousing069"
  Angle = 360
  Axis = (0,1,0)
  Base = (0,0,0)
  FaceMakerClass = Part::FaceMakerBullseye
  Placement = pos=(0,0,36.15) rot=(0,0,1;0rad)
  Solid = false
  Source = -> Face133
  Symmetric = false
FEATURE [Part::MultiFuse] Fusion106  label="plugHousing064"
  Placement = pos=(0,0,0) rot=(0,0,1;1.5708rad)
  Shapes = -> [Revolve138,Revolve136]
FEATURE [Part::MultiFuse] Fusion108  label="plugHousing066"
  Placement = pos=(0,19,0) rot=(0,0,1;3.14159rad)
  Shapes = -> [Fusion106,Fusion112]
FEATURE [Part::Feature] Face134
  shape: bbox 10 x 16.5 x 2e-07 mm, 1 faces, 0 solids (baked)
FEATURE [Part::Revolution] Revolve142  label="plugHousing075"
  Angle = 360
  Axis = (0,1,0)
  Base = (0,0,0)
  FaceMakerClass = Part::FaceMakerBullseye
  Placement = pos=(0,0,36.15) rot=(0,0,1;0rad)
  Solid = false
  Source = -> Face134
  Symmetric = false
FEATURE [Part::MultiFuse] Fusion107  label="plugHousing065"
  Placement = pos=(0,0,0) rot=(0,0,1;1.5708rad)
  Shapes = -> [Revolve137,Revolve142]
FEATURE [Part::MultiFuse] Fusion111  label="plugHousing077"
  Placement = pos=(0,19,0) rot=(0,0,1;3.14159rad)
  Shapes = -> [Fusion110,Fusion107]
FEATURE [Part::MultiFuse] Fusion109  label="plugHousing067"
  Placement = pos=(131.236,0,-0.15) rot=(0,0,1;0rad)
  Shapes = -> [Fusion108,Fusion111]
FEATURE [Part::MultiFuse] Fusion113  label="plugHousing079"
  Shapes = -> [Fillet043,Fusion109]
FEATURE [Part::Feature] Face135
  shape: bbox 3.5 x 17.8 x 2e-07 mm, 1 faces, 0 solids (baked)
FEATURE [Part::Revolution] Revolve143  label="removeToCreateScrewAndThreadedInsertHole049"
  Angle = 360
  Axis = (0,1,0)
  Base = (0,0,0)
  FaceMakerClass = Part::FaceMakerBullseye
  Placement = pos=(12.5,0,10) rot=(0,0,1;0rad)
  Solid = false
  Source = -> Face135
  Symmetric = false
FEATURE [Part::Feature] Face136
  shape: bbox 3.5 x 17.8 x 2e-07 mm, 1 faces, 0 solids (baked)
FEATURE [Part::Revolution] Revolve144  label="removeToCreateScrewAndThreadedInsertHole050"
  Angle = 360
  Axis = (0,1,0)
  Base = (0,0,0)
  FaceMakerClass = Part::FaceMakerBullseye
  Placement = pos=(12.5,0,62) rot=(0,0,1;0rad)
  Solid = false
  Source = -> Face136
  Symmetric = false
FEATURE [Part::Feature] Face137
  shape: bbox 3.5 x 17.8 x 2e-07 mm, 1 faces, 0 solids (baked)
FEATURE [Part::Revolution] Revolve145  label="removeToCreateScrewAndThreadedInsertHole051"
  Angle = 360
  Axis = (0,1,0)
  Base = (0,0,0)
  FaceMakerClass = Part::FaceMakerBullseye
  Placement = pos=(89.5,0,68.5) rot=(0,0,1;0rad)
  Solid = false
  Source = -> Face137
  Symmetric = false
FEATURE [Part::Feature] Face138
  shape: bbox 3.5 x 17.8 x 2e-07 mm, 1 faces, 0 solids (baked)
FEATURE [Part::Revolution] Revolve146  label="removeToCreateScrewAndThreadedInsertHole052"
  Angle = 360
  Axis = (0,1,0)
  Base = (0,0,0)
  FaceMakerClass = Part::FaceMakerBullseye
  Placement = pos=(89.5,0,3.5) rot=(0,0,1;0rad)
  Solid = false
  Source = -> Face138
  Symmetric = false
FEATURE [Part::Feature] Face139
  shape: bbox 3.5 x 17.8 x 2e-07 mm, 1 faces, 0 solids (baked)
FEATURE [Part::Revolution] Revolve147  label="removeToCreateScrewAndThreadedInsertHole053"
  Angle = 360
  Axis = (0,1,0)
  Base = (0,0,0)
  FaceMakerClass = Part::FaceMakerBullseye
  Placement = pos=(109.5,4.7,3.5) rot=(0,0,1;0rad)
  Solid = false
  Source = -> Face139
  Symmetric = false
FEATURE [Part::Feature] Face140
  shape: bbox 3.5 x 17.8 x 2e-07 mm, 1 faces, 0 solids (baked)
FEATURE [Part::Revolution] Revolve148  label="removeToCreateScrewAndThreadedInsertHole054"
  Angle = 360
  Axis = (0,1,0)
  Base = (0,0,0)
  FaceMakerClass = Part::FaceMakerBullseye
  Placement = pos=(109.5,4.7,68.5) rot=(0,0,1;0rad)
  Solid = false
  Source = -> Face140
  Symmetric = false
FEATURE [Part::MultiFuse] Fusion114  label="removeToCreateScrewAndThreadedInsertHole055"
  Shapes = -> [Revolve148,Revolve147,Revolve146,Revolve145,Revolve144,Revolve143]
FEATURE [Part::Cut] Cut047  label="casePillars004"
  Base = -> Cut037
  Tool = -> Fusion114
FEATURE [Part::Feature] Face141
  shape: bbox 3.5 x 17.8 x 2e-07 mm, 1 faces, 0 solids (baked)
FEATURE [Part::Feature] Face142
  shape: bbox 3.5 x 17.8 x 2e-07 mm, 1 faces, 0 solids (baked)
FEATURE [Part::Feature] Face143
  shape: bbox 3.5 x 17.8 x 2e-07 mm, 1 faces, 0 solids (baked)
FEATURE [Part::Revolution] Revolve149  label="removeToCreateScrewAndThreadedInsertHole057"
  Angle = 360
  Axis = (0,1,0)
  Base = (0,0,0)
  FaceMakerClass = Part::FaceMakerBullseye
  Placement = pos=(12.5,0,10) rot=(0,0,1;0rad)
  Solid = false
  Source = -> Face141
  Symmetric = false
FEATURE [Part::Feature] Face144
  shape: bbox 3.5 x 17.8 x 2e-07 mm, 1 faces, 0 solids (baked)
FEATURE [Part::Feature] Face145
  shape: bbox 3.5 x 17.8 x 2e-07 mm, 1 faces, 0 solids (baked)
FEATURE [Part::Feature] Face146
  shape: bbox 3.5 x 17.8 x 2e-07 mm, 1 faces, 0 solids (baked)
FEATURE [Part::Revolution] Revolve150  label="removeToCreateScrewAndThreadedInsertHole058"
  Angle = 360
  Axis = (0,1,0)
  Base = (0,0,0)
  FaceMakerClass = Part::FaceMakerBullseye
  Placement = pos=(12.5,0,62) rot=(0,0,1;0rad)
  Solid = false
  Source = -> Face146
  Symmetric = false
FEATURE [Part::Revolution] Revolve151  label="removeToCreateScrewAndThreadedInsertHole059"
  Angle = 360
  Axis = (0,1,0)
  Base = (0,0,0)
  FaceMakerClass = Part::FaceMakerBullseye
  Placement = pos=(89.5,0,68.5) rot=(0,0,1;0rad)
  Solid = false
  Source = -> Face143
  Symmetric = false
FEATURE [Part::Revolution] Revolve152  label="removeToCreateScrewAndThreadedInsertHole060"
  Angle = 360
  Axis = (0,1,0)
  Base = (0,0,0)
  FaceMakerClass = Part::FaceMakerBullseye
  Placement = pos=(89.5,0,3.5) rot=(0,0,1;0rad)
  Solid = false
  Source = -> Face142
  Symmetric = false
FEATURE [Part::Revolution] Revolve153  label="removeToCreateScrewAndThreadedInsertHole061"
  Angle = 360
  Axis = (0,1,0)
  Base = (0,0,0)
  FaceMakerClass = Part::FaceMakerBullseye
  Placement = pos=(109.5,4.7,3.5) rot=(0,0,1;0rad)
  Solid = false
  Source = -> Face145
  Symmetric = false
FEATURE [Part::Revolution] Revolve154  label="removeToCreateScrewAndThreadedInsertHole062"
  Angle = 360
  Axis = (0,1,0)
  Base = (0,0,0)
  FaceMakerClass = Part::FaceMakerBullseye
  Placement = pos=(109.5,4.7,68.5) rot=(0,0,1;0rad)
  Solid = false
  Source = -> Face144
  Symmetric = false
FEATURE [Part::MultiFuse] Fusion115  label="removeToCreateScrewAndThreadedInsertHole056"
  Shapes = -> [Revolve154,Revolve153,Revolve152,Revolve151,Revolve150,Revolve149]
FEATURE [Part::Feature] Face147
  shape: bbox 9.8 x 26.5 x 2e-07 mm, 1 faces, 0 solids (baked)
FEATURE [Part::Revolution] Revolve155
  Angle = 360
  Axis = (0,1,0)
  Base = (0,0,0)
  FaceMakerClass = Part::FaceMakerBullseye
  Placement = pos=(0,0,0) rot=(0,0,1;1.5708rad)
  Solid = false
  Source = -> Face147
  Symmetric = false
FEATURE [Part::Feature] Face148
  shape: bbox 9.8 x 26.5 x 2e-07 mm, 1 faces, 0 solids (baked)
FEATURE [Part::Revolution] Revolve156
  Angle = 360
  Axis = (0,1,0)
  Base = (0,0,0)
  FaceMakerClass = Part::FaceMakerBullseye
  Placement = pos=(0,0,0) rot=(0,0,1;1.5708rad)
  Solid = false
  Source = -> Face148
  Symmetric = false
FEATURE [Part::MultiFuse] Fusion116
  Placement = pos=(-18,19,36) rot=(0,0,1;0rad)
  Shapes = -> [Revolve156,Revolve155]
FEATURE [Part::Box] Box029  label="Cube016"
  AttacherType = Attacher::AttachEngine3D
  Height = 28
  Length = 3
  Placement = pos=(110.7,19,22) rot=(0,0,1;0rad)
  Width = 15.7
FEATURE [Part::Cylinder] Cylinder046
  Angle = 360
  AttacherType = Attacher::AttachEngine3D
  Height = 10
  Placement = pos=(0,0,36.15) rot=(0,0,1;0rad)
  Radius = 4
FEATURE [Part::Cylinder] Cylinder047
  Angle = 360
  AttacherType = Attacher::AttachEngine3D
  Height = 20
  Placement = pos=(0,0,36.15) rot=(0,0,1;0rad)
  Radius = 10.3
FEATURE [Part::MultiFuse] Fusion117  label="removeToCreteHoleForPlugHousing041"
  Placement = pos=(70,19,36) rot=(0,1,0;1.5708rad)
  Shapes = -> [Cylinder047,Cylinder046]
FEATURE [Part::Cut] Cut049  label="plugHousingTab004"
  Base = -> Box029
  Placement = pos=(-107.4,-14,0) rot=(0,0,1;0rad)
  Tool = -> Fusion117
FEATURE [Part::Box] Box030  label="Cube017"
  AttacherType = Attacher::AttachEngine3D
  Height = 28
  Length = 3
  Placement = pos=(110.7,19,22) rot=(0,0,1;0rad)
  Width = 15.7
FEATURE [Part::Cylinder] Cylinder048
  Angle = 360
  AttacherType = Attacher::AttachEngine3D
  Height = 10
  Placement = pos=(0,0,36.15) rot=(0,0,1;0rad)
  Radius = 4
FEATURE [Part::Cylinder] Cylinder049
  Angle = 360
  AttacherType = Attacher::AttachEngine3D
  Height = 20
  Placement = pos=(0,0,36.15) rot=(0,0,1;0rad)
  Radius = 10.3
FEATURE [Part::MultiFuse] Fusion118  label="removeToCreteHoleForPlugHousing042"
  Placement = pos=(70,19,36) rot=(0,1,0;1.5708rad)
  Shapes = -> [Cylinder049,Cylinder048]
FEATURE [Part::Cut] Cut050  label="plugHousingTab005"
  Base = -> Box030
  Placement = pos=(-107.4,-14,0) rot=(0,0,1;0rad)
  Tool = -> Fusion118
FEATURE [Part::MultiFuse] Fusion119
  Placement = pos=(9.6,23,0) rot=(0,0,1;3.14159rad)
  Shapes = -> [Cut049,Cut050]
FEATURE [Part::Box] Box031  label="Cube018"
  AttacherType = Attacher::AttachEngine3D
  Height = 10
  Length = 3
  Placement = pos=(3.3,4,12) rot=(0,0,1;0rad)
  Width = 10
FEATURE [Part::Fillet] Fillet044
  Base = -> Box031
  Edges = 1 edges r=2: [Edge11]
FEATURE [Part::Box] Box032  label="Cube019"
  AttacherType = Attacher::AttachEngine3D
  Height = 10
  Length = 3
  Placement = pos=(3.3,4,50) rot=(0,0,1;0rad)
  Width = 10
FEATURE [Part::Fillet] Fillet045
  Base = -> Box032
  Edges = 1 edges r=2: [Edge12]
FEATURE [Part::Box] Box033  label="Cube020"
  AttacherType = Attacher::AttachEngine3D
  Height = 28
  Length = 4
  Placement = pos=(5,0,22) rot=(0,0,1;0rad)
  Width = 10
FEATURE [Part::Fillet] Fillet046
  Base = -> Box033
  Edges = 1 edges r=1: [Edge7]
FEATURE [Part::Fillet] Fillet047
  Base = -> Fillet046
  Edges = 1 edges r=2: [Edge5]
FEATURE [Part::Fillet] Fillet048
  Base = -> Fillet047
  Edges = 1 edges r=2: [Edge2]
FEATURE [Part::Cylinder] Cylinder050
  Angle = 360
  AttacherType = Attacher::AttachEngine3D
  Height = 20
  Placement = pos=(0,0,36.15) rot=(0,0,1;0rad)
  Radius = 8.2
FEATURE [Part::Cylinder] Cylinder051
  Angle = 360
  AttacherType = Attacher::AttachEngine3D
  Height = 10
  Placement = pos=(0,0,36.15) rot=(0,0,1;0rad)
  Radius = 4
FEATURE [Part::MultiFuse] Fusion120  label="removeToCreteHoleForPlugHousing043"
  Placement = pos=(-42,19,36) rot=(0,1,0;1.5708rad)
  Shapes = -> [Cylinder050,Cylinder051]
FEATURE [Sketcher::SketchObject] Sketch067  label="topSketch018"
  FullyConstrained = true
  sketch-geometry (4):
    g0: LineSegment StartX=16.8446 StartY=31.512 StartZ=0 EndX=16.3251 EndY=34.4666 EndZ=0
    g1: ArcOfCircle CenterX=19 CenterY=19.2524 CenterZ=0 NormalX=0 NormalY=0 NormalZ=1 AngleXU=0 Radius=15.4476 StartAngle=1.74483 EndAngle=2.72717
    g2: ArcOfCircle CenterX=19 CenterY=19.2524 CenterZ=0 NormalX=0 NormalY=0 NormalZ=1 AngleXU=0 Radius=12.4476 StartAngle=1.74483 EndAngle=2.73189
    g3: LineSegment StartX=4.86004 StartY=25.4725 StartZ=0 EndX=7.58253 EndY=24.2107 EndZ=0
  constraints (7):
    c: Block(g0)
    c: Coincident(g1,g0)
    c: Coincident(g2,g0)
    c: Coincident(g3,g1)
    c: Coincident(g3,g2)
    c: Block(g1)
    c: Block(g2)
FEATURE [Part::Extrusion] Extrude058
  Base = -> Sketch067
  Dir = (0,0,1)
  DirMode = 2
  FaceMakerClass = Part::FaceMakerBullseye
  LengthFwd = 10
  LengthRev = 0
  Placement = pos=(0,0,31) rot=(0,0,1;0rad)
  Solid = true
  Symmetric = false
FEATURE [Part::Cut] Cut051
  Base = -> Extrude058
  Tool = -> Fusion120
FEATURE [Part::Fillet] Fillet049
  Base = -> Cut051
  Edges = 1 edges r=2: [Edge1]
FEATURE [Part::Fillet] Fillet050
  Base = -> Fillet049
  Edges = 1 edges r=2.5: [Edge1]
FEATURE [Part::Fillet] Fillet051
  Base = -> Fillet050
  Edges = 1 edges r=2.5: [Edge2]
FEATURE [Part::MultiFuse] Fusion121  label="wireHolder003"
  Shapes = -> [Fusion116,Fillet051]
FEATURE [Part::MultiFuse] Fusion122
  Shapes = -> [Fillet045,Fusion121]
FEATURE [Part::MultiFuse] Fusion123  label="wireHolder004"
  Shapes = -> [Fusion122,Fillet048]
FEATURE [Part::MultiFuse] Fusion124  label="wireHolder005"
  Shapes = -> [Fillet044,Fusion119,Fusion123]
FEATURE [Sketcher::SketchObject] Sketch068  label="topSketch019"
  FullyConstrained = true
  sketch-geometry (6):
    g0: LineSegment StartX=19 StartY=38 StartZ=0 EndX=117 EndY=38 EndZ=0
    g1: ArcOfCircle CenterX=19 CenterY=19 CenterZ=0 NormalX=0 NormalY=0 NormalZ=1 AngleXU=0 Radius=19 StartAngle=1.5708 EndAngle=3.14159
    g2: LineSegment StartX=117 StartY=38 StartZ=0 EndX=117 EndY=19 EndZ=0
    g3: LineSegment StartX=98 StartY=1.0161e-12 StartZ=0 EndX=5.22862e-06 EndY=1.0161e-12 EndZ=0
    g4: LineSegment StartX=5.22862e-06 StartY=19 StartZ=0 EndX=5.22862e-06 EndY=1.0161e-12 EndZ=0
    g5: ArcOfCircle CenterX=98 CenterY=19 CenterZ=0 NormalX=0 NormalY=0 NormalZ=1 AngleXU=0 Radius=19 StartAngle=4.71239 EndAngle=6.28319
  constraints (16):
    c: Horizontal(g0)
    c: Distance(g0) = 98
    c: Coincident(g1,g0)
    c: Block(g1)
    c: Coincident(g2,g0)
    c: Vertical(g2)
    c: Distance(g2) = 19
    c: Horizontal(g3)
    c: Coincident(g4,g1)
    c: Vertical(g4)
    c: Coincident(g3,g4)
    c: Block(g3)
    c: Coincident(g5,g2)
    c: Coincident(g5,g3)
    c: Block(g0)
    c: Block(g5)
FEATURE [Part::Extrusion] Extrude059  label="sideA002"
  Base = -> Sketch068
  Dir = (0,0,1)
  DirMode = 2
  FaceMakerClass = Part::FaceMakerBullseye
  LengthFwd = 3
  LengthRev = 0
  Placement = pos=(0,0,-2.7) rot=(0,0,1;0rad)
  Solid = true
  Symmetric = false
FEATURE [Sketcher::SketchObject] Sketch069  label="topSketch020"
  FullyConstrained = true
  sketch-geometry (6):
    g0: LineSegment StartX=19 StartY=38 StartZ=0 EndX=117 EndY=38 EndZ=0
    g1: ArcOfCircle CenterX=19 CenterY=19 CenterZ=0 NormalX=0 NormalY=0 NormalZ=1 AngleXU=0 Radius=19 StartAngle=1.5708 EndAngle=3.14159
    g2: LineSegment StartX=117 StartY=38 StartZ=0 EndX=117 EndY=19 EndZ=0
    g3: LineSegment StartX=98 StartY=1.0161e-12 StartZ=0 EndX=5.22862e-06 EndY=1.0161e-12 EndZ=0
    g4: LineSegment StartX=5.22862e-06 StartY=19 StartZ=0 EndX=5.22862e-06 EndY=1.0161e-12 EndZ=0
    g5: ArcOfCircle CenterX=98 CenterY=19 CenterZ=0 NormalX=0 NormalY=0 NormalZ=1 AngleXU=0 Radius=19 StartAngle=4.71239 EndAngle=6.28319
  constraints (16):
    c: Horizontal(g0)
    c: Distance(g0) = 98
    c: Coincident(g1,g0)
    c: Block(g1)
    c: Coincident(g2,g0)
    c: Vertical(g2)
    c: Distance(g2) = 19
    c: Horizontal(g3)
    c: Coincident(g4,g1)
    c: Vertical(g4)
    c: Coincident(g3,g4)
    c: Block(g3)
    c: Coincident(g5,g2)
    c: Coincident(g5,g3)
    c: Block(g0)
    c: Block(g5)
FEATURE [Part::Extrusion] Extrude060  label="sideB002"
  Base = -> Sketch069
  Dir = (0,0,1)
  DirMode = 2
  FaceMakerClass = Part::FaceMakerBullseye
  LengthFwd = 3
  LengthRev = 0
  Placement = pos=(0,0,71.7) rot=(0,0,1;0rad)
  Solid = true
  Symmetric = false
FEATURE [Part::MultiFuse] Fusion127  label="removeFromBottom001"
  Placement = pos=(2,0,0) rot=(0,0,1;0rad)
  Shapes = -> [Extrude059,Extrude060]
FEATURE [Part::Cylinder] Cylinder052
  Angle = 360
  AttacherType = Attacher::AttachEngine3D
  Height = 20
  Placement = pos=(0,0,36.15) rot=(0,0,1;0rad)
  Radius = 14
FEATURE [Part::Cylinder] Cylinder053
  Angle = 360
  AttacherType = Attacher::AttachEngine3D
  Height = 10
  Placement = pos=(0,0,36.15) rot=(0,0,1;0rad)
  Radius = 4
FEATURE [Part::MultiFuse] Fusion128  label="removeToCreteHoleForPlugHousing044"
  Placement = pos=(70,19,36) rot=(0,1,0;1.5708rad)
  Shapes = -> [Cylinder052,Cylinder053]
FEATURE [Part::Cut] Cut052  label="bottom011"
  Base = -> Extrude043
  Tool = -> Fusion128
FEATURE [Part::Cut] Cut054  label="bottom012"
  Base = -> Cut052
  Tool = -> Fusion115
FEATURE [Sketcher::SketchObject] Sketch070
  FullyConstrained = true
  Placement = pos=(117,19,0) rot=(0.57735,0.57735,0.57735;2.0944rad)
  sketch-geometry (48):
    g0: LineSegment StartX=-49.19 StartY=69.25 StartZ=0 EndX=-49.19 EndY=66.25 EndZ=0
    g1: LineSegment StartX=-49.19 StartY=63.5 StartZ=0 EndX=-49.19 EndY=60.5 EndZ=0
    g2: LineSegment StartX=-49.19 StartY=57.75 StartZ=0 EndX=-49.19 EndY=54.75 EndZ=0
    g3: LineSegment StartX=-49.19 StartY=52 StartZ=0 EndX=-49.19 EndY=49 EndZ=0
    g4: LineSegment StartX=-49.19 StartY=46.25 StartZ=0 EndX=-49.19 EndY=43.25 EndZ=0
    g5: LineSegment StartX=-49.19 StartY=40.5 StartZ=0 EndX=-49.19 EndY=37.5 EndZ=0
    g6: LineSegment StartX=-49.19 StartY=34.5 StartZ=0 EndX=-49.19 EndY=31.5 EndZ=0
    g7: LineSegment StartX=-49.19 StartY=28.75 StartZ=0 EndX=-49.19 EndY=25.75 EndZ=0
    g8: LineSegment StartX=-49.19 StartY=23 StartZ=0 EndX=-49.19 EndY=20 EndZ=0
    g9: LineSegment StartX=-49.19 StartY=17.25 StartZ=0 EndX=-49.19 EndY=14.25 EndZ=0
    g10: LineSegment StartX=-49.19 StartY=11.5 StartZ=0 EndX=-49.19 EndY=8.5 EndZ=0
    g11: LineSegment StartX=-49.19 StartY=5.75 StartZ=0 EndX=-49.19 EndY=2.75 EndZ=0
    g12: ArcOfCircle CenterX=-1.5 CenterY=67.75 CenterZ=0 NormalX=0 NormalY=0 NormalZ=1 AngleXU=0 Radius=1.5 StartAngle=4.71239 EndAngle=7.85398
    g13: ArcOfCircle CenterX=-1.5 CenterY=62 CenterZ=0 NormalX=0 NormalY=0 NormalZ=1 AngleXU=0 Radius=1.5 StartAngle=4.71239 EndAngle=7.85398
    g14: ArcOfCircle CenterX=-1.5 CenterY=56.25 CenterZ=0 NormalX=0 NormalY=0 NormalZ=1 AngleXU=0 Radius=1.5 StartAngle=4.71239 EndAngle=7.85398
    g15: ArcOfCircle CenterX=-11.49 CenterY=50.5 CenterZ=0 NormalX=0 NormalY=0 NormalZ=1 AngleXU=0 Radius=1.5 StartAngle=4.71239 EndAngle=7.85398
    g16: ArcOfCircle CenterX=-16.28 CenterY=44.75 CenterZ=0 NormalX=0 NormalY=0 NormalZ=1 AngleXU=0 Radius=1.5 StartAngle=4.71239 EndAngle=7.85398
    g17: ArcOfCircle CenterX=-18.2337 CenterY=39 CenterZ=0 NormalX=0 NormalY=0 NormalZ=1 AngleXU=0 Radius=1.5 StartAngle=4.71485 EndAngle=7.85398
    g18: ArcOfCircle CenterX=-16.2837 CenterY=27.25 CenterZ=0 NormalX=0 NormalY=0 NormalZ=1 AngleXU=0 Radius=1.5 StartAngle=4.71485 EndAngle=7.85398
    g19: ArcOfCircle CenterX=-18.2337 CenterY=33 CenterZ=0 NormalX=0 NormalY=0 NormalZ=1 AngleXU=0 Radius=1.5 StartAngle=4.71485 EndAngle=7.85398
    g20: ArcOfCircle CenterX=-11.49 CenterY=21.5 CenterZ=0 NormalX=0 NormalY=0 NormalZ=1 AngleXU=0 Radius=1.5 StartAngle=4.71239 EndAngle=7.85398
    g21: ArcOfCircle CenterX=-1.5 CenterY=4.25 CenterZ=0 NormalX=0 NormalY=0 NormalZ=1 AngleXU=0 Radius=1.5 StartAngle=4.71239 EndAngle=7.85398
    g22: ArcOfCircle CenterX=-1.5 CenterY=10 CenterZ=0 NormalX=0 NormalY=0 NormalZ=1 AngleXU=0 Radius=1.5 StartAngle=4.71239 EndAngle=7.85398
    g23: ArcOfCircle CenterX=-1.5 CenterY=15.75 CenterZ=0 NormalX=0 NormalY=0 NormalZ=1 AngleXU=0 Radius=1.5 StartAngle=4.71239 EndAngle=7.85398
    g24: LineSegment StartX=-49.19 StartY=69.25 StartZ=0 EndX=-1.5 EndY=69.25 EndZ=0
    g25: LineSegment StartX=-49.19 StartY=66.25 StartZ=0 EndX=-1.5 EndY=66.25 EndZ=0
    g26: LineSegment StartX=-49.19 StartY=63.5 StartZ=0 EndX=-1.5 EndY=63.5 EndZ=0
    g27: LineSegment StartX=-49.19 StartY=60.5 StartZ=0 EndX=-1.5 EndY=60.5 EndZ=0
    g28: LineSegment StartX=-49.19 StartY=57.75 StartZ=0 EndX=-1.5 EndY=57.75 EndZ=0
    g29: LineSegment StartX=-49.19 StartY=54.75 StartZ=0 EndX=-1.5 EndY=54.75 EndZ=0
    g30: LineSegment StartX=-49.19 StartY=52 StartZ=0 EndX=-11.49 EndY=52 EndZ=0
    g31: LineSegment StartX=-49.19 StartY=49 StartZ=0 EndX=-11.49 EndY=49 EndZ=0
    g32: LineSegment StartX=-49.19 StartY=46.25 StartZ=0 EndX=-16.28 EndY=46.25 EndZ=0
    g33: LineSegment StartX=-49.19 StartY=43.25 StartZ=0 EndX=-16.28 EndY=43.25 EndZ=0
    g34: LineSegment StartX=-49.19 StartY=40.5 StartZ=0 EndX=-18.2337 EndY=40.5 EndZ=0
    g35: LineSegment StartX=-49.19 StartY=37.5 StartZ=0 EndX=-18.23 EndY=37.5 EndZ=0
    g36: LineSegment StartX=-49.19 StartY=34.5 StartZ=0 EndX=-18.2337 EndY=34.5 EndZ=0
    g37: LineSegment StartX=-49.19 StartY=31.5 StartZ=0 EndX=-18.23 EndY=31.5 EndZ=0
    g38: LineSegment StartX=-49.19 StartY=28.75 StartZ=0 EndX=-16.2837 EndY=28.75 EndZ=0
    g39: LineSegment StartX=-49.19 StartY=25.75 StartZ=0 EndX=-16.28 EndY=25.75 EndZ=0
    g40: LineSegment StartX=-49.19 StartY=23 StartZ=0 EndX=-11.49 EndY=23 EndZ=0
    g41: LineSegment StartX=-49.19 StartY=20 StartZ=0 EndX=-11.49 EndY=20 EndZ=0
    g42: LineSegment StartX=-49.19 StartY=17.25 StartZ=0 EndX=-1.5 EndY=17.25 EndZ=0
    g43: LineSegment StartX=-49.19 StartY=14.25 StartZ=0 EndX=-1.5 EndY=14.25 EndZ=0
    g44: LineSegment StartX=-49.19 StartY=11.5 StartZ=0 EndX=-1.5 EndY=11.5 EndZ=0
    g45: LineSegment StartX=-49.19 StartY=8.5 StartZ=0 EndX=-1.5 EndY=8.5 EndZ=0
    g46: LineSegment StartX=-49.19 StartY=5.75 StartZ=0 EndX=-1.5 EndY=5.75 EndZ=0
    g47: LineSegment StartX=-49.19 StartY=2.75 StartZ=0 EndX=-1.5 EndY=2.75 EndZ=0
  constraints (120):
    c: Vertical(g0)
    c: Distance(g0) = 3
    c: Block(g0)
    c: Vertical(g1)
    c: Distance(g1) = 3
    c: Vertical(g2)
    c: Equal(g0,g2) = 3
    c: Block(g2)
    c: Vertical(g3)
    c: Equal(g1,g3) = 3
    c: Vertical(g4)
    c: Equal(g0,g4) = 3
    c: Block(g4)
    c: Vertical(g5)
    c: Equal(g1,g5) = 3
    c: Vertical(g6)
    c: Equal(g0,g6) = 3
    c: Block(g6)
    c: Vertical(g7)
    c: Equal(g1,g7) = 3
    c: Vertical(g8)
    c: Equal(g0,g8) = 3
    c: Block(g8)
    c: Vertical(g9)
    c: Equal(g1,g9) = 3
    c: Vertical(g10)
    c: Equal(g0,g10) = 3
    c: Block(g10)
    c: Vertical(g11)
    c: Equal(g1,g11) = 3
    c: Block(g12)
    c: Block(g13)
    c: Block(g14)
    c: Block(g15)
    c: Block(g16)
    c: Block(g17)
    c: Block(g18)
    c: Block(g19)
    c: Block(g20)
    c: Block(g21)
    c: Block(g22)
    c: Block(g23)
    c: Block(g11)
    c: Block(g9)
    c: Block(g7)
    c: Block(g5)
    c: Block(g3)
    c: Block(g1)
    c: Coincident(g24,g0)
    c: Coincident(g24,g12)
    c: Horizontal(g24)
    c: Coincident(g25,g0)
    c: Coincident(g25,g12)
    c: Horizontal(g25)
    c: Coincident(g26,g1)
    c: Coincident(g26,g13)
    c: Horizontal(g26)
    c: Coincident(g27,g1)
    c: Coincident(g27,g13)
    c: Horizontal(g27)
    c: Coincident(g28,g2)
    c: Coincident(g28,g14)
    c: Horizontal(g28)
    c: Coincident(g29,g2)
    c: Coincident(g29,g14)
    c: Horizontal(g29)
    c: Coincident(g30,g3)
    c: Coincident(g30,g15)
    c: Horizontal(g30)
    c: Coincident(g31,g3)
    c: Coincident(g31,g15)
    c: Horizontal(g31)
    c: Coincident(g32,g4)
    c: Coincident(g32,g16)
    c: Horizontal(g32)
    c: Coincident(g33,g4)
    c: Coincident(g33,g16)
    c: Horizontal(g33)
    c: Coincident(g34,g5)
    c: Coincident(g34,g17)
    c: Horizontal(g34)
    c: Coincident(g35,g5)
    c: Coincident(g35,g17)
    c: Horizontal(g35)
    c: Coincident(g36,g6)
    c: Coincident(g36,g19)
    c: Horizontal(g36)
    c: Coincident(g37,g6)
    c: Coincident(g37,g19)
    c: Horizontal(g37)
    c: Coincident(g38,g7)
    c: Coincident(g38,g18)
    c: Horizontal(g38)
    c: Coincident(g39,g7)
    c: Coincident(g39,g18)
    c: Horizontal(g39)
    c: Coincident(g40,g8)
    c: Coincident(g40,g20)
    c: Horizontal(g40)
    c: Coincident(g41,g8)
    c: Coincident(g41,g20)
    c: Horizontal(g41)
    c: Coincident(g42,g9)
    c: Coincident(g42,g23)
    c: Horizontal(g42)
    c: Coincident(g43,g9)
    c: Coincident(g43,g23)
    c: Horizontal(g43)
    c: Coincident(g44,g10)
    c: Coincident(g44,g22)
    c: Horizontal(g44)
    c: Coincident(g45,g10)
    c: Coincident(g45,g22)
    c: Horizontal(g45)
    c: Coincident(g46,g11)
    c: Coincident(g46,g21)
    c: Horizontal(g46)
    c: Coincident(g47,g11)
    c: Coincident(g47,g21)
    c: Horizontal(g47)
FEATURE [Part::Extrusion] Extrude061
  Base = -> Sketch070
  Dir = (1,0,0)
  DirMode = 2
  FaceMakerClass = Part::FaceMakerBullseye
  LengthFwd = 23
  LengthRev = 0
  Placement = pos=(-19,0,0) rot=(0,0,1;0rad)
  Solid = true
  Symmetric = false
FEATURE [Part::Fillet] Fillet052  label="removeToCreateVentalationHoles002"
  Base = -> Extrude061
  Edges = <same value as first occurrence — deduplicated (x6 in doc)>
  Placement = pos=(7,0.02,0) rot=(0,0,1;0rad)
FEATURE [Part::MultiFuse] Fusion130  label="bottom013"
  Shapes = -> [Cut054,Cut034]
FEATURE [Part::Cut] Cut055
  Base = -> Fusion130
  Tool = -> Fillet052
FEATURE [Part::Cylinder] Cylinder054
  Angle = 360
  AttacherType = Attacher::AttachEngine3D
  Height = 20
  Placement = pos=(0,0,36.15) rot=(0,0,1;0rad)
  Radius = 4
FEATURE [Sketcher::SketchObject] Sketch071  label="bottomSketch002"
  FullyConstrained = true
  sketch-geometry (32):
    g0: LineSegment StartX=3.3 StartY=-6.03275e-07 StartZ=0 EndX=98 EndY=-6.03275e-07 EndZ=0
    g1: ArcOfCircle CenterX=98 CenterY=19 CenterZ=0 NormalX=0 NormalY=0 NormalZ=1 AngleXU=0 Radius=19 StartAngle=4.71239 EndAngle=5.71103
    g2: LineSegment StartX=6.3 StartY=8 StartZ=0 EndX=3.3 EndY=8 EndZ=0
    g3: LineSegment StartX=3.3 StartY=8 StartZ=0 EndX=3.3 EndY=-6.03275e-07 EndZ=0
    g4: ArcOfCircle CenterX=8.3 CenterY=5 CenterZ=0 NormalX=0 NormalY=0 NormalZ=1 AngleXU=0 Radius=2 StartAngle=3.14159 EndAngle=4.71239
    g5: LineSegment StartX=6.3 StartY=8 StartZ=0 EndX=6.3 EndY=5 EndZ=0
    g6: ArcOfCircle CenterX=98 CenterY=19 CenterZ=0 NormalX=0 NormalY=0 NormalZ=1 AngleXU=0 Radius=12.7 StartAngle=4.71239 EndAngle=6.28319
    g7: LineSegment StartX=94.7 StartY=3 StartZ=0 EndX=8.3 EndY=3 EndZ=0
    g8-g12: Circle x5 (B-spline internal-alignment scaffolding for g13; pole/knot coordinates omitted)
    g13: BSplineCurve PolesCount=5 KnotsCount=3 Degree=3 IsPeriodic=0
    g14: GeomPoint X=98 Y=6.3 Z=0
    g15: GeomPoint X=96.3938 Y=4.71946 Z=0
    g16: GeomPoint X=94.7 Y=3 Z=0
    g17-g23: Circle x7 (B-spline internal-alignment scaffolding for g24; pole/knot coordinates omitted)
    g24: BSplineCurve PolesCount=7 KnotsCount=5 Degree=3 IsPeriodic=0
    g25-g29: GeomPoint x5 (B-spline internal-alignment scaffolding for g24; pole/knot coordinates omitted)
    g30: ArcOfCircle CenterX=98 CenterY=19 CenterZ=0 NormalX=0 NormalY=0 NormalZ=1 AngleXU=0 Radius=15.7 StartAngle=5.81226 EndAngle=6.28319
    g31: LineSegment StartX=110.7 StartY=19 StartZ=0 EndX=113.7 EndY=19 EndZ=0
  constraints (41):
    c: Horizontal(g0)
    c: Coincident(g1,g0)
    c: Block(g1)
    c: Horizontal(g2)
    c: Distance(g2) = 3
    c: Coincident(g3,g2)
    c: Vertical(g3)
    c: Coincident(g3,g0)
    c: Block(g4)
    c: Block(g2)
    c: Coincident(g5,g2)
    c: Coincident(g5,g4)
    c: Vertical(g5)
    c: Coincident(g6,g1)
    c: Block(g6)
    c: Coincident(g7,g4)
    c: Horizontal(g7)
    c: Block(g0)
    c: Block(g7)
    c: Block(g3)
    c: Coincident(g13,g6)
    c: Weight(g8) = 1
    c: Equal(g8, g9-g12) x4
    c: Coincident(g13,g7)
    c: InternalAlignment(g8-g12 -> g13) x5
    c: InternalAlignment(g14,g13)
    c: InternalAlignment(g15,g13)
    c: InternalAlignment(g16,g13)
    c: Block(g13)
    c: Weight(g17) = 1
    c: Equal(g17, g18-g23) x6
    c: Coincident(g24,g1)
    c: InternalAlignment(g17-g23 -> g24) x7
    c: InternalAlignment(g25-g29 -> g24) x5
    c: Block(g24)
    c: Coincident(g30,g24)
    c: Coincident(g31,g6)
    c: Coincident(g31,g30)
    c: Horizontal(g31)
    c: Block(g31)
    c: Block(g30)
FEATURE [Part::Extrusion] Extrude062  label="bottom014"
  Base = -> Sketch071
  Dir = (0,0,1)
  DirMode = 2
  FaceMakerClass = Part::FaceMakerBullseye
  LengthFwd = 71.4
  LengthRev = 0
  Placement = pos=(0,0,0.3) rot=(0,0,1;0rad)
  Solid = true
  Symmetric = false
FEATURE [Part::Fillet] Fillet054
  Base = -> Extrude062
  Edges = 1 edges r=2.4: [Edge17]
FEATURE [Part::Fillet] Fillet055  label="bottom015"
  Base = -> Fillet054
  Edges = 1 edges r=2.4: [Edge36]
FEATURE [Part::Cylinder] Cylinder055
  Angle = 360
  AttacherType = Attacher::AttachEngine3D
  Height = 10
  Placement = pos=(0,0,36.15) rot=(0,0,1;0rad)
  Radius = 4
FEATURE [Part::MultiFuse] Fusion131  label="removeToCreateHoleForPlugHousing002"
  Placement = pos=(70,19,36.15) rot=(0,1,0;1.5708rad)
  Shapes = -> [Cylinder054,Cylinder055]
FEATURE [Part::Cut] Cut056  label="Bottom001"
  Base = -> Fillet055
  Placement = pos=(9,0,0) rot=(0,0,1;0rad)
  Tool = -> Fusion131
FEATURE [Part::Cut] Cut057
  Base = -> Cut055
  Tool = -> Cut056
FEATURE [Sketcher::SketchObject] Sketch072  label="topSketch021"
  FullyConstrained = true
  sketch-geometry (4):
    g0: ArcOfCircle CenterX=105 CenterY=19 CenterZ=0 NormalX=0 NormalY=0 NormalZ=1 AngleXU=0 Radius=20.6155 StartAngle=5.54125 EndAngle=6.28319
    g1: ArcOfCircle CenterX=105 CenterY=19 CenterZ=0 NormalX=0 NormalY=0 NormalZ=1 AngleXU=0 Radius=13 StartAngle=5.54125 EndAngle=6.28319
    g2: LineSegment StartX=118 StartY=19 StartZ=0 EndX=125.616 EndY=19 EndZ=0
    g3: LineSegment StartX=114.583 StartY=10.2157 StartZ=0 EndX=120.197 EndY=5.06982 EndZ=0
  constraints (7):
    c: Block(g0)
    c: Block(g1)
    c: Coincident(g2,g1)
    c: Coincident(g2,g0)
    c: Horizontal(g2)
    c: Coincident(g3,g1)
    c: Coincident(g3,g0)
FEATURE [Part::Extrusion] Extrude063  label="bottomPlugHousingBit003"
  Base = -> Sketch072
  Dir = (0,0,1)
  DirMode = 2
  FaceMakerClass = Part::FaceMakerBullseye
  LengthFwd = 72
  LengthRev = 0
  Solid = true
  Symmetric = false
FEATURE [Part::Cylinder] Cylinder056
  Angle = 360
  AttacherType = Attacher::AttachEngine3D
  Height = 20
  Placement = pos=(0,0,36.15) rot=(0,0,1;0rad)
  Radius = 14.3
FEATURE [Part::Cylinder] Cylinder057
  Angle = 360
  AttacherType = Attacher::AttachEngine3D
  Height = 10
  Placement = pos=(0,0,36.15) rot=(0,0,1;0rad)
  Radius = 4
FEATURE [Part::Box] Box034  label="removeToCreteHoleForPlugHousing047"
  AttacherType = Attacher::AttachEngine3D
  Height = 28.6
  Length = 20
  Placement = pos=(106.15,0,21.7) rot=(0,0,1;0rad)
  Width = 19
FEATURE [Part::Cylinder] Cylinder058
  Angle = 360
  AttacherType = Attacher::AttachEngine3D
  Height = 20
  Placement = pos=(0,0,36.15) rot=(0,0,1;0rad)
  Radius = 14.3
FEATURE [Part::Cylinder] Cylinder059
  Angle = 360
  AttacherType = Attacher::AttachEngine3D
  Height = 10
  Placement = pos=(0,0,36.15) rot=(0,0,1;0rad)
  Radius = 4
FEATURE [Part::MultiFuse] Fusion134  label="removeToCreteHoleForPlugHousing046"
  Placement = pos=(70,19,36) rot=(0,1,0;1.5708rad)
  Shapes = -> [Cylinder058,Cylinder059]
FEATURE [Part::Cylinder] Cylinder060
  Angle = 360
  AttacherType = Attacher::AttachEngine3D
  Height = 20
  Placement = pos=(0,0,36.15) rot=(0,0,1;0rad)
  Radius = 14
FEATURE [Part::Cylinder] Cylinder061
  Angle = 360
  AttacherType = Attacher::AttachEngine3D
  Height = 10
  Placement = pos=(0,0,36.15) rot=(0,0,1;0rad)
  Radius = 4
FEATURE [Part::MultiFuse] Fusion135  label="removeToCreteHoleForPlugHousing048"
  Placement = pos=(70,19,36) rot=(0,1,0;1.5708rad)
  Shapes = -> [Cylinder060,Cylinder061]
FEATURE [Part::Box] Box035  label="removeToCreteHoleForPlugHousing049"
  AttacherType = Attacher::AttachEngine3D
  Height = 28.6
  Length = 20
  Placement = pos=(106.15,0,21.7) rot=(0,0,1;0rad)
  Width = 19
FEATURE [Part::MultiFuse] Fusion133  label="removeToCreteHoleForPlugHousing045"
  Placement = pos=(0,0,-28.3) rot=(0,0,1;0rad)
  Shapes = -> [Box035,Fusion134]
FEATURE [Part::MultiFuse] Fusion138  label="removeToCreteHoleForPlugHousing051"
  Placement = pos=(70,19,36) rot=(0,1,0;1.5708rad)
  Shapes = -> [Cylinder056,Cylinder057]
FEATURE [Part::MultiFuse] Fusion137  label="removeToCreteHoleForPlugHousing050"
  Placement = pos=(0,0,28.3) rot=(0,0,1;0rad)
  Shapes = -> [Box034,Fusion138]
FEATURE [Part::MultiFuse] Fusion132  label="removeToCreatePlugHousingBottomBit002"
  Shapes = -> [Fusion133,Fusion137]
FEATURE [Part::MultiFuse] Fusion136  label="removeToCreatePlugHousingBottomBit003"
  Shapes = -> [Fusion135,Fusion132]
FEATURE [Part::Cut] Cut058  label="bottomPlugHousingBit002"
  Base = -> Extrude063
  Placement = pos=(-0.09,0,0) rot=(0,0,1;0rad)
  Tool = -> Fusion136
FEATURE [Sketcher::SketchObject] Sketch073  label="bottomSketch003"
  FullyConstrained = true
  sketch-geometry (45):
    g0: LineSegment StartX=6.29999 StartY=8 StartZ=0 EndX=3.29999 EndY=8 EndZ=0
    g1: LineSegment StartX=3.29999 StartY=8 StartZ=0 EndX=3.29999 EndY=-6.03275e-07 EndZ=0
    g2: ArcOfCircle CenterX=8.29999 CenterY=5 CenterZ=0 NormalX=0 NormalY=0 NormalZ=1 AngleXU=0 Radius=2 StartAngle=3.14159 EndAngle=4.71239
    g3: LineSegment StartX=6.29999 StartY=8 StartZ=0 EndX=6.29999 EndY=5 EndZ=0
    g4: ArcOfCircle CenterX=105 CenterY=19 CenterZ=0 NormalX=0 NormalY=0 NormalZ=1 AngleXU=0 Radius=12.7 StartAngle=4.71239 EndAngle=5.94289
    g5-g11: Circle x7 (B-spline internal-alignment scaffolding for g12; pole/knot coordinates omitted)
    g12: BSplineCurve PolesCount=7 KnotsCount=5 Degree=3 IsPeriodic=0
    g13-g17: GeomPoint x5 (B-spline internal-alignment scaffolding for g12; pole/knot coordinates omitted)
    g18: ArcOfCircle CenterX=105 CenterY=19 CenterZ=0 NormalX=0 NormalY=0 NormalZ=1 AngleXU=0 Radius=15.7 StartAngle=5.81226 EndAngle=6.28319
    g19: BSplineCurve PolesCount=5 KnotsCount=3 Degree=3 IsPeriodic=0
    g20: LineSegment StartX=8.29999 StartY=3 StartZ=0 EndX=101.7 EndY=3 EndZ=0
    g21: LineSegment StartX=3.29999 StartY=-6.03275e-07 StartZ=0 EndX=105 EndY=-6.03275e-07 EndZ=0
    g22: LineSegment StartX=120.974 StartY=8.71251 StartZ=0 EndX=122.332 EndY=7.83778 EndZ=0
    g23: LineSegment StartX=105 StartY=-6.03274e-07 StartZ=0 EndX=113 EndY=-6.03274e-07 EndZ=0
    g24: ArcOfCircle CenterX=105 CenterY=19 CenterZ=0 NormalX=0 NormalY=0 NormalZ=1 AngleXU=0 Radius=20.6155 StartAngle=5.11091 EndAngle=5.71103
    g25: ArcOfCircle CenterX=117.7 CenterY=19 CenterZ=0 NormalX=0 NormalY=0 NormalZ=1 AngleXU=0 Radius=3 StartAngle=1.2e-15 EndAngle=2.10468
    g26: Circle CenterX=116.345 CenterY=16.3232 CenterZ=0 NormalX=0 NormalY=0 NormalZ=1 AngleXU=0 Radius=1
    g27: Circle CenterX=117.24 CenterY=15.7584 CenterZ=0 NormalX=0 NormalY=0 NormalZ=1 AngleXU=0 Radius=1
    g28: Circle CenterX=116.972 CenterY=14.7612 CenterZ=0 NormalX=0 NormalY=0 NormalZ=1 AngleXU=0 Radius=1
    g29: BSplineCurve PolesCount=3 KnotsCount=2 Degree=2 IsPeriodic=0
    g30: GeomPoint X=116.345 Y=16.3232 Z=0
    g31: GeomPoint X=116.972 Y=14.7612 Z=0
    g32: Circle CenterX=115.828 CenterY=17.157 CenterZ=0 NormalX=0 NormalY=0 NormalZ=1 AngleXU=0 Radius=1
    g33: Circle CenterX=115.841 CenterY=16.639 CenterZ=0 NormalX=0 NormalY=0 NormalZ=1 AngleXU=0 Radius=1
    g34: Circle CenterX=116.345 CenterY=16.3232 CenterZ=0 NormalX=0 NormalY=0 NormalZ=1 AngleXU=0 Radius=1
    g35: BSplineCurve PolesCount=3 KnotsCount=2 Degree=2 IsPeriodic=0
    g36: GeomPoint X=115.828 Y=17.157 Z=0
    g37: GeomPoint X=116.345 Y=16.3232 Z=0
    g38: LineSegment StartX=115.828 StartY=17.157 StartZ=0 EndX=115.828 EndY=20.8307 EndZ=0
    g39: Circle CenterX=115.828 CenterY=20.8307 CenterZ=0 NormalX=0 NormalY=0 NormalZ=1 AngleXU=0 Radius=1
    g40: Circle CenterX=115.831 CenterY=21.3396 CenterZ=0 NormalX=0 NormalY=0 NormalZ=1 AngleXU=0 Radius=1
    g41: Circle CenterX=116.173 CenterY=21.5825 CenterZ=0 NormalX=0 NormalY=0 NormalZ=1 AngleXU=0 Radius=1
    g42: BSplineCurve PolesCount=3 KnotsCount=2 Degree=2 IsPeriodic=0
    g43: GeomPoint X=115.828 Y=20.8307 Z=0
    g44: GeomPoint X=116.173 Y=21.5825 Z=0
  constraints (70):
    c: Horizontal(g0)
    c: Distance(g0) = 3
    c: Coincident(g1,g0)
    c: Vertical(g1)
    c: Block(g2)
    c: Block(g0)
    c: Coincident(g3,g0)
    c: Coincident(g3,g2)
    c: Vertical(g3)
    c: Block(g1)
    c: Block(g4)
    c: Coincident(g19,g4)
    c: Block(g19)
    c: Equal(g5, g6-g11) x6
    c: InternalAlignment(g5-g11 -> g12) x7
    c: InternalAlignment(g13-g17 -> g12) x5
    c: Block(g12)
    c: Coincident(g18,g12)
    c: Block(g18)
    c: Coincident(g20,g2)
    c: Coincident(g20,g19)
    c: Horizontal(g20)
    c: Distance(g20) = 93.4
    c: Coincident(g21,g1)
    c: Horizontal(g21)
    c: Distance(g21) = 101.7
    c: Horizontal(g23)
    c: Distance(g23) = 8
    c: Coincident(g24,g23)
    c: Block(g23)
    c: Coincident(g22,g24)
    c: Block(g24)
    c: Block(g22)
    c: Distance(g22) = 1.61553
    c: Coincident(g25,g18)
    c: Block(g25)
    c: Weight(g26) = 1
    c: Equal(g26,g27)
    c: Equal(g26,g28)
    c: Coincident(g29,g4)
    c: InternalAlignment(g26,g29)
    c: InternalAlignment(g27,g29)
    c: InternalAlignment(g28,g29)
    c: InternalAlignment(g30,g29)
    c: InternalAlignment(g31,g29)
    c: Block(g29)
    c: Weight(g32) = 1
    c: Equal(g32,g33)
    c: Equal(g32,g34)
    c: Coincident(g35,g29)
    c: InternalAlignment(g32,g35)
    c: InternalAlignment(g33,g35)
    c: InternalAlignment(g34,g35)
    c: InternalAlignment(g36,g35)
    c: InternalAlignment(g37,g35)
    c: Block(g35)
    c: Coincident(g38,g35)
    c: Vertical(g38)
    c: Block(g38)
    c: Coincident(g42,g38)
    c: Weight(g39) = 1
    c: Equal(g39,g40)
    c: Equal(g39,g41)
    c: Coincident(g42,g25)
    c: InternalAlignment(g39,g42)
    c: InternalAlignment(g40,g42)
    c: InternalAlignment(g41,g42)
    c: InternalAlignment(g43,g42)
    c: InternalAlignment(g44,g42)
    c: Block(g42)
FEATURE [Part::Extrusion] Extrude064  label="bottom016"
  Base = -> Sketch073
  Dir = (0,0,1)
  DirMode = 2
  FaceMakerClass = Part::FaceMakerBullseye
  LengthFwd = 71.4
  LengthRev = 0
  Placement = pos=(0,0,0.3) rot=(0,0,1;0rad)
  Solid = true
  Symmetric = false
FEATURE [Part::Revolution] Revolve157  label="removeToCreateScrewAndThreadedInsertHole063"
  Angle = 360
  Axis = (0,1,0)
  Base = (0,0,0)
  FaceMakerClass = Part::FaceMakerBullseye
  Placement = pos=(12.5,0,10) rot=(0,0,1;0rad)
  Solid = false
  Source = -> Face141
  Symmetric = false
FEATURE [Sketcher::SketchObject] Sketch074
  FullyConstrained = true
  Placement = pos=(117,19,0) rot=(0.57735,0.57735,0.57735;2.0944rad)
  sketch-geometry (48):
    g0: LineSegment StartX=-49.19 StartY=69.25 StartZ=0 EndX=-49.19 EndY=66.25 EndZ=0
    g1: LineSegment StartX=-49.19 StartY=63.5 StartZ=0 EndX=-49.19 EndY=60.5 EndZ=0
    g2: LineSegment StartX=-49.19 StartY=57.75 StartZ=0 EndX=-49.19 EndY=54.75 EndZ=0
    g3: LineSegment StartX=-49.19 StartY=52 StartZ=0 EndX=-49.19 EndY=49 EndZ=0
    g4: LineSegment StartX=-49.19 StartY=46.25 StartZ=0 EndX=-49.19 EndY=43.25 EndZ=0
    g5: LineSegment StartX=-49.19 StartY=40.5 StartZ=0 EndX=-49.19 EndY=37.5 EndZ=0
    g6: LineSegment StartX=-49.19 StartY=34.5 StartZ=0 EndX=-49.19 EndY=31.5 EndZ=0
    g7: LineSegment StartX=-49.19 StartY=28.75 StartZ=0 EndX=-49.19 EndY=25.75 EndZ=0
    g8: LineSegment StartX=-49.19 StartY=23 StartZ=0 EndX=-49.19 EndY=20 EndZ=0
    g9: LineSegment StartX=-49.19 StartY=17.25 StartZ=0 EndX=-49.19 EndY=14.25 EndZ=0
    g10: LineSegment StartX=-49.19 StartY=11.5 StartZ=0 EndX=-49.19 EndY=8.5 EndZ=0
    g11: LineSegment StartX=-49.19 StartY=5.75 StartZ=0 EndX=-49.19 EndY=2.75 EndZ=0
    g12: ArcOfCircle CenterX=-1.5 CenterY=67.75 CenterZ=0 NormalX=0 NormalY=0 NormalZ=1 AngleXU=0 Radius=1.5 StartAngle=4.71239 EndAngle=7.85398
    g13: ArcOfCircle CenterX=-1.5 CenterY=62 CenterZ=0 NormalX=0 NormalY=0 NormalZ=1 AngleXU=0 Radius=1.5 StartAngle=4.71239 EndAngle=7.85398
    g14: ArcOfCircle CenterX=-1.5 CenterY=56.25 CenterZ=0 NormalX=0 NormalY=0 NormalZ=1 AngleXU=0 Radius=1.5 StartAngle=4.71239 EndAngle=7.85398
    g15: ArcOfCircle CenterX=-11.49 CenterY=50.5 CenterZ=0 NormalX=0 NormalY=0 NormalZ=1 AngleXU=0 Radius=1.5 StartAngle=4.71239 EndAngle=7.85398
    g16: ArcOfCircle CenterX=-16.28 CenterY=44.75 CenterZ=0 NormalX=0 NormalY=0 NormalZ=1 AngleXU=0 Radius=1.5 StartAngle=4.71239 EndAngle=7.85398
    g17: ArcOfCircle CenterX=-18.2337 CenterY=39 CenterZ=0 NormalX=0 NormalY=0 NormalZ=1 AngleXU=0 Radius=1.5 StartAngle=4.71485 EndAngle=7.85398
    g18: ArcOfCircle CenterX=-16.2837 CenterY=27.25 CenterZ=0 NormalX=0 NormalY=0 NormalZ=1 AngleXU=0 Radius=1.5 StartAngle=4.71485 EndAngle=7.85398
    g19: ArcOfCircle CenterX=-18.2337 CenterY=33 CenterZ=0 NormalX=0 NormalY=0 NormalZ=1 AngleXU=0 Radius=1.5 StartAngle=4.71485 EndAngle=7.85398
    g20: ArcOfCircle CenterX=-11.49 CenterY=21.5 CenterZ=0 NormalX=0 NormalY=0 NormalZ=1 AngleXU=0 Radius=1.5 StartAngle=4.71239 EndAngle=7.85398
    g21: ArcOfCircle CenterX=-1.5 CenterY=4.25 CenterZ=0 NormalX=0 NormalY=0 NormalZ=1 AngleXU=0 Radius=1.5 StartAngle=4.71239 EndAngle=7.85398
    g22: ArcOfCircle CenterX=-1.5 CenterY=10 CenterZ=0 NormalX=0 NormalY=0 NormalZ=1 AngleXU=0 Radius=1.5 StartAngle=4.71239 EndAngle=7.85398
    g23: ArcOfCircle CenterX=-1.5 CenterY=15.75 CenterZ=0 NormalX=0 NormalY=0 NormalZ=1 AngleXU=0 Radius=1.5 StartAngle=4.71239 EndAngle=7.85398
    g24: LineSegment StartX=-49.19 StartY=69.25 StartZ=0 EndX=-1.5 EndY=69.25 EndZ=0
    g25: LineSegment StartX=-49.19 StartY=66.25 StartZ=0 EndX=-1.5 EndY=66.25 EndZ=0
    g26: LineSegment StartX=-49.19 StartY=63.5 StartZ=0 EndX=-1.5 EndY=63.5 EndZ=0
    g27: LineSegment StartX=-49.19 StartY=60.5 StartZ=0 EndX=-1.5 EndY=60.5 EndZ=0
    g28: LineSegment StartX=-49.19 StartY=57.75 StartZ=0 EndX=-1.5 EndY=57.75 EndZ=0
    g29: LineSegment StartX=-49.19 StartY=54.75 StartZ=0 EndX=-1.5 EndY=54.75 EndZ=0
    g30: LineSegment StartX=-49.19 StartY=52 StartZ=0 EndX=-11.49 EndY=52 EndZ=0
    g31: LineSegment StartX=-49.19 StartY=49 StartZ=0 EndX=-11.49 EndY=49 EndZ=0
    g32: LineSegment StartX=-49.19 StartY=46.25 StartZ=0 EndX=-16.28 EndY=46.25 EndZ=0
    g33: LineSegment StartX=-49.19 StartY=43.25 StartZ=0 EndX=-16.28 EndY=43.25 EndZ=0
    g34: LineSegment StartX=-49.19 StartY=40.5 StartZ=0 EndX=-18.2337 EndY=40.5 EndZ=0
    g35: LineSegment StartX=-49.19 StartY=37.5 StartZ=0 EndX=-18.23 EndY=37.5 EndZ=0
    g36: LineSegment StartX=-49.19 StartY=34.5 StartZ=0 EndX=-18.2337 EndY=34.5 EndZ=0
    g37: LineSegment StartX=-49.19 StartY=31.5 StartZ=0 EndX=-18.23 EndY=31.5 EndZ=0
    g38: LineSegment StartX=-49.19 StartY=28.75 StartZ=0 EndX=-16.2837 EndY=28.75 EndZ=0
    g39: LineSegment StartX=-49.19 StartY=25.75 StartZ=0 EndX=-16.28 EndY=25.75 EndZ=0
    g40: LineSegment StartX=-49.19 StartY=23 StartZ=0 EndX=-11.49 EndY=23 EndZ=0
    g41: LineSegment StartX=-49.19 StartY=20 StartZ=0 EndX=-11.49 EndY=20 EndZ=0
    g42: LineSegment StartX=-49.19 StartY=17.25 StartZ=0 EndX=-1.5 EndY=17.25 EndZ=0
    g43: LineSegment StartX=-49.19 StartY=14.25 StartZ=0 EndX=-1.5 EndY=14.25 EndZ=0
    g44: LineSegment StartX=-49.19 StartY=11.5 StartZ=0 EndX=-1.5 EndY=11.5 EndZ=0
    g45: LineSegment StartX=-49.19 StartY=8.5 StartZ=0 EndX=-1.5 EndY=8.5 EndZ=0
    g46: LineSegment StartX=-49.19 StartY=5.75 StartZ=0 EndX=-1.5 EndY=5.75 EndZ=0
    g47: LineSegment StartX=-49.19 StartY=2.75 StartZ=0 EndX=-1.5 EndY=2.75 EndZ=0
  constraints (120):
    c: Vertical(g0)
    c: Distance(g0) = 3
    c: Block(g0)
    c: Vertical(g1)
    c: Distance(g1) = 3
    c: Vertical(g2)
    c: Equal(g0,g2) = 3
    c: Block(g2)
    c: Vertical(g3)
    c: Equal(g1,g3) = 3
    c: Vertical(g4)
    c: Equal(g0,g4) = 3
    c: Block(g4)
    c: Vertical(g5)
    c: Equal(g1,g5) = 3
    c: Vertical(g6)
    c: Equal(g0,g6) = 3
    c: Block(g6)
    c: Vertical(g7)
    c: Equal(g1,g7) = 3
    c: Vertical(g8)
    c: Equal(g0,g8) = 3
    c: Block(g8)
    c: Vertical(g9)
    c: Equal(g1,g9) = 3
    c: Vertical(g10)
    c: Equal(g0,g10) = 3
    c: Block(g10)
    c: Vertical(g11)
    c: Equal(g1,g11) = 3
    c: Block(g12)
    c: Block(g13)
    c: Block(g14)
    c: Block(g15)
    c: Block(g16)
    c: Block(g17)
    c: Block(g18)
    c: Block(g19)
    c: Block(g20)
    c: Block(g21)
    c: Block(g22)
    c: Block(g23)
    c: Block(g11)
    c: Block(g9)
    c: Block(g7)
    c: Block(g5)
    c: Block(g3)
    c: Block(g1)
    c: Coincident(g24,g0)
    c: Coincident(g24,g12)
    c: Horizontal(g24)
    c: Coincident(g25,g0)
    c: Coincident(g25,g12)
    c: Horizontal(g25)
    c: Coincident(g26,g1)
    c: Coincident(g26,g13)
    c: Horizontal(g26)
    c: Coincident(g27,g1)
    c: Coincident(g27,g13)
    c: Horizontal(g27)
    c: Coincident(g28,g2)
    c: Coincident(g28,g14)
    c: Horizontal(g28)
    c: Coincident(g29,g2)
    c: Coincident(g29,g14)
    c: Horizontal(g29)
    c: Coincident(g30,g3)
    c: Coincident(g30,g15)
    c: Horizontal(g30)
    c: Coincident(g31,g3)
    c: Coincident(g31,g15)
    c: Horizontal(g31)
    c: Coincident(g32,g4)
    c: Coincident(g32,g16)
    c: Horizontal(g32)
    c: Coincident(g33,g4)
    c: Coincident(g33,g16)
    c: Horizontal(g33)
    c: Coincident(g34,g5)
    c: Coincident(g34,g17)
    c: Horizontal(g34)
    c: Coincident(g35,g5)
    c: Coincident(g35,g17)
    c: Horizontal(g35)
    c: Coincident(g36,g6)
    c: Coincident(g36,g19)
    c: Horizontal(g36)
    c: Coincident(g37,g6)
    c: Coincident(g37,g19)
    c: Horizontal(g37)
    c: Coincident(g38,g7)
    c: Coincident(g38,g18)
    c: Horizontal(g38)
    c: Coincident(g39,g7)
    c: Coincident(g39,g18)
    c: Horizontal(g39)
    c: Coincident(g40,g8)
    c: Coincident(g40,g20)
    c: Horizontal(g40)
    c: Coincident(g41,g8)
    c: Coincident(g41,g20)
    c: Horizontal(g41)
    c: Coincident(g42,g9)
    c: Coincident(g42,g23)
    c: Horizontal(g42)
    c: Coincident(g43,g9)
    c: Coincident(g43,g23)
    c: Horizontal(g43)
    c: Coincident(g44,g10)
    c: Coincident(g44,g22)
    c: Horizontal(g44)
    c: Coincident(g45,g10)
    c: Coincident(g45,g22)
    c: Horizontal(g45)
    c: Coincident(g46,g11)
    c: Coincident(g46,g21)
    c: Horizontal(g46)
    c: Coincident(g47,g11)
    c: Coincident(g47,g21)
    c: Horizontal(g47)
FEATURE [Part::Extrusion] Extrude065
  Base = -> Sketch074
  Dir = (1,0,0)
  DirMode = 2
  FaceMakerClass = Part::FaceMakerBullseye
  LengthFwd = 23
  LengthRev = 0
  Placement = pos=(-19,0,0) rot=(0,0,1;0rad)
  Solid = true
  Symmetric = false
FEATURE [Part::Fillet] Fillet056  label="removeToCreateVentalationHoles003"
  Base = -> Extrude065
  Edges = <same value as first occurrence — deduplicated (x6 in doc)>
  Placement = pos=(7,0.02,0) rot=(0,0,1;0rad)
FEATURE [Part::Revolution] Revolve158  label="removeToCreateScrewAndThreadedInsertHole065"
  Angle = 360
  Axis = (0,1,0)
  Base = (0,0,0)
  FaceMakerClass = Part::FaceMakerBullseye
  Placement = pos=(12.5,0,62) rot=(0,0,1;0rad)
  Solid = false
  Source = -> Face146
  Symmetric = false
FEATURE [Part::Revolution] Revolve159  label="removeToCreateScrewAndThreadedInsertHole066"
  Angle = 360
  Axis = (0,1,0)
  Base = (0,0,0)
  FaceMakerClass = Part::FaceMakerBullseye
  Placement = pos=(89.5,0,68.5) rot=(0,0,1;0rad)
  Solid = false
  Source = -> Face143
  Symmetric = false
FEATURE [Part::Revolution] Revolve160  label="removeToCreateScrewAndThreadedInsertHole067"
  Angle = 360
  Axis = (0,1,0)
  Base = (0,0,0)
  FaceMakerClass = Part::FaceMakerBullseye
  Placement = pos=(89.5,0,3.5) rot=(0,0,1;0rad)
  Solid = false
  Source = -> Face142
  Symmetric = false
FEATURE [Part::Revolution] Revolve161  label="removeToCreateScrewAndThreadedInsertHole068"
  Angle = 360
  Axis = (0,1,0)
  Base = (0,0,0)
  FaceMakerClass = Part::FaceMakerBullseye
  Placement = pos=(109.5,4.7,3.5) rot=(0,0,1;0rad)
  Solid = false
  Source = -> Face145
  Symmetric = false
FEATURE [Part::Revolution] Revolve162  label="removeToCreateScrewAndThreadedInsertHole069"
  Angle = 360
  Axis = (0,1,0)
  Base = (0,0,0)
  FaceMakerClass = Part::FaceMakerBullseye
  Placement = pos=(109.5,4.7,68.5) rot=(0,0,1;0rad)
  Solid = false
  Source = -> Face144
  Symmetric = false
FEATURE [Part::MultiFuse] Fusion141  label="removeToCreateScrewAndThreadedInsertHole064"
  Shapes = -> [Revolve162,Revolve161,Revolve160,Revolve159,Revolve158,Revolve157]
FEATURE [Part::Cylinder] Cylinder062
  Angle = 360
  AttacherType = Attacher::AttachEngine3D
  Height = 20
  Placement = pos=(0,0,36.15) rot=(0,0,1;0rad)
  Radius = 14
FEATURE [Part::Cylinder] Cylinder063
  Angle = 360
  AttacherType = Attacher::AttachEngine3D
  Height = 10
  Placement = pos=(0,0,36.15) rot=(0,0,1;0rad)
  Radius = 4
FEATURE [Part::MultiFuse] Fusion139  label="removeToCreteHoleForPlugHousing052"
  Placement = pos=(70,19,36) rot=(0,1,0;1.5708rad)
  Shapes = -> [Cylinder062,Cylinder063]
FEATURE [Part::Cut] Cut060  label="bottom017"
  Base = -> Extrude064
  Tool = -> Fusion139
FEATURE [Part::Cut] Cut061  label="bottom019"
  Base = -> Cut060
  Tool = -> Fusion141
FEATURE [Part::MultiFuse] Fusion140  label="bottom018"
  Shapes = -> [Cut061,Cut058]
FEATURE [Part::Cut] Cut059  label="bottom020"
  Base = -> Fusion140
  Tool = -> Fillet056
FEATURE [Part::Box] Box036  label="Cube021"
  AttacherType = Attacher::AttachEngine3D
  Height = 80
  Length = 26
  Placement = pos=(0,-1,-5) rot=(0,0,1;0rad)
  Width = 11
FEATURE [Part::Cut] Cut062  label="removeFromBottom002"
  Base = -> Cut057
  Tool = -> Box036
FEATURE [Part::Cut] Cut063
  Base = -> Cut059
  Tool = -> Cut062
FEATURE [Part::Cut] Cut064  label="pcbStands"
  Base = -> Fusion095
  Tool = -> Fusion127
FEATURE [Sketcher::SketchObject] Sketch075  label="topSketch022"
  FullyConstrained = true
  sketch-geometry (6):
    g0: LineSegment StartX=19 StartY=38 StartZ=0 EndX=117 EndY=38 EndZ=0
    g1: ArcOfCircle CenterX=19 CenterY=19 CenterZ=0 NormalX=0 NormalY=0 NormalZ=1 AngleXU=0 Radius=19 StartAngle=1.5708 EndAngle=3.14159
    g2: LineSegment StartX=117 StartY=38 StartZ=0 EndX=117 EndY=19 EndZ=0
    g3: LineSegment StartX=98 StartY=1.0161e-12 StartZ=0 EndX=5.22862e-06 EndY=1.0161e-12 EndZ=0
    g4: LineSegment StartX=5.22862e-06 StartY=19 StartZ=0 EndX=5.22862e-06 EndY=1.0161e-12 EndZ=0
    g5: ArcOfCircle CenterX=98 CenterY=19 CenterZ=0 NormalX=0 NormalY=0 NormalZ=1 AngleXU=0 Radius=19 StartAngle=4.71239 EndAngle=6.28319
  constraints (16):
    c: Horizontal(g0)
    c: Distance(g0) = 98
    c: Coincident(g1,g0)
    c: Block(g1)
    c: Coincident(g2,g0)
    c: Vertical(g2)
    c: Distance(g2) = 19
    c: Horizontal(g3)
    c: Coincident(g4,g1)
    c: Vertical(g4)
    c: Coincident(g3,g4)
    c: Block(g3)
    c: Coincident(g5,g2)
    c: Coincident(g5,g3)
    c: Block(g0)
    c: Block(g5)
FEATURE [Part::Extrusion] Extrude067  label="sideB003"
  Base = -> Sketch075
  Dir = (0,0,1)
  DirMode = 2
  FaceMakerClass = Part::FaceMakerBullseye
  LengthFwd = 3
  LengthRev = 0
  Placement = pos=(0,0,71.7) rot=(0,0,1;0rad)
  Solid = true
  Symmetric = false
FEATURE [Sketcher::SketchObject] Sketch076  label="topSketch023"
  FullyConstrained = true
  sketch-geometry (6):
    g0: LineSegment StartX=19 StartY=38 StartZ=0 EndX=117 EndY=38 EndZ=0
    g1: ArcOfCircle CenterX=19 CenterY=19 CenterZ=0 NormalX=0 NormalY=0 NormalZ=1 AngleXU=0 Radius=19 StartAngle=1.5708 EndAngle=3.14159
    g2: LineSegment StartX=117 StartY=38 StartZ=0 EndX=117 EndY=19 EndZ=0
    g3: LineSegment StartX=98 StartY=1.0161e-12 StartZ=0 EndX=5.22862e-06 EndY=1.0161e-12 EndZ=0
    g4: LineSegment StartX=5.22862e-06 StartY=19 StartZ=0 EndX=5.22862e-06 EndY=1.0161e-12 EndZ=0
    g5: ArcOfCircle CenterX=98 CenterY=19 CenterZ=0 NormalX=0 NormalY=0 NormalZ=1 AngleXU=0 Radius=19 StartAngle=4.71239 EndAngle=6.28319
  constraints (16):
    c: Horizontal(g0)
    c: Distance(g0) = 98
    c: Coincident(g1,g0)
    c: Block(g1)
    c: Coincident(g2,g0)
    c: Vertical(g2)
    c: Distance(g2) = 19
    c: Horizontal(g3)
    c: Coincident(g4,g1)
    c: Vertical(g4)
    c: Coincident(g3,g4)
    c: Block(g3)
    c: Coincident(g5,g2)
    c: Coincident(g5,g3)
    c: Block(g0)
    c: Block(g5)
FEATURE [Part::Extrusion] Extrude066  label="sideA003"
  Base = -> Sketch076
  Dir = (0,0,1)
  DirMode = 2
  FaceMakerClass = Part::FaceMakerBullseye
  LengthFwd = 3
  LengthRev = 0
  Placement = pos=(0,0,-2.7) rot=(0,0,1;0rad)
  Solid = true
  Symmetric = false
FEATURE [Part::MultiFuse] Fusion142  label="removeFromBottom003"
  Placement = pos=(2,0,0) rot=(0,0,1;0rad)
  Shapes = -> [Extrude066,Extrude067]
FEATURE [Part::Cut] Cut065  label="screwRetainers002"
  Base = -> Fusion096
  Tool = -> Fusion142
FEATURE [Sketcher::SketchObject] Sketch077
  FullyConstrained = true
  Placement = pos=(117,19,0) rot=(0.57735,0.57735,0.57735;2.0944rad)
  sketch-geometry (8):
    g0: LineSegment StartX=-49.19 StartY=63.5 StartZ=0 EndX=-49.19 EndY=60.5 EndZ=0
    g1: LineSegment StartX=-49.19 StartY=11.5 StartZ=0 EndX=-49.19 EndY=8.5 EndZ=0
    g2: ArcOfCircle CenterX=-1.5 CenterY=62 CenterZ=0 NormalX=0 NormalY=0 NormalZ=1 AngleXU=0 Radius=1.5 StartAngle=4.71239 EndAngle=7.85398
    g3: ArcOfCircle CenterX=-1.5 CenterY=10 CenterZ=0 NormalX=0 NormalY=0 NormalZ=1 AngleXU=0 Radius=1.5 StartAngle=4.71239 EndAngle=7.85398
    g4: LineSegment StartX=-49.19 StartY=63.5 StartZ=0 EndX=-1.5 EndY=63.5 EndZ=0
    g5: LineSegment StartX=-49.19 StartY=60.5 StartZ=0 EndX=-1.5 EndY=60.5 EndZ=0
    g6: LineSegment StartX=-49.19 StartY=11.5 StartZ=0 EndX=-1.5 EndY=11.5 EndZ=0
    g7: LineSegment StartX=-49.19 StartY=8.5 StartZ=0 EndX=-1.5 EndY=8.5 EndZ=0
  constraints (19):
    c: Vertical(g0)
    c: Distance(g0) = 3
    c: Vertical(g1)
    c: Block(g1)
    c: Block(g2)
    c: Block(g3)
    c: Block(g0)
    c: Coincident(g4,g0)
    c: Coincident(g4,g2)
    c: Horizontal(g4)
    c: Coincident(g5,g0)
    c: Coincident(g5,g2)
    c: Horizontal(g5)
    c: Coincident(g6,g1)
    c: Coincident(g6,g3)
    c: Horizontal(g6)
    c: Coincident(g7,g1)
    c: Coincident(g7,g3)
    c: Horizontal(g7)
FEATURE [Part::Extrusion] Extrude068
  Base = -> Sketch077
  Dir = (1,0,0)
  DirMode = 2
  FaceMakerClass = Part::FaceMakerBullseye
  LengthFwd = 10
  LengthRev = 0
  Solid = true
  Symmetric = false
FEATURE [Part::Fillet] Fillet057  label="removeFromtMoreFrontCaseScrewRetainers002"
  Base = -> Extrude068
  Edges = 4 edges r=1.49: [Edge6,Edge11,Edge18,Edge23]
  Placement = pos=(-12,0,0) rot=(0,0,1;0rad)
FEATURE [Sketcher::SketchObject] Sketch078
  FullyConstrained = true
  Placement = pos=(117,19,0) rot=(0.57735,0.57735,0.57735;2.0944rad)
  sketch-geometry (8):
    g0: LineSegment StartX=-49.19 StartY=69.25 StartZ=0 EndX=-49.19 EndY=66.25 EndZ=0
    g1: LineSegment StartX=-49.19 StartY=5.75 StartZ=0 EndX=-49.19 EndY=2.75 EndZ=0
    g2: ArcOfCircle CenterX=-1.5 CenterY=67.75 CenterZ=0 NormalX=0 NormalY=0 NormalZ=1 AngleXU=0 Radius=1.5 StartAngle=4.71239 EndAngle=7.85398
    g3: ArcOfCircle CenterX=-1.5 CenterY=4.25 CenterZ=0 NormalX=0 NormalY=0 NormalZ=1 AngleXU=0 Radius=1.5 StartAngle=4.71239 EndAngle=7.85398
    g4: LineSegment StartX=-49.19 StartY=69.25 StartZ=0 EndX=-1.5 EndY=69.25 EndZ=0
    g5: LineSegment StartX=-49.19 StartY=66.25 StartZ=0 EndX=-1.5 EndY=66.25 EndZ=0
    g6: LineSegment StartX=-49.19 StartY=5.75 StartZ=0 EndX=-1.5 EndY=5.75 EndZ=0
    g7: LineSegment StartX=-49.19 StartY=2.75 StartZ=0 EndX=-1.5 EndY=2.75 EndZ=0
  constraints (19):
    c: Vertical(g0)
    c: Distance(g0) = 3
    c: Block(g0)
    c: Vertical(g1)
    c: Block(g2)
    c: Block(g3)
    c: Block(g1)
    c: Coincident(g4,g0)
    c: Coincident(g4,g2)
    c: Horizontal(g4)
    c: Coincident(g5,g0)
    c: Coincident(g5,g2)
    c: Horizontal(g5)
    c: Coincident(g6,g1)
    c: Coincident(g6,g3)
    c: Horizontal(g6)
    c: Coincident(g7,g1)
    c: Coincident(g7,g3)
    c: Horizontal(g7)
FEATURE [Part::Extrusion] Extrude069
  Base = -> Sketch078
  Dir = (1,0,0)
  DirMode = 2
  FaceMakerClass = Part::FaceMakerBullseye
  LengthFwd = 10
  LengthRev = 0
  Solid = true
  Symmetric = false
FEATURE [Part::Fillet] Fillet058  label="removeFromtMoreFrontCaseScrewRetainers003"
  Base = -> Extrude069
  Edges = 4 edges r=1.49: [Edge6,Edge11,Edge18,Edge23]
  Placement = pos=(-4,0,0) rot=(0,0,1;0rad)
FEATURE [Part::Cut] Cut066
  Base = -> Cut065
  Tool = -> Fillet058
FEATURE [Part::Cut] Cut067  label="screwPillars"
  Base = -> Cut066
  Tool = -> Fillet057
FEATURE [Part::MultiFuse] Fusion143  label="bottom021"
  Shapes = -> [Cut031,Cut063]
FEATURE [Part::Cylinder] Cylinder
  Angle = 360
  AttacherType = Attacher::AttachEngine3D
  Height = 10
  Placement = pos=(20.65,12,4.68) rot=(1,0,0;1.5708rad)
  Radius = 2
FEATURE [Part::Cylinder] Cylinder064
  Angle = 360
  AttacherType = Attacher::AttachEngine3D
  Height = 10
  Placement = pos=(20.65,12,67.38) rot=(1,0,0;1.5708rad)
  Radius = 2
FEATURE [Part::Cylinder] Cylinder065
  Angle = 360
  AttacherType = Attacher::AttachEngine3D
  Height = 10
  Placement = pos=(77.15,12,67.38) rot=(1,0,0;1.5708rad)
  Radius = 2
FEATURE [Part::Cylinder] Cylinder066
  Angle = 360
  AttacherType = Attacher::AttachEngine3D
  Height = 10
  Placement = pos=(77.15,12,4.68) rot=(1,0,0;1.5708rad)
  Radius = 2
FEATURE [Part::MultiFuse] Fusion144  label="removeFromThreadedInsertHousing"
  Shapes = -> [Cylinder065,Cylinder064,Cylinder,Cylinder066]
FEATURE [Part::Cut] Cut068  label="pcbStands001"
  Base = -> Cut064
  Tool = -> Fusion144
FEATURE [Part::MultiFuse] Fusion145
  Shapes = -> [Cut068,Fusion143]
FEATURE [Part::MultiFuse] Fusion146
  Shapes = -> [Fusion145]
FEATURE [Part::MultiFuse] Fusion147  label="bottom022"
  Shapes = -> [Cut067,Fusion146]
FEATURE [Part::MultiFuse] Fusion148  label="casePillars005"
  Shapes = -> [Cut047,Fusion092]
FEATURE [Part::MultiFuse] Fusion149  label="bottom023"
  Shapes = -> [Fusion124,Fusion113,Fusion147]
FEATURE [Part::MultiFuse] Fusion150  label="topBits"
  Shapes = -> [Cut025,Fusion148,Cut030,Fillet034]
FEATURE [Part::Feature] Face149 .. Face152  x4 (patterned run collapsed; names and placements below)
  shape: bbox 3.2 x 1.5 x 2e-07 mm, 1 faces, 0 solids (baked)
FEATURE [Part::Feature] Face153
  shape: bbox 3.6 x 3.2 x 2e-07 mm, 1 faces, 0 solids (baked)
FEATURE [Part::Feature] Face154
  shape: bbox 3.6 x 3.2 x 2e-07 mm, 1 faces, 0 solids (baked)
FEATURE [Sketcher::SketchObject] Sketch079  label="topSketch024"
  FullyConstrained = true
  sketch-geometry (6):
    g0: LineSegment StartX=19 StartY=38 StartZ=0 EndX=117 EndY=38 EndZ=0
    g1: ArcOfCircle CenterX=19 CenterY=19 CenterZ=0 NormalX=0 NormalY=0 NormalZ=1 AngleXU=0 Radius=19 StartAngle=1.5708 EndAngle=3.14159
    g2: LineSegment StartX=117 StartY=38 StartZ=0 EndX=117 EndY=19 EndZ=0
    g3: LineSegment StartX=98 StartY=1.0161e-12 StartZ=0 EndX=5.22862e-06 EndY=1.0161e-12 EndZ=0
    g4: LineSegment StartX=5.22862e-06 StartY=19 StartZ=0 EndX=5.22862e-06 EndY=1.0161e-12 EndZ=0
    g5: ArcOfCircle CenterX=98 CenterY=19 CenterZ=0 NormalX=0 NormalY=0 NormalZ=1 AngleXU=0 Radius=19 StartAngle=4.71239 EndAngle=6.28319
  constraints (16):
    c: Horizontal(g0)
    c: Distance(g0) = 98
    c: Coincident(g1,g0)
    c: Block(g1)
    c: Coincident(g2,g0)
    c: Vertical(g2)
    c: Distance(g2) = 19
    c: Horizontal(g3)
    c: Coincident(g4,g1)
    c: Vertical(g4)
    c: Coincident(g3,g4)
    c: Block(g3)
    c: Coincident(g5,g2)
    c: Coincident(g5,g3)
    c: Block(g0)
    c: Block(g5)
FEATURE [Sketcher::SketchObject] Sketch080  label="topSketch025"
  FullyConstrained = true
  sketch-geometry (6):
    g0: LineSegment StartX=19 StartY=38 StartZ=0 EndX=117 EndY=38 EndZ=0
    g1: ArcOfCircle CenterX=19 CenterY=19 CenterZ=0 NormalX=0 NormalY=0 NormalZ=1 AngleXU=0 Radius=19 StartAngle=1.5708 EndAngle=3.14159
    g2: LineSegment StartX=117 StartY=38 StartZ=0 EndX=117 EndY=19 EndZ=0
    g3: LineSegment StartX=98 StartY=1.0161e-12 StartZ=0 EndX=5.22862e-06 EndY=1.0161e-12 EndZ=0
    g4: LineSegment StartX=5.22862e-06 StartY=19 StartZ=0 EndX=5.22862e-06 EndY=1.0161e-12 EndZ=0
    g5: ArcOfCircle CenterX=98 CenterY=19 CenterZ=0 NormalX=0 NormalY=0 NormalZ=1 AngleXU=0 Radius=19 StartAngle=4.71239 EndAngle=6.28319
  constraints (16):
    c: Horizontal(g0)
    c: Distance(g0) = 98
    c: Coincident(g1,g0)
    c: Block(g1)
    c: Coincident(g2,g0)
    c: Vertical(g2)
    c: Distance(g2) = 19
    c: Horizontal(g3)
    c: Coincident(g4,g1)
    c: Vertical(g4)
    c: Coincident(g3,g4)
    c: Block(g3)
    c: Coincident(g5,g2)
    c: Coincident(g5,g3)
    c: Block(g0)
    c: Block(g5)
FEATURE [Part::Extrusion] Extrude070  label="sideA004"
  Base = -> Sketch080
  Dir = (0,0,1)
  DirMode = 2
  FaceMakerClass = Part::FaceMakerBullseye
  LengthFwd = 3
  LengthRev = 0
  Placement = pos=(0,0,-2.7) rot=(0,0,1;0rad)
  Solid = true
  Symmetric = false
FEATURE [Sketcher::SketchObject] Sketch081
  FullyConstrained = true
  Placement = pos=(117,19,0) rot=(0.57735,0.57735,0.57735;2.0944rad)
  sketch-geometry (8):
    g0: LineSegment StartX=-49.19 StartY=63.5 StartZ=0 EndX=-49.19 EndY=60.5 EndZ=0
    g1: LineSegment StartX=-49.19 StartY=11.5 StartZ=0 EndX=-49.19 EndY=8.5 EndZ=0
    g2: ArcOfCircle CenterX=-1.5 CenterY=62 CenterZ=0 NormalX=0 NormalY=0 NormalZ=1 AngleXU=0 Radius=1.5 StartAngle=4.71239 EndAngle=7.85398
    g3: ArcOfCircle CenterX=-1.5 CenterY=10 CenterZ=0 NormalX=0 NormalY=0 NormalZ=1 AngleXU=0 Radius=1.5 StartAngle=4.71239 EndAngle=7.85398
    g4: LineSegment StartX=-49.19 StartY=63.5 StartZ=0 EndX=-1.5 EndY=63.5 EndZ=0
    g5: LineSegment StartX=-49.19 StartY=60.5 StartZ=0 EndX=-1.5 EndY=60.5 EndZ=0
    g6: LineSegment StartX=-49.19 StartY=11.5 StartZ=0 EndX=-1.5 EndY=11.5 EndZ=0
    g7: LineSegment StartX=-49.19 StartY=8.5 StartZ=0 EndX=-1.5 EndY=8.5 EndZ=0
  constraints (19):
    c: Vertical(g0)
    c: Distance(g0) = 3
    c: Vertical(g1)
    c: Block(g1)
    c: Block(g2)
    c: Block(g3)
    c: Block(g0)
    c: Coincident(g4,g0)
    c: Coincident(g4,g2)
    c: Horizontal(g4)
    c: Coincident(g5,g0)
    c: Coincident(g5,g2)
    c: Horizontal(g5)
    c: Coincident(g6,g1)
    c: Coincident(g6,g3)
    c: Horizontal(g6)
    c: Coincident(g7,g1)
    c: Coincident(g7,g3)
    c: Horizontal(g7)
FEATURE [Part::Extrusion] Extrude071  label="sideB004"
  Base = -> Sketch079
  Dir = (0,0,1)
  DirMode = 2
  FaceMakerClass = Part::FaceMakerBullseye
  LengthFwd = 3
  LengthRev = 0
  Placement = pos=(0,0,71.7) rot=(0,0,1;0rad)
  Solid = true
  Symmetric = false
FEATURE [Part::MultiFuse] Fusion152  label="removeFromBottom004"
  Placement = pos=(2,0,0) rot=(0,0,1;0rad)
  Shapes = -> [Extrude070,Extrude071]
FEATURE [Part::Extrusion] Extrude072
  Base = -> Sketch081
  Dir = (1,0,0)
  DirMode = 2
  FaceMakerClass = Part::FaceMakerBullseye
  LengthFwd = 10
  LengthRev = 0
  Solid = true
  Symmetric = false
FEATURE [Part::Fillet] Fillet059  label="removeFromtMoreFrontCaseScrewRetainers004"
  Base = -> Extrude072
  Edges = 4 edges r=1.49: [Edge6,Edge11,Edge18,Edge23]
  Placement = pos=(-12,0,0) rot=(0,0,1;0rad)
FEATURE [Sketcher::SketchObject] Sketch082
  FullyConstrained = true
  Placement = pos=(117,19,0) rot=(0.57735,0.57735,0.57735;2.0944rad)
  sketch-geometry (8):
    g0: LineSegment StartX=-49.19 StartY=69.25 StartZ=0 EndX=-49.19 EndY=66.25 EndZ=0
    g1: LineSegment StartX=-49.19 StartY=5.75 StartZ=0 EndX=-49.19 EndY=2.75 EndZ=0
    g2: ArcOfCircle CenterX=-1.5 CenterY=67.75 CenterZ=0 NormalX=0 NormalY=0 NormalZ=1 AngleXU=0 Radius=1.5 StartAngle=4.71239 EndAngle=7.85398
    g3: ArcOfCircle CenterX=-1.5 CenterY=4.25 CenterZ=0 NormalX=0 NormalY=0 NormalZ=1 AngleXU=0 Radius=1.5 StartAngle=4.71239 EndAngle=7.85398
    g4: LineSegment StartX=-49.19 StartY=69.25 StartZ=0 EndX=-1.5 EndY=69.25 EndZ=0
    g5: LineSegment StartX=-49.19 StartY=66.25 StartZ=0 EndX=-1.5 EndY=66.25 EndZ=0
    g6: LineSegment StartX=-49.19 StartY=5.75 StartZ=0 EndX=-1.5 EndY=5.75 EndZ=0
    g7: LineSegment StartX=-49.19 StartY=2.75 StartZ=0 EndX=-1.5 EndY=2.75 EndZ=0
  constraints (19):
    c: Vertical(g0)
    c: Distance(g0) = 3
    c: Block(g0)
    c: Vertical(g1)
    c: Block(g2)
    c: Block(g3)
    c: Block(g1)
    c: Coincident(g4,g0)
    c: Coincident(g4,g2)
    c: Horizontal(g4)
    c: Coincident(g5,g0)
    c: Coincident(g5,g2)
    c: Horizontal(g5)
    c: Coincident(g6,g1)
    c: Coincident(g6,g3)
    c: Horizontal(g6)
    c: Coincident(g7,g1)
    c: Coincident(g7,g3)
    c: Horizontal(g7)
FEATURE [Part::Extrusion] Extrude073
  Base = -> Sketch082
  Dir = (1,0,0)
  DirMode = 2
  FaceMakerClass = Part::FaceMakerBullseye
  LengthFwd = 10
  LengthRev = 0
  Solid = true
  Symmetric = false
FEATURE [Part::Fillet] Fillet060  label="removeFromtMoreFrontCaseScrewRetainers005"
  Base = -> Extrude073
  Edges = 4 edges r=1.49: [Edge6,Edge11,Edge18,Edge23]
  Placement = pos=(-4,0,0) rot=(0,0,1;0rad)
FEATURE [Part::Revolution] Revolve163  label="backCaseScrewRetainer004"
  Angle = 360
  Axis = (0,1,0)
  Base = (0,0,0)
  FaceMakerClass = Part::FaceMakerBullseye
  Placement = pos=(12.5,3,62) rot=(0,0,1;0rad)
  Solid = false
  Source = -> Face149
  Symmetric = false
FEATURE [Part::Revolution] Revolve164  label="frontCaseScrewRetainer006"
  Angle = 360
  Axis = (0,1,0)
  Base = (0,0,0)
  FaceMakerClass = Part::FaceMakerBullseye
  Placement = pos=(89.5,3,68.5) rot=(0,0,1;0rad)
  Solid = false
  Source = -> Face151
  Symmetric = false
FEATURE [Part::Revolution] Revolve165  label="frontCaseScrewRetainer007"
  Angle = 360
  Axis = (0,1,0)
  Base = (0,0,0)
  FaceMakerClass = Part::FaceMakerBullseye
  Placement = pos=(89.5,3,3.5) rot=(0,0,1;0rad)
  Solid = false
  Source = -> Face152
  Symmetric = false
FEATURE [Part::Revolution] Revolve166  label="backCaseScrewRetainer005"
  Angle = 360
  Axis = (0,1,0)
  Base = (0,0,0)
  FaceMakerClass = Part::FaceMakerBullseye
  Placement = pos=(12.5,3,10) rot=(0,0,1;0rad)
  Solid = false
  Source = -> Face150
  Symmetric = false
FEATURE [Part::Revolution] Revolve167  label="moreFrontCaseScrewRetainer006"
  Angle = 360
  Axis = (0,1,0)
  Base = (0,0,0)
  FaceMakerClass = Part::FaceMakerBullseye
  Placement = pos=(109.5,4.5,68.5) rot=(0,0,1;0rad)
  Solid = false
  Source = -> Face153
  Symmetric = false
FEATURE [Part::Revolution] Revolve168  label="moreFrontCaseScrewRetainer007"
  Angle = 360
  Axis = (0,1,0)
  Base = (0,0,0)
  FaceMakerClass = Part::FaceMakerBullseye
  Placement = pos=(109.5,4.5,3.5) rot=(0,0,1;0rad)
  Solid = false
  Source = -> Face154
  Symmetric = false
FEATURE [Part::MultiFuse] Fusion151  label="screwRetainers003"
  Shapes = -> [Revolve168,Revolve167,Revolve166,Revolve165,Revolve164,Revolve163]
FEATURE [Part::Cut] Cut069  label="screwRetainers004"
  Base = -> Fusion151
  Tool = -> Fusion152
FEATURE [Part::Cut] Cut070
  Base = -> Cut069
  Tool = -> Fillet060
FEATURE [Part::Cut] Cut071  label="screwPillars001"
  Base = -> Cut070
  Tool = -> Fillet059
FEATURE [Part::MultiFuse] Fusion153  label="bottom024"
  Shapes = -> [Fusion149,Cut071]
FEATURE [Part::Cylinder] Cylinder067
  Angle = 360
  AttacherType = Attacher::AttachEngine3D
  Height = 10
  Placement = pos=(20.65,12,4.68) rot=(1,0,0;1.5708rad)
  Radius = 2
FEATURE [Part::Cylinder] Cylinder068
  Angle = 360
  AttacherType = Attacher::AttachEngine3D
  Height = 10
  Placement = pos=(20.65,12,67.38) rot=(1,0,0;1.5708rad)
  Radius = 2
FEATURE [Part::Cylinder] Cylinder069
  Angle = 360
  AttacherType = Attacher::AttachEngine3D
  Height = 10
  Placement = pos=(77.15,12,67.38) rot=(1,0,0;1.5708rad)
  Radius = 2
FEATURE [Part::Cylinder] Cylinder070
  Angle = 360
  AttacherType = Attacher::AttachEngine3D
  Height = 10
  Placement = pos=(77.15,12,4.68) rot=(1,0,0;1.5708rad)
  Radius = 2
FEATURE [Part::MultiFuse] Fusion154  label="removeFromThreadedInsertHousing001"
  Shapes = -> [Cylinder069,Cylinder068,Cylinder067,Cylinder070]
FEATURE [Part::Cut] Cut072  label="bottom025"
  Base = -> Fusion153
  Tool = -> Fusion154
FEATURE [Image::ImagePlane] ImagePlane
  XSize = 339
  YSize = 72
FEATURE [Sketcher::SketchObject] Sketch083
  FullyConstrained = true
  MapMode = 5
  Support = -> [XY_Plane]
  sketch-geometry (294):
    g0: LineSegment StartX=-151.619 StartY=28.8932 StartZ=0 EndX=-140.819 EndY=28.8932 EndZ=0
    g1: LineSegment StartX=-151.619 StartY=24.0313 StartZ=0 EndX=-151.619 EndY=28.8932 EndZ=0
    g2: LineSegment StartX=-140.819 StartY=17.7713 StartZ=0 EndX=-151.619 EndY=17.7713 EndZ=0
    g3: LineSegment StartX=-151.619 StartY=17.7713 StartZ=0 EndX=-151.619 EndY=22.6313 EndZ=0
    g4: LineSegment StartX=-151.619 StartY=22.6313 StartZ=0 EndX=-145.128 EndY=22.6313 EndZ=0
    g5: LineSegment StartX=-145.128 StartY=24.0313 StartZ=0 EndX=-140.819 EndY=28.8932 EndZ=0
    g6: LineSegment StartX=-145.128 StartY=22.6313 StartZ=0 EndX=-140.819 EndY=17.7713 EndZ=0
    g7: ArcOfCircle CenterX=-155.157 CenterY=23.3323 CenterZ=0 NormalX=0 NormalY=0 NormalZ=1 AngleXU=0 Radius=6.92354 StartAngle=1.03434 EndAngle=5.24885
    g8: ArcOfCircle CenterX=-155.157 CenterY=23.3323 CenterZ=0 NormalX=0 NormalY=0 NormalZ=1 AngleXU=0 Radius=12.6269 StartAngle=1.28675 EndAngle=4.99643
    g9: LineSegment StartX=-151.619 StartY=35.4532 StartZ=0 EndX=-151.619 EndY=29.2832 EndZ=0
    g10: LineSegment StartX=-151.619 StartY=17.3813 StartZ=0 EndX=-151.619 EndY=11.2113 EndZ=0
    g11-g21: Circle x11 (B-spline internal-alignment scaffolding for g22; pole/knot coordinates omitted)
    g22: BSplineCurve PolesCount=11 KnotsCount=9 Degree=3 IsPeriodic=0
    g23-g31: GeomPoint x9 (B-spline internal-alignment scaffolding for g22; pole/knot coordinates omitted)
    g32-g49: Circle x18 (B-spline internal-alignment scaffolding for g50; pole/knot coordinates omitted)
    g50: BSplineCurve PolesCount=18 KnotsCount=16 Degree=3 IsPeriodic=0
    g51-g66: GeomPoint x16 (B-spline internal-alignment scaffolding for g50; pole/knot coordinates omitted)
    g67: LineSegment StartX=-117.124 StartY=30.093 StartZ=0 EndX=-117.603 EndY=26.5272 EndZ=0
    g68: LineSegment StartX=-117.603 StartY=17.8472 StartZ=0 EndX=-117.124 EndY=14.2659 EndZ=0
    g69: Ellipse CenterX=-109.671 CenterY=20.025 CenterZ=0 NormalX=0 NormalY=0 NormalZ=1 MajorRadius=3.34798 MinorRadius=2.71052 AngleXU=-1.56793
    g70: GeomPoint X=-109.666 Y=18.0598 Z=0
    g71: GeomPoint X=-109.677 Y=21.9902 Z=0
    g72: Ellipse CenterX=-109.671 CenterY=20.0123 CenterZ=0 NormalX=0 NormalY=0 NormalZ=1 MajorRadius=6.93002 MinorRadius=6.36273 AngleXU=-3.13976
    g73: GeomPoint X=-112.417 Y=20.0073 Z=0
    g74: GeomPoint X=-106.925 Y=20.0173 Z=0
    g75: Ellipse CenterX=-51.7682 CenterY=20.1463 CenterZ=0 NormalX=0 NormalY=0 NormalZ=1 MajorRadius=3.19279 MinorRadius=2.71052 AngleXU=-1.52774
    g76: GeomPoint X=-51.6955 Y=18.4606 Z=0
    g77: GeomPoint X=-51.8408 Y=21.832 Z=0
    g78: GeomPoint X=-54.5142 Y=20.1413 Z=0
    g79: GeomPoint X=-49.0221 Y=20.1513 Z=0
    g80: Ellipse CenterX=-51.7682 CenterY=20.1463 CenterZ=0 NormalX=0 NormalY=0 NormalZ=1 MajorRadius=6.93002 MinorRadius=6.36273 AngleXU=-3.13976
    g81: Ellipse CenterX=-22.8436 CenterY=20.1783 CenterZ=0 NormalX=0 NormalY=0 NormalZ=1 MajorRadius=3.31512 MinorRadius=2.71052 AngleXU=-1.60214
    g82: GeomPoint X=-22.9034 Y=18.2706 Z=0
    g83: GeomPoint X=-22.7838 Y=22.0861 Z=0
    g84: GeomPoint X=-25.5897 Y=20.1733 Z=0
    g85: GeomPoint X=-20.0976 Y=20.1833 Z=0
    g86: Ellipse CenterX=-22.8436 CenterY=20.1783 CenterZ=0 NormalX=0 NormalY=0 NormalZ=1 MajorRadius=6.93002 MinorRadius=6.36273 AngleXU=-3.13976
    g87: LineSegment StartX=-101.889 StartY=14.1107 StartZ=0 EndX=-97.7455 EndY=14.1107 EndZ=0
    g88: LineSegment StartX=-93.8155 StartY=14.1107 StartZ=0 EndX=-89.6755 EndY=14.1107 EndZ=0
    g89: LineSegment StartX=-85.7455 StartY=14.1107 StartZ=0 EndX=-81.6055 EndY=14.1107 EndZ=0
    g90: LineSegment StartX=-101.889 StartY=14.1107 StartZ=0 EndX=-101.889 EndY=25.9907 EndZ=0
    g91: LineSegment StartX=-101.889 StartY=25.9907 StartZ=0 EndX=-97.8594 EndY=25.9907 EndZ=0
    g92: LineSegment StartX=-97.8594 StartY=25.9907 StartZ=0 EndX=-97.8594 EndY=24.0907 EndZ=0
    g93: LineSegment StartX=-97.7455 StartY=14.1107 StartZ=0 EndX=-97.7455 EndY=19.9107 EndZ=0
    g94: LineSegment StartX=-89.6755 StartY=14.1107 StartZ=0 EndX=-89.6755 EndY=19.9107 EndZ=0
    g95: LineSegment StartX=-93.8155 StartY=14.1107 StartZ=0 EndX=-93.8155 EndY=21.0107 EndZ=0
    g96-g106: Circle x11 (B-spline internal-alignment scaffolding for g107; pole/knot coordinates omitted)
    g107: BSplineCurve PolesCount=11 KnotsCount=9 Degree=3 IsPeriodic=0
    g108-g116: GeomPoint x9 (B-spline internal-alignment scaffolding for g107; pole/knot coordinates omitted)
    g117: BSplineCurve PolesCount=11 KnotsCount=9 Degree=3 IsPeriodic=0
    g118-g125: Circle x8 (B-spline internal-alignment scaffolding for g126; pole/knot coordinates omitted)
    g126: BSplineCurve PolesCount=8 KnotsCount=6 Degree=3 IsPeriodic=0
    g127-g132: GeomPoint x6 (B-spline internal-alignment scaffolding for g126; pole/knot coordinates omitted)
    g133: BSplineCurve PolesCount=8 KnotsCount=6 Degree=3 IsPeriodic=0
    g134: LineSegment StartX=-85.7455 StartY=21.0107 StartZ=0 EndX=-85.7455 EndY=14.1107 EndZ=0
    g135: LineSegment StartX=-80.0879 StartY=14.1107 StartZ=0 EndX=-75.944 EndY=14.1107 EndZ=0
    g136: LineSegment StartX=-72.014 StartY=14.1107 StartZ=0 EndX=-67.874 EndY=14.1107 EndZ=0
    g137: LineSegment StartX=-63.944 StartY=14.1107 StartZ=0 EndX=-59.804 EndY=14.1107 EndZ=0
    g138: LineSegment StartX=-80.0879 StartY=14.1107 StartZ=0 EndX=-80.0879 EndY=25.9907 EndZ=0
    g139: LineSegment StartX=-80.0879 StartY=25.9907 StartZ=0 EndX=-76.0579 EndY=25.9907 EndZ=0
    g140: LineSegment StartX=-76.0579 StartY=25.9907 StartZ=0 EndX=-76.0579 EndY=24.0907 EndZ=0
    g141: LineSegment StartX=-75.944 StartY=14.1107 StartZ=0 EndX=-75.944 EndY=19.9107 EndZ=0
    g142: LineSegment StartX=-67.874 StartY=14.1107 StartZ=0 EndX=-67.874 EndY=19.9107 EndZ=0
    g143: LineSegment StartX=-72.014 StartY=14.1107 StartZ=0 EndX=-72.014 EndY=21.0107 EndZ=0
    g144-g148: Circle x5 (B-spline internal-alignment scaffolding for g149; pole/knot coordinates omitted)
    g149: BSplineCurve PolesCount=11 KnotsCount=9 Degree=3 IsPeriodic=0
    g150-g158: GeomPoint x9 (B-spline internal-alignment scaffolding for g149; pole/knot coordinates omitted)
    g159: BSplineCurve PolesCount=11 KnotsCount=9 Degree=3 IsPeriodic=0
    g160-g167: Circle x8 (B-spline internal-alignment scaffolding for g168; pole/knot coordinates omitted)
    g168: BSplineCurve PolesCount=8 KnotsCount=6 Degree=3 IsPeriodic=0
    g169-g174: GeomPoint x6 (B-spline internal-alignment scaffolding for g168; pole/knot coordinates omitted)
    g175: BSplineCurve PolesCount=8 KnotsCount=6 Degree=3 IsPeriodic=0
    g176: LineSegment StartX=-63.944 StartY=21.0107 StartZ=0 EndX=-63.944 EndY=14.1107 EndZ=0
    g177: LineSegment StartX=-59.804 StartY=14.1107 StartZ=0 EndX=-59.804 EndY=21.5868 EndZ=0
    g178: BSplineCurve PolesCount=4 KnotsCount=2 Degree=3 IsPeriodic=0
    g179: GeomPoint X=-59.804 Y=21.5868 Z=0
    g180: GeomPoint X=-60.2379 Y=24.0907 Z=0
    g181: LineSegment StartX=-81.6055 StartY=14.1107 StartZ=0 EndX=-81.6055 EndY=21.5868 EndZ=0
    g182: LineSegment StartX=-151.619 StartY=24.0313 StartZ=0 EndX=-145.128 EndY=24.0313 EndZ=0
    g183: Circle CenterX=-82.0394 CenterY=24.0907 CenterZ=0 NormalX=0 NormalY=0 NormalZ=1 AngleXU=0 Radius=1
    g184: Circle CenterX=-81.7131 CenterY=23.2736 CenterZ=0 NormalX=0 NormalY=0 NormalZ=1 AngleXU=0 Radius=1
    g185: Circle CenterX=-81.6055 CenterY=21.5868 CenterZ=0 NormalX=0 NormalY=0 NormalZ=1 AngleXU=0 Radius=1
    g186: BSplineCurve PolesCount=3 KnotsCount=2 Degree=2 IsPeriodic=0
    g187: GeomPoint X=-82.0394 Y=24.0907 Z=0
    g188: GeomPoint X=-81.6055 Y=21.5868 Z=0
    g189: Ellipse CenterX=-37.3522 CenterY=19.9515 CenterZ=0 NormalX=0 NormalY=0 NormalZ=1 MajorRadius=2.99755 MinorRadius=2.49 AngleXU=1.5708
    g190: GeomPoint X=-37.3522 Y=21.6203 Z=0
    g191: GeomPoint X=-37.3522 Y=18.2826 Z=0
    g192: ArcOfEllipse CenterX=-38.7647 CenterY=20.06 CenterZ=0 NormalX=0 NormalY=0 NormalZ=1 MajorRadius=6.30025 MinorRadius=5.3849 AngleXU=1.57276 StartAngle=5.50632 EndAngle=10.3035
    g193: GeomPoint X=-38.7711 Y=23.3304 Z=0
    g194: GeomPoint X=-38.7583 Y=16.7895 Z=0
    g195: LineSegment StartX=-34.6109 StartY=14.1107 StartZ=0 EndX=-30.8984 EndY=14.1107 EndZ=0
    g196: LineSegment StartX=-30.8984 StartY=14.1107 StartZ=0 EndX=-30.8984 EndY=31.1784 EndZ=0
    g197: LineSegment StartX=-30.8984 StartY=31.1784 StartZ=0 EndX=-34.9984 EndY=31.1784 EndZ=0
    g198: LineSegment StartX=-34.9984 StartY=24.5602 StartZ=0 EndX=-34.9984 EndY=31.1784 EndZ=0
    g199: LineSegment StartX=-34.6109 StartY=16.0476 StartZ=0 EndX=-34.6109 EndY=14.1107 EndZ=0
    g200: LineSegment StartX=-14.8781 StartY=14.1107 StartZ=0 EndX=-10.5106 EndY=14.1107 EndZ=0
    g201: LineSegment StartX=-14.8781 StartY=14.1107 StartZ=0 EndX=-14.8781 EndY=25.8504 EndZ=0
    g202: LineSegment StartX=-14.8781 StartY=25.8504 StartZ=0 EndX=-10.8534 EndY=25.8504 EndZ=0
    g203: LineSegment StartX=-10.8534 StartY=25.8504 StartZ=0 EndX=-10.8534 EndY=24.0923 EndZ=0
    g204: LineSegment StartX=-10.5106 StartY=14.1107 StartZ=0 EndX=-10.5106 EndY=19.7752 EndZ=0
    g205: LineSegment StartX=-5.96397 StartY=25.9304 StartZ=0 EndX=-5.96397 EndY=22.574 EndZ=0
    g206-g214: Circle x9 (B-spline internal-alignment scaffolding for g215; pole/knot coordinates omitted)
    g215: BSplineCurve PolesCount=9 KnotsCount=7 Degree=3 IsPeriodic=0
    g216-g222: GeomPoint x7 (B-spline internal-alignment scaffolding for g215; pole/knot coordinates omitted)
    g223-g232: Circle x10 (B-spline internal-alignment scaffolding for g233; pole/knot coordinates omitted)
    g233: BSplineCurve PolesCount=10 KnotsCount=8 Degree=3 IsPeriodic=0
    g234-g241: GeomPoint x8 (B-spline internal-alignment scaffolding for g233; pole/knot coordinates omitted)
    g242: LineSegment StartX=-1.58923 StartY=21.0696 StartZ=0 EndX=2.62034 EndY=21.0696 EndZ=0
    g243: LineSegment StartX=-1.55856 StartY=18.7342 StartZ=0 EndX=6.45946 EndY=18.7342 EndZ=0
    g244: LineSegment StartX=5.29231 StartY=17.386 StartZ=0 EndX=5.29231 EndY=14.3674 EndZ=0
    g245-g269: Circle x25 (B-spline internal-alignment scaffolding for g270; pole/knot coordinates omitted)
    g270: BSplineCurve PolesCount=25 KnotsCount=23 Degree=3 IsPeriodic=0
    g271-g293: GeomPoint x23 (B-spline internal-alignment scaffolding for g270; pole/knot coordinates omitted)
  constraints (238):
    c: Coincident(g1,g0)
    c: Horizontal(g0)
    c: Vertical(g1)
    c: Coincident(g2,g3)
    c: Coincident(g3,g4)
    c: Horizontal(g4)
    c: Horizontal(g2)
    c: Vertical(g3)
    c: Block(g1)
    c: Distance(g3) = 4.86
    c: Block(g4)
    c: Distance(g0) = 10.8
    c: Distance(g2) = 10.8
    c: Coincident(g5,g0)
    c: Coincident(g6,g4)
    c: Coincident(g6,g2)
    c: Block(g8)
    c: Block(g7)
    c: Coincident(g9,g8)
    c: Coincident(g9,g7)
    c: Vertical(g9)
    c: Coincident(g10,g7)
    c: Coincident(g10,g8)
    c: Vertical(g10)
    c: Weight(g11) = 1
    c: Equal(g11, g12-g21) x10
    c: InternalAlignment(g11-g21 -> g22) x11
    c: InternalAlignment(g23-g31 -> g22) x9
    c: Block(g22)
    c: Weight(g32) = 1
    c: Equal(g32, g33-g49) x17
    c: InternalAlignment(g32-g49 -> g50) x18
    c: InternalAlignment(g51-g66 -> g50) x16
    c: Block(g50)
    c: Coincident(g67,g50)
    c: Coincident(g67,g22)
    c: Coincident(g68,g22)
    c: Coincident(g68,g50)
    c: InternalAlignment(g70,g69)
    c: InternalAlignment(g71,g69)
    c: Block(g69)
    c: InternalAlignment(g73,g72)
    c: InternalAlignment(g74,g72)
    c: Block(g72)
    c: InternalAlignment(g76,g75)
    c: InternalAlignment(g77,g75)
    c: InternalAlignment(g78,g80)
    c: InternalAlignment(g79,g80)
    c: Block(g80)
    c: Coincident(g75,g80)
    c: Block(g75)
    c: InternalAlignment(g82,g81)
    c: InternalAlignment(g83,g81)
    c: InternalAlignment(g84,g86)
    c: InternalAlignment(g85,g86)
    c: Block(g86)
    c: Coincident(g81,g86)
    c: Block(g81)
    c: Horizontal(g87)
    c: Block(g87)
    c: Horizontal(g88)
    c: Distance(g88) = 4.14
    c: Horizontal(g89)
    c: Equal(g88,g89) = 4.14
    c: Block(g89)
    c: Block(g88)
    c: Coincident(g90,g87)
    c: Vertical(g90)
    c: Distance(g90) = 11.88
    c: Coincident(g91,g90)
    c: Horizontal(g91)
    c: Coincident(g92,g91)
    c: Vertical(g92)
    c: Distance(g91) = 4.03
    c: Distance(g92) = 1.9
    c: Coincident(g93,g87)
    c: Vertical(g93)
    c: Vertical(g94)
    c: Coincident(g94,g88)
    c: Distance(g93) = 5.8
    c: Distance(g94) = 5.8
    c: Vertical(g95)
    c: Coincident(g95,g88)
    c: Distance(g95) = 6.9
    c: Coincident(g107,g92)
    c: Weight(g96) = 1
    c: Equal(g96, g97-g106) x10
    c: InternalAlignment(g96-g106 -> g107) x11
    c: InternalAlignment(g108-g116 -> g107) x9
    c: Block(g107)
    c: Block(g117)
    c: Coincident(g126,g93)
    c: Weight(g118) = 1
    c: Equal(g118, g119-g125) x7
    c: Coincident(g126,g95)
    c: InternalAlignment(g118-g125 -> g126) x8
    c: InternalAlignment(g127-g132 -> g126) x6
    c: Coincident(g133,g94)
    c: Block(g126)
    c: Block(g133)
    c: Coincident(g134,g133)
    c: Coincident(g134,g89)
    c: Vertical(g134)
    c: Horizontal(g135)
    c: Block(g135)
    c: Horizontal(g136)
    c: Equal(g88,g136) = 4.14
    c: Horizontal(g137)
    c: Equal(g136,g137) = 4.14
    c: Block(g137)
    c: Block(g136)
    c: Coincident(g138,g135)
    c: Vertical(g138)
    c: Equal(g90,g138) = 11.88
    c: Coincident(g139,g138)
    c: Horizontal(g139)
    c: Coincident(g140,g139)
    c: Vertical(g140)
    c: Equal(g91,g139) = 4.03
    c: Equal(g92,g140) = 1.9
    c: Coincident(g141,g135)
    c: Vertical(g141)
    c: Vertical(g142)
    c: Coincident(g142,g136)
    c: Equal(g93,g141) = 5.8
    c: Equal(g94,g142) = 5.8
    c: Vertical(g143)
    c: Coincident(g143,g136)
    c: Equal(g95,g143) = 6.9
    c: Coincident(g149,g140)
    c: Equal(g96,g144) = 1
    c: Equal(g144, g145-g148) x4
    c: InternalAlignment(g144-g148 -> g149) x5
    c: InternalAlignment(g150-g158 -> g149) x9
    c: Block(g149)
    c: Block(g159)
    c: Coincident(g168,g141)
    c: Equal(g118,g160) = 1
    c: Equal(g160, g161-g167) x7
    c: Coincident(g168,g143)
    c: InternalAlignment(g160-g167 -> g168) x8
    c: InternalAlignment(g169-g174 -> g168) x6
    c: Coincident(g175,g142)
    c: Block(g168)
    c: Block(g175)
    c: Coincident(g176,g175)
    c: Coincident(g176,g137)
    c: Vertical(g176)
    c: Coincident(g177,g137)
    c: Vertical(g177)
    c: Coincident(g178,g177)
    c: Coincident(g178,g159)
    c: InternalAlignment(g179,g178)
    c: InternalAlignment(g180,g178)
    c: Block(g178)
    c: Vertical(g181)
    c: Coincident(g181,g89)
    c: Block(g5)
    c: Coincident(g182,g1)
    c: Coincident(g182,g5)
    c: Horizontal(g182)
    c: Coincident(g186,g117)
    c: Weight(g183) = 1
    c: Equal(g183,g184)
    c: Equal(g183,g185)
    c: Coincident(g186,g181)
    c: InternalAlignment(g183,g186)
    c: InternalAlignment(g184,g186)
    c: InternalAlignment(g185,g186)
    c: InternalAlignment(g187,g186)
    c: InternalAlignment(g188,g186)
    c: Block(g186)
    c: InternalAlignment(g190,g189)
    c: InternalAlignment(g191,g189)
    c: Block(g189)
    c: InternalAlignment(g193,g192)
    c: InternalAlignment(g194,g192)
    c: Block(g192)
    c: Horizontal(g195)
    c: Block(g195)
    c: Coincident(g196,g195)
    c: Vertical(g196)
    c: Block(g196)
    c: Distance(g195) = 3.71244
    c: Coincident(g197,g196)
    c: Horizontal(g197)
    c: Distance(g197) = 4.1
    c: Coincident(g198,g192)
    c: Coincident(g198,g197)
    c: Vertical(g198)
    c: Block(g198)
    c: Coincident(g199,g192)
    c: Coincident(g199,g195)
    c: Vertical(g199)
    c: Block(g199)
    c: Horizontal(g200)
    c: Block(g200)
    c: Coincident(g201,g200)
    c: Vertical(g201)
    c: Block(g201)
    c: Coincident(g202,g201)
    c: Horizontal(g202)
    c: Block(g202)
    c: Coincident(g203,g202)
    c: Vertical(g203)
    c: Block(g203)
    c: Coincident(g204,g200)
    c: Vertical(g204)
    c: Block(g204)
    c: Coincident(g215,g203)
    c: Weight(g206) = 1
    c: Equal(g206, g207-g214) x8
    c: Coincident(g215,g205)
    c: InternalAlignment(g206-g214 -> g215) x9
    c: InternalAlignment(g216-g222 -> g215) x7
    c: Coincident(g233,g204)
    c: Weight(g223) = 1
    c: Equal(g223, g224-g232) x9
    c: Coincident(g233,g205)
    c: InternalAlignment(g223-g232 -> g233) x10
    c: InternalAlignment(g234-g241 -> g233) x8
    c: Vertical(g205)
    c: Block(g205)
    c: Block(g215)
    c: Block(g233)
    c: Horizontal(g242)
    c: Horizontal(g243)
    c: Block(g242)
    c: Block(g243)
    c: Vertical(g244)
    c: Block(g244)
    c: Coincident(g270,g243)
    c: Weight(g245) = 1
    c: Equal(g245, g246-g269) x24
    c: Coincident(g270,g244)
    c: InternalAlignment(g245-g269 -> g270) x25
    c: InternalAlignment(g271-g293 -> g270) x23
    c: Block(g270)
FEATURE [PartDesign::Body] Body
  Group = -> [Sketch083]
  Origin = -> Origin
FEATURE [Sketcher::SketchObject] Sketch084
  FullyConstrained = true
  MapMode = 5
  Support = -> [XY_Plane001]
FEATURE [PartDesign::Body] Body001
  Group = -> [Sketch084]
  Origin = -> Origin001
